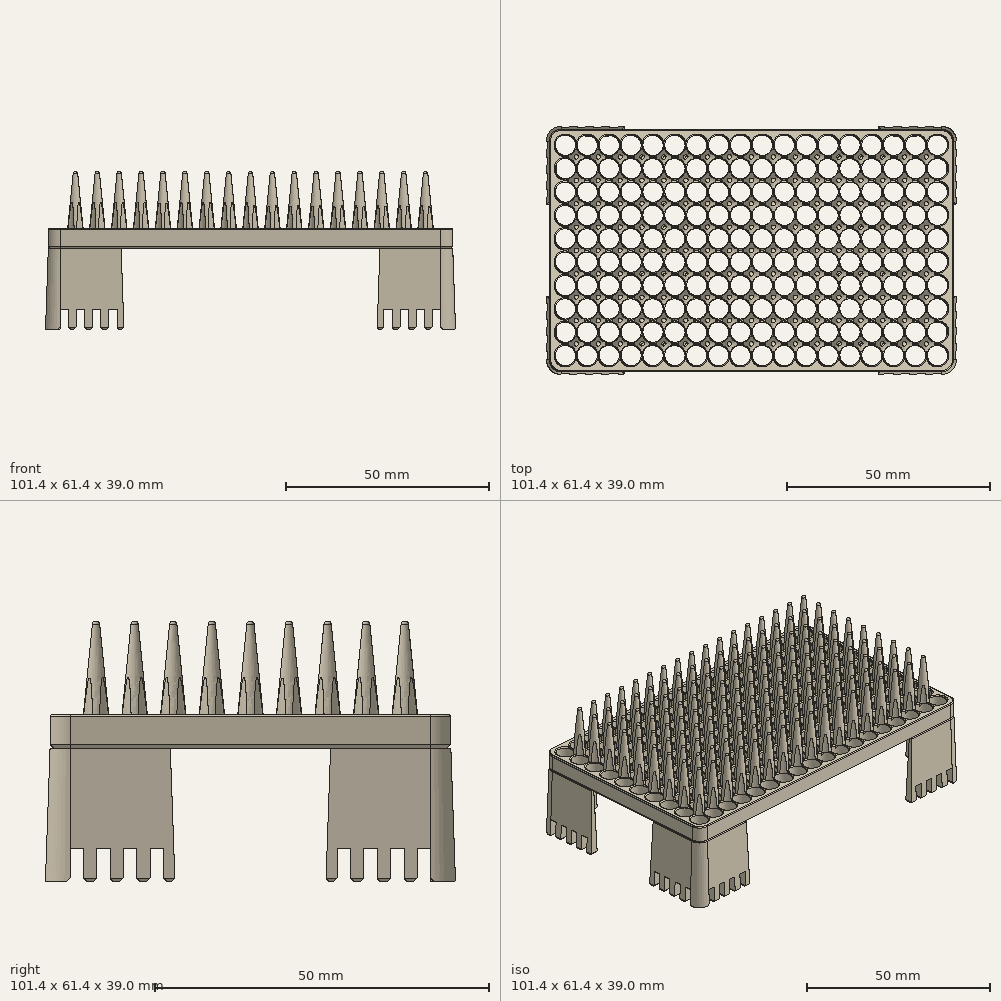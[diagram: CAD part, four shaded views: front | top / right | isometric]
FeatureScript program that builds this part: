
annotation { "Feature Type Name" : "Feature", "Feature Type Description" : "" }
export const myFeature = defineFeature(function(context is Context, id is Id, definition is map)
    precondition{}
    {
        {
            var Q0;
            Q0=qCreatedBy(makeId("Top.planeOp"),FACE);
            var sketch = newSketch(context, id + "F0", { "sketchPlane" : qUnion([Q0])});
            skLineSegment(sketch, "E0.bottom", {"start": v(-47, 30) * mm, "end": v(47, 30) * mm});
            skLineSegment(sketch, "E0.top", {"start": v(-47, -30) * mm, "end": v(47, -30) * mm});
            skLineSegment(sketch, "E0.left", {"start": v(-50, 27) * mm, "end": v(-50, -27) * mm});
            skLineSegment(sketch, "E0.right", {"start": v(50, 27) * mm, "end": v(50, -27) * mm});
            skPoint(sketch, "E1", {"position": v(-46, 26) * mm});
            skPoint(sketch, "E2.0.1.0", {"position": v(-46, 20.22) * mm});
            skPoint(sketch, "E2.0.2.0", {"position": v(-46, 14.45) * mm});
            skPoint(sketch, "E2.0.3.0", {"position": v(-46, 8.67) * mm});
            skPoint(sketch, "E2.0.4.0", {"position": v(-46, 2.9) * mm});
            skPoint(sketch, "E2.0.5.0", {"position": v(-46, -2.89) * mm});
            skPoint(sketch, "E2.0.6.0", {"position": v(-46, -8.66) * mm});
            skPoint(sketch, "E2.0.7.0", {"position": v(-46, -14.44) * mm});
            skPoint(sketch, "E2.0.8.0", {"position": v(-46, -20.22) * mm});
            skPoint(sketch, "E2.0.9.0", {"position": v(-46, -26) * mm});
            skPoint(sketch, "E2.1.0.0", {"position": v(-40.59, 26) * mm});
            skPoint(sketch, "E2.1.1.0", {"position": v(-40.59, 20.22) * mm});
            skPoint(sketch, "E2.1.2.0", {"position": v(-40.59, 14.45) * mm});
            skPoint(sketch, "E2.1.3.0", {"position": v(-40.59, 8.67) * mm});
            skPoint(sketch, "E2.1.4.0", {"position": v(-40.59, 2.9) * mm});
            skPoint(sketch, "E2.1.5.0", {"position": v(-40.59, -2.89) * mm});
            skPoint(sketch, "E2.1.6.0", {"position": v(-40.59, -8.66) * mm});
            skPoint(sketch, "E2.1.7.0", {"position": v(-40.59, -14.44) * mm});
            skPoint(sketch, "E2.1.8.0", {"position": v(-40.59, -20.22) * mm});
            skPoint(sketch, "E2.1.9.0", {"position": v(-40.59, -26) * mm});
            skPoint(sketch, "E2.2.0.0", {"position": v(-35.18, 26) * mm});
            skPoint(sketch, "E2.2.1.0", {"position": v(-35.18, 20.22) * mm});
            skPoint(sketch, "E2.2.2.0", {"position": v(-35.18, 14.45) * mm});
            skPoint(sketch, "E2.2.3.0", {"position": v(-35.18, 8.67) * mm});
            skPoint(sketch, "E2.2.4.0", {"position": v(-35.18, 2.9) * mm});
            skPoint(sketch, "E2.2.5.0", {"position": v(-35.18, -2.89) * mm});
            skPoint(sketch, "E2.2.6.0", {"position": v(-35.18, -8.66) * mm});
            skPoint(sketch, "E2.2.7.0", {"position": v(-35.18, -14.44) * mm});
            skPoint(sketch, "E2.2.8.0", {"position": v(-35.18, -20.22) * mm});
            skPoint(sketch, "E2.2.9.0", {"position": v(-35.18, -26) * mm});
            skPoint(sketch, "E2.3.0.0", {"position": v(-29.76, 26) * mm});
            skPoint(sketch, "E2.3.1.0", {"position": v(-29.76, 20.22) * mm});
            skPoint(sketch, "E2.3.2.0", {"position": v(-29.76, 14.45) * mm});
            skPoint(sketch, "E2.3.3.0", {"position": v(-29.76, 8.67) * mm});
            skPoint(sketch, "E2.3.4.0", {"position": v(-29.76, 2.9) * mm});
            skPoint(sketch, "E2.3.5.0", {"position": v(-29.76, -2.89) * mm});
            skPoint(sketch, "E2.3.6.0", {"position": v(-29.76, -8.66) * mm});
            skPoint(sketch, "E2.3.7.0", {"position": v(-29.76, -14.44) * mm});
            skPoint(sketch, "E2.3.8.0", {"position": v(-29.76, -20.22) * mm});
            skPoint(sketch, "E2.3.9.0", {"position": v(-29.76, -26) * mm});
            skPoint(sketch, "E2.4.0.0", {"position": v(-24.35, 26) * mm});
            skPoint(sketch, "E2.4.1.0", {"position": v(-24.35, 20.22) * mm});
            skPoint(sketch, "E2.4.2.0", {"position": v(-24.35, 14.45) * mm});
            skPoint(sketch, "E2.4.3.0", {"position": v(-24.35, 8.67) * mm});
            skPoint(sketch, "E2.4.4.0", {"position": v(-24.35, 2.9) * mm});
            skPoint(sketch, "E2.4.5.0", {"position": v(-24.35, -2.89) * mm});
            skPoint(sketch, "E2.4.6.0", {"position": v(-24.35, -8.66) * mm});
            skPoint(sketch, "E2.4.7.0", {"position": v(-24.35, -14.44) * mm});
            skPoint(sketch, "E2.4.8.0", {"position": v(-24.35, -20.22) * mm});
            skPoint(sketch, "E2.4.9.0", {"position": v(-24.35, -26) * mm});
            skPoint(sketch, "E2.5.0.0", {"position": v(-18.94, 26) * mm});
            skPoint(sketch, "E2.5.1.0", {"position": v(-18.94, 20.22) * mm});
            skPoint(sketch, "E2.5.2.0", {"position": v(-18.94, 14.45) * mm});
            skPoint(sketch, "E2.5.3.0", {"position": v(-18.94, 8.67) * mm});
            skPoint(sketch, "E2.5.4.0", {"position": v(-18.94, 2.9) * mm});
            skPoint(sketch, "E2.5.5.0", {"position": v(-18.94, -2.89) * mm});
            skPoint(sketch, "E2.5.6.0", {"position": v(-18.94, -8.66) * mm});
            skPoint(sketch, "E2.5.7.0", {"position": v(-18.94, -14.44) * mm});
            skPoint(sketch, "E2.5.8.0", {"position": v(-18.94, -20.22) * mm});
            skPoint(sketch, "E2.5.9.0", {"position": v(-18.94, -26) * mm});
            skPoint(sketch, "E2.6.0.0", {"position": v(-13.53, 26) * mm});
            skPoint(sketch, "E2.6.1.0", {"position": v(-13.53, 20.22) * mm});
            skPoint(sketch, "E2.6.2.0", {"position": v(-13.53, 14.45) * mm});
            skPoint(sketch, "E2.6.3.0", {"position": v(-13.53, 8.67) * mm});
            skPoint(sketch, "E2.6.4.0", {"position": v(-13.53, 2.9) * mm});
            skPoint(sketch, "E2.6.5.0", {"position": v(-13.53, -2.89) * mm});
            skPoint(sketch, "E2.6.6.0", {"position": v(-13.53, -8.66) * mm});
            skPoint(sketch, "E2.6.7.0", {"position": v(-13.53, -14.44) * mm});
            skPoint(sketch, "E2.6.8.0", {"position": v(-13.53, -20.22) * mm});
            skPoint(sketch, "E2.6.9.0", {"position": v(-13.53, -26) * mm});
            skPoint(sketch, "E2.7.0.0", {"position": v(-8.12, 26) * mm});
            skPoint(sketch, "E2.7.1.0", {"position": v(-8.12, 20.22) * mm});
            skPoint(sketch, "E2.7.2.0", {"position": v(-8.12, 14.45) * mm});
            skPoint(sketch, "E2.7.3.0", {"position": v(-8.12, 8.67) * mm});
            skPoint(sketch, "E2.7.4.0", {"position": v(-8.12, 2.9) * mm});
            skPoint(sketch, "E2.7.5.0", {"position": v(-8.12, -2.89) * mm});
            skPoint(sketch, "E2.7.6.0", {"position": v(-8.12, -8.66) * mm});
            skPoint(sketch, "E2.7.7.0", {"position": v(-8.12, -14.44) * mm});
            skPoint(sketch, "E2.7.8.0", {"position": v(-8.12, -20.22) * mm});
            skPoint(sketch, "E2.7.9.0", {"position": v(-8.12, -26) * mm});
            skPoint(sketch, "E2.8.0.0", {"position": v(-2.7, 26) * mm});
            skPoint(sketch, "E2.8.1.0", {"position": v(-2.7, 20.22) * mm});
            skPoint(sketch, "E2.8.2.0", {"position": v(-2.7, 14.45) * mm});
            skPoint(sketch, "E2.8.3.0", {"position": v(-2.7, 8.67) * mm});
            skPoint(sketch, "E2.8.4.0", {"position": v(-2.7, 2.9) * mm});
            skPoint(sketch, "E2.8.5.0", {"position": v(-2.7, -2.89) * mm});
            skPoint(sketch, "E2.8.6.0", {"position": v(-2.7, -8.66) * mm});
            skPoint(sketch, "E2.8.7.0", {"position": v(-2.7, -14.44) * mm});
            skPoint(sketch, "E2.8.8.0", {"position": v(-2.7, -20.22) * mm});
            skPoint(sketch, "E2.8.9.0", {"position": v(-2.7, -26) * mm});
            skPoint(sketch, "E2.9.0.0", {"position": v(2.7, 26) * mm});
            skPoint(sketch, "E2.9.1.0", {"position": v(2.7, 20.22) * mm});
            skPoint(sketch, "E2.9.2.0", {"position": v(2.7, 14.45) * mm});
            skPoint(sketch, "E2.9.3.0", {"position": v(2.7, 8.67) * mm});
            skPoint(sketch, "E2.9.4.0", {"position": v(2.7, 2.9) * mm});
            skPoint(sketch, "E2.9.5.0", {"position": v(2.7, -2.89) * mm});
            skPoint(sketch, "E2.9.6.0", {"position": v(2.7, -8.66) * mm});
            skPoint(sketch, "E2.9.7.0", {"position": v(2.7, -14.44) * mm});
            skPoint(sketch, "E2.9.8.0", {"position": v(2.7, -20.22) * mm});
            skPoint(sketch, "E2.9.9.0", {"position": v(2.7, -26) * mm});
            skPoint(sketch, "E2.10.0.0", {"position": v(8.12, 26) * mm});
            skPoint(sketch, "E2.10.1.0", {"position": v(8.12, 20.22) * mm});
            skPoint(sketch, "E2.10.2.0", {"position": v(8.12, 14.45) * mm});
            skPoint(sketch, "E2.10.3.0", {"position": v(8.12, 8.67) * mm});
            skPoint(sketch, "E2.10.4.0", {"position": v(8.12, 2.9) * mm});
            skPoint(sketch, "E2.10.5.0", {"position": v(8.12, -2.89) * mm});
            skPoint(sketch, "E2.10.6.0", {"position": v(8.12, -8.66) * mm});
            skPoint(sketch, "E2.10.7.0", {"position": v(8.12, -14.44) * mm});
            skPoint(sketch, "E2.10.8.0", {"position": v(8.12, -20.22) * mm});
            skPoint(sketch, "E2.10.9.0", {"position": v(8.12, -26) * mm});
            skPoint(sketch, "E2.11.0.0", {"position": v(13.53, 26) * mm});
            skPoint(sketch, "E2.11.1.0", {"position": v(13.53, 20.22) * mm});
            skPoint(sketch, "E2.11.2.0", {"position": v(13.53, 14.45) * mm});
            skPoint(sketch, "E2.11.3.0", {"position": v(13.53, 8.67) * mm});
            skPoint(sketch, "E2.11.4.0", {"position": v(13.53, 2.9) * mm});
            skPoint(sketch, "E2.11.5.0", {"position": v(13.53, -2.89) * mm});
            skPoint(sketch, "E2.11.6.0", {"position": v(13.53, -8.66) * mm});
            skPoint(sketch, "E2.11.7.0", {"position": v(13.53, -14.44) * mm});
            skPoint(sketch, "E2.11.8.0", {"position": v(13.53, -20.22) * mm});
            skPoint(sketch, "E2.11.9.0", {"position": v(13.53, -26) * mm});
            skPoint(sketch, "E2.12.0.0", {"position": v(18.94, 26) * mm});
            skPoint(sketch, "E2.12.1.0", {"position": v(18.94, 20.22) * mm});
            skPoint(sketch, "E2.12.2.0", {"position": v(18.94, 14.45) * mm});
            skPoint(sketch, "E2.12.3.0", {"position": v(18.94, 8.67) * mm});
            skPoint(sketch, "E2.12.4.0", {"position": v(18.94, 2.9) * mm});
            skPoint(sketch, "E2.12.5.0", {"position": v(18.94, -2.89) * mm});
            skPoint(sketch, "E2.12.6.0", {"position": v(18.94, -8.66) * mm});
            skPoint(sketch, "E2.12.7.0", {"position": v(18.94, -14.44) * mm});
            skPoint(sketch, "E2.12.8.0", {"position": v(18.94, -20.22) * mm});
            skPoint(sketch, "E2.12.9.0", {"position": v(18.94, -26) * mm});
            skPoint(sketch, "E2.13.0.0", {"position": v(24.36, 26) * mm});
            skPoint(sketch, "E2.13.1.0", {"position": v(24.36, 20.22) * mm});
            skPoint(sketch, "E2.13.2.0", {"position": v(24.36, 14.45) * mm});
            skPoint(sketch, "E2.13.3.0", {"position": v(24.36, 8.67) * mm});
            skPoint(sketch, "E2.13.4.0", {"position": v(24.36, 2.9) * mm});
            skPoint(sketch, "E2.13.5.0", {"position": v(24.36, -2.89) * mm});
            skPoint(sketch, "E2.13.6.0", {"position": v(24.36, -8.66) * mm});
            skPoint(sketch, "E2.13.7.0", {"position": v(24.36, -14.44) * mm});
            skPoint(sketch, "E2.13.8.0", {"position": v(24.36, -20.22) * mm});
            skPoint(sketch, "E2.13.9.0", {"position": v(24.36, -26) * mm});
            skPoint(sketch, "E2.14.0.0", {"position": v(29.77, 26) * mm});
            skPoint(sketch, "E2.14.1.0", {"position": v(29.77, 20.22) * mm});
            skPoint(sketch, "E2.14.2.0", {"position": v(29.77, 14.45) * mm});
            skPoint(sketch, "E2.14.3.0", {"position": v(29.77, 8.67) * mm});
            skPoint(sketch, "E2.14.4.0", {"position": v(29.77, 2.9) * mm});
            skPoint(sketch, "E2.14.5.0", {"position": v(29.77, -2.89) * mm});
            skPoint(sketch, "E2.14.6.0", {"position": v(29.77, -8.66) * mm});
            skPoint(sketch, "E2.14.7.0", {"position": v(29.77, -14.44) * mm});
            skPoint(sketch, "E2.14.8.0", {"position": v(29.77, -20.22) * mm});
            skPoint(sketch, "E2.14.9.0", {"position": v(29.77, -26) * mm});
            skPoint(sketch, "E2.15.0.0", {"position": v(35.18, 26) * mm});
            skPoint(sketch, "E2.15.1.0", {"position": v(35.18, 20.22) * mm});
            skPoint(sketch, "E2.15.2.0", {"position": v(35.18, 14.45) * mm});
            skPoint(sketch, "E2.15.3.0", {"position": v(35.18, 8.67) * mm});
            skPoint(sketch, "E2.15.4.0", {"position": v(35.18, 2.9) * mm});
            skPoint(sketch, "E2.15.5.0", {"position": v(35.18, -2.89) * mm});
            skPoint(sketch, "E2.15.6.0", {"position": v(35.18, -8.66) * mm});
            skPoint(sketch, "E2.15.7.0", {"position": v(35.18, -14.44) * mm});
            skPoint(sketch, "E2.15.8.0", {"position": v(35.18, -20.22) * mm});
            skPoint(sketch, "E2.15.9.0", {"position": v(35.18, -26) * mm});
            skPoint(sketch, "E2.16.0.0", {"position": v(40.6, 26) * mm});
            skPoint(sketch, "E2.16.1.0", {"position": v(40.6, 20.22) * mm});
            skPoint(sketch, "E2.16.2.0", {"position": v(40.6, 14.45) * mm});
            skPoint(sketch, "E2.16.3.0", {"position": v(40.6, 8.67) * mm});
            skPoint(sketch, "E2.16.4.0", {"position": v(40.6, 2.9) * mm});
            skPoint(sketch, "E2.16.5.0", {"position": v(40.6, -2.89) * mm});
            skPoint(sketch, "E2.16.6.0", {"position": v(40.6, -8.66) * mm});
            skPoint(sketch, "E2.16.7.0", {"position": v(40.6, -14.44) * mm});
            skPoint(sketch, "E2.16.8.0", {"position": v(40.6, -20.22) * mm});
            skPoint(sketch, "E2.16.9.0", {"position": v(40.6, -26) * mm});
            skPoint(sketch, "E2.17.0.0", {"position": v(46, 26) * mm});
            skPoint(sketch, "E2.17.1.0", {"position": v(46, 20.22) * mm});
            skPoint(sketch, "E2.17.2.0", {"position": v(46, 14.45) * mm});
            skPoint(sketch, "E2.17.3.0", {"position": v(46, 8.67) * mm});
            skPoint(sketch, "E2.17.4.0", {"position": v(46, 2.9) * mm});
            skPoint(sketch, "E2.17.5.0", {"position": v(46, -2.89) * mm});
            skPoint(sketch, "E2.17.6.0", {"position": v(46, -8.66) * mm});
            skPoint(sketch, "E2.17.7.0", {"position": v(46, -14.44) * mm});
            skPoint(sketch, "E2.17.8.0", {"position": v(46, -20.22) * mm});
            skPoint(sketch, "E2.17.9.0", {"position": v(46, -26) * mm});
            skLineSegment(sketch, "E2.direction1", {"start": v(-46, 26) * mm, "end": v(-40.59, 26) * mm, "construction": true});
            skLineSegment(sketch, "E2.direction2", {"start": v(-46, 26) * mm, "end": v(-46, 20.22) * mm, "construction": true});
            skPoint(sketch, "E3.visualSharp", {"position": v(-50, 30) * mm});
            skArc(sketch, "E3.filletArc", {"start": v(-47, 30) * mm, "mid": v(-49.12, 29.12) * mm, "end": v(-50, 27) * mm});
            skPoint(sketch, "E4.visualSharp", {"position": v(-50, -30) * mm});
            skArc(sketch, "E4.filletArc", {"start": v(-50, -27) * mm, "mid": v(-49.12, -29.12) * mm, "end": v(-47, -30) * mm});
            skPoint(sketch, "E5.visualSharp", {"position": v(50, 30) * mm});
            skArc(sketch, "E5.filletArc", {"start": v(50, 27) * mm, "mid": v(49.12, 29.12) * mm, "end": v(47, 30) * mm});
            skPoint(sketch, "E6.visualSharp", {"position": v(50, -30) * mm});
            skArc(sketch, "E6.filletArc", {"start": v(47, -30) * mm, "mid": v(49.12, -29.12) * mm, "end": v(50, -27) * mm});
            skCircle(sketch, "E7", {"center": v(-46, 26) * mm, "radius": 2.5 * mm});
            skCircle(sketch, "E8", {"center": v(-40.59, 26) * mm, "radius": 2.5 * mm});
            skCircle(sketch, "E9", {"center": v(-35.18, 26) * mm, "radius": 2.5 * mm});
            skCircle(sketch, "E10", {"center": v(-29.76, 26) * mm, "radius": 2.5 * mm});
            skCircle(sketch, "E11", {"center": v(-24.35, 26) * mm, "radius": 2.5 * mm});
            skCircle(sketch, "E12", {"center": v(-18.94, 26) * mm, "radius": 2.5 * mm});
            skCircle(sketch, "E13", {"center": v(-18.94, 20.22) * mm, "radius": 2.5 * mm});
            skCircle(sketch, "E14", {"center": v(-24.35, 20.22) * mm, "radius": 2.5 * mm});
            skCircle(sketch, "E15", {"center": v(-29.76, 20.22) * mm, "radius": 2.5 * mm});
            skCircle(sketch, "E16", {"center": v(-35.18, 20.22) * mm, "radius": 2.5 * mm});
            skCircle(sketch, "E17", {"center": v(-40.59, 20.22) * mm, "radius": 2.5 * mm});
            skCircle(sketch, "E18", {"center": v(-40.59, 14.45) * mm, "radius": 2.5 * mm});
            skCircle(sketch, "E19", {"center": v(-35.18, 14.45) * mm, "radius": 2.5 * mm});
            skCircle(sketch, "E20", {"center": v(-29.76, 14.45) * mm, "radius": 2.5 * mm});
            skCircle(sketch, "E21", {"center": v(-24.35, 14.45) * mm, "radius": 2.5 * mm});
            skCircle(sketch, "E22", {"center": v(-18.94, 14.45) * mm, "radius": 2.5 * mm});
            skCircle(sketch, "E23", {"center": v(-13.53, 26) * mm, "radius": 2.5 * mm});
            skCircle(sketch, "E24", {"center": v(-13.53, 20.22) * mm, "radius": 2.5 * mm});
            skCircle(sketch, "E25", {"center": v(-13.53, 14.45) * mm, "radius": 2.5 * mm});
            skCircle(sketch, "E26", {"center": v(-46, 20.22) * mm, "radius": 2.5 * mm});
            skCircle(sketch, "E27", {"center": v(-46, 14.45) * mm, "radius": 2.5 * mm});
            skCircle(sketch, "E28", {"center": v(-46, 8.67) * mm, "radius": 2.5 * mm});
            skCircle(sketch, "E29", {"center": v(-40.59, 8.67) * mm, "radius": 2.5 * mm});
            skCircle(sketch, "E30", {"center": v(-35.18, 8.67) * mm, "radius": 2.5 * mm});
            skCircle(sketch, "E31", {"center": v(-29.76, 8.67) * mm, "radius": 2.5 * mm});
            skCircle(sketch, "E32", {"center": v(-24.35, 8.67) * mm, "radius": 2.5 * mm});
            skCircle(sketch, "E33", {"center": v(-18.94, 8.67) * mm, "radius": 2.5 * mm});
            skCircle(sketch, "E34", {"center": v(-13.53, 8.67) * mm, "radius": 2.5 * mm});
            skCircle(sketch, "E35", {"center": v(-13.53, 2.9) * mm, "radius": 2.5 * mm});
            skCircle(sketch, "E36", {"center": v(-18.94, 2.9) * mm, "radius": 2.5 * mm});
            skCircle(sketch, "E37", {"center": v(-24.35, 2.9) * mm, "radius": 2.5 * mm});
            skCircle(sketch, "E38", {"center": v(-29.76, 2.9) * mm, "radius": 2.5 * mm});
            skCircle(sketch, "E39", {"center": v(-35.18, 2.9) * mm, "radius": 2.5 * mm});
            skCircle(sketch, "E40", {"center": v(-40.59, 2.9) * mm, "radius": 2.5 * mm});
            skCircle(sketch, "E41", {"center": v(-46, 2.9) * mm, "radius": 2.5 * mm});
            skCircle(sketch, "E42", {"center": v(-8.12, 26) * mm, "radius": 2.5 * mm});
            skCircle(sketch, "E43", {"center": v(-2.7, 26) * mm, "radius": 2.5 * mm});
            skCircle(sketch, "E44", {"center": v(-8.12, 20.22) * mm, "radius": 2.5 * mm});
            skCircle(sketch, "E45", {"center": v(-8.12, 14.45) * mm, "radius": 2.5 * mm});
            skCircle(sketch, "E46", {"center": v(-2.7, 20.22) * mm, "radius": 2.5 * mm});
            skCircle(sketch, "E47", {"center": v(-2.7, 14.45) * mm, "radius": 2.5 * mm});
            skCircle(sketch, "E48", {"center": v(2.7, 26) * mm, "radius": 2.5 * mm});
            skCircle(sketch, "E49", {"center": v(2.7, 20.22) * mm, "radius": 2.5 * mm});
            skCircle(sketch, "E50", {"center": v(8.12, 26) * mm, "radius": 2.5 * mm});
            skCircle(sketch, "E51", {"center": v(13.53, 26) * mm, "radius": 2.5 * mm});
            skCircle(sketch, "E52", {"center": v(18.94, 26) * mm, "radius": 2.5 * mm});
            skCircle(sketch, "E53", {"center": v(24.36, 26) * mm, "radius": 2.5 * mm});
            skCircle(sketch, "E54", {"center": v(29.77, 26) * mm, "radius": 2.5 * mm});
            skCircle(sketch, "E55", {"center": v(35.18, 26) * mm, "radius": 2.5 * mm});
            skCircle(sketch, "E56", {"center": v(40.6, 26) * mm, "radius": 2.5 * mm});
            skCircle(sketch, "E57", {"center": v(46, 26) * mm, "radius": 2.5 * mm});
            skCircle(sketch, "E58", {"center": v(46, 20.22) * mm, "radius": 2.5 * mm});
            skCircle(sketch, "E59", {"center": v(40.6, 20.22) * mm, "radius": 2.5 * mm});
            skCircle(sketch, "E60", {"center": v(35.18, 20.22) * mm, "radius": 2.5 * mm});
            skCircle(sketch, "E61", {"center": v(29.77, 20.22) * mm, "radius": 2.5 * mm});
            skCircle(sketch, "E62", {"center": v(24.36, 20.22) * mm, "radius": 2.5 * mm});
            skCircle(sketch, "E63", {"center": v(18.94, 20.22) * mm, "radius": 2.5 * mm});
            skCircle(sketch, "E64", {"center": v(13.53, 20.22) * mm, "radius": 2.5 * mm});
            skCircle(sketch, "E65", {"center": v(8.12, 20.22) * mm, "radius": 2.5 * mm});
            skCircle(sketch, "E66", {"center": v(2.7, 14.45) * mm, "radius": 2.5 * mm});
            skCircle(sketch, "E67", {"center": v(8.12, 14.45) * mm, "radius": 2.5 * mm});
            skCircle(sketch, "E68", {"center": v(13.53, 14.45) * mm, "radius": 2.5 * mm});
            skCircle(sketch, "E69", {"center": v(18.94, 14.45) * mm, "radius": 2.5 * mm});
            skCircle(sketch, "E70", {"center": v(24.36, 14.45) * mm, "radius": 2.5 * mm});
            skCircle(sketch, "E71", {"center": v(29.77, 14.45) * mm, "radius": 2.5 * mm});
            skCircle(sketch, "E72", {"center": v(35.18, 14.45) * mm, "radius": 2.5 * mm});
            skCircle(sketch, "E73", {"center": v(40.6, 14.45) * mm, "radius": 2.5 * mm});
            skCircle(sketch, "E74", {"center": v(46, 14.45) * mm, "radius": 2.5 * mm});
            skCircle(sketch, "E75", {"center": v(46, 8.67) * mm, "radius": 2.5 * mm});
            skCircle(sketch, "E76", {"center": v(40.6, 8.67) * mm, "radius": 2.5 * mm});
            skCircle(sketch, "E77", {"center": v(35.18, 8.67) * mm, "radius": 2.5 * mm});
            skCircle(sketch, "E78", {"center": v(29.77, 8.67) * mm, "radius": 2.5 * mm});
            skCircle(sketch, "E79", {"center": v(24.36, 8.67) * mm, "radius": 2.5 * mm});
            skCircle(sketch, "E80", {"center": v(18.94, 8.67) * mm, "radius": 2.5 * mm});
            skCircle(sketch, "E81", {"center": v(13.53, 8.67) * mm, "radius": 2.5 * mm});
            skCircle(sketch, "E82", {"center": v(8.12, 8.67) * mm, "radius": 2.5 * mm});
            skCircle(sketch, "E83", {"center": v(2.7, 8.67) * mm, "radius": 2.5 * mm});
            skCircle(sketch, "E84", {"center": v(-2.7, 8.67) * mm, "radius": 2.5 * mm});
            skCircle(sketch, "E85", {"center": v(-8.12, 8.67) * mm, "radius": 2.5 * mm});
            skCircle(sketch, "E86", {"center": v(-8.12, 2.9) * mm, "radius": 2.5 * mm});
            skCircle(sketch, "E87", {"center": v(-2.7, 2.9) * mm, "radius": 2.5 * mm});
            skCircle(sketch, "E88", {"center": v(2.7, 2.9) * mm, "radius": 2.5 * mm});
            skCircle(sketch, "E89", {"center": v(8.12, 2.9) * mm, "radius": 2.5 * mm});
            skCircle(sketch, "E90", {"center": v(13.53, 2.9) * mm, "radius": 2.5 * mm});
            skCircle(sketch, "E91", {"center": v(18.94, 2.9) * mm, "radius": 2.5 * mm});
            skCircle(sketch, "E92", {"center": v(24.36, 2.9) * mm, "radius": 2.5 * mm});
            skCircle(sketch, "E93", {"center": v(29.77, 2.9) * mm, "radius": 2.5 * mm});
            skCircle(sketch, "E94", {"center": v(35.18, 2.9) * mm, "radius": 2.5 * mm});
            skCircle(sketch, "E95", {"center": v(40.6, 2.9) * mm, "radius": 2.5 * mm});
            skCircle(sketch, "E96", {"center": v(46, 2.9) * mm, "radius": 2.5 * mm});
            skCircle(sketch, "E97", {"center": v(-46, -2.89) * mm, "radius": 2.5 * mm});
            skCircle(sketch, "E98", {"center": v(-40.59, -2.89) * mm, "radius": 2.5 * mm});
            skCircle(sketch, "E99", {"center": v(-35.18, -2.89) * mm, "radius": 2.5 * mm});
            skCircle(sketch, "E100", {"center": v(-29.76, -2.89) * mm, "radius": 2.5 * mm});
            skCircle(sketch, "E101", {"center": v(-24.35, -2.89) * mm, "radius": 2.5 * mm});
            skCircle(sketch, "E102", {"center": v(-18.94, -2.89) * mm, "radius": 2.5 * mm});
            skCircle(sketch, "E103", {"center": v(-13.53, -2.89) * mm, "radius": 2.5 * mm});
            skCircle(sketch, "E104", {"center": v(-8.12, -2.89) * mm, "radius": 2.5 * mm});
            skCircle(sketch, "E105", {"center": v(-2.7, -2.89) * mm, "radius": 2.5 * mm});
            skCircle(sketch, "E106", {"center": v(-2.7, -8.66) * mm, "radius": 2.5 * mm});
            skCircle(sketch, "E107", {"center": v(-24.35, -8.66) * mm, "radius": 2.5 * mm});
            skCircle(sketch, "E108", {"center": v(-18.94, -8.66) * mm, "radius": 2.5 * mm});
            skCircle(sketch, "E109", {"center": v(-13.53, -8.66) * mm, "radius": 2.5 * mm});
            skCircle(sketch, "E110", {"center": v(-8.12, -8.66) * mm, "radius": 2.5 * mm});
            skCircle(sketch, "E111", {"center": v(-35.18, -8.66) * mm, "radius": 2.5 * mm});
            skCircle(sketch, "E112", {"center": v(-29.76, -8.66) * mm, "radius": 2.5 * mm});
            skCircle(sketch, "E113", {"center": v(-35.18, -14.44) * mm, "radius": 2.5 * mm});
            skCircle(sketch, "E114", {"center": v(-29.76, -14.44) * mm, "radius": 2.5 * mm});
            skCircle(sketch, "E115", {"center": v(-24.35, -14.44) * mm, "radius": 2.5 * mm});
            skCircle(sketch, "E116", {"center": v(-18.94, -14.44) * mm, "radius": 2.5 * mm});
            skCircle(sketch, "E117", {"center": v(-13.53, -14.44) * mm, "radius": 2.5 * mm});
            skCircle(sketch, "E118", {"center": v(-8.12, -14.44) * mm, "radius": 2.5 * mm});
            skCircle(sketch, "E119", {"center": v(-2.7, -14.44) * mm, "radius": 2.5 * mm});
            skCircle(sketch, "E120", {"center": v(-46, -8.66) * mm, "radius": 2.5 * mm});
            skCircle(sketch, "E121", {"center": v(-40.59, -8.66) * mm, "radius": 2.5 * mm});
            skCircle(sketch, "E122", {"center": v(-46, -14.44) * mm, "radius": 2.5 * mm});
            skCircle(sketch, "E123", {"center": v(-40.59, -14.44) * mm, "radius": 2.5 * mm});
            skCircle(sketch, "E124", {"center": v(-46, -20.22) * mm, "radius": 2.5 * mm});
            skCircle(sketch, "E125", {"center": v(-40.59, -20.22) * mm, "radius": 2.5 * mm});
            skCircle(sketch, "E126", {"center": v(-46, -26) * mm, "radius": 2.5 * mm});
            skCircle(sketch, "E127", {"center": v(-40.59, -26) * mm, "radius": 2.5 * mm});
            skCircle(sketch, "E128", {"center": v(-35.18, -26) * mm, "radius": 2.5 * mm});
            skCircle(sketch, "E129", {"center": v(-35.18, -20.22) * mm, "radius": 2.5 * mm});
            skCircle(sketch, "E130", {"center": v(-29.76, -20.22) * mm, "radius": 2.5 * mm});
            skCircle(sketch, "E131", {"center": v(-29.76, -26) * mm, "radius": 2.5 * mm});
            skCircle(sketch, "E132", {"center": v(-24.35, -26) * mm, "radius": 2.5 * mm});
            skCircle(sketch, "E133", {"center": v(-24.35, -20.22) * mm, "radius": 2.5 * mm});
            skCircle(sketch, "E134", {"center": v(-18.94, -20.22) * mm, "radius": 2.5 * mm});
            skCircle(sketch, "E135", {"center": v(-18.94, -26) * mm, "radius": 2.5 * mm});
            skCircle(sketch, "E136", {"center": v(-13.53, -20.22) * mm, "radius": 2.5 * mm});
            skCircle(sketch, "E137", {"center": v(-8.12, -20.22) * mm, "radius": 2.5 * mm});
            skCircle(sketch, "E138", {"center": v(-2.7, -20.22) * mm, "radius": 2.5 * mm});
            skCircle(sketch, "E139", {"center": v(-2.7, -26) * mm, "radius": 2.5 * mm});
            skCircle(sketch, "E140", {"center": v(-8.12, -26) * mm, "radius": 2.5 * mm});
            skCircle(sketch, "E141", {"center": v(-13.53, -26) * mm, "radius": 2.5 * mm});
            skCircle(sketch, "E142", {"center": v(2.7, -2.89) * mm, "radius": 2.5 * mm});
            skCircle(sketch, "E143", {"center": v(8.12, -2.89) * mm, "radius": 2.5 * mm});
            skCircle(sketch, "E144", {"center": v(13.53, -2.89) * mm, "radius": 2.5 * mm});
            skCircle(sketch, "E145", {"center": v(18.94, -2.89) * mm, "radius": 2.5 * mm});
            skCircle(sketch, "E146", {"center": v(24.36, -2.89) * mm, "radius": 2.5 * mm});
            skCircle(sketch, "E147", {"center": v(29.77, -2.89) * mm, "radius": 2.5 * mm});
            skCircle(sketch, "E148", {"center": v(35.18, -2.89) * mm, "radius": 2.5 * mm});
            skCircle(sketch, "E149", {"center": v(40.6, -2.89) * mm, "radius": 2.5 * mm});
            skCircle(sketch, "E150", {"center": v(46, -2.89) * mm, "radius": 2.5 * mm});
            skCircle(sketch, "E151", {"center": v(46, -8.66) * mm, "radius": 2.5 * mm});
            skCircle(sketch, "E152", {"center": v(40.6, -8.66) * mm, "radius": 2.5 * mm});
            skCircle(sketch, "E153", {"center": v(35.18, -8.66) * mm, "radius": 2.5 * mm});
            skCircle(sketch, "E154", {"center": v(29.77, -8.66) * mm, "radius": 2.5 * mm});
            skCircle(sketch, "E155", {"center": v(24.36, -8.66) * mm, "radius": 2.5 * mm});
            skCircle(sketch, "E156", {"center": v(18.94, -8.66) * mm, "radius": 2.5 * mm});
            skCircle(sketch, "E157", {"center": v(13.53, -8.66) * mm, "radius": 2.5 * mm});
            skCircle(sketch, "E158", {"center": v(8.12, -8.66) * mm, "radius": 2.5 * mm});
            skCircle(sketch, "E159", {"center": v(2.7, -8.66) * mm, "radius": 2.5 * mm});
            skCircle(sketch, "E160", {"center": v(2.7, -14.44) * mm, "radius": 2.5 * mm});
            skCircle(sketch, "E161", {"center": v(8.12, -14.44) * mm, "radius": 2.5 * mm});
            skCircle(sketch, "E162", {"center": v(13.53, -14.44) * mm, "radius": 2.5 * mm});
            skCircle(sketch, "E163", {"center": v(18.94, -14.44) * mm, "radius": 2.5 * mm});
            skCircle(sketch, "E164", {"center": v(24.36, -14.44) * mm, "radius": 2.5 * mm});
            skCircle(sketch, "E165", {"center": v(29.77, -14.44) * mm, "radius": 2.5 * mm});
            skCircle(sketch, "E166", {"center": v(35.18, -14.44) * mm, "radius": 2.5 * mm});
            skCircle(sketch, "E167", {"center": v(40.6, -14.44) * mm, "radius": 2.5 * mm});
            skCircle(sketch, "E168", {"center": v(46, -14.44) * mm, "radius": 2.5 * mm});
            skCircle(sketch, "E169", {"center": v(2.7, -20.22) * mm, "radius": 2.5 * mm});
            skCircle(sketch, "E170", {"center": v(8.12, -20.22) * mm, "radius": 2.5 * mm});
            skCircle(sketch, "E171", {"center": v(13.53, -20.22) * mm, "radius": 2.5 * mm});
            skCircle(sketch, "E172", {"center": v(18.94, -20.22) * mm, "radius": 2.5 * mm});
            skCircle(sketch, "E173", {"center": v(24.36, -20.22) * mm, "radius": 2.5 * mm});
            skCircle(sketch, "E174", {"center": v(29.77, -20.22) * mm, "radius": 2.5 * mm});
            skCircle(sketch, "E175", {"center": v(35.18, -20.22) * mm, "radius": 2.5 * mm});
            skCircle(sketch, "E176", {"center": v(40.6, -20.22) * mm, "radius": 2.5 * mm});
            skCircle(sketch, "E177", {"center": v(46, -20.22) * mm, "radius": 2.5 * mm});
            skCircle(sketch, "E178", {"center": v(2.7, -26) * mm, "radius": 2.5 * mm});
            skCircle(sketch, "E179", {"center": v(8.12, -26) * mm, "radius": 2.5 * mm});
            skCircle(sketch, "E180", {"center": v(13.53, -26) * mm, "radius": 2.5 * mm});
            skCircle(sketch, "E181", {"center": v(18.94, -26) * mm, "radius": 2.5 * mm});
            skCircle(sketch, "E182", {"center": v(24.36, -26) * mm, "radius": 2.5 * mm});
            skCircle(sketch, "E183", {"center": v(29.77, -26) * mm, "radius": 2.5 * mm});
            skCircle(sketch, "E184", {"center": v(35.18, -26) * mm, "radius": 2.5 * mm});
            skCircle(sketch, "E185", {"center": v(40.6, -26) * mm, "radius": 2.5 * mm});
            skCircle(sketch, "E186", {"center": v(46, -26) * mm, "radius": 2.5 * mm});
            skSolve(sketch);
        }
        {
            var Q0;
            Q0=makeQuery(id+"F0.imprint","IMPRINT",FACE,{"disambiguationData":[TD([[makeQuery(id+"F0.imprint","IMPRINT",EDGE,{"derivedFrom":sQuery(id+"F0.wireOp",EDGE,"E0.bottom")}),-1.0]])]});
            var sketch = newSketch(context, id + "F1", { "sketchPlane" : qUnion([Q0])});
            skLineSegment(sketch, "E187", {"start": v(-46, 20.22) * mm, "end": v(-40.59, 26) * mm, "construction": true});
            skLineSegment(sketch, "E188", {"start": v(-46, 26) * mm, "end": v(-40.59, 20.22) * mm, "construction": true});
            skPoint(sketch, "E189", {"position": v(-43.3, 23.11) * mm});
            skLineSegment(sketch, "E190", {"start": v(-46, -20.22) * mm, "end": v(-40.59, -26) * mm, "construction": true});
            skLineSegment(sketch, "E191", {"start": v(-40.59, -20.22) * mm, "end": v(-46, -26) * mm, "construction": true});
            skPoint(sketch, "E192", {"position": v(-43.3, -23.1) * mm});
            skLineSegment(sketch, "E193", {"start": v(40.6, 26) * mm, "end": v(46, 20.22) * mm, "construction": true});
            skLineSegment(sketch, "E194", {"start": v(46, 26) * mm, "end": v(40.6, 20.22) * mm, "construction": true});
            skLineSegment(sketch, "E195", {"start": v(40.6, -20.22) * mm, "end": v(46, -26) * mm, "construction": true});
            skLineSegment(sketch, "E196", {"start": v(46, -20.22) * mm, "end": v(40.6, -26) * mm, "construction": true});
            skPoint(sketch, "E197", {"position": v(43.3, 23.11) * mm});
            skPoint(sketch, "E198", {"position": v(43.3, -23.1) * mm});
            skCircle(sketch, "E199", {"center": v(-43.3, 23.11) * mm, "radius": 2 * mm});
            skLineSegment(sketch, "E200", {"start": v(-40.59, 26) * mm, "end": v(-35.18, 20.22) * mm, "construction": true});
            skLineSegment(sketch, "E201", {"start": v(-35.18, 26) * mm, "end": v(-40.59, 20.22) * mm, "construction": true});
            skPoint(sketch, "E202", {"position": v(-37.88, 23.11) * mm});
            skLineSegment(sketch, "E203", {"start": v(-46, 20.22) * mm, "end": v(-40.59, 14.45) * mm, "construction": true});
            skLineSegment(sketch, "E204", {"start": v(-40.59, 20.22) * mm, "end": v(-46, 14.45) * mm, "construction": true});
            skPoint(sketch, "E205", {"position": v(-43.3, 17.33) * mm});
            skCircle(sketch, "E206.0.1.0", {"center": v(-43.3, 17.33) * mm, "radius": 2 * mm});
            skCircle(sketch, "E206.0.2.0", {"center": v(-43.3, 11.56) * mm, "radius": 2 * mm});
            skCircle(sketch, "E206.0.3.0", {"center": v(-43.3, 5.78) * mm, "radius": 2 * mm});
            skCircle(sketch, "E206.0.4.0", {"center": v(-43.3, 0) * mm, "radius": 2 * mm});
            skCircle(sketch, "E206.0.5.0", {"center": v(-43.3, -5.77) * mm, "radius": 2 * mm});
            skCircle(sketch, "E206.0.6.0", {"center": v(-43.3, -11.55) * mm, "radius": 2 * mm});
            skCircle(sketch, "E206.0.7.0", {"center": v(-43.3, -17.33) * mm, "radius": 2 * mm});
            skCircle(sketch, "E206.0.8.0", {"center": v(-43.3, -23.1) * mm, "radius": 2 * mm});
            skCircle(sketch, "E206.1.0.0", {"center": v(-37.88, 23.11) * mm, "radius": 2 * mm});
            skCircle(sketch, "E206.1.1.0", {"center": v(-37.88, 17.33) * mm, "radius": 2 * mm});
            skCircle(sketch, "E206.1.2.0", {"center": v(-37.88, 11.56) * mm, "radius": 2 * mm});
            skCircle(sketch, "E206.1.3.0", {"center": v(-37.88, 5.78) * mm, "radius": 2 * mm});
            skCircle(sketch, "E206.1.4.0", {"center": v(-37.88, 0) * mm, "radius": 2 * mm});
            skCircle(sketch, "E206.1.5.0", {"center": v(-37.88, -5.77) * mm, "radius": 2 * mm});
            skCircle(sketch, "E206.1.6.0", {"center": v(-37.88, -11.55) * mm, "radius": 2 * mm});
            skCircle(sketch, "E206.1.7.0", {"center": v(-37.88, -17.33) * mm, "radius": 2 * mm});
            skCircle(sketch, "E206.1.8.0", {"center": v(-37.88, -23.1) * mm, "radius": 2 * mm});
            skCircle(sketch, "E206.2.0.0", {"center": v(-32.47, 23.11) * mm, "radius": 2 * mm});
            skCircle(sketch, "E206.2.1.0", {"center": v(-32.47, 17.33) * mm, "radius": 2 * mm});
            skCircle(sketch, "E206.2.2.0", {"center": v(-32.47, 11.56) * mm, "radius": 2 * mm});
            skCircle(sketch, "E206.2.3.0", {"center": v(-32.47, 5.78) * mm, "radius": 2 * mm});
            skCircle(sketch, "E206.2.4.0", {"center": v(-32.47, 0) * mm, "radius": 2 * mm});
            skCircle(sketch, "E206.2.5.0", {"center": v(-32.47, -5.77) * mm, "radius": 2 * mm});
            skCircle(sketch, "E206.2.6.0", {"center": v(-32.47, -11.55) * mm, "radius": 2 * mm});
            skCircle(sketch, "E206.2.7.0", {"center": v(-32.47, -17.33) * mm, "radius": 2 * mm});
            skCircle(sketch, "E206.2.8.0", {"center": v(-32.47, -23.1) * mm, "radius": 2 * mm});
            skCircle(sketch, "E206.3.0.0", {"center": v(-27.06, 23.11) * mm, "radius": 2 * mm});
            skCircle(sketch, "E206.3.1.0", {"center": v(-27.06, 17.33) * mm, "radius": 2 * mm});
            skCircle(sketch, "E206.3.2.0", {"center": v(-27.06, 11.56) * mm, "radius": 2 * mm});
            skCircle(sketch, "E206.3.3.0", {"center": v(-27.06, 5.78) * mm, "radius": 2 * mm});
            skCircle(sketch, "E206.3.4.0", {"center": v(-27.06, 0) * mm, "radius": 2 * mm});
            skCircle(sketch, "E206.3.5.0", {"center": v(-27.06, -5.77) * mm, "radius": 2 * mm});
            skCircle(sketch, "E206.3.6.0", {"center": v(-27.06, -11.55) * mm, "radius": 2 * mm});
            skCircle(sketch, "E206.3.7.0", {"center": v(-27.06, -17.33) * mm, "radius": 2 * mm});
            skCircle(sketch, "E206.3.8.0", {"center": v(-27.06, -23.1) * mm, "radius": 2 * mm});
            skCircle(sketch, "E206.4.0.0", {"center": v(-21.65, 23.11) * mm, "radius": 2 * mm});
            skCircle(sketch, "E206.4.1.0", {"center": v(-21.65, 17.33) * mm, "radius": 2 * mm});
            skCircle(sketch, "E206.4.2.0", {"center": v(-21.65, 11.56) * mm, "radius": 2 * mm});
            skCircle(sketch, "E206.4.3.0", {"center": v(-21.65, 5.78) * mm, "radius": 2 * mm});
            skCircle(sketch, "E206.4.4.0", {"center": v(-21.65, 0) * mm, "radius": 2 * mm});
            skCircle(sketch, "E206.4.5.0", {"center": v(-21.65, -5.77) * mm, "radius": 2 * mm});
            skCircle(sketch, "E206.4.6.0", {"center": v(-21.65, -11.55) * mm, "radius": 2 * mm});
            skCircle(sketch, "E206.4.7.0", {"center": v(-21.65, -17.33) * mm, "radius": 2 * mm});
            skCircle(sketch, "E206.4.8.0", {"center": v(-21.65, -23.1) * mm, "radius": 2 * mm});
            skCircle(sketch, "E206.5.0.0", {"center": v(-16.23, 23.11) * mm, "radius": 2 * mm});
            skCircle(sketch, "E206.5.1.0", {"center": v(-16.23, 17.33) * mm, "radius": 2 * mm});
            skCircle(sketch, "E206.5.2.0", {"center": v(-16.23, 11.56) * mm, "radius": 2 * mm});
            skCircle(sketch, "E206.5.3.0", {"center": v(-16.23, 5.78) * mm, "radius": 2 * mm});
            skCircle(sketch, "E206.5.4.0", {"center": v(-16.23, 0) * mm, "radius": 2 * mm});
            skCircle(sketch, "E206.5.5.0", {"center": v(-16.23, -5.77) * mm, "radius": 2 * mm});
            skCircle(sketch, "E206.5.6.0", {"center": v(-16.23, -11.55) * mm, "radius": 2 * mm});
            skCircle(sketch, "E206.5.7.0", {"center": v(-16.23, -17.33) * mm, "radius": 2 * mm});
            skCircle(sketch, "E206.5.8.0", {"center": v(-16.23, -23.1) * mm, "radius": 2 * mm});
            skCircle(sketch, "E206.6.0.0", {"center": v(-10.82, 23.11) * mm, "radius": 2 * mm});
            skCircle(sketch, "E206.6.1.0", {"center": v(-10.82, 17.33) * mm, "radius": 2 * mm});
            skCircle(sketch, "E206.6.2.0", {"center": v(-10.82, 11.56) * mm, "radius": 2 * mm});
            skCircle(sketch, "E206.6.3.0", {"center": v(-10.82, 5.78) * mm, "radius": 2 * mm});
            skCircle(sketch, "E206.6.4.0", {"center": v(-10.82, 0) * mm, "radius": 2 * mm});
            skCircle(sketch, "E206.6.5.0", {"center": v(-10.82, -5.77) * mm, "radius": 2 * mm});
            skCircle(sketch, "E206.6.6.0", {"center": v(-10.82, -11.55) * mm, "radius": 2 * mm});
            skCircle(sketch, "E206.6.7.0", {"center": v(-10.82, -17.33) * mm, "radius": 2 * mm});
            skCircle(sketch, "E206.6.8.0", {"center": v(-10.82, -23.1) * mm, "radius": 2 * mm});
            skCircle(sketch, "E206.7.0.0", {"center": v(-5.41, 23.11) * mm, "radius": 2 * mm});
            skCircle(sketch, "E206.7.1.0", {"center": v(-5.41, 17.33) * mm, "radius": 2 * mm});
            skCircle(sketch, "E206.7.2.0", {"center": v(-5.41, 11.56) * mm, "radius": 2 * mm});
            skCircle(sketch, "E206.7.3.0", {"center": v(-5.41, 5.78) * mm, "radius": 2 * mm});
            skCircle(sketch, "E206.7.4.0", {"center": v(-5.41, 0) * mm, "radius": 2 * mm});
            skCircle(sketch, "E206.7.5.0", {"center": v(-5.41, -5.77) * mm, "radius": 2 * mm});
            skCircle(sketch, "E206.7.6.0", {"center": v(-5.41, -11.55) * mm, "radius": 2 * mm});
            skCircle(sketch, "E206.7.7.0", {"center": v(-5.41, -17.33) * mm, "radius": 2 * mm});
            skCircle(sketch, "E206.7.8.0", {"center": v(-5.41, -23.1) * mm, "radius": 2 * mm});
            skCircle(sketch, "E206.8.0.0", {"center": v(0, 23.11) * mm, "radius": 2 * mm});
            skCircle(sketch, "E206.8.1.0", {"center": v(0, 17.33) * mm, "radius": 2 * mm});
            skCircle(sketch, "E206.8.2.0", {"center": v(0, 11.56) * mm, "radius": 2 * mm});
            skCircle(sketch, "E206.8.3.0", {"center": v(0, 5.78) * mm, "radius": 2 * mm});
            skCircle(sketch, "E206.8.4.0", {"center": v(0, 0) * mm, "radius": 2 * mm});
            skCircle(sketch, "E206.8.5.0", {"center": v(0, -5.77) * mm, "radius": 2 * mm});
            skCircle(sketch, "E206.8.6.0", {"center": v(0, -11.55) * mm, "radius": 2 * mm});
            skCircle(sketch, "E206.8.7.0", {"center": v(0, -17.33) * mm, "radius": 2 * mm});
            skCircle(sketch, "E206.8.8.0", {"center": v(0, -23.1) * mm, "radius": 2 * mm});
            skCircle(sketch, "E206.9.0.0", {"center": v(5.41, 23.11) * mm, "radius": 2 * mm});
            skCircle(sketch, "E206.9.1.0", {"center": v(5.41, 17.33) * mm, "radius": 2 * mm});
            skCircle(sketch, "E206.9.2.0", {"center": v(5.41, 11.56) * mm, "radius": 2 * mm});
            skCircle(sketch, "E206.9.3.0", {"center": v(5.41, 5.78) * mm, "radius": 2 * mm});
            skCircle(sketch, "E206.9.4.0", {"center": v(5.41, 0) * mm, "radius": 2 * mm});
            skCircle(sketch, "E206.9.5.0", {"center": v(5.41, -5.77) * mm, "radius": 2 * mm});
            skCircle(sketch, "E206.9.6.0", {"center": v(5.41, -11.55) * mm, "radius": 2 * mm});
            skCircle(sketch, "E206.9.7.0", {"center": v(5.41, -17.33) * mm, "radius": 2 * mm});
            skCircle(sketch, "E206.9.8.0", {"center": v(5.41, -23.1) * mm, "radius": 2 * mm});
            skCircle(sketch, "E206.10.0.0", {"center": v(10.83, 23.11) * mm, "radius": 2 * mm});
            skCircle(sketch, "E206.10.1.0", {"center": v(10.83, 17.33) * mm, "radius": 2 * mm});
            skCircle(sketch, "E206.10.2.0", {"center": v(10.83, 11.56) * mm, "radius": 2 * mm});
            skCircle(sketch, "E206.10.3.0", {"center": v(10.83, 5.78) * mm, "radius": 2 * mm});
            skCircle(sketch, "E206.10.4.0", {"center": v(10.83, 0) * mm, "radius": 2 * mm});
            skCircle(sketch, "E206.10.5.0", {"center": v(10.83, -5.77) * mm, "radius": 2 * mm});
            skCircle(sketch, "E206.10.6.0", {"center": v(10.83, -11.55) * mm, "radius": 2 * mm});
            skCircle(sketch, "E206.10.7.0", {"center": v(10.83, -17.33) * mm, "radius": 2 * mm});
            skCircle(sketch, "E206.10.8.0", {"center": v(10.83, -23.1) * mm, "radius": 2 * mm});
            skCircle(sketch, "E206.11.0.0", {"center": v(16.24, 23.11) * mm, "radius": 2 * mm});
            skCircle(sketch, "E206.11.1.0", {"center": v(16.24, 17.33) * mm, "radius": 2 * mm});
            skCircle(sketch, "E206.11.2.0", {"center": v(16.24, 11.56) * mm, "radius": 2 * mm});
            skCircle(sketch, "E206.11.3.0", {"center": v(16.24, 5.78) * mm, "radius": 2 * mm});
            skCircle(sketch, "E206.11.4.0", {"center": v(16.24, 0) * mm, "radius": 2 * mm});
            skCircle(sketch, "E206.11.5.0", {"center": v(16.24, -5.77) * mm, "radius": 2 * mm});
            skCircle(sketch, "E206.11.6.0", {"center": v(16.24, -11.55) * mm, "radius": 2 * mm});
            skCircle(sketch, "E206.11.7.0", {"center": v(16.24, -17.33) * mm, "radius": 2 * mm});
            skCircle(sketch, "E206.11.8.0", {"center": v(16.24, -23.1) * mm, "radius": 2 * mm});
            skCircle(sketch, "E206.12.0.0", {"center": v(21.65, 23.11) * mm, "radius": 2 * mm});
            skCircle(sketch, "E206.12.1.0", {"center": v(21.65, 17.33) * mm, "radius": 2 * mm});
            skCircle(sketch, "E206.12.2.0", {"center": v(21.65, 11.56) * mm, "radius": 2 * mm});
            skCircle(sketch, "E206.12.3.0", {"center": v(21.65, 5.78) * mm, "radius": 2 * mm});
            skCircle(sketch, "E206.12.4.0", {"center": v(21.65, 0) * mm, "radius": 2 * mm});
            skCircle(sketch, "E206.12.5.0", {"center": v(21.65, -5.77) * mm, "radius": 2 * mm});
            skCircle(sketch, "E206.12.6.0", {"center": v(21.65, -11.55) * mm, "radius": 2 * mm});
            skCircle(sketch, "E206.12.7.0", {"center": v(21.65, -17.33) * mm, "radius": 2 * mm});
            skCircle(sketch, "E206.12.8.0", {"center": v(21.65, -23.1) * mm, "radius": 2 * mm});
            skCircle(sketch, "E206.13.0.0", {"center": v(27.06, 23.11) * mm, "radius": 2 * mm});
            skCircle(sketch, "E206.13.1.0", {"center": v(27.06, 17.33) * mm, "radius": 2 * mm});
            skCircle(sketch, "E206.13.2.0", {"center": v(27.06, 11.56) * mm, "radius": 2 * mm});
            skCircle(sketch, "E206.13.3.0", {"center": v(27.06, 5.78) * mm, "radius": 2 * mm});
            skCircle(sketch, "E206.13.4.0", {"center": v(27.06, 0) * mm, "radius": 2 * mm});
            skCircle(sketch, "E206.13.5.0", {"center": v(27.06, -5.77) * mm, "radius": 2 * mm});
            skCircle(sketch, "E206.13.6.0", {"center": v(27.06, -11.55) * mm, "radius": 2 * mm});
            skCircle(sketch, "E206.13.7.0", {"center": v(27.06, -17.33) * mm, "radius": 2 * mm});
            skCircle(sketch, "E206.13.8.0", {"center": v(27.06, -23.1) * mm, "radius": 2 * mm});
            skCircle(sketch, "E206.14.0.0", {"center": v(32.47, 23.11) * mm, "radius": 2 * mm});
            skCircle(sketch, "E206.14.1.0", {"center": v(32.47, 17.33) * mm, "radius": 2 * mm});
            skCircle(sketch, "E206.14.2.0", {"center": v(32.47, 11.56) * mm, "radius": 2 * mm});
            skCircle(sketch, "E206.14.3.0", {"center": v(32.47, 5.78) * mm, "radius": 2 * mm});
            skCircle(sketch, "E206.14.4.0", {"center": v(32.47, 0) * mm, "radius": 2 * mm});
            skCircle(sketch, "E206.14.5.0", {"center": v(32.47, -5.77) * mm, "radius": 2 * mm});
            skCircle(sketch, "E206.14.6.0", {"center": v(32.47, -11.55) * mm, "radius": 2 * mm});
            skCircle(sketch, "E206.14.7.0", {"center": v(32.47, -17.33) * mm, "radius": 2 * mm});
            skCircle(sketch, "E206.14.8.0", {"center": v(32.47, -23.1) * mm, "radius": 2 * mm});
            skCircle(sketch, "E206.15.0.0", {"center": v(37.89, 23.11) * mm, "radius": 2 * mm});
            skCircle(sketch, "E206.15.1.0", {"center": v(37.89, 17.33) * mm, "radius": 2 * mm});
            skCircle(sketch, "E206.15.2.0", {"center": v(37.89, 11.56) * mm, "radius": 2 * mm});
            skCircle(sketch, "E206.15.3.0", {"center": v(37.89, 5.78) * mm, "radius": 2 * mm});
            skCircle(sketch, "E206.15.4.0", {"center": v(37.89, 0) * mm, "radius": 2 * mm});
            skCircle(sketch, "E206.15.5.0", {"center": v(37.89, -5.77) * mm, "radius": 2 * mm});
            skCircle(sketch, "E206.15.6.0", {"center": v(37.89, -11.55) * mm, "radius": 2 * mm});
            skCircle(sketch, "E206.15.7.0", {"center": v(37.89, -17.33) * mm, "radius": 2 * mm});
            skCircle(sketch, "E206.15.8.0", {"center": v(37.89, -23.1) * mm, "radius": 2 * mm});
            skCircle(sketch, "E206.16.0.0", {"center": v(43.3, 23.11) * mm, "radius": 2 * mm});
            skCircle(sketch, "E206.16.1.0", {"center": v(43.3, 17.33) * mm, "radius": 2 * mm});
            skCircle(sketch, "E206.16.2.0", {"center": v(43.3, 11.56) * mm, "radius": 2 * mm});
            skCircle(sketch, "E206.16.3.0", {"center": v(43.3, 5.78) * mm, "radius": 2 * mm});
            skCircle(sketch, "E206.16.4.0", {"center": v(43.3, 0) * mm, "radius": 2 * mm});
            skCircle(sketch, "E206.16.5.0", {"center": v(43.3, -5.77) * mm, "radius": 2 * mm});
            skCircle(sketch, "E206.16.6.0", {"center": v(43.3, -11.55) * mm, "radius": 2 * mm});
            skCircle(sketch, "E206.16.7.0", {"center": v(43.3, -17.33) * mm, "radius": 2 * mm});
            skCircle(sketch, "E206.16.8.0", {"center": v(43.3, -23.1) * mm, "radius": 2 * mm});
            skLineSegment(sketch, "E206.direction1", {"start": v(-43.3, 23.11) * mm, "end": v(-37.88, 23.11) * mm, "construction": true});
            skLineSegment(sketch, "E206.direction2", {"start": v(-43.3, 23.11) * mm, "end": v(-43.3, 17.33) * mm, "construction": true});
            skSolve(sketch);
        }
        {
            var Q0;
            Q0=makeQuery(id+"F0.imprint","IMPRINT",FACE,{"disambiguationData":[TD([[makeQuery(id+"F0.imprint","IMPRINT",EDGE,{"derivedFrom":sQuery(id+"F0.wireOp",EDGE,"E0.bottom")}),-1.0]])]});
            extrude(context, id + "F2", {"entities" : qUnion([Q0]), "depth" : -4 * mm, "offsetDistance" : 25 * mm, "hasSecondDirection" : true, "secondDirectionOppositeDirection" : true, "secondDirectionDepth" : -1 * mm});
        }
        {
            var Q0;
            Q0 = qSketchRegion(id + "F1", true);
            extrude(context, id + "F3", {"entities" : qUnion([Q0]), "depth" : 15 * mm, "offsetDistance" : 25 * mm});
        }
        {
            var Q0;
            Q0=makeQuery(id+"F3.opExtrude","CAP_EDGE",EDGE,{"disambiguationData":[OSD([sQuery(id+"F1.wireOp",EDGE,"E199")])],"isStart":false});
            var Q1;
            Q1=makeQuery(id+"F3.opExtrude","CAP_FACE",FACE,{"disambiguationData":[OSD([sQuery(id+"F1.wireOp",EDGE,"E206.0.1.0")])],"isStart":false});
            var Q2;
            Q2=makeQuery(id+"F3.opExtrude","CAP_FACE",FACE,{"disambiguationData":[OSD([sQuery(id+"F1.wireOp",EDGE,"E206.0.2.0")])],"isStart":false});
            var Q3;
            Q3=makeQuery(id+"F3.opExtrude","CAP_FACE",FACE,{"disambiguationData":[OSD([sQuery(id+"F1.wireOp",EDGE,"E206.1.2.0")])],"isStart":false});
            var Q4;
            Q4=makeQuery(id+"F3.opExtrude","CAP_FACE",FACE,{"disambiguationData":[OSD([sQuery(id+"F1.wireOp",EDGE,"E206.1.1.0")])],"isStart":false});
            var Q5;
            Q5=makeQuery(id+"F3.opExtrude","CAP_FACE",FACE,{"disambiguationData":[OSD([sQuery(id+"F1.wireOp",EDGE,"E206.1.0.0")])],"isStart":false});
            var Q6;
            Q6=makeQuery(id+"F3.opExtrude","CAP_FACE",FACE,{"disambiguationData":[OSD([sQuery(id+"F1.wireOp",EDGE,"E206.2.0.0")])],"isStart":false});
            var Q7;
            Q7=makeQuery(id+"F3.opExtrude","CAP_FACE",FACE,{"disambiguationData":[OSD([sQuery(id+"F1.wireOp",EDGE,"E206.3.0.0")])],"isStart":false});
            var Q8;
            Q8=makeQuery(id+"F3.opExtrude","CAP_FACE",FACE,{"disambiguationData":[OSD([sQuery(id+"F1.wireOp",EDGE,"E206.4.0.0")])],"isStart":false});
            var Q9;
            Q9=makeQuery(id+"F3.opExtrude","CAP_FACE",FACE,{"disambiguationData":[OSD([sQuery(id+"F1.wireOp",EDGE,"E206.5.0.0")])],"isStart":false});
            var Q10;
            Q10=makeQuery(id+"F3.opExtrude","CAP_FACE",FACE,{"disambiguationData":[OSD([sQuery(id+"F1.wireOp",EDGE,"E206.6.0.0")])],"isStart":false});
            var Q11;
            Q11=makeQuery(id+"F3.opExtrude","CAP_FACE",FACE,{"disambiguationData":[OSD([sQuery(id+"F1.wireOp",EDGE,"E206.6.1.0")])],"isStart":false});
            var Q12;
            Q12=makeQuery(id+"F3.opExtrude","CAP_FACE",FACE,{"disambiguationData":[OSD([sQuery(id+"F1.wireOp",EDGE,"E206.5.1.0")])],"isStart":false});
            var Q13;
            Q13=makeQuery(id+"F3.opExtrude","CAP_FACE",FACE,{"disambiguationData":[OSD([sQuery(id+"F1.wireOp",EDGE,"E206.4.1.0")])],"isStart":false});
            var Q14;
            Q14=makeQuery(id+"F3.opExtrude","CAP_FACE",FACE,{"disambiguationData":[OSD([sQuery(id+"F1.wireOp",EDGE,"E206.3.1.0")])],"isStart":false});
            var Q15;
            Q15=makeQuery(id+"F3.opExtrude","CAP_FACE",FACE,{"disambiguationData":[OSD([sQuery(id+"F1.wireOp",EDGE,"E206.2.1.0")])],"isStart":false});
            var Q16;
            Q16=makeQuery(id+"F3.opExtrude","CAP_FACE",FACE,{"disambiguationData":[OSD([sQuery(id+"F1.wireOp",EDGE,"E206.2.2.0")])],"isStart":false});
            var Q17;
            Q17=makeQuery(id+"F3.opExtrude","CAP_FACE",FACE,{"disambiguationData":[OSD([sQuery(id+"F1.wireOp",EDGE,"E206.3.2.0")])],"isStart":false});
            var Q18;
            Q18=makeQuery(id+"F3.opExtrude","CAP_FACE",FACE,{"disambiguationData":[OSD([sQuery(id+"F1.wireOp",EDGE,"E206.4.2.0")])],"isStart":false});
            var Q19;
            Q19=makeQuery(id+"F3.opExtrude","CAP_FACE",FACE,{"disambiguationData":[OSD([sQuery(id+"F1.wireOp",EDGE,"E206.5.2.0")])],"isStart":false});
            var Q20;
            Q20=makeQuery(id+"F3.opExtrude","CAP_FACE",FACE,{"disambiguationData":[OSD([sQuery(id+"F1.wireOp",EDGE,"E206.7.0.0")])],"isStart":false});
            var Q21;
            Q21=makeQuery(id+"F3.opExtrude","CAP_FACE",FACE,{"disambiguationData":[OSD([sQuery(id+"F1.wireOp",EDGE,"E206.7.1.0")])],"isStart":false});
            var Q22;
            Q22=makeQuery(id+"F3.opExtrude","CAP_FACE",FACE,{"disambiguationData":[OSD([sQuery(id+"F1.wireOp",EDGE,"E206.6.2.0")])],"isStart":false});
            var Q23;
            Q23=makeQuery(id+"F3.opExtrude","CAP_FACE",FACE,{"disambiguationData":[OSD([sQuery(id+"F1.wireOp",EDGE,"E206.7.2.0")])],"isStart":false});
            var Q24;
            Q24=makeQuery(id+"F3.opExtrude","CAP_FACE",FACE,{"disambiguationData":[OSD([sQuery(id+"F1.wireOp",EDGE,"E206.8.2.0")])],"isStart":false});
            var Q25;
            Q25=makeQuery(id+"F3.opExtrude","CAP_FACE",FACE,{"disambiguationData":[OSD([sQuery(id+"F1.wireOp",EDGE,"E206.8.1.0")])],"isStart":false});
            var Q26;
            Q26=makeQuery(id+"F3.opExtrude","CAP_FACE",FACE,{"disambiguationData":[OSD([sQuery(id+"F1.wireOp",EDGE,"E206.8.0.0")])],"isStart":false});
            var Q27;
            Q27=makeQuery(id+"F3.opExtrude","CAP_FACE",FACE,{"disambiguationData":[OSD([sQuery(id+"F1.wireOp",EDGE,"E206.9.0.0")])],"isStart":false});
            var Q28;
            Q28=makeQuery(id+"F3.opExtrude","CAP_FACE",FACE,{"disambiguationData":[OSD([sQuery(id+"F1.wireOp",EDGE,"E206.10.0.0")])],"isStart":false});
            var Q29;
            Q29=makeQuery(id+"F3.opExtrude","CAP_FACE",FACE,{"disambiguationData":[OSD([sQuery(id+"F1.wireOp",EDGE,"E206.11.0.0")])],"isStart":false});
            var Q30;
            Q30=makeQuery(id+"F3.opExtrude","CAP_FACE",FACE,{"disambiguationData":[OSD([sQuery(id+"F1.wireOp",EDGE,"E206.12.0.0")])],"isStart":false});
            var Q31;
            Q31=makeQuery(id+"F3.opExtrude","CAP_FACE",FACE,{"disambiguationData":[OSD([sQuery(id+"F1.wireOp",EDGE,"E206.13.0.0")])],"isStart":false});
            var Q32;
            Q32=makeQuery(id+"F3.opExtrude","CAP_FACE",FACE,{"disambiguationData":[OSD([sQuery(id+"F1.wireOp",EDGE,"E206.14.0.0")])],"isStart":false});
            var Q33;
            Q33=makeQuery(id+"F3.opExtrude","CAP_FACE",FACE,{"disambiguationData":[OSD([sQuery(id+"F1.wireOp",EDGE,"E206.15.1.0")])],"isStart":false});
            var Q34;
            Q34=makeQuery(id+"F3.opExtrude","CAP_FACE",FACE,{"disambiguationData":[OSD([sQuery(id+"F1.wireOp",EDGE,"E206.14.1.0")])],"isStart":false});
            var Q35;
            Q35=makeQuery(id+"F3.opExtrude","CAP_FACE",FACE,{"disambiguationData":[OSD([sQuery(id+"F1.wireOp",EDGE,"E206.13.1.0")])],"isStart":false});
            var Q36;
            Q36=makeQuery(id+"F3.opExtrude","CAP_FACE",FACE,{"disambiguationData":[OSD([sQuery(id+"F1.wireOp",EDGE,"E206.12.1.0")])],"isStart":false});
            var Q37;
            Q37=makeQuery(id+"F3.opExtrude","CAP_FACE",FACE,{"disambiguationData":[OSD([sQuery(id+"F1.wireOp",EDGE,"E206.11.1.0")])],"isStart":false});
            var Q38;
            Q38=makeQuery(id+"F3.opExtrude","CAP_FACE",FACE,{"disambiguationData":[OSD([sQuery(id+"F1.wireOp",EDGE,"E206.10.1.0")])],"isStart":false});
            var Q39;
            Q39=makeQuery(id+"F3.opExtrude","CAP_FACE",FACE,{"disambiguationData":[OSD([sQuery(id+"F1.wireOp",EDGE,"E206.9.1.0")])],"isStart":false});
            var Q40;
            Q40=makeQuery(id+"F3.opExtrude","CAP_FACE",FACE,{"disambiguationData":[OSD([sQuery(id+"F1.wireOp",EDGE,"E206.9.2.0")])],"isStart":false});
            var Q41;
            Q41=makeQuery(id+"F3.opExtrude","CAP_FACE",FACE,{"disambiguationData":[OSD([sQuery(id+"F1.wireOp",EDGE,"E206.10.2.0")])],"isStart":false});
            var Q42;
            Q42=makeQuery(id+"F3.opExtrude","CAP_FACE",FACE,{"disambiguationData":[OSD([sQuery(id+"F1.wireOp",EDGE,"E206.11.2.0")])],"isStart":false});
            var Q43;
            Q43=makeQuery(id+"F3.opExtrude","CAP_FACE",FACE,{"disambiguationData":[OSD([sQuery(id+"F1.wireOp",EDGE,"E206.12.2.0")])],"isStart":false});
            var Q44;
            Q44=makeQuery(id+"F3.opExtrude","CAP_FACE",FACE,{"disambiguationData":[OSD([sQuery(id+"F1.wireOp",EDGE,"E206.13.2.0")])],"isStart":false});
            var Q45;
            Q45=makeQuery(id+"F3.opExtrude","CAP_FACE",FACE,{"disambiguationData":[OSD([sQuery(id+"F1.wireOp",EDGE,"E206.14.2.0")])],"isStart":false});
            var Q46;
            Q46=makeQuery(id+"F3.opExtrude","CAP_FACE",FACE,{"disambiguationData":[OSD([sQuery(id+"F1.wireOp",EDGE,"E206.15.2.0")])],"isStart":false});
            var Q47;
            Q47=makeQuery(id+"F3.opExtrude","CAP_FACE",FACE,{"disambiguationData":[OSD([sQuery(id+"F1.wireOp",EDGE,"E206.16.0.0")])],"isStart":false});
            var Q48;
            Q48=makeQuery(id+"F3.opExtrude","CAP_FACE",FACE,{"disambiguationData":[OSD([sQuery(id+"F1.wireOp",EDGE,"E206.16.1.0")])],"isStart":false});
            var Q49;
            Q49=makeQuery(id+"F3.opExtrude","CAP_FACE",FACE,{"disambiguationData":[OSD([sQuery(id+"F1.wireOp",EDGE,"E206.16.2.0")])],"isStart":false});
            var Q50;
            Q50=makeQuery(id+"F3.opExtrude","CAP_FACE",FACE,{"disambiguationData":[OSD([sQuery(id+"F1.wireOp",EDGE,"E206.16.3.0")])],"isStart":false});
            var Q51;
            Q51=makeQuery(id+"F3.opExtrude","CAP_FACE",FACE,{"disambiguationData":[OSD([sQuery(id+"F1.wireOp",EDGE,"E206.16.4.0")])],"isStart":false});
            var Q52;
            Q52=makeQuery(id+"F3.opExtrude","CAP_FACE",FACE,{"disambiguationData":[OSD([sQuery(id+"F1.wireOp",EDGE,"E206.15.4.0")])],"isStart":false});
            var Q53;
            Q53=makeQuery(id+"F3.opExtrude","CAP_FACE",FACE,{"disambiguationData":[OSD([sQuery(id+"F1.wireOp",EDGE,"E206.15.3.0")])],"isStart":false});
            var Q54;
            Q54=makeQuery(id+"F3.opExtrude","CAP_FACE",FACE,{"disambiguationData":[OSD([sQuery(id+"F1.wireOp",EDGE,"E206.14.4.0")])],"isStart":false});
            var Q55;
            Q55=makeQuery(id+"F3.opExtrude","CAP_FACE",FACE,{"disambiguationData":[OSD([sQuery(id+"F1.wireOp",EDGE,"E206.13.4.0")])],"isStart":false});
            var Q56;
            Q56=makeQuery(id+"F3.opExtrude","CAP_FACE",FACE,{"disambiguationData":[OSD([sQuery(id+"F1.wireOp",EDGE,"E206.13.3.0")])],"isStart":false});
            var Q57;
            Q57=makeQuery(id+"F3.opExtrude","CAP_FACE",FACE,{"disambiguationData":[OSD([sQuery(id+"F1.wireOp",EDGE,"E206.12.3.0")])],"isStart":false});
            var Q58;
            Q58=makeQuery(id+"F3.opExtrude","CAP_FACE",FACE,{"disambiguationData":[OSD([sQuery(id+"F1.wireOp",EDGE,"E206.12.4.0")])],"isStart":false});
            var Q59;
            Q59=makeQuery(id+"F3.opExtrude","CAP_FACE",FACE,{"disambiguationData":[OSD([sQuery(id+"F1.wireOp",EDGE,"E206.11.4.0")])],"isStart":false});
            var Q60;
            Q60=makeQuery(id+"F3.opExtrude","CAP_FACE",FACE,{"disambiguationData":[OSD([sQuery(id+"F1.wireOp",EDGE,"E206.11.3.0")])],"isStart":false});
            var Q61;
            Q61=makeQuery(id+"F3.opExtrude","CAP_FACE",FACE,{"disambiguationData":[OSD([sQuery(id+"F1.wireOp",EDGE,"E206.10.3.0")])],"isStart":false});
            var Q62;
            Q62=makeQuery(id+"F3.opExtrude","CAP_FACE",FACE,{"disambiguationData":[OSD([sQuery(id+"F1.wireOp",EDGE,"E206.10.4.0")])],"isStart":false});
            var Q63;
            Q63=makeQuery(id+"F3.opExtrude","CAP_FACE",FACE,{"disambiguationData":[OSD([sQuery(id+"F1.wireOp",EDGE,"E206.9.4.0")])],"isStart":false});
            var Q64;
            Q64=makeQuery(id+"F3.opExtrude","CAP_FACE",FACE,{"disambiguationData":[OSD([sQuery(id+"F1.wireOp",EDGE,"E206.9.3.0")])],"isStart":false});
            var Q65;
            Q65=makeQuery(id+"F3.opExtrude","CAP_FACE",FACE,{"disambiguationData":[OSD([sQuery(id+"F1.wireOp",EDGE,"E206.8.3.0")])],"isStart":false});
            var Q66;
            Q66=makeQuery(id+"F3.opExtrude","CAP_FACE",FACE,{"disambiguationData":[OSD([sQuery(id+"F1.wireOp",EDGE,"E206.8.4.0")])],"isStart":false});
            var Q67;
            Q67=makeQuery(id+"F3.opExtrude","CAP_FACE",FACE,{"disambiguationData":[OSD([sQuery(id+"F1.wireOp",EDGE,"E206.7.4.0")])],"isStart":false});
            var Q68;
            Q68=makeQuery(id+"F3.opExtrude","CAP_FACE",FACE,{"disambiguationData":[OSD([sQuery(id+"F1.wireOp",EDGE,"E206.7.3.0")])],"isStart":false});
            var Q69;
            Q69=makeQuery(id+"F3.opExtrude","CAP_FACE",FACE,{"disambiguationData":[OSD([sQuery(id+"F1.wireOp",EDGE,"E206.15.0.0")])],"isStart":false});
            var Q70;
            Q70=makeQuery(id+"F3.opExtrude","CAP_EDGE",EDGE,{"disambiguationData":[OSD([sQuery(id+"F1.wireOp",EDGE,"E206.14.3.0")])],"isStart":false});
            var Q71;
            Q71=makeQuery(id+"F3.opExtrude","CAP_FACE",FACE,{"disambiguationData":[OSD([sQuery(id+"F1.wireOp",EDGE,"E206.6.3.0")])],"isStart":false});
            var Q72;
            Q72=makeQuery(id+"F3.opExtrude","CAP_FACE",FACE,{"disambiguationData":[OSD([sQuery(id+"F1.wireOp",EDGE,"E206.5.3.0")])],"isStart":false});
            var Q73;
            Q73=makeQuery(id+"F3.opExtrude","CAP_FACE",FACE,{"disambiguationData":[OSD([sQuery(id+"F1.wireOp",EDGE,"E206.4.3.0")])],"isStart":false});
            var Q74;
            Q74=makeQuery(id+"F3.opExtrude","CAP_FACE",FACE,{"disambiguationData":[OSD([sQuery(id+"F1.wireOp",EDGE,"E206.3.3.0")])],"isStart":false});
            var Q75;
            Q75=makeQuery(id+"F3.opExtrude","CAP_FACE",FACE,{"disambiguationData":[OSD([sQuery(id+"F1.wireOp",EDGE,"E206.2.3.0")])],"isStart":false});
            var Q76;
            Q76=makeQuery(id+"F3.opExtrude","CAP_FACE",FACE,{"disambiguationData":[OSD([sQuery(id+"F1.wireOp",EDGE,"E206.1.3.0")])],"isStart":false});
            var Q77;
            Q77=makeQuery(id+"F3.opExtrude","CAP_FACE",FACE,{"disambiguationData":[OSD([sQuery(id+"F1.wireOp",EDGE,"E206.0.3.0")])],"isStart":false});
            var Q78;
            Q78=makeQuery(id+"F3.opExtrude","CAP_FACE",FACE,{"disambiguationData":[OSD([sQuery(id+"F1.wireOp",EDGE,"E206.0.4.0")])],"isStart":false});
            var Q79;
            Q79=makeQuery(id+"F3.opExtrude","CAP_FACE",FACE,{"disambiguationData":[OSD([sQuery(id+"F1.wireOp",EDGE,"E206.1.4.0")])],"isStart":false});
            var Q80;
            Q80=makeQuery(id+"F3.opExtrude","CAP_FACE",FACE,{"disambiguationData":[OSD([sQuery(id+"F1.wireOp",EDGE,"E206.2.4.0")])],"isStart":false});
            var Q81;
            Q81=makeQuery(id+"F3.opExtrude","CAP_FACE",FACE,{"disambiguationData":[OSD([sQuery(id+"F1.wireOp",EDGE,"E206.3.4.0")])],"isStart":false});
            var Q82;
            Q82=makeQuery(id+"F3.opExtrude","CAP_FACE",FACE,{"disambiguationData":[OSD([sQuery(id+"F1.wireOp",EDGE,"E206.4.4.0")])],"isStart":false});
            var Q83;
            Q83=makeQuery(id+"F3.opExtrude","CAP_FACE",FACE,{"disambiguationData":[OSD([sQuery(id+"F1.wireOp",EDGE,"E206.5.4.0")])],"isStart":false});
            var Q84;
            Q84=makeQuery(id+"F3.opExtrude","CAP_FACE",FACE,{"disambiguationData":[OSD([sQuery(id+"F1.wireOp",EDGE,"E206.6.4.0")])],"isStart":false});
            var Q85;
            Q85=makeQuery(id+"F3.opExtrude","CAP_FACE",FACE,{"disambiguationData":[OSD([sQuery(id+"F1.wireOp",EDGE,"E206.0.5.0")])],"isStart":false});
            var Q86;
            Q86=makeQuery(id+"F3.opExtrude","CAP_FACE",FACE,{"disambiguationData":[OSD([sQuery(id+"F1.wireOp",EDGE,"E206.1.5.0")])],"isStart":false});
            var Q87;
            Q87=makeQuery(id+"F3.opExtrude","CAP_FACE",FACE,{"disambiguationData":[OSD([sQuery(id+"F1.wireOp",EDGE,"E206.2.5.0")])],"isStart":false});
            var Q88;
            Q88=makeQuery(id+"F3.opExtrude","CAP_FACE",FACE,{"disambiguationData":[OSD([sQuery(id+"F1.wireOp",EDGE,"E206.3.5.0")])],"isStart":false});
            var Q89;
            Q89=makeQuery(id+"F3.opExtrude","CAP_FACE",FACE,{"disambiguationData":[OSD([sQuery(id+"F1.wireOp",EDGE,"E206.4.5.0")])],"isStart":false});
            var Q90;
            Q90=makeQuery(id+"F3.opExtrude","CAP_FACE",FACE,{"disambiguationData":[OSD([sQuery(id+"F1.wireOp",EDGE,"E206.5.5.0")])],"isStart":false});
            var Q91;
            Q91=makeQuery(id+"F3.opExtrude","CAP_FACE",FACE,{"disambiguationData":[OSD([sQuery(id+"F1.wireOp",EDGE,"E206.6.5.0")])],"isStart":false});
            var Q92;
            Q92=makeQuery(id+"F3.opExtrude","CAP_FACE",FACE,{"disambiguationData":[OSD([sQuery(id+"F1.wireOp",EDGE,"E206.7.5.0")])],"isStart":false});
            var Q93;
            Q93=makeQuery(id+"F3.opExtrude","CAP_FACE",FACE,{"disambiguationData":[OSD([sQuery(id+"F1.wireOp",EDGE,"E206.8.5.0")])],"isStart":false});
            var Q94;
            Q94=makeQuery(id+"F3.opExtrude","CAP_FACE",FACE,{"disambiguationData":[OSD([sQuery(id+"F1.wireOp",EDGE,"E206.9.5.0")])],"isStart":false});
            var Q95;
            Q95=makeQuery(id+"F3.opExtrude","CAP_FACE",FACE,{"disambiguationData":[OSD([sQuery(id+"F1.wireOp",EDGE,"E206.8.6.0")])],"isStart":false});
            var Q96;
            Q96=makeQuery(id+"F3.opExtrude","CAP_FACE",FACE,{"disambiguationData":[OSD([sQuery(id+"F1.wireOp",EDGE,"E206.7.6.0")])],"isStart":false});
            var Q97;
            Q97=makeQuery(id+"F3.opExtrude","CAP_FACE",FACE,{"disambiguationData":[OSD([sQuery(id+"F1.wireOp",EDGE,"E206.6.6.0")])],"isStart":false});
            var Q98;
            Q98=makeQuery(id+"F3.opExtrude","CAP_FACE",FACE,{"disambiguationData":[OSD([sQuery(id+"F1.wireOp",EDGE,"E206.5.6.0")])],"isStart":false});
            var Q99;
            Q99=makeQuery(id+"F3.opExtrude","CAP_FACE",FACE,{"disambiguationData":[OSD([sQuery(id+"F1.wireOp",EDGE,"E206.4.6.0")])],"isStart":false});
            var Q100;
            Q100=makeQuery(id+"F3.opExtrude","CAP_FACE",FACE,{"disambiguationData":[OSD([sQuery(id+"F1.wireOp",EDGE,"E206.3.6.0")])],"isStart":false});
            var Q101;
            Q101=makeQuery(id+"F3.opExtrude","CAP_FACE",FACE,{"disambiguationData":[OSD([sQuery(id+"F1.wireOp",EDGE,"E206.2.6.0")])],"isStart":false});
            var Q102;
            Q102=makeQuery(id+"F3.opExtrude","CAP_FACE",FACE,{"disambiguationData":[OSD([sQuery(id+"F1.wireOp",EDGE,"E206.1.6.0")])],"isStart":false});
            var Q103;
            Q103=makeQuery(id+"F3.opExtrude","CAP_FACE",FACE,{"disambiguationData":[OSD([sQuery(id+"F1.wireOp",EDGE,"E206.0.6.0")])],"isStart":false});
            var Q104;
            Q104=makeQuery(id+"F3.opExtrude","CAP_FACE",FACE,{"disambiguationData":[OSD([sQuery(id+"F1.wireOp",EDGE,"E206.9.6.0")])],"isStart":false});
            var Q105;
            Q105=makeQuery(id+"F3.opExtrude","CAP_FACE",FACE,{"disambiguationData":[OSD([sQuery(id+"F1.wireOp",EDGE,"E206.10.6.0")])],"isStart":false});
            var Q106;
            Q106=makeQuery(id+"F3.opExtrude","CAP_FACE",FACE,{"disambiguationData":[OSD([sQuery(id+"F1.wireOp",EDGE,"E206.11.6.0")])],"isStart":false});
            var Q107;
            Q107=makeQuery(id+"F3.opExtrude","CAP_FACE",FACE,{"disambiguationData":[OSD([sQuery(id+"F1.wireOp",EDGE,"E206.12.6.0")])],"isStart":false});
            var Q108;
            Q108=makeQuery(id+"F3.opExtrude","CAP_FACE",FACE,{"disambiguationData":[OSD([sQuery(id+"F1.wireOp",EDGE,"E206.13.6.0")])],"isStart":false});
            var Q109;
            Q109=makeQuery(id+"F3.opExtrude","CAP_FACE",FACE,{"disambiguationData":[OSD([sQuery(id+"F1.wireOp",EDGE,"E206.14.6.0")])],"isStart":false});
            var Q110;
            Q110=makeQuery(id+"F3.opExtrude","CAP_FACE",FACE,{"disambiguationData":[OSD([sQuery(id+"F1.wireOp",EDGE,"E206.15.6.0")])],"isStart":false});
            var Q111;
            Q111=makeQuery(id+"F3.opExtrude","CAP_FACE",FACE,{"disambiguationData":[OSD([sQuery(id+"F1.wireOp",EDGE,"E206.10.5.0")])],"isStart":false});
            var Q112;
            Q112=makeQuery(id+"F3.opExtrude","CAP_FACE",FACE,{"disambiguationData":[OSD([sQuery(id+"F1.wireOp",EDGE,"E206.11.5.0")])],"isStart":false});
            var Q113;
            Q113=makeQuery(id+"F3.opExtrude","CAP_FACE",FACE,{"disambiguationData":[OSD([sQuery(id+"F1.wireOp",EDGE,"E206.12.5.0")])],"isStart":false});
            var Q114;
            Q114=makeQuery(id+"F3.opExtrude","CAP_FACE",FACE,{"disambiguationData":[OSD([sQuery(id+"F1.wireOp",EDGE,"E206.13.5.0")])],"isStart":false});
            var Q115;
            Q115=makeQuery(id+"F3.opExtrude","CAP_FACE",FACE,{"disambiguationData":[OSD([sQuery(id+"F1.wireOp",EDGE,"E206.14.5.0")])],"isStart":false});
            var Q116;
            Q116=makeQuery(id+"F3.opExtrude","CAP_FACE",FACE,{"disambiguationData":[OSD([sQuery(id+"F1.wireOp",EDGE,"E206.15.5.0")])],"isStart":false});
            var Q117;
            Q117=makeQuery(id+"F3.opExtrude","CAP_FACE",FACE,{"disambiguationData":[OSD([sQuery(id+"F1.wireOp",EDGE,"E206.16.5.0")])],"isStart":false});
            var Q118;
            Q118=makeQuery(id+"F3.opExtrude","CAP_FACE",FACE,{"disambiguationData":[OSD([sQuery(id+"F1.wireOp",EDGE,"E206.16.6.0")])],"isStart":false});
            var Q119;
            Q119=makeQuery(id+"F3.opExtrude","CAP_FACE",FACE,{"disambiguationData":[OSD([sQuery(id+"F1.wireOp",EDGE,"E206.16.7.0")])],"isStart":false});
            var Q120;
            Q120=makeQuery(id+"F3.opExtrude","CAP_FACE",FACE,{"disambiguationData":[OSD([sQuery(id+"F1.wireOp",EDGE,"E206.15.7.0")])],"isStart":false});
            var Q121;
            Q121=makeQuery(id+"F3.opExtrude","CAP_FACE",FACE,{"disambiguationData":[OSD([sQuery(id+"F1.wireOp",EDGE,"E206.14.7.0")])],"isStart":false});
            var Q122;
            Q122=makeQuery(id+"F3.opExtrude","CAP_FACE",FACE,{"disambiguationData":[OSD([sQuery(id+"F1.wireOp",EDGE,"E206.13.7.0")])],"isStart":false});
            var Q123;
            Q123=makeQuery(id+"F3.opExtrude","CAP_FACE",FACE,{"disambiguationData":[OSD([sQuery(id+"F1.wireOp",EDGE,"E206.12.7.0")])],"isStart":false});
            var Q124;
            Q124=makeQuery(id+"F3.opExtrude","CAP_FACE",FACE,{"disambiguationData":[OSD([sQuery(id+"F1.wireOp",EDGE,"E206.11.7.0")])],"isStart":false});
            var Q125;
            Q125=makeQuery(id+"F3.opExtrude","CAP_FACE",FACE,{"disambiguationData":[OSD([sQuery(id+"F1.wireOp",EDGE,"E206.10.7.0")])],"isStart":false});
            var Q126;
            Q126=makeQuery(id+"F3.opExtrude","CAP_FACE",FACE,{"disambiguationData":[OSD([sQuery(id+"F1.wireOp",EDGE,"E206.9.7.0")])],"isStart":false});
            var Q127;
            Q127=makeQuery(id+"F3.opExtrude","CAP_FACE",FACE,{"disambiguationData":[OSD([sQuery(id+"F1.wireOp",EDGE,"E206.8.7.0")])],"isStart":false});
            var Q128;
            Q128=makeQuery(id+"F3.opExtrude","CAP_FACE",FACE,{"disambiguationData":[OSD([sQuery(id+"F1.wireOp",EDGE,"E206.7.7.0")])],"isStart":false});
            var Q129;
            Q129=makeQuery(id+"F3.opExtrude","CAP_FACE",FACE,{"disambiguationData":[OSD([sQuery(id+"F1.wireOp",EDGE,"E206.6.7.0")])],"isStart":false});
            var Q130;
            Q130=makeQuery(id+"F3.opExtrude","CAP_FACE",FACE,{"disambiguationData":[OSD([sQuery(id+"F1.wireOp",EDGE,"E206.5.7.0")])],"isStart":false});
            var Q131;
            Q131=makeQuery(id+"F3.opExtrude","CAP_FACE",FACE,{"disambiguationData":[OSD([sQuery(id+"F1.wireOp",EDGE,"E206.4.7.0")])],"isStart":false});
            var Q132;
            Q132=makeQuery(id+"F3.opExtrude","CAP_FACE",FACE,{"disambiguationData":[OSD([sQuery(id+"F1.wireOp",EDGE,"E206.3.7.0")])],"isStart":false});
            var Q133;
            Q133=makeQuery(id+"F3.opExtrude","CAP_FACE",FACE,{"disambiguationData":[OSD([sQuery(id+"F1.wireOp",EDGE,"E206.0.7.0")])],"isStart":false});
            var Q134;
            Q134=makeQuery(id+"F3.opExtrude","CAP_FACE",FACE,{"disambiguationData":[OSD([sQuery(id+"F1.wireOp",EDGE,"E206.1.7.0")])],"isStart":false});
            var Q135;
            Q135=makeQuery(id+"F3.opExtrude","CAP_FACE",FACE,{"disambiguationData":[OSD([sQuery(id+"F1.wireOp",EDGE,"E206.2.7.0")])],"isStart":false});
            var Q136;
            Q136=makeQuery(id+"F3.opExtrude","CAP_FACE",FACE,{"disambiguationData":[OSD([sQuery(id+"F1.wireOp",EDGE,"E206.0.8.0")])],"isStart":false});
            var Q137;
            Q137=makeQuery(id+"F3.opExtrude","CAP_FACE",FACE,{"disambiguationData":[OSD([sQuery(id+"F1.wireOp",EDGE,"E206.1.8.0")])],"isStart":false});
            var Q138;
            Q138=makeQuery(id+"F3.opExtrude","CAP_FACE",FACE,{"disambiguationData":[OSD([sQuery(id+"F1.wireOp",EDGE,"E206.2.8.0")])],"isStart":false});
            var Q139;
            Q139=makeQuery(id+"F3.opExtrude","CAP_FACE",FACE,{"disambiguationData":[OSD([sQuery(id+"F1.wireOp",EDGE,"E206.3.8.0")])],"isStart":false});
            var Q140;
            Q140=makeQuery(id+"F3.opExtrude","CAP_FACE",FACE,{"disambiguationData":[OSD([sQuery(id+"F1.wireOp",EDGE,"E206.4.8.0")])],"isStart":false});
            var Q141;
            Q141=makeQuery(id+"F3.opExtrude","CAP_FACE",FACE,{"disambiguationData":[OSD([sQuery(id+"F1.wireOp",EDGE,"E206.5.8.0")])],"isStart":false});
            var Q142;
            Q142=makeQuery(id+"F3.opExtrude","CAP_FACE",FACE,{"disambiguationData":[OSD([sQuery(id+"F1.wireOp",EDGE,"E206.6.8.0")])],"isStart":false});
            var Q143;
            Q143=makeQuery(id+"F3.opExtrude","CAP_FACE",FACE,{"disambiguationData":[OSD([sQuery(id+"F1.wireOp",EDGE,"E206.7.8.0")])],"isStart":false});
            var Q144;
            Q144=makeQuery(id+"F3.opExtrude","CAP_FACE",FACE,{"disambiguationData":[OSD([sQuery(id+"F1.wireOp",EDGE,"E206.8.8.0")])],"isStart":false});
            var Q145;
            Q145=makeQuery(id+"F3.opExtrude","CAP_FACE",FACE,{"disambiguationData":[OSD([sQuery(id+"F1.wireOp",EDGE,"E206.9.8.0")])],"isStart":false});
            var Q146;
            Q146=makeQuery(id+"F3.opExtrude","CAP_FACE",FACE,{"disambiguationData":[OSD([sQuery(id+"F1.wireOp",EDGE,"E206.11.8.0")])],"isStart":false});
            var Q147;
            Q147=makeQuery(id+"F3.opExtrude","CAP_FACE",FACE,{"disambiguationData":[OSD([sQuery(id+"F1.wireOp",EDGE,"E206.12.8.0")])],"isStart":false});
            var Q148;
            Q148=makeQuery(id+"F3.opExtrude","CAP_FACE",FACE,{"disambiguationData":[OSD([sQuery(id+"F1.wireOp",EDGE,"E206.13.8.0")])],"isStart":false});
            var Q149;
            Q149=makeQuery(id+"F3.opExtrude","CAP_FACE",FACE,{"disambiguationData":[OSD([sQuery(id+"F1.wireOp",EDGE,"E206.14.8.0")])],"isStart":false});
            var Q150;
            Q150=makeQuery(id+"F3.opExtrude","CAP_FACE",FACE,{"disambiguationData":[OSD([sQuery(id+"F1.wireOp",EDGE,"E206.15.8.0")])],"isStart":false});
            var Q151;
            Q151=makeQuery(id+"F3.opExtrude","CAP_FACE",FACE,{"disambiguationData":[OSD([sQuery(id+"F1.wireOp",EDGE,"E206.16.8.0")])],"isStart":false});
            var Q152;
            Q152=makeQuery(id+"F3.opExtrude","CAP_FACE",FACE,{"disambiguationData":[OSD([sQuery(id+"F1.wireOp",EDGE,"E206.10.8.0")])],"isStart":false});
            chamfer(context, id + "F4", {"entities" : qUnion([Q0, Q1, Q2, Q3, Q4, Q5, Q6, Q7, Q8, Q9, Q10, Q11, Q12, Q13, Q14, Q15, Q16, Q17, Q18, Q19, Q20, Q21, Q22, Q23, Q24, Q25, Q26, Q27, Q28, Q29, Q30, Q31, Q32, Q33, Q34, Q35, Q36, Q37, Q38, Q39, Q40, Q41, Q42, Q43, Q44, Q45, Q46, Q47, Q48, Q49, Q50, Q51, Q52, Q53, Q54, Q55, Q56, Q57, Q58, Q59, Q60, Q61, Q62, Q63, Q64, Q65, Q66, Q67, Q68, Q69, Q70, Q71, Q72, Q73, Q74, Q75, Q76, Q77, Q78, Q79, Q80, Q81, Q82, Q83, Q84, Q85, Q86, Q87, Q88, Q89, Q90, Q91, Q92, Q93, Q94, Q95, Q96, Q97, Q98, Q99, Q100, Q101, Q102, Q103, Q104, Q105, Q106, Q107, Q108, Q109, Q110, Q111, Q112, Q113, Q114, Q115, Q116, Q117, Q118, Q119, Q120, Q121, Q122, Q123, Q124, Q125, Q126, Q127, Q128, Q129, Q130, Q131, Q132, Q133, Q134, Q135, Q136, Q137, Q138, Q139, Q140, Q141, Q142, Q143, Q144, Q145, Q146, Q147, Q148, Q149, Q150, Q151, Q152]), "chamferType" : ChamferType.TWO_OFFSETS, "width1" : 1.5 * mm, "oppositeDirection" : false, "width2" : 15 * mm, "tangentPropagation" : true});
        }
        {
            var Q0;
            {var subQ0=sQuery(id+"F1.wireOp",EDGE,"E206.16.4.0");Q0=makeQuery(id+"F4.opChamfer","BLEND_EDGE",EDGE,{"blendedFrom":[makeQuery(id+"F3.opExtrude","CAP_EDGE",EDGE,{"disambiguationData":[OSD([subQ0])],"isStart":false}),makeQuery(id+"F3.opExtrude","CAP_FACE",FACE,{"disambiguationData":[OSD([subQ0])],"isStart":false})],"blendedInto":[makeQuery(id+"F3.opExtrude","CAP_FACE",FACE,{"disambiguationData":[OSD([subQ0])],"isStart":false})]});}
            var Q1;
            {var subQ0=sQuery(id+"F1.wireOp",EDGE,"E206.14.4.0");Q1=makeQuery(id+"F4.opChamfer","BLEND_EDGE",EDGE,{"blendedFrom":[makeQuery(id+"F3.opExtrude","CAP_EDGE",EDGE,{"disambiguationData":[OSD([subQ0])],"isStart":false}),makeQuery(id+"F3.opExtrude","CAP_FACE",FACE,{"disambiguationData":[OSD([subQ0])],"isStart":false})],"blendedInto":[makeQuery(id+"F3.opExtrude","CAP_FACE",FACE,{"disambiguationData":[OSD([subQ0])],"isStart":false})]});}
            var Q2;
            {var subQ0=sQuery(id+"F1.wireOp",EDGE,"E206.15.4.0");Q2=makeQuery(id+"F4.opChamfer","BLEND_EDGE",EDGE,{"blendedFrom":[makeQuery(id+"F3.opExtrude","CAP_EDGE",EDGE,{"disambiguationData":[OSD([subQ0])],"isStart":false}),makeQuery(id+"F3.opExtrude","CAP_FACE",FACE,{"disambiguationData":[OSD([subQ0])],"isStart":false})],"blendedInto":[makeQuery(id+"F3.opExtrude","CAP_FACE",FACE,{"disambiguationData":[OSD([subQ0])],"isStart":false})]});}
            var Q3;
            {var subQ0=sQuery(id+"F1.wireOp",EDGE,"E206.13.4.0");Q3=makeQuery(id+"F4.opChamfer","BLEND_EDGE",EDGE,{"blendedFrom":[makeQuery(id+"F3.opExtrude","CAP_EDGE",EDGE,{"disambiguationData":[OSD([subQ0])],"isStart":false}),makeQuery(id+"F3.opExtrude","CAP_FACE",FACE,{"disambiguationData":[OSD([subQ0])],"isStart":false})],"blendedInto":[makeQuery(id+"F3.opExtrude","CAP_FACE",FACE,{"disambiguationData":[OSD([subQ0])],"isStart":false})]});}
            var Q4;
            {var subQ0=sQuery(id+"F1.wireOp",EDGE,"E206.14.3.0");Q4=makeQuery(id+"F4.opChamfer","BLEND_EDGE",EDGE,{"blendedFrom":[makeQuery(id+"F3.opExtrude","CAP_EDGE",EDGE,{"disambiguationData":[OSD([subQ0])],"isStart":false}),makeQuery(id+"F3.opExtrude","CAP_FACE",FACE,{"disambiguationData":[OSD([subQ0])],"isStart":false})],"blendedInto":[makeQuery(id+"F3.opExtrude","CAP_FACE",FACE,{"disambiguationData":[OSD([subQ0])],"isStart":false})]});}
            var Q5;
            {var subQ0=sQuery(id+"F1.wireOp",EDGE,"E206.15.3.0");Q5=makeQuery(id+"F4.opChamfer","BLEND_EDGE",EDGE,{"blendedFrom":[makeQuery(id+"F3.opExtrude","CAP_EDGE",EDGE,{"disambiguationData":[OSD([subQ0])],"isStart":false}),makeQuery(id+"F3.opExtrude","CAP_FACE",FACE,{"disambiguationData":[OSD([subQ0])],"isStart":false})],"blendedInto":[makeQuery(id+"F3.opExtrude","CAP_FACE",FACE,{"disambiguationData":[OSD([subQ0])],"isStart":false})]});}
            var Q6;
            {var subQ0=sQuery(id+"F1.wireOp",EDGE,"E206.16.3.0");Q6=makeQuery(id+"F4.opChamfer","BLEND_EDGE",EDGE,{"blendedFrom":[makeQuery(id+"F3.opExtrude","CAP_EDGE",EDGE,{"disambiguationData":[OSD([subQ0])],"isStart":false}),makeQuery(id+"F3.opExtrude","CAP_FACE",FACE,{"disambiguationData":[OSD([subQ0])],"isStart":false})],"blendedInto":[makeQuery(id+"F3.opExtrude","CAP_FACE",FACE,{"disambiguationData":[OSD([subQ0])],"isStart":false})]});}
            var Q7;
            {var subQ0=sQuery(id+"F1.wireOp",EDGE,"E206.16.5.0");Q7=makeQuery(id+"F4.opChamfer","BLEND_EDGE",EDGE,{"blendedFrom":[makeQuery(id+"F3.opExtrude","CAP_EDGE",EDGE,{"disambiguationData":[OSD([subQ0])],"isStart":false}),makeQuery(id+"F3.opExtrude","CAP_FACE",FACE,{"disambiguationData":[OSD([subQ0])],"isStart":false})],"blendedInto":[makeQuery(id+"F3.opExtrude","CAP_FACE",FACE,{"disambiguationData":[OSD([subQ0])],"isStart":false})]});}
            var Q8;
            {var subQ0=sQuery(id+"F1.wireOp",EDGE,"E206.15.5.0");Q8=makeQuery(id+"F4.opChamfer","BLEND_EDGE",EDGE,{"blendedFrom":[makeQuery(id+"F3.opExtrude","CAP_EDGE",EDGE,{"disambiguationData":[OSD([subQ0])],"isStart":false}),makeQuery(id+"F3.opExtrude","CAP_FACE",FACE,{"disambiguationData":[OSD([subQ0])],"isStart":false})],"blendedInto":[makeQuery(id+"F3.opExtrude","CAP_FACE",FACE,{"disambiguationData":[OSD([subQ0])],"isStart":false})]});}
            var Q9;
            {var subQ0=sQuery(id+"F1.wireOp",EDGE,"E206.14.5.0");Q9=makeQuery(id+"F4.opChamfer","BLEND_EDGE",EDGE,{"blendedFrom":[makeQuery(id+"F3.opExtrude","CAP_EDGE",EDGE,{"disambiguationData":[OSD([subQ0])],"isStart":false}),makeQuery(id+"F3.opExtrude","CAP_FACE",FACE,{"disambiguationData":[OSD([subQ0])],"isStart":false})],"blendedInto":[makeQuery(id+"F3.opExtrude","CAP_FACE",FACE,{"disambiguationData":[OSD([subQ0])],"isStart":false})]});}
            var Q10;
            {var subQ0=sQuery(id+"F1.wireOp",EDGE,"E206.13.5.0");Q10=makeQuery(id+"F4.opChamfer","BLEND_EDGE",EDGE,{"blendedFrom":[makeQuery(id+"F3.opExtrude","CAP_EDGE",EDGE,{"disambiguationData":[OSD([subQ0])],"isStart":false}),makeQuery(id+"F3.opExtrude","CAP_FACE",FACE,{"disambiguationData":[OSD([subQ0])],"isStart":false})],"blendedInto":[makeQuery(id+"F3.opExtrude","CAP_FACE",FACE,{"disambiguationData":[OSD([subQ0])],"isStart":false})]});}
            var Q11;
            {var subQ0=sQuery(id+"F1.wireOp",EDGE,"E206.12.6.0");Q11=makeQuery(id+"F4.opChamfer","BLEND_EDGE",EDGE,{"blendedFrom":[makeQuery(id+"F3.opExtrude","CAP_EDGE",EDGE,{"disambiguationData":[OSD([subQ0])],"isStart":false}),makeQuery(id+"F3.opExtrude","CAP_FACE",FACE,{"disambiguationData":[OSD([subQ0])],"isStart":false})],"blendedInto":[makeQuery(id+"F3.opExtrude","CAP_FACE",FACE,{"disambiguationData":[OSD([subQ0])],"isStart":false})]});}
            var Q12;
            {var subQ0=sQuery(id+"F1.wireOp",EDGE,"E206.12.7.0");Q12=makeQuery(id+"F4.opChamfer","BLEND_EDGE",EDGE,{"blendedFrom":[makeQuery(id+"F3.opExtrude","CAP_EDGE",EDGE,{"disambiguationData":[OSD([subQ0])],"isStart":false}),makeQuery(id+"F3.opExtrude","CAP_FACE",FACE,{"disambiguationData":[OSD([subQ0])],"isStart":false})],"blendedInto":[makeQuery(id+"F3.opExtrude","CAP_FACE",FACE,{"disambiguationData":[OSD([subQ0])],"isStart":false})]});}
            var Q13;
            {var subQ0=sQuery(id+"F1.wireOp",EDGE,"E206.13.7.0");Q13=makeQuery(id+"F4.opChamfer","BLEND_EDGE",EDGE,{"blendedFrom":[makeQuery(id+"F3.opExtrude","CAP_EDGE",EDGE,{"disambiguationData":[OSD([subQ0])],"isStart":false}),makeQuery(id+"F3.opExtrude","CAP_FACE",FACE,{"disambiguationData":[OSD([subQ0])],"isStart":false})],"blendedInto":[makeQuery(id+"F3.opExtrude","CAP_FACE",FACE,{"disambiguationData":[OSD([subQ0])],"isStart":false})]});}
            var Q14;
            {var subQ0=sQuery(id+"F1.wireOp",EDGE,"E206.14.7.0");Q14=makeQuery(id+"F4.opChamfer","BLEND_EDGE",EDGE,{"blendedFrom":[makeQuery(id+"F3.opExtrude","CAP_EDGE",EDGE,{"disambiguationData":[OSD([subQ0])],"isStart":false}),makeQuery(id+"F3.opExtrude","CAP_FACE",FACE,{"disambiguationData":[OSD([subQ0])],"isStart":false})],"blendedInto":[makeQuery(id+"F3.opExtrude","CAP_FACE",FACE,{"disambiguationData":[OSD([subQ0])],"isStart":false})]});}
            var Q15;
            {var subQ0=sQuery(id+"F1.wireOp",EDGE,"E206.15.7.0");Q15=makeQuery(id+"F4.opChamfer","BLEND_EDGE",EDGE,{"blendedFrom":[makeQuery(id+"F3.opExtrude","CAP_EDGE",EDGE,{"disambiguationData":[OSD([subQ0])],"isStart":false}),makeQuery(id+"F3.opExtrude","CAP_FACE",FACE,{"disambiguationData":[OSD([subQ0])],"isStart":false})],"blendedInto":[makeQuery(id+"F3.opExtrude","CAP_FACE",FACE,{"disambiguationData":[OSD([subQ0])],"isStart":false})]});}
            var Q16;
            {var subQ0=sQuery(id+"F1.wireOp",EDGE,"E206.16.7.0");Q16=makeQuery(id+"F4.opChamfer","BLEND_EDGE",EDGE,{"blendedFrom":[makeQuery(id+"F3.opExtrude","CAP_EDGE",EDGE,{"disambiguationData":[OSD([subQ0])],"isStart":false}),makeQuery(id+"F3.opExtrude","CAP_FACE",FACE,{"disambiguationData":[OSD([subQ0])],"isStart":false})],"blendedInto":[makeQuery(id+"F3.opExtrude","CAP_FACE",FACE,{"disambiguationData":[OSD([subQ0])],"isStart":false})]});}
            var Q17;
            {var subQ0=sQuery(id+"F1.wireOp",EDGE,"E206.13.6.0");Q17=makeQuery(id+"F4.opChamfer","BLEND_EDGE",EDGE,{"blendedFrom":[makeQuery(id+"F3.opExtrude","CAP_EDGE",EDGE,{"disambiguationData":[OSD([subQ0])],"isStart":false}),makeQuery(id+"F3.opExtrude","CAP_FACE",FACE,{"disambiguationData":[OSD([subQ0])],"isStart":false})],"blendedInto":[makeQuery(id+"F3.opExtrude","CAP_FACE",FACE,{"disambiguationData":[OSD([subQ0])],"isStart":false})]});}
            var Q18;
            {var subQ0=sQuery(id+"F1.wireOp",EDGE,"E206.14.6.0");Q18=makeQuery(id+"F4.opChamfer","BLEND_EDGE",EDGE,{"blendedFrom":[makeQuery(id+"F3.opExtrude","CAP_EDGE",EDGE,{"disambiguationData":[OSD([subQ0])],"isStart":false}),makeQuery(id+"F3.opExtrude","CAP_FACE",FACE,{"disambiguationData":[OSD([subQ0])],"isStart":false})],"blendedInto":[makeQuery(id+"F3.opExtrude","CAP_FACE",FACE,{"disambiguationData":[OSD([subQ0])],"isStart":false})]});}
            var Q19;
            {var subQ0=sQuery(id+"F1.wireOp",EDGE,"E206.15.6.0");Q19=makeQuery(id+"F4.opChamfer","BLEND_EDGE",EDGE,{"blendedFrom":[makeQuery(id+"F3.opExtrude","CAP_EDGE",EDGE,{"disambiguationData":[OSD([subQ0])],"isStart":false}),makeQuery(id+"F3.opExtrude","CAP_FACE",FACE,{"disambiguationData":[OSD([subQ0])],"isStart":false})],"blendedInto":[makeQuery(id+"F3.opExtrude","CAP_FACE",FACE,{"disambiguationData":[OSD([subQ0])],"isStart":false})]});}
            var Q20;
            {var subQ0=sQuery(id+"F1.wireOp",EDGE,"E206.16.6.0");Q20=makeQuery(id+"F4.opChamfer","BLEND_EDGE",EDGE,{"blendedFrom":[makeQuery(id+"F3.opExtrude","CAP_EDGE",EDGE,{"disambiguationData":[OSD([subQ0])],"isStart":false}),makeQuery(id+"F3.opExtrude","CAP_FACE",FACE,{"disambiguationData":[OSD([subQ0])],"isStart":false})],"blendedInto":[makeQuery(id+"F3.opExtrude","CAP_FACE",FACE,{"disambiguationData":[OSD([subQ0])],"isStart":false})]});}
            var Q21;
            {var subQ0=sQuery(id+"F1.wireOp",EDGE,"E206.16.8.0");Q21=makeQuery(id+"F4.opChamfer","BLEND_EDGE",EDGE,{"blendedFrom":[makeQuery(id+"F3.opExtrude","CAP_EDGE",EDGE,{"disambiguationData":[OSD([subQ0])],"isStart":false}),makeQuery(id+"F3.opExtrude","CAP_FACE",FACE,{"disambiguationData":[OSD([subQ0])],"isStart":false})],"blendedInto":[makeQuery(id+"F3.opExtrude","CAP_FACE",FACE,{"disambiguationData":[OSD([subQ0])],"isStart":false})]});}
            var Q22;
            {var subQ0=sQuery(id+"F1.wireOp",EDGE,"E206.15.8.0");Q22=makeQuery(id+"F4.opChamfer","BLEND_EDGE",EDGE,{"blendedFrom":[makeQuery(id+"F3.opExtrude","CAP_EDGE",EDGE,{"disambiguationData":[OSD([subQ0])],"isStart":false}),makeQuery(id+"F3.opExtrude","CAP_FACE",FACE,{"disambiguationData":[OSD([subQ0])],"isStart":false})],"blendedInto":[makeQuery(id+"F3.opExtrude","CAP_FACE",FACE,{"disambiguationData":[OSD([subQ0])],"isStart":false})]});}
            var Q23;
            {var subQ0=sQuery(id+"F1.wireOp",EDGE,"E206.14.8.0");Q23=makeQuery(id+"F4.opChamfer","BLEND_EDGE",EDGE,{"blendedFrom":[makeQuery(id+"F3.opExtrude","CAP_EDGE",EDGE,{"disambiguationData":[OSD([subQ0])],"isStart":false}),makeQuery(id+"F3.opExtrude","CAP_FACE",FACE,{"disambiguationData":[OSD([subQ0])],"isStart":false})],"blendedInto":[makeQuery(id+"F3.opExtrude","CAP_FACE",FACE,{"disambiguationData":[OSD([subQ0])],"isStart":false})]});}
            var Q24;
            {var subQ0=sQuery(id+"F1.wireOp",EDGE,"E206.13.8.0");Q24=makeQuery(id+"F4.opChamfer","BLEND_EDGE",EDGE,{"blendedFrom":[makeQuery(id+"F3.opExtrude","CAP_EDGE",EDGE,{"disambiguationData":[OSD([subQ0])],"isStart":false}),makeQuery(id+"F3.opExtrude","CAP_FACE",FACE,{"disambiguationData":[OSD([subQ0])],"isStart":false})],"blendedInto":[makeQuery(id+"F3.opExtrude","CAP_FACE",FACE,{"disambiguationData":[OSD([subQ0])],"isStart":false})]});}
            var Q25;
            {var subQ0=sQuery(id+"F1.wireOp",EDGE,"E206.12.8.0");Q25=makeQuery(id+"F4.opChamfer","BLEND_EDGE",EDGE,{"blendedFrom":[makeQuery(id+"F3.opExtrude","CAP_EDGE",EDGE,{"disambiguationData":[OSD([subQ0])],"isStart":false}),makeQuery(id+"F3.opExtrude","CAP_FACE",FACE,{"disambiguationData":[OSD([subQ0])],"isStart":false})],"blendedInto":[makeQuery(id+"F3.opExtrude","CAP_FACE",FACE,{"disambiguationData":[OSD([subQ0])],"isStart":false})]});}
            var Q26;
            {var subQ0=sQuery(id+"F1.wireOp",EDGE,"E206.12.5.0");Q26=makeQuery(id+"F4.opChamfer","BLEND_EDGE",EDGE,{"blendedFrom":[makeQuery(id+"F3.opExtrude","CAP_EDGE",EDGE,{"disambiguationData":[OSD([subQ0])],"isStart":false}),makeQuery(id+"F3.opExtrude","CAP_FACE",FACE,{"disambiguationData":[OSD([subQ0])],"isStart":false})],"blendedInto":[makeQuery(id+"F3.opExtrude","CAP_FACE",FACE,{"disambiguationData":[OSD([subQ0])],"isStart":false})]});}
            var Q27;
            {var subQ0=sQuery(id+"F1.wireOp",EDGE,"E206.12.4.0");Q27=makeQuery(id+"F4.opChamfer","BLEND_EDGE",EDGE,{"blendedFrom":[makeQuery(id+"F3.opExtrude","CAP_EDGE",EDGE,{"disambiguationData":[OSD([subQ0])],"isStart":false}),makeQuery(id+"F3.opExtrude","CAP_FACE",FACE,{"disambiguationData":[OSD([subQ0])],"isStart":false})],"blendedInto":[makeQuery(id+"F3.opExtrude","CAP_FACE",FACE,{"disambiguationData":[OSD([subQ0])],"isStart":false})]});}
            var Q28;
            {var subQ0=sQuery(id+"F1.wireOp",EDGE,"E206.12.3.0");Q28=makeQuery(id+"F4.opChamfer","BLEND_EDGE",EDGE,{"blendedFrom":[makeQuery(id+"F3.opExtrude","CAP_EDGE",EDGE,{"disambiguationData":[OSD([subQ0])],"isStart":false}),makeQuery(id+"F3.opExtrude","CAP_FACE",FACE,{"disambiguationData":[OSD([subQ0])],"isStart":false})],"blendedInto":[makeQuery(id+"F3.opExtrude","CAP_FACE",FACE,{"disambiguationData":[OSD([subQ0])],"isStart":false})]});}
            var Q29;
            {var subQ0=sQuery(id+"F1.wireOp",EDGE,"E206.13.3.0");Q29=makeQuery(id+"F4.opChamfer","BLEND_EDGE",EDGE,{"blendedFrom":[makeQuery(id+"F3.opExtrude","CAP_EDGE",EDGE,{"disambiguationData":[OSD([subQ0])],"isStart":false}),makeQuery(id+"F3.opExtrude","CAP_FACE",FACE,{"disambiguationData":[OSD([subQ0])],"isStart":false})],"blendedInto":[makeQuery(id+"F3.opExtrude","CAP_FACE",FACE,{"disambiguationData":[OSD([subQ0])],"isStart":false})]});}
            var Q30;
            {var subQ0=sQuery(id+"F1.wireOp",EDGE,"E206.12.2.0");Q30=makeQuery(id+"F4.opChamfer","BLEND_EDGE",EDGE,{"blendedFrom":[makeQuery(id+"F3.opExtrude","CAP_EDGE",EDGE,{"disambiguationData":[OSD([subQ0])],"isStart":false}),makeQuery(id+"F3.opExtrude","CAP_FACE",FACE,{"disambiguationData":[OSD([subQ0])],"isStart":false})],"blendedInto":[makeQuery(id+"F3.opExtrude","CAP_FACE",FACE,{"disambiguationData":[OSD([subQ0])],"isStart":false})]});}
            var Q31;
            {var subQ0=sQuery(id+"F1.wireOp",EDGE,"E206.13.2.0");Q31=makeQuery(id+"F4.opChamfer","BLEND_EDGE",EDGE,{"blendedFrom":[makeQuery(id+"F3.opExtrude","CAP_EDGE",EDGE,{"disambiguationData":[OSD([subQ0])],"isStart":false}),makeQuery(id+"F3.opExtrude","CAP_FACE",FACE,{"disambiguationData":[OSD([subQ0])],"isStart":false})],"blendedInto":[makeQuery(id+"F3.opExtrude","CAP_FACE",FACE,{"disambiguationData":[OSD([subQ0])],"isStart":false})]});}
            var Q32;
            {var subQ0=sQuery(id+"F1.wireOp",EDGE,"E206.14.2.0");Q32=makeQuery(id+"F4.opChamfer","BLEND_EDGE",EDGE,{"blendedFrom":[makeQuery(id+"F3.opExtrude","CAP_EDGE",EDGE,{"disambiguationData":[OSD([subQ0])],"isStart":false}),makeQuery(id+"F3.opExtrude","CAP_FACE",FACE,{"disambiguationData":[OSD([subQ0])],"isStart":false})],"blendedInto":[makeQuery(id+"F3.opExtrude","CAP_FACE",FACE,{"disambiguationData":[OSD([subQ0])],"isStart":false})]});}
            var Q33;
            {var subQ0=sQuery(id+"F1.wireOp",EDGE,"E206.15.2.0");Q33=makeQuery(id+"F4.opChamfer","BLEND_EDGE",EDGE,{"blendedFrom":[makeQuery(id+"F3.opExtrude","CAP_EDGE",EDGE,{"disambiguationData":[OSD([subQ0])],"isStart":false}),makeQuery(id+"F3.opExtrude","CAP_FACE",FACE,{"disambiguationData":[OSD([subQ0])],"isStart":false})],"blendedInto":[makeQuery(id+"F3.opExtrude","CAP_FACE",FACE,{"disambiguationData":[OSD([subQ0])],"isStart":false})]});}
            var Q34;
            {var subQ0=sQuery(id+"F1.wireOp",EDGE,"E206.16.2.0");Q34=makeQuery(id+"F4.opChamfer","BLEND_EDGE",EDGE,{"blendedFrom":[makeQuery(id+"F3.opExtrude","CAP_EDGE",EDGE,{"disambiguationData":[OSD([subQ0])],"isStart":false}),makeQuery(id+"F3.opExtrude","CAP_FACE",FACE,{"disambiguationData":[OSD([subQ0])],"isStart":false})],"blendedInto":[makeQuery(id+"F3.opExtrude","CAP_FACE",FACE,{"disambiguationData":[OSD([subQ0])],"isStart":false})]});}
            var Q35;
            {var subQ0=sQuery(id+"F1.wireOp",EDGE,"E206.16.1.0");Q35=makeQuery(id+"F4.opChamfer","BLEND_EDGE",EDGE,{"blendedFrom":[makeQuery(id+"F3.opExtrude","CAP_EDGE",EDGE,{"disambiguationData":[OSD([subQ0])],"isStart":false}),makeQuery(id+"F3.opExtrude","CAP_FACE",FACE,{"disambiguationData":[OSD([subQ0])],"isStart":false})],"blendedInto":[makeQuery(id+"F3.opExtrude","CAP_FACE",FACE,{"disambiguationData":[OSD([subQ0])],"isStart":false})]});}
            var Q36;
            {var subQ0=sQuery(id+"F1.wireOp",EDGE,"E206.16.0.0");Q36=makeQuery(id+"F4.opChamfer","BLEND_EDGE",EDGE,{"blendedFrom":[makeQuery(id+"F3.opExtrude","CAP_EDGE",EDGE,{"disambiguationData":[OSD([subQ0])],"isStart":false}),makeQuery(id+"F3.opExtrude","CAP_FACE",FACE,{"disambiguationData":[OSD([subQ0])],"isStart":false})],"blendedInto":[makeQuery(id+"F3.opExtrude","CAP_FACE",FACE,{"disambiguationData":[OSD([subQ0])],"isStart":false})]});}
            var Q37;
            {var subQ0=sQuery(id+"F1.wireOp",EDGE,"E206.15.0.0");Q37=makeQuery(id+"F4.opChamfer","BLEND_EDGE",EDGE,{"blendedFrom":[makeQuery(id+"F3.opExtrude","CAP_EDGE",EDGE,{"disambiguationData":[OSD([subQ0])],"isStart":false}),makeQuery(id+"F3.opExtrude","CAP_FACE",FACE,{"disambiguationData":[OSD([subQ0])],"isStart":false})],"blendedInto":[makeQuery(id+"F3.opExtrude","CAP_FACE",FACE,{"disambiguationData":[OSD([subQ0])],"isStart":false})]});}
            var Q38;
            {var subQ0=sQuery(id+"F1.wireOp",EDGE,"E206.15.1.0");Q38=makeQuery(id+"F4.opChamfer","BLEND_EDGE",EDGE,{"blendedFrom":[makeQuery(id+"F3.opExtrude","CAP_EDGE",EDGE,{"disambiguationData":[OSD([subQ0])],"isStart":false}),makeQuery(id+"F3.opExtrude","CAP_FACE",FACE,{"disambiguationData":[OSD([subQ0])],"isStart":false})],"blendedInto":[makeQuery(id+"F3.opExtrude","CAP_FACE",FACE,{"disambiguationData":[OSD([subQ0])],"isStart":false})]});}
            var Q39;
            {var subQ0=sQuery(id+"F1.wireOp",EDGE,"E206.14.1.0");Q39=makeQuery(id+"F4.opChamfer","BLEND_EDGE",EDGE,{"blendedFrom":[makeQuery(id+"F3.opExtrude","CAP_EDGE",EDGE,{"disambiguationData":[OSD([subQ0])],"isStart":false}),makeQuery(id+"F3.opExtrude","CAP_FACE",FACE,{"disambiguationData":[OSD([subQ0])],"isStart":false})],"blendedInto":[makeQuery(id+"F3.opExtrude","CAP_FACE",FACE,{"disambiguationData":[OSD([subQ0])],"isStart":false})]});}
            var Q40;
            {var subQ0=sQuery(id+"F1.wireOp",EDGE,"E206.14.0.0");Q40=makeQuery(id+"F4.opChamfer","BLEND_EDGE",EDGE,{"blendedFrom":[makeQuery(id+"F3.opExtrude","CAP_EDGE",EDGE,{"disambiguationData":[OSD([subQ0])],"isStart":false}),makeQuery(id+"F3.opExtrude","CAP_FACE",FACE,{"disambiguationData":[OSD([subQ0])],"isStart":false})],"blendedInto":[makeQuery(id+"F3.opExtrude","CAP_FACE",FACE,{"disambiguationData":[OSD([subQ0])],"isStart":false})]});}
            var Q41;
            {var subQ0=sQuery(id+"F1.wireOp",EDGE,"E206.13.0.0");Q41=makeQuery(id+"F4.opChamfer","BLEND_EDGE",EDGE,{"blendedFrom":[makeQuery(id+"F3.opExtrude","CAP_EDGE",EDGE,{"disambiguationData":[OSD([subQ0])],"isStart":false}),makeQuery(id+"F3.opExtrude","CAP_FACE",FACE,{"disambiguationData":[OSD([subQ0])],"isStart":false})],"blendedInto":[makeQuery(id+"F3.opExtrude","CAP_FACE",FACE,{"disambiguationData":[OSD([subQ0])],"isStart":false})]});}
            var Q42;
            {var subQ0=sQuery(id+"F1.wireOp",EDGE,"E206.13.1.0");Q42=makeQuery(id+"F4.opChamfer","BLEND_EDGE",EDGE,{"blendedFrom":[makeQuery(id+"F3.opExtrude","CAP_EDGE",EDGE,{"disambiguationData":[OSD([subQ0])],"isStart":false}),makeQuery(id+"F3.opExtrude","CAP_FACE",FACE,{"disambiguationData":[OSD([subQ0])],"isStart":false})],"blendedInto":[makeQuery(id+"F3.opExtrude","CAP_FACE",FACE,{"disambiguationData":[OSD([subQ0])],"isStart":false})]});}
            var Q43;
            {var subQ0=sQuery(id+"F1.wireOp",EDGE,"E206.12.1.0");Q43=makeQuery(id+"F4.opChamfer","BLEND_EDGE",EDGE,{"blendedFrom":[makeQuery(id+"F3.opExtrude","CAP_EDGE",EDGE,{"disambiguationData":[OSD([subQ0])],"isStart":false}),makeQuery(id+"F3.opExtrude","CAP_FACE",FACE,{"disambiguationData":[OSD([subQ0])],"isStart":false})],"blendedInto":[makeQuery(id+"F3.opExtrude","CAP_FACE",FACE,{"disambiguationData":[OSD([subQ0])],"isStart":false})]});}
            var Q44;
            {var subQ0=sQuery(id+"F1.wireOp",EDGE,"E206.12.0.0");Q44=makeQuery(id+"F4.opChamfer","BLEND_EDGE",EDGE,{"blendedFrom":[makeQuery(id+"F3.opExtrude","CAP_EDGE",EDGE,{"disambiguationData":[OSD([subQ0])],"isStart":false}),makeQuery(id+"F3.opExtrude","CAP_FACE",FACE,{"disambiguationData":[OSD([subQ0])],"isStart":false})],"blendedInto":[makeQuery(id+"F3.opExtrude","CAP_FACE",FACE,{"disambiguationData":[OSD([subQ0])],"isStart":false})]});}
            var Q45;
            {var subQ0=sQuery(id+"F1.wireOp",EDGE,"E206.11.8.0");Q45=makeQuery(id+"F4.opChamfer","BLEND_EDGE",EDGE,{"blendedFrom":[makeQuery(id+"F3.opExtrude","CAP_EDGE",EDGE,{"disambiguationData":[OSD([subQ0])],"isStart":false}),makeQuery(id+"F3.opExtrude","CAP_FACE",FACE,{"disambiguationData":[OSD([subQ0])],"isStart":false})],"blendedInto":[makeQuery(id+"F3.opExtrude","CAP_FACE",FACE,{"disambiguationData":[OSD([subQ0])],"isStart":false})]});}
            var Q46;
            {var subQ0=sQuery(id+"F1.wireOp",EDGE,"E206.10.8.0");Q46=makeQuery(id+"F4.opChamfer","BLEND_EDGE",EDGE,{"blendedFrom":[makeQuery(id+"F3.opExtrude","CAP_EDGE",EDGE,{"disambiguationData":[OSD([subQ0])],"isStart":false}),makeQuery(id+"F3.opExtrude","CAP_FACE",FACE,{"disambiguationData":[OSD([subQ0])],"isStart":false})],"blendedInto":[makeQuery(id+"F3.opExtrude","CAP_FACE",FACE,{"disambiguationData":[OSD([subQ0])],"isStart":false})]});}
            var Q47;
            {var subQ0=sQuery(id+"F1.wireOp",EDGE,"E206.10.7.0");Q47=makeQuery(id+"F4.opChamfer","BLEND_EDGE",EDGE,{"blendedFrom":[makeQuery(id+"F3.opExtrude","CAP_EDGE",EDGE,{"disambiguationData":[OSD([subQ0])],"isStart":false}),makeQuery(id+"F3.opExtrude","CAP_FACE",FACE,{"disambiguationData":[OSD([subQ0])],"isStart":false})],"blendedInto":[makeQuery(id+"F3.opExtrude","CAP_FACE",FACE,{"disambiguationData":[OSD([subQ0])],"isStart":false})]});}
            var Q48;
            {var subQ0=sQuery(id+"F1.wireOp",EDGE,"E206.11.7.0");Q48=makeQuery(id+"F4.opChamfer","BLEND_EDGE",EDGE,{"blendedFrom":[makeQuery(id+"F3.opExtrude","CAP_EDGE",EDGE,{"disambiguationData":[OSD([subQ0])],"isStart":false}),makeQuery(id+"F3.opExtrude","CAP_FACE",FACE,{"disambiguationData":[OSD([subQ0])],"isStart":false})],"blendedInto":[makeQuery(id+"F3.opExtrude","CAP_FACE",FACE,{"disambiguationData":[OSD([subQ0])],"isStart":false})]});}
            var Q49;
            {var subQ0=sQuery(id+"F1.wireOp",EDGE,"E206.10.6.0");Q49=makeQuery(id+"F4.opChamfer","BLEND_EDGE",EDGE,{"blendedFrom":[makeQuery(id+"F3.opExtrude","CAP_EDGE",EDGE,{"disambiguationData":[OSD([subQ0])],"isStart":false}),makeQuery(id+"F3.opExtrude","CAP_FACE",FACE,{"disambiguationData":[OSD([subQ0])],"isStart":false})],"blendedInto":[makeQuery(id+"F3.opExtrude","CAP_FACE",FACE,{"disambiguationData":[OSD([subQ0])],"isStart":false})]});}
            var Q50;
            {var subQ0=sQuery(id+"F1.wireOp",EDGE,"E206.11.6.0");Q50=makeQuery(id+"F4.opChamfer","BLEND_EDGE",EDGE,{"blendedFrom":[makeQuery(id+"F3.opExtrude","CAP_EDGE",EDGE,{"disambiguationData":[OSD([subQ0])],"isStart":false}),makeQuery(id+"F3.opExtrude","CAP_FACE",FACE,{"disambiguationData":[OSD([subQ0])],"isStart":false})],"blendedInto":[makeQuery(id+"F3.opExtrude","CAP_FACE",FACE,{"disambiguationData":[OSD([subQ0])],"isStart":false})]});}
            var Q51;
            {var subQ0=sQuery(id+"F1.wireOp",EDGE,"E206.10.5.0");Q51=makeQuery(id+"F4.opChamfer","BLEND_EDGE",EDGE,{"blendedFrom":[makeQuery(id+"F3.opExtrude","CAP_EDGE",EDGE,{"disambiguationData":[OSD([subQ0])],"isStart":false}),makeQuery(id+"F3.opExtrude","CAP_FACE",FACE,{"disambiguationData":[OSD([subQ0])],"isStart":false})],"blendedInto":[makeQuery(id+"F3.opExtrude","CAP_FACE",FACE,{"disambiguationData":[OSD([subQ0])],"isStart":false})]});}
            var Q52;
            {var subQ0=sQuery(id+"F1.wireOp",EDGE,"E206.11.5.0");Q52=makeQuery(id+"F4.opChamfer","BLEND_EDGE",EDGE,{"blendedFrom":[makeQuery(id+"F3.opExtrude","CAP_EDGE",EDGE,{"disambiguationData":[OSD([subQ0])],"isStart":false}),makeQuery(id+"F3.opExtrude","CAP_FACE",FACE,{"disambiguationData":[OSD([subQ0])],"isStart":false})],"blendedInto":[makeQuery(id+"F3.opExtrude","CAP_FACE",FACE,{"disambiguationData":[OSD([subQ0])],"isStart":false})]});}
            var Q53;
            {var subQ0=sQuery(id+"F1.wireOp",EDGE,"E206.10.4.0");Q53=makeQuery(id+"F4.opChamfer","BLEND_EDGE",EDGE,{"blendedFrom":[makeQuery(id+"F3.opExtrude","CAP_EDGE",EDGE,{"disambiguationData":[OSD([subQ0])],"isStart":false}),makeQuery(id+"F3.opExtrude","CAP_FACE",FACE,{"disambiguationData":[OSD([subQ0])],"isStart":false})],"blendedInto":[makeQuery(id+"F3.opExtrude","CAP_FACE",FACE,{"disambiguationData":[OSD([subQ0])],"isStart":false})]});}
            var Q54;
            {var subQ0=sQuery(id+"F1.wireOp",EDGE,"E206.11.4.0");Q54=makeQuery(id+"F4.opChamfer","BLEND_EDGE",EDGE,{"blendedFrom":[makeQuery(id+"F3.opExtrude","CAP_EDGE",EDGE,{"disambiguationData":[OSD([subQ0])],"isStart":false}),makeQuery(id+"F3.opExtrude","CAP_FACE",FACE,{"disambiguationData":[OSD([subQ0])],"isStart":false})],"blendedInto":[makeQuery(id+"F3.opExtrude","CAP_FACE",FACE,{"disambiguationData":[OSD([subQ0])],"isStart":false})]});}
            var Q55;
            {var subQ0=sQuery(id+"F1.wireOp",EDGE,"E206.4.8.0");Q55=makeQuery(id+"F4.opChamfer","BLEND_EDGE",EDGE,{"blendedFrom":[makeQuery(id+"F3.opExtrude","CAP_EDGE",EDGE,{"disambiguationData":[OSD([subQ0])],"isStart":false}),makeQuery(id+"F3.opExtrude","CAP_FACE",FACE,{"disambiguationData":[OSD([subQ0])],"isStart":false})],"blendedInto":[makeQuery(id+"F3.opExtrude","CAP_FACE",FACE,{"disambiguationData":[OSD([subQ0])],"isStart":false})]});}
            var Q56;
            {var subQ0=sQuery(id+"F1.wireOp",EDGE,"E206.5.8.0");Q56=makeQuery(id+"F4.opChamfer","BLEND_EDGE",EDGE,{"blendedFrom":[makeQuery(id+"F3.opExtrude","CAP_EDGE",EDGE,{"disambiguationData":[OSD([subQ0])],"isStart":false}),makeQuery(id+"F3.opExtrude","CAP_FACE",FACE,{"disambiguationData":[OSD([subQ0])],"isStart":false})],"blendedInto":[makeQuery(id+"F3.opExtrude","CAP_FACE",FACE,{"disambiguationData":[OSD([subQ0])],"isStart":false})]});}
            var Q57;
            {var subQ0=sQuery(id+"F1.wireOp",EDGE,"E206.6.8.0");Q57=makeQuery(id+"F4.opChamfer","BLEND_EDGE",EDGE,{"blendedFrom":[makeQuery(id+"F3.opExtrude","CAP_EDGE",EDGE,{"disambiguationData":[OSD([subQ0])],"isStart":false}),makeQuery(id+"F3.opExtrude","CAP_FACE",FACE,{"disambiguationData":[OSD([subQ0])],"isStart":false})],"blendedInto":[makeQuery(id+"F3.opExtrude","CAP_FACE",FACE,{"disambiguationData":[OSD([subQ0])],"isStart":false})]});}
            var Q58;
            {var subQ0=sQuery(id+"F1.wireOp",EDGE,"E206.7.8.0");Q58=makeQuery(id+"F4.opChamfer","BLEND_EDGE",EDGE,{"blendedFrom":[makeQuery(id+"F3.opExtrude","CAP_EDGE",EDGE,{"disambiguationData":[OSD([subQ0])],"isStart":false}),makeQuery(id+"F3.opExtrude","CAP_FACE",FACE,{"disambiguationData":[OSD([subQ0])],"isStart":false})],"blendedInto":[makeQuery(id+"F3.opExtrude","CAP_FACE",FACE,{"disambiguationData":[OSD([subQ0])],"isStart":false})]});}
            var Q59;
            {var subQ0=sQuery(id+"F1.wireOp",EDGE,"E206.8.8.0");Q59=makeQuery(id+"F4.opChamfer","BLEND_EDGE",EDGE,{"blendedFrom":[makeQuery(id+"F3.opExtrude","CAP_EDGE",EDGE,{"disambiguationData":[OSD([subQ0])],"isStart":false}),makeQuery(id+"F3.opExtrude","CAP_FACE",FACE,{"disambiguationData":[OSD([subQ0])],"isStart":false})],"blendedInto":[makeQuery(id+"F3.opExtrude","CAP_FACE",FACE,{"disambiguationData":[OSD([subQ0])],"isStart":false})]});}
            var Q60;
            {var subQ0=sQuery(id+"F1.wireOp",EDGE,"E206.9.8.0");Q60=makeQuery(id+"F4.opChamfer","BLEND_EDGE",EDGE,{"blendedFrom":[makeQuery(id+"F3.opExtrude","CAP_EDGE",EDGE,{"disambiguationData":[OSD([subQ0])],"isStart":false}),makeQuery(id+"F3.opExtrude","CAP_FACE",FACE,{"disambiguationData":[OSD([subQ0])],"isStart":false})],"blendedInto":[makeQuery(id+"F3.opExtrude","CAP_FACE",FACE,{"disambiguationData":[OSD([subQ0])],"isStart":false})]});}
            var Q61;
            {var subQ0=sQuery(id+"F1.wireOp",EDGE,"E206.4.7.0");Q61=makeQuery(id+"F4.opChamfer","BLEND_EDGE",EDGE,{"blendedFrom":[makeQuery(id+"F3.opExtrude","CAP_EDGE",EDGE,{"disambiguationData":[OSD([subQ0])],"isStart":false}),makeQuery(id+"F3.opExtrude","CAP_FACE",FACE,{"disambiguationData":[OSD([subQ0])],"isStart":false})],"blendedInto":[makeQuery(id+"F3.opExtrude","CAP_FACE",FACE,{"disambiguationData":[OSD([subQ0])],"isStart":false})]});}
            var Q62;
            {var subQ0=sQuery(id+"F1.wireOp",EDGE,"E206.5.7.0");Q62=makeQuery(id+"F4.opChamfer","BLEND_EDGE",EDGE,{"blendedFrom":[makeQuery(id+"F3.opExtrude","CAP_EDGE",EDGE,{"disambiguationData":[OSD([subQ0])],"isStart":false}),makeQuery(id+"F3.opExtrude","CAP_FACE",FACE,{"disambiguationData":[OSD([subQ0])],"isStart":false})],"blendedInto":[makeQuery(id+"F3.opExtrude","CAP_FACE",FACE,{"disambiguationData":[OSD([subQ0])],"isStart":false})]});}
            var Q63;
            {var subQ0=sQuery(id+"F1.wireOp",EDGE,"E206.6.7.0");Q63=makeQuery(id+"F4.opChamfer","BLEND_EDGE",EDGE,{"blendedFrom":[makeQuery(id+"F3.opExtrude","CAP_EDGE",EDGE,{"disambiguationData":[OSD([subQ0])],"isStart":false}),makeQuery(id+"F3.opExtrude","CAP_FACE",FACE,{"disambiguationData":[OSD([subQ0])],"isStart":false})],"blendedInto":[makeQuery(id+"F3.opExtrude","CAP_FACE",FACE,{"disambiguationData":[OSD([subQ0])],"isStart":false})]});}
            var Q64;
            {var subQ0=sQuery(id+"F1.wireOp",EDGE,"E206.7.7.0");Q64=makeQuery(id+"F4.opChamfer","BLEND_EDGE",EDGE,{"blendedFrom":[makeQuery(id+"F3.opExtrude","CAP_EDGE",EDGE,{"disambiguationData":[OSD([subQ0])],"isStart":false}),makeQuery(id+"F3.opExtrude","CAP_FACE",FACE,{"disambiguationData":[OSD([subQ0])],"isStart":false})],"blendedInto":[makeQuery(id+"F3.opExtrude","CAP_FACE",FACE,{"disambiguationData":[OSD([subQ0])],"isStart":false})]});}
            var Q65;
            {var subQ0=sQuery(id+"F1.wireOp",EDGE,"E206.8.7.0");Q65=makeQuery(id+"F4.opChamfer","BLEND_EDGE",EDGE,{"blendedFrom":[makeQuery(id+"F3.opExtrude","CAP_EDGE",EDGE,{"disambiguationData":[OSD([subQ0])],"isStart":false}),makeQuery(id+"F3.opExtrude","CAP_FACE",FACE,{"disambiguationData":[OSD([subQ0])],"isStart":false})],"blendedInto":[makeQuery(id+"F3.opExtrude","CAP_FACE",FACE,{"disambiguationData":[OSD([subQ0])],"isStart":false})]});}
            var Q66;
            {var subQ0=sQuery(id+"F1.wireOp",EDGE,"E206.9.7.0");Q66=makeQuery(id+"F4.opChamfer","BLEND_EDGE",EDGE,{"blendedFrom":[makeQuery(id+"F3.opExtrude","CAP_EDGE",EDGE,{"disambiguationData":[OSD([subQ0])],"isStart":false}),makeQuery(id+"F3.opExtrude","CAP_FACE",FACE,{"disambiguationData":[OSD([subQ0])],"isStart":false})],"blendedInto":[makeQuery(id+"F3.opExtrude","CAP_FACE",FACE,{"disambiguationData":[OSD([subQ0])],"isStart":false})]});}
            var Q67;
            {var subQ0=sQuery(id+"F1.wireOp",EDGE,"E206.9.6.0");Q67=makeQuery(id+"F4.opChamfer","BLEND_EDGE",EDGE,{"blendedFrom":[makeQuery(id+"F3.opExtrude","CAP_EDGE",EDGE,{"disambiguationData":[OSD([subQ0])],"isStart":false}),makeQuery(id+"F3.opExtrude","CAP_FACE",FACE,{"disambiguationData":[OSD([subQ0])],"isStart":false})],"blendedInto":[makeQuery(id+"F3.opExtrude","CAP_FACE",FACE,{"disambiguationData":[OSD([subQ0])],"isStart":false})]});}
            var Q68;
            {var subQ0=sQuery(id+"F1.wireOp",EDGE,"E206.8.6.0");Q68=makeQuery(id+"F4.opChamfer","BLEND_EDGE",EDGE,{"blendedFrom":[makeQuery(id+"F3.opExtrude","CAP_EDGE",EDGE,{"disambiguationData":[OSD([subQ0])],"isStart":false}),makeQuery(id+"F3.opExtrude","CAP_FACE",FACE,{"disambiguationData":[OSD([subQ0])],"isStart":false})],"blendedInto":[makeQuery(id+"F3.opExtrude","CAP_FACE",FACE,{"disambiguationData":[OSD([subQ0])],"isStart":false})]});}
            var Q69;
            {var subQ0=sQuery(id+"F1.wireOp",EDGE,"E206.9.0.0");Q69=makeQuery(id+"F4.opChamfer","BLEND_EDGE",EDGE,{"blendedFrom":[makeQuery(id+"F3.opExtrude","CAP_EDGE",EDGE,{"disambiguationData":[OSD([subQ0])],"isStart":false}),makeQuery(id+"F3.opExtrude","CAP_FACE",FACE,{"disambiguationData":[OSD([subQ0])],"isStart":false})],"blendedInto":[makeQuery(id+"F3.opExtrude","CAP_FACE",FACE,{"disambiguationData":[OSD([subQ0])],"isStart":false})]});}
            var Q70;
            {var subQ0=sQuery(id+"F1.wireOp",EDGE,"E206.10.0.0");Q70=makeQuery(id+"F4.opChamfer","BLEND_EDGE",EDGE,{"blendedFrom":[makeQuery(id+"F3.opExtrude","CAP_EDGE",EDGE,{"disambiguationData":[OSD([subQ0])],"isStart":false}),makeQuery(id+"F3.opExtrude","CAP_FACE",FACE,{"disambiguationData":[OSD([subQ0])],"isStart":false})],"blendedInto":[makeQuery(id+"F3.opExtrude","CAP_FACE",FACE,{"disambiguationData":[OSD([subQ0])],"isStart":false})]});}
            var Q71;
            {var subQ0=sQuery(id+"F1.wireOp",EDGE,"E206.11.0.0");Q71=makeQuery(id+"F4.opChamfer","BLEND_EDGE",EDGE,{"blendedFrom":[makeQuery(id+"F3.opExtrude","CAP_EDGE",EDGE,{"disambiguationData":[OSD([subQ0])],"isStart":false}),makeQuery(id+"F3.opExtrude","CAP_FACE",FACE,{"disambiguationData":[OSD([subQ0])],"isStart":false})],"blendedInto":[makeQuery(id+"F3.opExtrude","CAP_FACE",FACE,{"disambiguationData":[OSD([subQ0])],"isStart":false})]});}
            var Q72;
            {var subQ0=sQuery(id+"F1.wireOp",EDGE,"E206.9.1.0");Q72=makeQuery(id+"F4.opChamfer","BLEND_EDGE",EDGE,{"blendedFrom":[makeQuery(id+"F3.opExtrude","CAP_EDGE",EDGE,{"disambiguationData":[OSD([subQ0])],"isStart":false}),makeQuery(id+"F3.opExtrude","CAP_FACE",FACE,{"disambiguationData":[OSD([subQ0])],"isStart":false})],"blendedInto":[makeQuery(id+"F3.opExtrude","CAP_FACE",FACE,{"disambiguationData":[OSD([subQ0])],"isStart":false})]});}
            var Q73;
            {var subQ0=sQuery(id+"F1.wireOp",EDGE,"E206.10.1.0");Q73=makeQuery(id+"F4.opChamfer","BLEND_EDGE",EDGE,{"blendedFrom":[makeQuery(id+"F3.opExtrude","CAP_EDGE",EDGE,{"disambiguationData":[OSD([subQ0])],"isStart":false}),makeQuery(id+"F3.opExtrude","CAP_FACE",FACE,{"disambiguationData":[OSD([subQ0])],"isStart":false})],"blendedInto":[makeQuery(id+"F3.opExtrude","CAP_FACE",FACE,{"disambiguationData":[OSD([subQ0])],"isStart":false})]});}
            var Q74;
            {var subQ0=sQuery(id+"F1.wireOp",EDGE,"E206.11.1.0");Q74=makeQuery(id+"F4.opChamfer","BLEND_EDGE",EDGE,{"blendedFrom":[makeQuery(id+"F3.opExtrude","CAP_EDGE",EDGE,{"disambiguationData":[OSD([subQ0])],"isStart":false}),makeQuery(id+"F3.opExtrude","CAP_FACE",FACE,{"disambiguationData":[OSD([subQ0])],"isStart":false})],"blendedInto":[makeQuery(id+"F3.opExtrude","CAP_FACE",FACE,{"disambiguationData":[OSD([subQ0])],"isStart":false})]});}
            var Q75;
            {var subQ0=sQuery(id+"F1.wireOp",EDGE,"E206.11.2.0");Q75=makeQuery(id+"F4.opChamfer","BLEND_EDGE",EDGE,{"blendedFrom":[makeQuery(id+"F3.opExtrude","CAP_EDGE",EDGE,{"disambiguationData":[OSD([subQ0])],"isStart":false}),makeQuery(id+"F3.opExtrude","CAP_FACE",FACE,{"disambiguationData":[OSD([subQ0])],"isStart":false})],"blendedInto":[makeQuery(id+"F3.opExtrude","CAP_FACE",FACE,{"disambiguationData":[OSD([subQ0])],"isStart":false})]});}
            var Q76;
            {var subQ0=sQuery(id+"F1.wireOp",EDGE,"E206.10.2.0");Q76=makeQuery(id+"F4.opChamfer","BLEND_EDGE",EDGE,{"blendedFrom":[makeQuery(id+"F3.opExtrude","CAP_EDGE",EDGE,{"disambiguationData":[OSD([subQ0])],"isStart":false}),makeQuery(id+"F3.opExtrude","CAP_FACE",FACE,{"disambiguationData":[OSD([subQ0])],"isStart":false})],"blendedInto":[makeQuery(id+"F3.opExtrude","CAP_FACE",FACE,{"disambiguationData":[OSD([subQ0])],"isStart":false})]});}
            var Q77;
            {var subQ0=sQuery(id+"F1.wireOp",EDGE,"E206.9.2.0");Q77=makeQuery(id+"F4.opChamfer","BLEND_EDGE",EDGE,{"blendedFrom":[makeQuery(id+"F3.opExtrude","CAP_EDGE",EDGE,{"disambiguationData":[OSD([subQ0])],"isStart":false}),makeQuery(id+"F3.opExtrude","CAP_FACE",FACE,{"disambiguationData":[OSD([subQ0])],"isStart":false})],"blendedInto":[makeQuery(id+"F3.opExtrude","CAP_FACE",FACE,{"disambiguationData":[OSD([subQ0])],"isStart":false})]});}
            var Q78;
            {var subQ0=sQuery(id+"F1.wireOp",EDGE,"E206.8.2.0");Q78=makeQuery(id+"F4.opChamfer","BLEND_EDGE",EDGE,{"blendedFrom":[makeQuery(id+"F3.opExtrude","CAP_EDGE",EDGE,{"disambiguationData":[OSD([subQ0])],"isStart":false}),makeQuery(id+"F3.opExtrude","CAP_FACE",FACE,{"disambiguationData":[OSD([subQ0])],"isStart":false})],"blendedInto":[makeQuery(id+"F3.opExtrude","CAP_FACE",FACE,{"disambiguationData":[OSD([subQ0])],"isStart":false})]});}
            var Q79;
            {var subQ0=sQuery(id+"F1.wireOp",EDGE,"E206.8.1.0");Q79=makeQuery(id+"F4.opChamfer","BLEND_EDGE",EDGE,{"blendedFrom":[makeQuery(id+"F3.opExtrude","CAP_EDGE",EDGE,{"disambiguationData":[OSD([subQ0])],"isStart":false}),makeQuery(id+"F3.opExtrude","CAP_FACE",FACE,{"disambiguationData":[OSD([subQ0])],"isStart":false})],"blendedInto":[makeQuery(id+"F3.opExtrude","CAP_FACE",FACE,{"disambiguationData":[OSD([subQ0])],"isStart":false})]});}
            var Q80;
            {var subQ0=sQuery(id+"F1.wireOp",EDGE,"E206.8.0.0");Q80=makeQuery(id+"F4.opChamfer","BLEND_EDGE",EDGE,{"blendedFrom":[makeQuery(id+"F3.opExtrude","CAP_EDGE",EDGE,{"disambiguationData":[OSD([subQ0])],"isStart":false}),makeQuery(id+"F3.opExtrude","CAP_FACE",FACE,{"disambiguationData":[OSD([subQ0])],"isStart":false})],"blendedInto":[makeQuery(id+"F3.opExtrude","CAP_FACE",FACE,{"disambiguationData":[OSD([subQ0])],"isStart":false})]});}
            var Q81;
            {var subQ0=sQuery(id+"F1.wireOp",EDGE,"E206.11.3.0");Q81=makeQuery(id+"F4.opChamfer","BLEND_EDGE",EDGE,{"blendedFrom":[makeQuery(id+"F3.opExtrude","CAP_EDGE",EDGE,{"disambiguationData":[OSD([subQ0])],"isStart":false}),makeQuery(id+"F3.opExtrude","CAP_FACE",FACE,{"disambiguationData":[OSD([subQ0])],"isStart":false})],"blendedInto":[makeQuery(id+"F3.opExtrude","CAP_FACE",FACE,{"disambiguationData":[OSD([subQ0])],"isStart":false})]});}
            var Q82;
            {var subQ0=sQuery(id+"F1.wireOp",EDGE,"E206.10.3.0");Q82=makeQuery(id+"F4.opChamfer","BLEND_EDGE",EDGE,{"blendedFrom":[makeQuery(id+"F3.opExtrude","CAP_EDGE",EDGE,{"disambiguationData":[OSD([subQ0])],"isStart":false}),makeQuery(id+"F3.opExtrude","CAP_FACE",FACE,{"disambiguationData":[OSD([subQ0])],"isStart":false})],"blendedInto":[makeQuery(id+"F3.opExtrude","CAP_FACE",FACE,{"disambiguationData":[OSD([subQ0])],"isStart":false})]});}
            var Q83;
            {var subQ0=sQuery(id+"F1.wireOp",EDGE,"E206.9.3.0");Q83=makeQuery(id+"F4.opChamfer","BLEND_EDGE",EDGE,{"blendedFrom":[makeQuery(id+"F3.opExtrude","CAP_EDGE",EDGE,{"disambiguationData":[OSD([subQ0])],"isStart":false}),makeQuery(id+"F3.opExtrude","CAP_FACE",FACE,{"disambiguationData":[OSD([subQ0])],"isStart":false})],"blendedInto":[makeQuery(id+"F3.opExtrude","CAP_FACE",FACE,{"disambiguationData":[OSD([subQ0])],"isStart":false})]});}
            var Q84;
            {var subQ0=sQuery(id+"F1.wireOp",EDGE,"E206.9.4.0");Q84=makeQuery(id+"F4.opChamfer","BLEND_EDGE",EDGE,{"blendedFrom":[makeQuery(id+"F3.opExtrude","CAP_EDGE",EDGE,{"disambiguationData":[OSD([subQ0])],"isStart":false}),makeQuery(id+"F3.opExtrude","CAP_FACE",FACE,{"disambiguationData":[OSD([subQ0])],"isStart":false})],"blendedInto":[makeQuery(id+"F3.opExtrude","CAP_FACE",FACE,{"disambiguationData":[OSD([subQ0])],"isStart":false})]});}
            var Q85;
            {var subQ0=sQuery(id+"F1.wireOp",EDGE,"E206.9.5.0");Q85=makeQuery(id+"F4.opChamfer","BLEND_EDGE",EDGE,{"blendedFrom":[makeQuery(id+"F3.opExtrude","CAP_EDGE",EDGE,{"disambiguationData":[OSD([subQ0])],"isStart":false}),makeQuery(id+"F3.opExtrude","CAP_FACE",FACE,{"disambiguationData":[OSD([subQ0])],"isStart":false})],"blendedInto":[makeQuery(id+"F3.opExtrude","CAP_FACE",FACE,{"disambiguationData":[OSD([subQ0])],"isStart":false})]});}
            var Q86;
            {var subQ0=sQuery(id+"F1.wireOp",EDGE,"E206.8.5.0");Q86=makeQuery(id+"F4.opChamfer","BLEND_EDGE",EDGE,{"blendedFrom":[makeQuery(id+"F3.opExtrude","CAP_EDGE",EDGE,{"disambiguationData":[OSD([subQ0])],"isStart":false}),makeQuery(id+"F3.opExtrude","CAP_FACE",FACE,{"disambiguationData":[OSD([subQ0])],"isStart":false})],"blendedInto":[makeQuery(id+"F3.opExtrude","CAP_FACE",FACE,{"disambiguationData":[OSD([subQ0])],"isStart":false})]});}
            var Q87;
            {var subQ0=sQuery(id+"F1.wireOp",EDGE,"E206.8.4.0");Q87=makeQuery(id+"F4.opChamfer","BLEND_EDGE",EDGE,{"blendedFrom":[makeQuery(id+"F3.opExtrude","CAP_EDGE",EDGE,{"disambiguationData":[OSD([subQ0])],"isStart":false}),makeQuery(id+"F3.opExtrude","CAP_FACE",FACE,{"disambiguationData":[OSD([subQ0])],"isStart":false})],"blendedInto":[makeQuery(id+"F3.opExtrude","CAP_FACE",FACE,{"disambiguationData":[OSD([subQ0])],"isStart":false})]});}
            var Q88;
            {var subQ0=sQuery(id+"F1.wireOp",EDGE,"E206.8.3.0");Q88=makeQuery(id+"F4.opChamfer","BLEND_EDGE",EDGE,{"blendedFrom":[makeQuery(id+"F3.opExtrude","CAP_EDGE",EDGE,{"disambiguationData":[OSD([subQ0])],"isStart":false}),makeQuery(id+"F3.opExtrude","CAP_FACE",FACE,{"disambiguationData":[OSD([subQ0])],"isStart":false})],"blendedInto":[makeQuery(id+"F3.opExtrude","CAP_FACE",FACE,{"disambiguationData":[OSD([subQ0])],"isStart":false})]});}
            var Q89;
            {var subQ0=sQuery(id+"F1.wireOp",EDGE,"E206.7.0.0");Q89=makeQuery(id+"F4.opChamfer","BLEND_EDGE",EDGE,{"blendedFrom":[makeQuery(id+"F3.opExtrude","CAP_EDGE",EDGE,{"disambiguationData":[OSD([subQ0])],"isStart":false}),makeQuery(id+"F3.opExtrude","CAP_FACE",FACE,{"disambiguationData":[OSD([subQ0])],"isStart":false})],"blendedInto":[makeQuery(id+"F3.opExtrude","CAP_FACE",FACE,{"disambiguationData":[OSD([subQ0])],"isStart":false})]});}
            var Q90;
            {var subQ0=sQuery(id+"F1.wireOp",EDGE,"E206.7.1.0");Q90=makeQuery(id+"F4.opChamfer","BLEND_EDGE",EDGE,{"blendedFrom":[makeQuery(id+"F3.opExtrude","CAP_EDGE",EDGE,{"disambiguationData":[OSD([subQ0])],"isStart":false}),makeQuery(id+"F3.opExtrude","CAP_FACE",FACE,{"disambiguationData":[OSD([subQ0])],"isStart":false})],"blendedInto":[makeQuery(id+"F3.opExtrude","CAP_FACE",FACE,{"disambiguationData":[OSD([subQ0])],"isStart":false})]});}
            var Q91;
            {var subQ0=sQuery(id+"F1.wireOp",EDGE,"E206.7.2.0");Q91=makeQuery(id+"F4.opChamfer","BLEND_EDGE",EDGE,{"blendedFrom":[makeQuery(id+"F3.opExtrude","CAP_EDGE",EDGE,{"disambiguationData":[OSD([subQ0])],"isStart":false}),makeQuery(id+"F3.opExtrude","CAP_FACE",FACE,{"disambiguationData":[OSD([subQ0])],"isStart":false})],"blendedInto":[makeQuery(id+"F3.opExtrude","CAP_FACE",FACE,{"disambiguationData":[OSD([subQ0])],"isStart":false})]});}
            var Q92;
            {var subQ0=sQuery(id+"F1.wireOp",EDGE,"E206.7.3.0");Q92=makeQuery(id+"F4.opChamfer","BLEND_EDGE",EDGE,{"blendedFrom":[makeQuery(id+"F3.opExtrude","CAP_EDGE",EDGE,{"disambiguationData":[OSD([subQ0])],"isStart":false}),makeQuery(id+"F3.opExtrude","CAP_FACE",FACE,{"disambiguationData":[OSD([subQ0])],"isStart":false})],"blendedInto":[makeQuery(id+"F3.opExtrude","CAP_FACE",FACE,{"disambiguationData":[OSD([subQ0])],"isStart":false})]});}
            var Q93;
            {var subQ0=sQuery(id+"F1.wireOp",EDGE,"E206.7.4.0");Q93=makeQuery(id+"F4.opChamfer","BLEND_EDGE",EDGE,{"blendedFrom":[makeQuery(id+"F3.opExtrude","CAP_EDGE",EDGE,{"disambiguationData":[OSD([subQ0])],"isStart":false}),makeQuery(id+"F3.opExtrude","CAP_FACE",FACE,{"disambiguationData":[OSD([subQ0])],"isStart":false})],"blendedInto":[makeQuery(id+"F3.opExtrude","CAP_FACE",FACE,{"disambiguationData":[OSD([subQ0])],"isStart":false})]});}
            var Q94;
            {var subQ0=sQuery(id+"F1.wireOp",EDGE,"E206.7.5.0");Q94=makeQuery(id+"F4.opChamfer","BLEND_EDGE",EDGE,{"blendedFrom":[makeQuery(id+"F3.opExtrude","CAP_EDGE",EDGE,{"disambiguationData":[OSD([subQ0])],"isStart":false}),makeQuery(id+"F3.opExtrude","CAP_FACE",FACE,{"disambiguationData":[OSD([subQ0])],"isStart":false})],"blendedInto":[makeQuery(id+"F3.opExtrude","CAP_FACE",FACE,{"disambiguationData":[OSD([subQ0])],"isStart":false})]});}
            var Q95;
            {var subQ0=sQuery(id+"F1.wireOp",EDGE,"E206.7.6.0");Q95=makeQuery(id+"F4.opChamfer","BLEND_EDGE",EDGE,{"blendedFrom":[makeQuery(id+"F3.opExtrude","CAP_EDGE",EDGE,{"disambiguationData":[OSD([subQ0])],"isStart":false}),makeQuery(id+"F3.opExtrude","CAP_FACE",FACE,{"disambiguationData":[OSD([subQ0])],"isStart":false})],"blendedInto":[makeQuery(id+"F3.opExtrude","CAP_FACE",FACE,{"disambiguationData":[OSD([subQ0])],"isStart":false})]});}
            var Q96;
            {var subQ0=sQuery(id+"F1.wireOp",EDGE,"E206.6.6.0");Q96=makeQuery(id+"F4.opChamfer","BLEND_EDGE",EDGE,{"blendedFrom":[makeQuery(id+"F3.opExtrude","CAP_EDGE",EDGE,{"disambiguationData":[OSD([subQ0])],"isStart":false}),makeQuery(id+"F3.opExtrude","CAP_FACE",FACE,{"disambiguationData":[OSD([subQ0])],"isStart":false})],"blendedInto":[makeQuery(id+"F3.opExtrude","CAP_FACE",FACE,{"disambiguationData":[OSD([subQ0])],"isStart":false})]});}
            var Q97;
            {var subQ0=sQuery(id+"F1.wireOp",EDGE,"E206.5.6.0");Q97=makeQuery(id+"F4.opChamfer","BLEND_EDGE",EDGE,{"blendedFrom":[makeQuery(id+"F3.opExtrude","CAP_EDGE",EDGE,{"disambiguationData":[OSD([subQ0])],"isStart":false}),makeQuery(id+"F3.opExtrude","CAP_FACE",FACE,{"disambiguationData":[OSD([subQ0])],"isStart":false})],"blendedInto":[makeQuery(id+"F3.opExtrude","CAP_FACE",FACE,{"disambiguationData":[OSD([subQ0])],"isStart":false})]});}
            var Q98;
            {var subQ0=sQuery(id+"F1.wireOp",EDGE,"E206.4.6.0");Q98=makeQuery(id+"F4.opChamfer","BLEND_EDGE",EDGE,{"blendedFrom":[makeQuery(id+"F3.opExtrude","CAP_EDGE",EDGE,{"disambiguationData":[OSD([subQ0])],"isStart":false}),makeQuery(id+"F3.opExtrude","CAP_FACE",FACE,{"disambiguationData":[OSD([subQ0])],"isStart":false})],"blendedInto":[makeQuery(id+"F3.opExtrude","CAP_FACE",FACE,{"disambiguationData":[OSD([subQ0])],"isStart":false})]});}
            var Q99;
            {var subQ0=sQuery(id+"F1.wireOp",EDGE,"E206.3.7.0");Q99=makeQuery(id+"F4.opChamfer","BLEND_EDGE",EDGE,{"blendedFrom":[makeQuery(id+"F3.opExtrude","CAP_EDGE",EDGE,{"disambiguationData":[OSD([subQ0])],"isStart":false}),makeQuery(id+"F3.opExtrude","CAP_FACE",FACE,{"disambiguationData":[OSD([subQ0])],"isStart":false})],"blendedInto":[makeQuery(id+"F3.opExtrude","CAP_FACE",FACE,{"disambiguationData":[OSD([subQ0])],"isStart":false})]});}
            var Q100;
            {var subQ0=sQuery(id+"F1.wireOp",EDGE,"E206.3.8.0");Q100=makeQuery(id+"F4.opChamfer","BLEND_EDGE",EDGE,{"blendedFrom":[makeQuery(id+"F3.opExtrude","CAP_EDGE",EDGE,{"disambiguationData":[OSD([subQ0])],"isStart":false}),makeQuery(id+"F3.opExtrude","CAP_FACE",FACE,{"disambiguationData":[OSD([subQ0])],"isStart":false})],"blendedInto":[makeQuery(id+"F3.opExtrude","CAP_FACE",FACE,{"disambiguationData":[OSD([subQ0])],"isStart":false})]});}
            var Q101;
            {var subQ0=sQuery(id+"F1.wireOp",EDGE,"E206.2.8.0");Q101=makeQuery(id+"F4.opChamfer","BLEND_EDGE",EDGE,{"blendedFrom":[makeQuery(id+"F3.opExtrude","CAP_EDGE",EDGE,{"disambiguationData":[OSD([subQ0])],"isStart":false}),makeQuery(id+"F3.opExtrude","CAP_FACE",FACE,{"disambiguationData":[OSD([subQ0])],"isStart":false})],"blendedInto":[makeQuery(id+"F3.opExtrude","CAP_FACE",FACE,{"disambiguationData":[OSD([subQ0])],"isStart":false})]});}
            var Q102;
            {var subQ0=sQuery(id+"F1.wireOp",EDGE,"E206.1.8.0");Q102=makeQuery(id+"F4.opChamfer","BLEND_EDGE",EDGE,{"blendedFrom":[makeQuery(id+"F3.opExtrude","CAP_EDGE",EDGE,{"disambiguationData":[OSD([subQ0])],"isStart":false}),makeQuery(id+"F3.opExtrude","CAP_FACE",FACE,{"disambiguationData":[OSD([subQ0])],"isStart":false})],"blendedInto":[makeQuery(id+"F3.opExtrude","CAP_FACE",FACE,{"disambiguationData":[OSD([subQ0])],"isStart":false})]});}
            var Q103;
            {var subQ0=sQuery(id+"F1.wireOp",EDGE,"E206.0.8.0");Q103=makeQuery(id+"F4.opChamfer","BLEND_EDGE",EDGE,{"blendedFrom":[makeQuery(id+"F3.opExtrude","CAP_EDGE",EDGE,{"disambiguationData":[OSD([subQ0])],"isStart":false}),makeQuery(id+"F3.opExtrude","CAP_FACE",FACE,{"disambiguationData":[OSD([subQ0])],"isStart":false})],"blendedInto":[makeQuery(id+"F3.opExtrude","CAP_FACE",FACE,{"disambiguationData":[OSD([subQ0])],"isStart":false})]});}
            var Q104;
            {var subQ0=sQuery(id+"F1.wireOp",EDGE,"E206.0.7.0");Q104=makeQuery(id+"F4.opChamfer","BLEND_EDGE",EDGE,{"blendedFrom":[makeQuery(id+"F3.opExtrude","CAP_EDGE",EDGE,{"disambiguationData":[OSD([subQ0])],"isStart":false}),makeQuery(id+"F3.opExtrude","CAP_FACE",FACE,{"disambiguationData":[OSD([subQ0])],"isStart":false})],"blendedInto":[makeQuery(id+"F3.opExtrude","CAP_FACE",FACE,{"disambiguationData":[OSD([subQ0])],"isStart":false})]});}
            var Q105;
            {var subQ0=sQuery(id+"F1.wireOp",EDGE,"E206.1.7.0");Q105=makeQuery(id+"F4.opChamfer","BLEND_EDGE",EDGE,{"blendedFrom":[makeQuery(id+"F3.opExtrude","CAP_EDGE",EDGE,{"disambiguationData":[OSD([subQ0])],"isStart":false}),makeQuery(id+"F3.opExtrude","CAP_FACE",FACE,{"disambiguationData":[OSD([subQ0])],"isStart":false})],"blendedInto":[makeQuery(id+"F3.opExtrude","CAP_FACE",FACE,{"disambiguationData":[OSD([subQ0])],"isStart":false})]});}
            var Q106;
            {var subQ0=sQuery(id+"F1.wireOp",EDGE,"E206.2.7.0");Q106=makeQuery(id+"F4.opChamfer","BLEND_EDGE",EDGE,{"blendedFrom":[makeQuery(id+"F3.opExtrude","CAP_EDGE",EDGE,{"disambiguationData":[OSD([subQ0])],"isStart":false}),makeQuery(id+"F3.opExtrude","CAP_FACE",FACE,{"disambiguationData":[OSD([subQ0])],"isStart":false})],"blendedInto":[makeQuery(id+"F3.opExtrude","CAP_FACE",FACE,{"disambiguationData":[OSD([subQ0])],"isStart":false})]});}
            var Q107;
            {var subQ0=sQuery(id+"F1.wireOp",EDGE,"E206.3.6.0");Q107=makeQuery(id+"F4.opChamfer","BLEND_EDGE",EDGE,{"blendedFrom":[makeQuery(id+"F3.opExtrude","CAP_EDGE",EDGE,{"disambiguationData":[OSD([subQ0])],"isStart":false}),makeQuery(id+"F3.opExtrude","CAP_FACE",FACE,{"disambiguationData":[OSD([subQ0])],"isStart":false})],"blendedInto":[makeQuery(id+"F3.opExtrude","CAP_FACE",FACE,{"disambiguationData":[OSD([subQ0])],"isStart":false})]});}
            var Q108;
            {var subQ0=sQuery(id+"F1.wireOp",EDGE,"E206.2.6.0");Q108=makeQuery(id+"F4.opChamfer","BLEND_EDGE",EDGE,{"blendedFrom":[makeQuery(id+"F3.opExtrude","CAP_EDGE",EDGE,{"disambiguationData":[OSD([subQ0])],"isStart":false}),makeQuery(id+"F3.opExtrude","CAP_FACE",FACE,{"disambiguationData":[OSD([subQ0])],"isStart":false})],"blendedInto":[makeQuery(id+"F3.opExtrude","CAP_FACE",FACE,{"disambiguationData":[OSD([subQ0])],"isStart":false})]});}
            var Q109;
            {var subQ0=sQuery(id+"F1.wireOp",EDGE,"E206.1.6.0");Q109=makeQuery(id+"F4.opChamfer","BLEND_EDGE",EDGE,{"blendedFrom":[makeQuery(id+"F3.opExtrude","CAP_EDGE",EDGE,{"disambiguationData":[OSD([subQ0])],"isStart":false}),makeQuery(id+"F3.opExtrude","CAP_FACE",FACE,{"disambiguationData":[OSD([subQ0])],"isStart":false})],"blendedInto":[makeQuery(id+"F3.opExtrude","CAP_FACE",FACE,{"disambiguationData":[OSD([subQ0])],"isStart":false})]});}
            var Q110;
            {var subQ0=sQuery(id+"F1.wireOp",EDGE,"E206.0.6.0");Q110=makeQuery(id+"F4.opChamfer","BLEND_EDGE",EDGE,{"blendedFrom":[makeQuery(id+"F3.opExtrude","CAP_EDGE",EDGE,{"disambiguationData":[OSD([subQ0])],"isStart":false}),makeQuery(id+"F3.opExtrude","CAP_FACE",FACE,{"disambiguationData":[OSD([subQ0])],"isStart":false})],"blendedInto":[makeQuery(id+"F3.opExtrude","CAP_FACE",FACE,{"disambiguationData":[OSD([subQ0])],"isStart":false})]});}
            var Q111;
            {var subQ0=sQuery(id+"F1.wireOp",EDGE,"E206.0.5.0");Q111=makeQuery(id+"F4.opChamfer","BLEND_EDGE",EDGE,{"blendedFrom":[makeQuery(id+"F3.opExtrude","CAP_EDGE",EDGE,{"disambiguationData":[OSD([subQ0])],"isStart":false}),makeQuery(id+"F3.opExtrude","CAP_FACE",FACE,{"disambiguationData":[OSD([subQ0])],"isStart":false})],"blendedInto":[makeQuery(id+"F3.opExtrude","CAP_FACE",FACE,{"disambiguationData":[OSD([subQ0])],"isStart":false})]});}
            var Q112;
            {var subQ0=sQuery(id+"F1.wireOp",EDGE,"E206.1.5.0");Q112=makeQuery(id+"F4.opChamfer","BLEND_EDGE",EDGE,{"blendedFrom":[makeQuery(id+"F3.opExtrude","CAP_EDGE",EDGE,{"disambiguationData":[OSD([subQ0])],"isStart":false}),makeQuery(id+"F3.opExtrude","CAP_FACE",FACE,{"disambiguationData":[OSD([subQ0])],"isStart":false})],"blendedInto":[makeQuery(id+"F3.opExtrude","CAP_FACE",FACE,{"disambiguationData":[OSD([subQ0])],"isStart":false})]});}
            var Q113;
            {var subQ0=sQuery(id+"F1.wireOp",EDGE,"E206.2.5.0");Q113=makeQuery(id+"F4.opChamfer","BLEND_EDGE",EDGE,{"blendedFrom":[makeQuery(id+"F3.opExtrude","CAP_EDGE",EDGE,{"disambiguationData":[OSD([subQ0])],"isStart":false}),makeQuery(id+"F3.opExtrude","CAP_FACE",FACE,{"disambiguationData":[OSD([subQ0])],"isStart":false})],"blendedInto":[makeQuery(id+"F3.opExtrude","CAP_FACE",FACE,{"disambiguationData":[OSD([subQ0])],"isStart":false})]});}
            var Q114;
            {var subQ0=sQuery(id+"F1.wireOp",EDGE,"E206.3.5.0");Q114=makeQuery(id+"F4.opChamfer","BLEND_EDGE",EDGE,{"blendedFrom":[makeQuery(id+"F3.opExtrude","CAP_EDGE",EDGE,{"disambiguationData":[OSD([subQ0])],"isStart":false}),makeQuery(id+"F3.opExtrude","CAP_FACE",FACE,{"disambiguationData":[OSD([subQ0])],"isStart":false})],"blendedInto":[makeQuery(id+"F3.opExtrude","CAP_FACE",FACE,{"disambiguationData":[OSD([subQ0])],"isStart":false})]});}
            var Q115;
            {var subQ0=sQuery(id+"F1.wireOp",EDGE,"E206.4.5.0");Q115=makeQuery(id+"F4.opChamfer","BLEND_EDGE",EDGE,{"blendedFrom":[makeQuery(id+"F3.opExtrude","CAP_EDGE",EDGE,{"disambiguationData":[OSD([subQ0])],"isStart":false}),makeQuery(id+"F3.opExtrude","CAP_FACE",FACE,{"disambiguationData":[OSD([subQ0])],"isStart":false})],"blendedInto":[makeQuery(id+"F3.opExtrude","CAP_FACE",FACE,{"disambiguationData":[OSD([subQ0])],"isStart":false})]});}
            var Q116;
            {var subQ0=sQuery(id+"F1.wireOp",EDGE,"E206.5.5.0");Q116=makeQuery(id+"F4.opChamfer","BLEND_EDGE",EDGE,{"blendedFrom":[makeQuery(id+"F3.opExtrude","CAP_EDGE",EDGE,{"disambiguationData":[OSD([subQ0])],"isStart":false}),makeQuery(id+"F3.opExtrude","CAP_FACE",FACE,{"disambiguationData":[OSD([subQ0])],"isStart":false})],"blendedInto":[makeQuery(id+"F3.opExtrude","CAP_FACE",FACE,{"disambiguationData":[OSD([subQ0])],"isStart":false})]});}
            var Q117;
            {var subQ0=sQuery(id+"F1.wireOp",EDGE,"E206.6.5.0");Q117=makeQuery(id+"F4.opChamfer","BLEND_EDGE",EDGE,{"blendedFrom":[makeQuery(id+"F3.opExtrude","CAP_EDGE",EDGE,{"disambiguationData":[OSD([subQ0])],"isStart":false}),makeQuery(id+"F3.opExtrude","CAP_FACE",FACE,{"disambiguationData":[OSD([subQ0])],"isStart":false})],"blendedInto":[makeQuery(id+"F3.opExtrude","CAP_FACE",FACE,{"disambiguationData":[OSD([subQ0])],"isStart":false})]});}
            var Q118;
            {var subQ0=sQuery(id+"F1.wireOp",EDGE,"E206.6.0.0");Q118=makeQuery(id+"F4.opChamfer","BLEND_EDGE",EDGE,{"blendedFrom":[makeQuery(id+"F3.opExtrude","CAP_EDGE",EDGE,{"disambiguationData":[OSD([subQ0])],"isStart":false}),makeQuery(id+"F3.opExtrude","CAP_FACE",FACE,{"disambiguationData":[OSD([subQ0])],"isStart":false})],"blendedInto":[makeQuery(id+"F3.opExtrude","CAP_FACE",FACE,{"disambiguationData":[OSD([subQ0])],"isStart":false})]});}
            var Q119;
            {var subQ0=sQuery(id+"F1.wireOp",EDGE,"E206.6.1.0");Q119=makeQuery(id+"F4.opChamfer","BLEND_EDGE",EDGE,{"blendedFrom":[makeQuery(id+"F3.opExtrude","CAP_EDGE",EDGE,{"disambiguationData":[OSD([subQ0])],"isStart":false}),makeQuery(id+"F3.opExtrude","CAP_FACE",FACE,{"disambiguationData":[OSD([subQ0])],"isStart":false})],"blendedInto":[makeQuery(id+"F3.opExtrude","CAP_FACE",FACE,{"disambiguationData":[OSD([subQ0])],"isStart":false})]});}
            var Q120;
            {var subQ0=sQuery(id+"F1.wireOp",EDGE,"E206.6.2.0");Q120=makeQuery(id+"F4.opChamfer","BLEND_EDGE",EDGE,{"blendedFrom":[makeQuery(id+"F3.opExtrude","CAP_EDGE",EDGE,{"disambiguationData":[OSD([subQ0])],"isStart":false}),makeQuery(id+"F3.opExtrude","CAP_FACE",FACE,{"disambiguationData":[OSD([subQ0])],"isStart":false})],"blendedInto":[makeQuery(id+"F3.opExtrude","CAP_FACE",FACE,{"disambiguationData":[OSD([subQ0])],"isStart":false})]});}
            var Q121;
            {var subQ0=sQuery(id+"F1.wireOp",EDGE,"E206.6.3.0");Q121=makeQuery(id+"F4.opChamfer","BLEND_EDGE",EDGE,{"blendedFrom":[makeQuery(id+"F3.opExtrude","CAP_EDGE",EDGE,{"disambiguationData":[OSD([subQ0])],"isStart":false}),makeQuery(id+"F3.opExtrude","CAP_FACE",FACE,{"disambiguationData":[OSD([subQ0])],"isStart":false})],"blendedInto":[makeQuery(id+"F3.opExtrude","CAP_FACE",FACE,{"disambiguationData":[OSD([subQ0])],"isStart":false})]});}
            var Q122;
            {var subQ0=sQuery(id+"F1.wireOp",EDGE,"E206.6.4.0");Q122=makeQuery(id+"F4.opChamfer","BLEND_EDGE",EDGE,{"blendedFrom":[makeQuery(id+"F3.opExtrude","CAP_EDGE",EDGE,{"disambiguationData":[OSD([subQ0])],"isStart":false}),makeQuery(id+"F3.opExtrude","CAP_FACE",FACE,{"disambiguationData":[OSD([subQ0])],"isStart":false})],"blendedInto":[makeQuery(id+"F3.opExtrude","CAP_FACE",FACE,{"disambiguationData":[OSD([subQ0])],"isStart":false})]});}
            var Q123;
            {var subQ0=sQuery(id+"F1.wireOp",EDGE,"E206.5.4.0");Q123=makeQuery(id+"F4.opChamfer","BLEND_EDGE",EDGE,{"blendedFrom":[makeQuery(id+"F3.opExtrude","CAP_EDGE",EDGE,{"disambiguationData":[OSD([subQ0])],"isStart":false}),makeQuery(id+"F3.opExtrude","CAP_FACE",FACE,{"disambiguationData":[OSD([subQ0])],"isStart":false})],"blendedInto":[makeQuery(id+"F3.opExtrude","CAP_FACE",FACE,{"disambiguationData":[OSD([subQ0])],"isStart":false})]});}
            var Q124;
            {var subQ0=sQuery(id+"F1.wireOp",EDGE,"E206.4.4.0");Q124=makeQuery(id+"F4.opChamfer","BLEND_EDGE",EDGE,{"blendedFrom":[makeQuery(id+"F3.opExtrude","CAP_EDGE",EDGE,{"disambiguationData":[OSD([subQ0])],"isStart":false}),makeQuery(id+"F3.opExtrude","CAP_FACE",FACE,{"disambiguationData":[OSD([subQ0])],"isStart":false})],"blendedInto":[makeQuery(id+"F3.opExtrude","CAP_FACE",FACE,{"disambiguationData":[OSD([subQ0])],"isStart":false})]});}
            var Q125;
            {var subQ0=sQuery(id+"F1.wireOp",EDGE,"E206.3.4.0");Q125=makeQuery(id+"F4.opChamfer","BLEND_EDGE",EDGE,{"blendedFrom":[makeQuery(id+"F3.opExtrude","CAP_EDGE",EDGE,{"disambiguationData":[OSD([subQ0])],"isStart":false}),makeQuery(id+"F3.opExtrude","CAP_FACE",FACE,{"disambiguationData":[OSD([subQ0])],"isStart":false})],"blendedInto":[makeQuery(id+"F3.opExtrude","CAP_FACE",FACE,{"disambiguationData":[OSD([subQ0])],"isStart":false})]});}
            var Q126;
            {var subQ0=sQuery(id+"F1.wireOp",EDGE,"E206.2.4.0");Q126=makeQuery(id+"F4.opChamfer","BLEND_EDGE",EDGE,{"blendedFrom":[makeQuery(id+"F3.opExtrude","CAP_EDGE",EDGE,{"disambiguationData":[OSD([subQ0])],"isStart":false}),makeQuery(id+"F3.opExtrude","CAP_FACE",FACE,{"disambiguationData":[OSD([subQ0])],"isStart":false})],"blendedInto":[makeQuery(id+"F3.opExtrude","CAP_FACE",FACE,{"disambiguationData":[OSD([subQ0])],"isStart":false})]});}
            var Q127;
            {var subQ0=sQuery(id+"F1.wireOp",EDGE,"E206.0.4.0");Q127=makeQuery(id+"F4.opChamfer","BLEND_EDGE",EDGE,{"blendedFrom":[makeQuery(id+"F3.opExtrude","CAP_EDGE",EDGE,{"disambiguationData":[OSD([subQ0])],"isStart":false}),makeQuery(id+"F3.opExtrude","CAP_FACE",FACE,{"disambiguationData":[OSD([subQ0])],"isStart":false})],"blendedInto":[makeQuery(id+"F3.opExtrude","CAP_FACE",FACE,{"disambiguationData":[OSD([subQ0])],"isStart":false})]});}
            var Q128;
            {var subQ0=sQuery(id+"F1.wireOp",EDGE,"E206.1.4.0");Q128=makeQuery(id+"F4.opChamfer","BLEND_EDGE",EDGE,{"blendedFrom":[makeQuery(id+"F3.opExtrude","CAP_EDGE",EDGE,{"disambiguationData":[OSD([subQ0])],"isStart":false}),makeQuery(id+"F3.opExtrude","CAP_FACE",FACE,{"disambiguationData":[OSD([subQ0])],"isStart":false})],"blendedInto":[makeQuery(id+"F3.opExtrude","CAP_FACE",FACE,{"disambiguationData":[OSD([subQ0])],"isStart":false})]});}
            var Q129;
            {var subQ0=sQuery(id+"F1.wireOp",EDGE,"E206.0.3.0");Q129=makeQuery(id+"F4.opChamfer","BLEND_EDGE",EDGE,{"blendedFrom":[makeQuery(id+"F3.opExtrude","CAP_EDGE",EDGE,{"disambiguationData":[OSD([subQ0])],"isStart":false}),makeQuery(id+"F3.opExtrude","CAP_FACE",FACE,{"disambiguationData":[OSD([subQ0])],"isStart":false})],"blendedInto":[makeQuery(id+"F3.opExtrude","CAP_FACE",FACE,{"disambiguationData":[OSD([subQ0])],"isStart":false})]});}
            var Q130;
            {var subQ0=sQuery(id+"F1.wireOp",EDGE,"E206.0.2.0");Q130=makeQuery(id+"F4.opChamfer","BLEND_EDGE",EDGE,{"blendedFrom":[makeQuery(id+"F3.opExtrude","CAP_EDGE",EDGE,{"disambiguationData":[OSD([subQ0])],"isStart":false}),makeQuery(id+"F3.opExtrude","CAP_FACE",FACE,{"disambiguationData":[OSD([subQ0])],"isStart":false})],"blendedInto":[makeQuery(id+"F3.opExtrude","CAP_FACE",FACE,{"disambiguationData":[OSD([subQ0])],"isStart":false})]});}
            var Q131;
            {var subQ0=sQuery(id+"F1.wireOp",EDGE,"E206.1.2.0");Q131=makeQuery(id+"F4.opChamfer","BLEND_EDGE",EDGE,{"blendedFrom":[makeQuery(id+"F3.opExtrude","CAP_EDGE",EDGE,{"disambiguationData":[OSD([subQ0])],"isStart":false}),makeQuery(id+"F3.opExtrude","CAP_FACE",FACE,{"disambiguationData":[OSD([subQ0])],"isStart":false})],"blendedInto":[makeQuery(id+"F3.opExtrude","CAP_FACE",FACE,{"disambiguationData":[OSD([subQ0])],"isStart":false})]});}
            var Q132;
            {var subQ0=sQuery(id+"F1.wireOp",EDGE,"E206.1.3.0");Q132=makeQuery(id+"F4.opChamfer","BLEND_EDGE",EDGE,{"blendedFrom":[makeQuery(id+"F3.opExtrude","CAP_EDGE",EDGE,{"disambiguationData":[OSD([subQ0])],"isStart":false}),makeQuery(id+"F3.opExtrude","CAP_FACE",FACE,{"disambiguationData":[OSD([subQ0])],"isStart":false})],"blendedInto":[makeQuery(id+"F3.opExtrude","CAP_FACE",FACE,{"disambiguationData":[OSD([subQ0])],"isStart":false})]});}
            var Q133;
            {var subQ0=sQuery(id+"F1.wireOp",EDGE,"E206.2.3.0");Q133=makeQuery(id+"F4.opChamfer","BLEND_EDGE",EDGE,{"blendedFrom":[makeQuery(id+"F3.opExtrude","CAP_EDGE",EDGE,{"disambiguationData":[OSD([subQ0])],"isStart":false}),makeQuery(id+"F3.opExtrude","CAP_FACE",FACE,{"disambiguationData":[OSD([subQ0])],"isStart":false})],"blendedInto":[makeQuery(id+"F3.opExtrude","CAP_FACE",FACE,{"disambiguationData":[OSD([subQ0])],"isStart":false})]});}
            var Q134;
            {var subQ0=sQuery(id+"F1.wireOp",EDGE,"E206.3.3.0");Q134=makeQuery(id+"F4.opChamfer","BLEND_EDGE",EDGE,{"blendedFrom":[makeQuery(id+"F3.opExtrude","CAP_EDGE",EDGE,{"disambiguationData":[OSD([subQ0])],"isStart":false}),makeQuery(id+"F3.opExtrude","CAP_FACE",FACE,{"disambiguationData":[OSD([subQ0])],"isStart":false})],"blendedInto":[makeQuery(id+"F3.opExtrude","CAP_FACE",FACE,{"disambiguationData":[OSD([subQ0])],"isStart":false})]});}
            var Q135;
            {var subQ0=sQuery(id+"F1.wireOp",EDGE,"E206.4.3.0");Q135=makeQuery(id+"F4.opChamfer","BLEND_EDGE",EDGE,{"blendedFrom":[makeQuery(id+"F3.opExtrude","CAP_EDGE",EDGE,{"disambiguationData":[OSD([subQ0])],"isStart":false}),makeQuery(id+"F3.opExtrude","CAP_FACE",FACE,{"disambiguationData":[OSD([subQ0])],"isStart":false})],"blendedInto":[makeQuery(id+"F3.opExtrude","CAP_FACE",FACE,{"disambiguationData":[OSD([subQ0])],"isStart":false})]});}
            var Q136;
            {var subQ0=sQuery(id+"F1.wireOp",EDGE,"E206.5.3.0");Q136=makeQuery(id+"F4.opChamfer","BLEND_EDGE",EDGE,{"blendedFrom":[makeQuery(id+"F3.opExtrude","CAP_EDGE",EDGE,{"disambiguationData":[OSD([subQ0])],"isStart":false}),makeQuery(id+"F3.opExtrude","CAP_FACE",FACE,{"disambiguationData":[OSD([subQ0])],"isStart":false})],"blendedInto":[makeQuery(id+"F3.opExtrude","CAP_FACE",FACE,{"disambiguationData":[OSD([subQ0])],"isStart":false})]});}
            var Q137;
            {var subQ0=sQuery(id+"F1.wireOp",EDGE,"E206.5.2.0");Q137=makeQuery(id+"F4.opChamfer","BLEND_EDGE",EDGE,{"blendedFrom":[makeQuery(id+"F3.opExtrude","CAP_EDGE",EDGE,{"disambiguationData":[OSD([subQ0])],"isStart":false}),makeQuery(id+"F3.opExtrude","CAP_FACE",FACE,{"disambiguationData":[OSD([subQ0])],"isStart":false})],"blendedInto":[makeQuery(id+"F3.opExtrude","CAP_FACE",FACE,{"disambiguationData":[OSD([subQ0])],"isStart":false})]});}
            var Q138;
            {var subQ0=sQuery(id+"F1.wireOp",EDGE,"E206.5.1.0");Q138=makeQuery(id+"F4.opChamfer","BLEND_EDGE",EDGE,{"blendedFrom":[makeQuery(id+"F3.opExtrude","CAP_EDGE",EDGE,{"disambiguationData":[OSD([subQ0])],"isStart":false}),makeQuery(id+"F3.opExtrude","CAP_FACE",FACE,{"disambiguationData":[OSD([subQ0])],"isStart":false})],"blendedInto":[makeQuery(id+"F3.opExtrude","CAP_FACE",FACE,{"disambiguationData":[OSD([subQ0])],"isStart":false})]});}
            var Q139;
            {var subQ0=sQuery(id+"F1.wireOp",EDGE,"E206.5.0.0");Q139=makeQuery(id+"F4.opChamfer","BLEND_EDGE",EDGE,{"blendedFrom":[makeQuery(id+"F3.opExtrude","CAP_EDGE",EDGE,{"disambiguationData":[OSD([subQ0])],"isStart":false}),makeQuery(id+"F3.opExtrude","CAP_FACE",FACE,{"disambiguationData":[OSD([subQ0])],"isStart":false})],"blendedInto":[makeQuery(id+"F3.opExtrude","CAP_FACE",FACE,{"disambiguationData":[OSD([subQ0])],"isStart":false})]});}
            var Q140;
            {var subQ0=sQuery(id+"F1.wireOp",EDGE,"E206.4.0.0");Q140=makeQuery(id+"F4.opChamfer","BLEND_EDGE",EDGE,{"blendedFrom":[makeQuery(id+"F3.opExtrude","CAP_EDGE",EDGE,{"disambiguationData":[OSD([subQ0])],"isStart":false}),makeQuery(id+"F3.opExtrude","CAP_FACE",FACE,{"disambiguationData":[OSD([subQ0])],"isStart":false})],"blendedInto":[makeQuery(id+"F3.opExtrude","CAP_FACE",FACE,{"disambiguationData":[OSD([subQ0])],"isStart":false})]});}
            var Q141;
            {var subQ0=sQuery(id+"F1.wireOp",EDGE,"E206.4.1.0");Q141=makeQuery(id+"F4.opChamfer","BLEND_EDGE",EDGE,{"blendedFrom":[makeQuery(id+"F3.opExtrude","CAP_EDGE",EDGE,{"disambiguationData":[OSD([subQ0])],"isStart":false}),makeQuery(id+"F3.opExtrude","CAP_FACE",FACE,{"disambiguationData":[OSD([subQ0])],"isStart":false})],"blendedInto":[makeQuery(id+"F3.opExtrude","CAP_FACE",FACE,{"disambiguationData":[OSD([subQ0])],"isStart":false})]});}
            var Q142;
            {var subQ0=sQuery(id+"F1.wireOp",EDGE,"E206.4.2.0");Q142=makeQuery(id+"F4.opChamfer","BLEND_EDGE",EDGE,{"blendedFrom":[makeQuery(id+"F3.opExtrude","CAP_EDGE",EDGE,{"disambiguationData":[OSD([subQ0])],"isStart":false}),makeQuery(id+"F3.opExtrude","CAP_FACE",FACE,{"disambiguationData":[OSD([subQ0])],"isStart":false})],"blendedInto":[makeQuery(id+"F3.opExtrude","CAP_FACE",FACE,{"disambiguationData":[OSD([subQ0])],"isStart":false})]});}
            var Q143;
            {var subQ0=sQuery(id+"F1.wireOp",EDGE,"E206.2.2.0");Q143=makeQuery(id+"F4.opChamfer","BLEND_EDGE",EDGE,{"blendedFrom":[makeQuery(id+"F3.opExtrude","CAP_EDGE",EDGE,{"disambiguationData":[OSD([subQ0])],"isStart":false}),makeQuery(id+"F3.opExtrude","CAP_FACE",FACE,{"disambiguationData":[OSD([subQ0])],"isStart":false})],"blendedInto":[makeQuery(id+"F3.opExtrude","CAP_FACE",FACE,{"disambiguationData":[OSD([subQ0])],"isStart":false})]});}
            var Q144;
            {var subQ0=sQuery(id+"F1.wireOp",EDGE,"E206.3.2.0");Q144=makeQuery(id+"F4.opChamfer","BLEND_EDGE",EDGE,{"blendedFrom":[makeQuery(id+"F3.opExtrude","CAP_EDGE",EDGE,{"disambiguationData":[OSD([subQ0])],"isStart":false}),makeQuery(id+"F3.opExtrude","CAP_FACE",FACE,{"disambiguationData":[OSD([subQ0])],"isStart":false})],"blendedInto":[makeQuery(id+"F3.opExtrude","CAP_FACE",FACE,{"disambiguationData":[OSD([subQ0])],"isStart":false})]});}
            var Q145;
            {var subQ0=sQuery(id+"F1.wireOp",EDGE,"E206.2.1.0");Q145=makeQuery(id+"F4.opChamfer","BLEND_EDGE",EDGE,{"blendedFrom":[makeQuery(id+"F3.opExtrude","CAP_EDGE",EDGE,{"disambiguationData":[OSD([subQ0])],"isStart":false}),makeQuery(id+"F3.opExtrude","CAP_FACE",FACE,{"disambiguationData":[OSD([subQ0])],"isStart":false})],"blendedInto":[makeQuery(id+"F3.opExtrude","CAP_FACE",FACE,{"disambiguationData":[OSD([subQ0])],"isStart":false})]});}
            var Q146;
            {var subQ0=sQuery(id+"F1.wireOp",EDGE,"E206.3.1.0");Q146=makeQuery(id+"F4.opChamfer","BLEND_EDGE",EDGE,{"blendedFrom":[makeQuery(id+"F3.opExtrude","CAP_EDGE",EDGE,{"disambiguationData":[OSD([subQ0])],"isStart":false}),makeQuery(id+"F3.opExtrude","CAP_FACE",FACE,{"disambiguationData":[OSD([subQ0])],"isStart":false})],"blendedInto":[makeQuery(id+"F3.opExtrude","CAP_FACE",FACE,{"disambiguationData":[OSD([subQ0])],"isStart":false})]});}
            var Q147;
            {var subQ0=sQuery(id+"F1.wireOp",EDGE,"E206.2.0.0");Q147=makeQuery(id+"F4.opChamfer","BLEND_EDGE",EDGE,{"blendedFrom":[makeQuery(id+"F3.opExtrude","CAP_EDGE",EDGE,{"disambiguationData":[OSD([subQ0])],"isStart":false}),makeQuery(id+"F3.opExtrude","CAP_FACE",FACE,{"disambiguationData":[OSD([subQ0])],"isStart":false})],"blendedInto":[makeQuery(id+"F3.opExtrude","CAP_FACE",FACE,{"disambiguationData":[OSD([subQ0])],"isStart":false})]});}
            var Q148;
            {var subQ0=sQuery(id+"F1.wireOp",EDGE,"E206.3.0.0");Q148=makeQuery(id+"F4.opChamfer","BLEND_EDGE",EDGE,{"blendedFrom":[makeQuery(id+"F3.opExtrude","CAP_EDGE",EDGE,{"disambiguationData":[OSD([subQ0])],"isStart":false}),makeQuery(id+"F3.opExtrude","CAP_FACE",FACE,{"disambiguationData":[OSD([subQ0])],"isStart":false})],"blendedInto":[makeQuery(id+"F3.opExtrude","CAP_FACE",FACE,{"disambiguationData":[OSD([subQ0])],"isStart":false})]});}
            var Q149;
            {var subQ0=sQuery(id+"F1.wireOp",EDGE,"E206.1.1.0");Q149=makeQuery(id+"F4.opChamfer","BLEND_EDGE",EDGE,{"blendedFrom":[makeQuery(id+"F3.opExtrude","CAP_EDGE",EDGE,{"disambiguationData":[OSD([subQ0])],"isStart":false}),makeQuery(id+"F3.opExtrude","CAP_FACE",FACE,{"disambiguationData":[OSD([subQ0])],"isStart":false})],"blendedInto":[makeQuery(id+"F3.opExtrude","CAP_FACE",FACE,{"disambiguationData":[OSD([subQ0])],"isStart":false})]});}
            var Q150;
            {var subQ0=sQuery(id+"F1.wireOp",EDGE,"E206.1.0.0");Q150=makeQuery(id+"F4.opChamfer","BLEND_EDGE",EDGE,{"blendedFrom":[makeQuery(id+"F3.opExtrude","CAP_EDGE",EDGE,{"disambiguationData":[OSD([subQ0])],"isStart":false}),makeQuery(id+"F3.opExtrude","CAP_FACE",FACE,{"disambiguationData":[OSD([subQ0])],"isStart":false})],"blendedInto":[makeQuery(id+"F3.opExtrude","CAP_FACE",FACE,{"disambiguationData":[OSD([subQ0])],"isStart":false})]});}
            var Q151;
            {var subQ0=sQuery(id+"F1.wireOp",EDGE,"E206.0.1.0");Q151=makeQuery(id+"F4.opChamfer","BLEND_EDGE",EDGE,{"blendedFrom":[makeQuery(id+"F3.opExtrude","CAP_EDGE",EDGE,{"disambiguationData":[OSD([subQ0])],"isStart":false}),makeQuery(id+"F3.opExtrude","CAP_FACE",FACE,{"disambiguationData":[OSD([subQ0])],"isStart":false})],"blendedInto":[makeQuery(id+"F3.opExtrude","CAP_FACE",FACE,{"disambiguationData":[OSD([subQ0])],"isStart":false})]});}
            var Q152;
            {var subQ0=sQuery(id+"F1.wireOp",EDGE,"E199");Q152=makeQuery(id+"F4.opChamfer","BLEND_EDGE",EDGE,{"blendedFrom":[makeQuery(id+"F3.opExtrude","CAP_EDGE",EDGE,{"disambiguationData":[OSD([subQ0])],"isStart":false}),makeQuery(id+"F3.opExtrude","CAP_FACE",FACE,{"disambiguationData":[OSD([subQ0])],"isStart":false})],"blendedInto":[makeQuery(id+"F3.opExtrude","CAP_FACE",FACE,{"disambiguationData":[OSD([subQ0])],"isStart":false})]});}
            fillet(context, id + "F5", {"entities" : qUnion([Q0, Q1, Q2, Q3, Q4, Q5, Q6, Q7, Q8, Q9, Q10, Q11, Q12, Q13, Q14, Q15, Q16, Q17, Q18, Q19, Q20, Q21, Q22, Q23, Q24, Q25, Q26, Q27, Q28, Q29, Q30, Q31, Q32, Q33, Q34, Q35, Q36, Q37, Q38, Q39, Q40, Q41, Q42, Q43, Q44, Q45, Q46, Q47, Q48, Q49, Q50, Q51, Q52, Q53, Q54, Q55, Q56, Q57, Q58, Q59, Q60, Q61, Q62, Q63, Q64, Q65, Q66, Q67, Q68, Q69, Q70, Q71, Q72, Q73, Q74, Q75, Q76, Q77, Q78, Q79, Q80, Q81, Q82, Q83, Q84, Q85, Q86, Q87, Q88, Q89, Q90, Q91, Q92, Q93, Q94, Q95, Q96, Q97, Q98, Q99, Q100, Q101, Q102, Q103, Q104, Q105, Q106, Q107, Q108, Q109, Q110, Q111, Q112, Q113, Q114, Q115, Q116, Q117, Q118, Q119, Q120, Q121, Q122, Q123, Q124, Q125, Q126, Q127, Q128, Q129, Q130, Q131, Q132, Q133, Q134, Q135, Q136, Q137, Q138, Q139, Q140, Q141, Q142, Q143, Q144, Q145, Q146, Q147, Q148, Q149, Q150, Q151, Q152]), "radius" : 0.5 * mm, "tangentPropagation" : true, "allowEdgeOverflow" : false});
        }
        {
            var Q0;
            Q0=makeQuery(id+"F2.opExtrude","CAP_FACE",FACE,{"disambiguationData":[OSD([sQuery(id+"F0.wireOp",EDGE,"E0.bottom"),sQuery(id+"F0.wireOp",EDGE,"E0.top"),sQuery(id+"F0.wireOp",EDGE,"E0.left"),sQuery(id+"F0.wireOp",EDGE,"E0.right"),sQuery(id+"F0.wireOp",EDGE,"E3.filletArc"),sQuery(id+"F0.wireOp",EDGE,"E4.filletArc"),sQuery(id+"F0.wireOp",EDGE,"E5.filletArc"),sQuery(id+"F0.wireOp",EDGE,"E6.filletArc"),sQuery(id+"F0.wireOp",EDGE,"E7"),sQuery(id+"F0.wireOp",EDGE,"E8"),sQuery(id+"F0.wireOp",EDGE,"E9"),sQuery(id+"F0.wireOp",EDGE,"E10"),sQuery(id+"F0.wireOp",EDGE,"E11"),sQuery(id+"F0.wireOp",EDGE,"E12"),sQuery(id+"F0.wireOp",EDGE,"E13"),sQuery(id+"F0.wireOp",EDGE,"E14"),sQuery(id+"F0.wireOp",EDGE,"E15"),sQuery(id+"F0.wireOp",EDGE,"E16"),sQuery(id+"F0.wireOp",EDGE,"E17"),sQuery(id+"F0.wireOp",EDGE,"E18"),sQuery(id+"F0.wireOp",EDGE,"E19"),sQuery(id+"F0.wireOp",EDGE,"E20"),sQuery(id+"F0.wireOp",EDGE,"E21"),sQuery(id+"F0.wireOp",EDGE,"E22"),sQuery(id+"F0.wireOp",EDGE,"E23"),sQuery(id+"F0.wireOp",EDGE,"E24"),sQuery(id+"F0.wireOp",EDGE,"E25"),sQuery(id+"F0.wireOp",EDGE,"E26"),sQuery(id+"F0.wireOp",EDGE,"E27"),sQuery(id+"F0.wireOp",EDGE,"E28"),sQuery(id+"F0.wireOp",EDGE,"E29"),sQuery(id+"F0.wireOp",EDGE,"E30"),sQuery(id+"F0.wireOp",EDGE,"E31"),sQuery(id+"F0.wireOp",EDGE,"E32"),sQuery(id+"F0.wireOp",EDGE,"E33"),sQuery(id+"F0.wireOp",EDGE,"E34"),sQuery(id+"F0.wireOp",EDGE,"E35"),sQuery(id+"F0.wireOp",EDGE,"E36"),sQuery(id+"F0.wireOp",EDGE,"E37"),sQuery(id+"F0.wireOp",EDGE,"E38"),sQuery(id+"F0.wireOp",EDGE,"E39"),sQuery(id+"F0.wireOp",EDGE,"E40"),sQuery(id+"F0.wireOp",EDGE,"E41"),sQuery(id+"F0.wireOp",EDGE,"E42"),sQuery(id+"F0.wireOp",EDGE,"E43"),sQuery(id+"F0.wireOp",EDGE,"E44"),sQuery(id+"F0.wireOp",EDGE,"E45"),sQuery(id+"F0.wireOp",EDGE,"E46"),sQuery(id+"F0.wireOp",EDGE,"E47"),sQuery(id+"F0.wireOp",EDGE,"E48"),sQuery(id+"F0.wireOp",EDGE,"E49"),sQuery(id+"F0.wireOp",EDGE,"E50"),sQuery(id+"F0.wireOp",EDGE,"E51"),sQuery(id+"F0.wireOp",EDGE,"E52"),sQuery(id+"F0.wireOp",EDGE,"E53"),sQuery(id+"F0.wireOp",EDGE,"E54"),sQuery(id+"F0.wireOp",EDGE,"E55"),sQuery(id+"F0.wireOp",EDGE,"E56"),sQuery(id+"F0.wireOp",EDGE,"E57"),sQuery(id+"F0.wireOp",EDGE,"E58"),sQuery(id+"F0.wireOp",EDGE,"E59"),sQuery(id+"F0.wireOp",EDGE,"E60"),sQuery(id+"F0.wireOp",EDGE,"E61"),sQuery(id+"F0.wireOp",EDGE,"E62"),sQuery(id+"F0.wireOp",EDGE,"E63"),sQuery(id+"F0.wireOp",EDGE,"E64"),sQuery(id+"F0.wireOp",EDGE,"E65"),sQuery(id+"F0.wireOp",EDGE,"E66"),sQuery(id+"F0.wireOp",EDGE,"E67"),sQuery(id+"F0.wireOp",EDGE,"E68"),sQuery(id+"F0.wireOp",EDGE,"E69"),sQuery(id+"F0.wireOp",EDGE,"E70"),sQuery(id+"F0.wireOp",EDGE,"E71"),sQuery(id+"F0.wireOp",EDGE,"E72"),sQuery(id+"F0.wireOp",EDGE,"E73"),sQuery(id+"F0.wireOp",EDGE,"E74"),sQuery(id+"F0.wireOp",EDGE,"E75"),sQuery(id+"F0.wireOp",EDGE,"E76"),sQuery(id+"F0.wireOp",EDGE,"E77"),sQuery(id+"F0.wireOp",EDGE,"E78"),sQuery(id+"F0.wireOp",EDGE,"E79"),sQuery(id+"F0.wireOp",EDGE,"E80"),sQuery(id+"F0.wireOp",EDGE,"E81"),sQuery(id+"F0.wireOp",EDGE,"E82"),sQuery(id+"F0.wireOp",EDGE,"E83"),sQuery(id+"F0.wireOp",EDGE,"E84"),sQuery(id+"F0.wireOp",EDGE,"E85"),sQuery(id+"F0.wireOp",EDGE,"E86"),sQuery(id+"F0.wireOp",EDGE,"E87"),sQuery(id+"F0.wireOp",EDGE,"E88"),sQuery(id+"F0.wireOp",EDGE,"E89"),sQuery(id+"F0.wireOp",EDGE,"E90"),sQuery(id+"F0.wireOp",EDGE,"E91"),sQuery(id+"F0.wireOp",EDGE,"E92"),sQuery(id+"F0.wireOp",EDGE,"E93"),sQuery(id+"F0.wireOp",EDGE,"E94"),sQuery(id+"F0.wireOp",EDGE,"E95"),sQuery(id+"F0.wireOp",EDGE,"E96"),sQuery(id+"F0.wireOp",EDGE,"E97"),sQuery(id+"F0.wireOp",EDGE,"E98"),sQuery(id+"F0.wireOp",EDGE,"E99"),sQuery(id+"F0.wireOp",EDGE,"E100"),sQuery(id+"F0.wireOp",EDGE,"E101"),sQuery(id+"F0.wireOp",EDGE,"E102"),sQuery(id+"F0.wireOp",EDGE,"E103"),sQuery(id+"F0.wireOp",EDGE,"E104"),sQuery(id+"F0.wireOp",EDGE,"E105"),sQuery(id+"F0.wireOp",EDGE,"E106"),sQuery(id+"F0.wireOp",EDGE,"E107"),sQuery(id+"F0.wireOp",EDGE,"E108"),sQuery(id+"F0.wireOp",EDGE,"E109"),sQuery(id+"F0.wireOp",EDGE,"E110"),sQuery(id+"F0.wireOp",EDGE,"E111"),sQuery(id+"F0.wireOp",EDGE,"E112"),sQuery(id+"F0.wireOp",EDGE,"E113"),sQuery(id+"F0.wireOp",EDGE,"E114"),sQuery(id+"F0.wireOp",EDGE,"E115"),sQuery(id+"F0.wireOp",EDGE,"E116"),sQuery(id+"F0.wireOp",EDGE,"E117"),sQuery(id+"F0.wireOp",EDGE,"E118"),sQuery(id+"F0.wireOp",EDGE,"E119"),sQuery(id+"F0.wireOp",EDGE,"E120"),sQuery(id+"F0.wireOp",EDGE,"E121"),sQuery(id+"F0.wireOp",EDGE,"E122"),sQuery(id+"F0.wireOp",EDGE,"E123"),sQuery(id+"F0.wireOp",EDGE,"E124"),sQuery(id+"F0.wireOp",EDGE,"E125"),sQuery(id+"F0.wireOp",EDGE,"E126"),sQuery(id+"F0.wireOp",EDGE,"E127"),sQuery(id+"F0.wireOp",EDGE,"E128"),sQuery(id+"F0.wireOp",EDGE,"E129"),sQuery(id+"F0.wireOp",EDGE,"E130"),sQuery(id+"F0.wireOp",EDGE,"E131"),sQuery(id+"F0.wireOp",EDGE,"E132"),sQuery(id+"F0.wireOp",EDGE,"E133"),sQuery(id+"F0.wireOp",EDGE,"E134"),sQuery(id+"F0.wireOp",EDGE,"E135"),sQuery(id+"F0.wireOp",EDGE,"E136"),sQuery(id+"F0.wireOp",EDGE,"E137"),sQuery(id+"F0.wireOp",EDGE,"E138"),sQuery(id+"F0.wireOp",EDGE,"E139"),sQuery(id+"F0.wireOp",EDGE,"E140"),sQuery(id+"F0.wireOp",EDGE,"E141"),sQuery(id+"F0.wireOp",EDGE,"E142"),sQuery(id+"F0.wireOp",EDGE,"E143"),sQuery(id+"F0.wireOp",EDGE,"E144"),sQuery(id+"F0.wireOp",EDGE,"E145"),sQuery(id+"F0.wireOp",EDGE,"E146"),sQuery(id+"F0.wireOp",EDGE,"E147"),sQuery(id+"F0.wireOp",EDGE,"E148"),sQuery(id+"F0.wireOp",EDGE,"E149"),sQuery(id+"F0.wireOp",EDGE,"E150"),sQuery(id+"F0.wireOp",EDGE,"E151"),sQuery(id+"F0.wireOp",EDGE,"E152"),sQuery(id+"F0.wireOp",EDGE,"E153"),sQuery(id+"F0.wireOp",EDGE,"E154"),sQuery(id+"F0.wireOp",EDGE,"E155"),sQuery(id+"F0.wireOp",EDGE,"E156"),sQuery(id+"F0.wireOp",EDGE,"E157"),sQuery(id+"F0.wireOp",EDGE,"E158"),sQuery(id+"F0.wireOp",EDGE,"E159"),sQuery(id+"F0.wireOp",EDGE,"E160"),sQuery(id+"F0.wireOp",EDGE,"E161"),sQuery(id+"F0.wireOp",EDGE,"E162"),sQuery(id+"F0.wireOp",EDGE,"E163"),sQuery(id+"F0.wireOp",EDGE,"E164"),sQuery(id+"F0.wireOp",EDGE,"E165"),sQuery(id+"F0.wireOp",EDGE,"E166"),sQuery(id+"F0.wireOp",EDGE,"E167"),sQuery(id+"F0.wireOp",EDGE,"E168"),sQuery(id+"F0.wireOp",EDGE,"E169"),sQuery(id+"F0.wireOp",EDGE,"E170"),sQuery(id+"F0.wireOp",EDGE,"E171"),sQuery(id+"F0.wireOp",EDGE,"E172"),sQuery(id+"F0.wireOp",EDGE,"E173"),sQuery(id+"F0.wireOp",EDGE,"E174"),sQuery(id+"F0.wireOp",EDGE,"E175"),sQuery(id+"F0.wireOp",EDGE,"E176"),sQuery(id+"F0.wireOp",EDGE,"E177"),sQuery(id+"F0.wireOp",EDGE,"E178"),sQuery(id+"F0.wireOp",EDGE,"E179"),sQuery(id+"F0.wireOp",EDGE,"E180"),sQuery(id+"F0.wireOp",EDGE,"E181"),sQuery(id+"F0.wireOp",EDGE,"E182"),sQuery(id+"F0.wireOp",EDGE,"E183"),sQuery(id+"F0.wireOp",EDGE,"E184"),sQuery(id+"F0.wireOp",EDGE,"E185"),sQuery(id+"F0.wireOp",EDGE,"E186")])],"isStart":false});
            var sketch = newSketch(context, id + "F6", { "sketchPlane" : qUnion([Q0])});
            skSolve(sketch);
        }
        {
            var Q0;
            Q0=makeQuery(id+"F6.imprint","IMPRINT",FACE,{"disambiguationData":[TD([[makeQuery(id+"F6.imprint","IMPRINT",EDGE,{"derivedFrom":makeQuery(id+"F2.opExtrude","CAP_EDGE",EDGE,{"disambiguationData":[OSD([sQuery(id+"F0.wireOp",EDGE,"E126")])],"isStart":false})}),-1.0]])]});
            var Q1;
            Q1=makeQuery(id+"F6.imprint","IMPRINT",FACE,{"disambiguationData":[TD([[makeQuery(id+"F6.imprint","IMPRINT",EDGE,{"derivedFrom":makeQuery(id+"F2.opExtrude","CAP_EDGE",EDGE,{"disambiguationData":[OSD([sQuery(id+"F0.wireOp",EDGE,"E127")])],"isStart":false})}),-1.0]])]});
            var Q2;
            Q2=makeQuery(id+"F6.imprint","IMPRINT",FACE,{"disambiguationData":[TD([[makeQuery(id+"F6.imprint","IMPRINT",EDGE,{"derivedFrom":makeQuery(id+"F2.opExtrude","CAP_EDGE",EDGE,{"disambiguationData":[OSD([sQuery(id+"F0.wireOp",EDGE,"E128")])],"isStart":false})}),-1.0]])]});
            var Q3;
            Q3=makeQuery(id+"F6.imprint","IMPRINT",FACE,{"disambiguationData":[TD([[makeQuery(id+"F6.imprint","IMPRINT",EDGE,{"derivedFrom":makeQuery(id+"F2.opExtrude","CAP_EDGE",EDGE,{"disambiguationData":[OSD([sQuery(id+"F0.wireOp",EDGE,"E124")])],"isStart":false})}),-1.0]])]});
            var Q4;
            Q4=makeQuery(id+"F6.imprint","IMPRINT",FACE,{"disambiguationData":[TD([[makeQuery(id+"F6.imprint","IMPRINT",EDGE,{"derivedFrom":makeQuery(id+"F2.opExtrude","CAP_EDGE",EDGE,{"disambiguationData":[OSD([sQuery(id+"F0.wireOp",EDGE,"E125")])],"isStart":false})}),-1.0]])]});
            var Q5;
            Q5=makeQuery(id+"F6.imprint","IMPRINT",FACE,{"disambiguationData":[TD([[makeQuery(id+"F6.imprint","IMPRINT",EDGE,{"derivedFrom":makeQuery(id+"F2.opExtrude","CAP_EDGE",EDGE,{"disambiguationData":[OSD([sQuery(id+"F0.wireOp",EDGE,"E129")])],"isStart":false})}),-1.0]])]});
            var Q6;
            Q6=makeQuery(id+"F6.imprint","IMPRINT",FACE,{"disambiguationData":[TD([[makeQuery(id+"F6.imprint","IMPRINT",EDGE,{"derivedFrom":makeQuery(id+"F2.opExtrude","CAP_EDGE",EDGE,{"disambiguationData":[OSD([sQuery(id+"F0.wireOp",EDGE,"E130")])],"isStart":false})}),-1.0]])]});
            var Q7;
            Q7=makeQuery(id+"F6.imprint","IMPRINT",FACE,{"disambiguationData":[TD([[makeQuery(id+"F6.imprint","IMPRINT",EDGE,{"derivedFrom":makeQuery(id+"F2.opExtrude","CAP_EDGE",EDGE,{"disambiguationData":[OSD([sQuery(id+"F0.wireOp",EDGE,"E133")])],"isStart":false})}),-1.0]])]});
            var Q8;
            Q8=makeQuery(id+"F6.imprint","IMPRINT",FACE,{"disambiguationData":[TD([[makeQuery(id+"F6.imprint","IMPRINT",EDGE,{"derivedFrom":makeQuery(id+"F2.opExtrude","CAP_EDGE",EDGE,{"disambiguationData":[OSD([sQuery(id+"F0.wireOp",EDGE,"E134")])],"isStart":false})}),-1.0]])]});
            var Q9;
            Q9=makeQuery(id+"F6.imprint","IMPRINT",FACE,{"disambiguationData":[TD([[makeQuery(id+"F6.imprint","IMPRINT",EDGE,{"derivedFrom":makeQuery(id+"F2.opExtrude","CAP_EDGE",EDGE,{"disambiguationData":[OSD([sQuery(id+"F0.wireOp",EDGE,"E135")])],"isStart":false})}),-1.0]])]});
            var Q10;
            Q10=makeQuery(id+"F6.imprint","IMPRINT",FACE,{"disambiguationData":[TD([[makeQuery(id+"F6.imprint","IMPRINT",EDGE,{"derivedFrom":makeQuery(id+"F2.opExtrude","CAP_EDGE",EDGE,{"disambiguationData":[OSD([sQuery(id+"F0.wireOp",EDGE,"E132")])],"isStart":false})}),-1.0]])]});
            var Q11;
            Q11=makeQuery(id+"F6.imprint","IMPRINT",FACE,{"disambiguationData":[TD([[makeQuery(id+"F6.imprint","IMPRINT",EDGE,{"derivedFrom":makeQuery(id+"F2.opExtrude","CAP_EDGE",EDGE,{"disambiguationData":[OSD([sQuery(id+"F0.wireOp",EDGE,"E131")])],"isStart":false})}),-1.0]])]});
            var Q12;
            Q12=makeQuery(id+"F6.imprint","IMPRINT",FACE,{"disambiguationData":[TD([[makeQuery(id+"F6.imprint","IMPRINT",EDGE,{"derivedFrom":makeQuery(id+"F2.opExtrude","CAP_EDGE",EDGE,{"disambiguationData":[OSD([sQuery(id+"F0.wireOp",EDGE,"E141")])],"isStart":false})}),-1.0]])]});
            var Q13;
            Q13=makeQuery(id+"F6.imprint","IMPRINT",FACE,{"disambiguationData":[TD([[makeQuery(id+"F6.imprint","IMPRINT",EDGE,{"derivedFrom":makeQuery(id+"F2.opExtrude","CAP_EDGE",EDGE,{"disambiguationData":[OSD([sQuery(id+"F0.wireOp",EDGE,"E140")])],"isStart":false})}),-1.0]])]});
            var Q14;
            Q14=makeQuery(id+"F6.imprint","IMPRINT",FACE,{"disambiguationData":[TD([[makeQuery(id+"F6.imprint","IMPRINT",EDGE,{"derivedFrom":makeQuery(id+"F2.opExtrude","CAP_EDGE",EDGE,{"disambiguationData":[OSD([sQuery(id+"F0.wireOp",EDGE,"E139")])],"isStart":false})}),-1.0]])]});
            var Q15;
            Q15=makeQuery(id+"F6.imprint","IMPRINT",FACE,{"disambiguationData":[TD([[makeQuery(id+"F6.imprint","IMPRINT",EDGE,{"derivedFrom":makeQuery(id+"F2.opExtrude","CAP_EDGE",EDGE,{"disambiguationData":[OSD([sQuery(id+"F0.wireOp",EDGE,"E138")])],"isStart":false})}),-1.0]])]});
            var Q16;
            Q16=makeQuery(id+"F6.imprint","IMPRINT",FACE,{"disambiguationData":[TD([[makeQuery(id+"F6.imprint","IMPRINT",EDGE,{"derivedFrom":makeQuery(id+"F2.opExtrude","CAP_EDGE",EDGE,{"disambiguationData":[OSD([sQuery(id+"F0.wireOp",EDGE,"E137")])],"isStart":false})}),-1.0]])]});
            var Q17;
            Q17=makeQuery(id+"F6.imprint","IMPRINT",FACE,{"disambiguationData":[TD([[makeQuery(id+"F6.imprint","IMPRINT",EDGE,{"derivedFrom":makeQuery(id+"F2.opExtrude","CAP_EDGE",EDGE,{"disambiguationData":[OSD([sQuery(id+"F0.wireOp",EDGE,"E136")])],"isStart":false})}),-1.0]])]});
            var Q18;
            Q18=makeQuery(id+"F6.imprint","IMPRINT",FACE,{"disambiguationData":[TD([[makeQuery(id+"F6.imprint","IMPRINT",EDGE,{"derivedFrom":makeQuery(id+"F2.opExtrude","CAP_EDGE",EDGE,{"disambiguationData":[OSD([sQuery(id+"F0.wireOp",EDGE,"E117")])],"isStart":false})}),-1.0]])]});
            var Q19;
            Q19=makeQuery(id+"F6.imprint","IMPRINT",FACE,{"disambiguationData":[TD([[makeQuery(id+"F6.imprint","IMPRINT",EDGE,{"derivedFrom":makeQuery(id+"F2.opExtrude","CAP_EDGE",EDGE,{"disambiguationData":[OSD([sQuery(id+"F0.wireOp",EDGE,"E118")])],"isStart":false})}),-1.0]])]});
            var Q20;
            Q20=makeQuery(id+"F6.imprint","IMPRINT",FACE,{"disambiguationData":[TD([[makeQuery(id+"F6.imprint","IMPRINT",EDGE,{"derivedFrom":makeQuery(id+"F2.opExtrude","CAP_EDGE",EDGE,{"disambiguationData":[OSD([sQuery(id+"F0.wireOp",EDGE,"E119")])],"isStart":false})}),-1.0]])]});
            var Q21;
            Q21=makeQuery(id+"F6.imprint","IMPRINT",FACE,{"disambiguationData":[TD([[makeQuery(id+"F6.imprint","IMPRINT",EDGE,{"derivedFrom":makeQuery(id+"F2.opExtrude","CAP_EDGE",EDGE,{"disambiguationData":[OSD([sQuery(id+"F0.wireOp",EDGE,"E106")])],"isStart":false})}),-1.0]])]});
            var Q22;
            Q22=makeQuery(id+"F6.imprint","IMPRINT",FACE,{"disambiguationData":[TD([[makeQuery(id+"F6.imprint","IMPRINT",EDGE,{"derivedFrom":makeQuery(id+"F2.opExtrude","CAP_EDGE",EDGE,{"disambiguationData":[OSD([sQuery(id+"F0.wireOp",EDGE,"E110")])],"isStart":false})}),-1.0]])]});
            var Q23;
            Q23=makeQuery(id+"F6.imprint","IMPRINT",FACE,{"disambiguationData":[TD([[makeQuery(id+"F6.imprint","IMPRINT",EDGE,{"derivedFrom":makeQuery(id+"F2.opExtrude","CAP_EDGE",EDGE,{"disambiguationData":[OSD([sQuery(id+"F0.wireOp",EDGE,"E109")])],"isStart":false})}),-1.0]])]});
            var Q24;
            Q24=makeQuery(id+"F6.imprint","IMPRINT",FACE,{"disambiguationData":[TD([[makeQuery(id+"F6.imprint","IMPRINT",EDGE,{"derivedFrom":makeQuery(id+"F2.opExtrude","CAP_EDGE",EDGE,{"disambiguationData":[OSD([sQuery(id+"F0.wireOp",EDGE,"E108")])],"isStart":false})}),-1.0]])]});
            var Q25;
            Q25=makeQuery(id+"F6.imprint","IMPRINT",FACE,{"disambiguationData":[TD([[makeQuery(id+"F6.imprint","IMPRINT",EDGE,{"derivedFrom":makeQuery(id+"F2.opExtrude","CAP_EDGE",EDGE,{"disambiguationData":[OSD([sQuery(id+"F0.wireOp",EDGE,"E116")])],"isStart":false})}),-1.0]])]});
            var Q26;
            Q26=makeQuery(id+"F6.imprint","IMPRINT",FACE,{"disambiguationData":[TD([[makeQuery(id+"F6.imprint","IMPRINT",EDGE,{"derivedFrom":makeQuery(id+"F2.opExtrude","CAP_EDGE",EDGE,{"disambiguationData":[OSD([sQuery(id+"F0.wireOp",EDGE,"E115")])],"isStart":false})}),-1.0]])]});
            var Q27;
            Q27=makeQuery(id+"F6.imprint","IMPRINT",FACE,{"disambiguationData":[TD([[makeQuery(id+"F6.imprint","IMPRINT",EDGE,{"derivedFrom":makeQuery(id+"F2.opExtrude","CAP_EDGE",EDGE,{"disambiguationData":[OSD([sQuery(id+"F0.wireOp",EDGE,"E114")])],"isStart":false})}),-1.0]])]});
            var Q28;
            Q28=makeQuery(id+"F6.imprint","IMPRINT",FACE,{"disambiguationData":[TD([[makeQuery(id+"F6.imprint","IMPRINT",EDGE,{"derivedFrom":makeQuery(id+"F2.opExtrude","CAP_EDGE",EDGE,{"disambiguationData":[OSD([sQuery(id+"F0.wireOp",EDGE,"E113")])],"isStart":false})}),-1.0]])]});
            var Q29;
            Q29=makeQuery(id+"F6.imprint","IMPRINT",FACE,{"disambiguationData":[TD([[makeQuery(id+"F6.imprint","IMPRINT",EDGE,{"derivedFrom":makeQuery(id+"F2.opExtrude","CAP_EDGE",EDGE,{"disambiguationData":[OSD([sQuery(id+"F0.wireOp",EDGE,"E123")])],"isStart":false})}),-1.0]])]});
            var Q30;
            Q30=makeQuery(id+"F6.imprint","IMPRINT",FACE,{"disambiguationData":[TD([[makeQuery(id+"F6.imprint","IMPRINT",EDGE,{"derivedFrom":makeQuery(id+"F2.opExtrude","CAP_EDGE",EDGE,{"disambiguationData":[OSD([sQuery(id+"F0.wireOp",EDGE,"E122")])],"isStart":false})}),-1.0]])]});
            var Q31;
            Q31=makeQuery(id+"F6.imprint","IMPRINT",FACE,{"disambiguationData":[TD([[makeQuery(id+"F6.imprint","IMPRINT",EDGE,{"derivedFrom":makeQuery(id+"F2.opExtrude","CAP_EDGE",EDGE,{"disambiguationData":[OSD([sQuery(id+"F0.wireOp",EDGE,"E120")])],"isStart":false})}),-1.0]])]});
            var Q32;
            Q32=makeQuery(id+"F6.imprint","IMPRINT",FACE,{"disambiguationData":[TD([[makeQuery(id+"F6.imprint","IMPRINT",EDGE,{"derivedFrom":makeQuery(id+"F2.opExtrude","CAP_EDGE",EDGE,{"disambiguationData":[OSD([sQuery(id+"F0.wireOp",EDGE,"E121")])],"isStart":false})}),-1.0]])]});
            var Q33;
            Q33=makeQuery(id+"F6.imprint","IMPRINT",FACE,{"disambiguationData":[TD([[makeQuery(id+"F6.imprint","IMPRINT",EDGE,{"derivedFrom":makeQuery(id+"F2.opExtrude","CAP_EDGE",EDGE,{"disambiguationData":[OSD([sQuery(id+"F0.wireOp",EDGE,"E111")])],"isStart":false})}),-1.0]])]});
            var Q34;
            Q34=makeQuery(id+"F6.imprint","IMPRINT",FACE,{"disambiguationData":[TD([[makeQuery(id+"F6.imprint","IMPRINT",EDGE,{"derivedFrom":makeQuery(id+"F2.opExtrude","CAP_EDGE",EDGE,{"disambiguationData":[OSD([sQuery(id+"F0.wireOp",EDGE,"E112")])],"isStart":false})}),-1.0]])]});
            var Q35;
            Q35=makeQuery(id+"F6.imprint","IMPRINT",FACE,{"disambiguationData":[TD([[makeQuery(id+"F6.imprint","IMPRINT",EDGE,{"derivedFrom":makeQuery(id+"F2.opExtrude","CAP_EDGE",EDGE,{"disambiguationData":[OSD([sQuery(id+"F0.wireOp",EDGE,"E107")])],"isStart":false})}),-1.0]])]});
            var Q36;
            Q36=makeQuery(id+"F6.imprint","IMPRINT",FACE,{"disambiguationData":[TD([[makeQuery(id+"F6.imprint","IMPRINT",EDGE,{"derivedFrom":makeQuery(id+"F2.opExtrude","CAP_EDGE",EDGE,{"disambiguationData":[OSD([sQuery(id+"F0.wireOp",EDGE,"E105")])],"isStart":false})}),-1.0]])]});
            var Q37;
            Q37=makeQuery(id+"F6.imprint","IMPRINT",FACE,{"disambiguationData":[TD([[makeQuery(id+"F6.imprint","IMPRINT",EDGE,{"derivedFrom":makeQuery(id+"F2.opExtrude","CAP_EDGE",EDGE,{"disambiguationData":[OSD([sQuery(id+"F0.wireOp",EDGE,"E104")])],"isStart":false})}),-1.0]])]});
            var Q38;
            Q38=makeQuery(id+"F6.imprint","IMPRINT",FACE,{"disambiguationData":[TD([[makeQuery(id+"F6.imprint","IMPRINT",EDGE,{"derivedFrom":makeQuery(id+"F2.opExtrude","CAP_EDGE",EDGE,{"disambiguationData":[OSD([sQuery(id+"F0.wireOp",EDGE,"E103")])],"isStart":false})}),-1.0]])]});
            var Q39;
            Q39=makeQuery(id+"F6.imprint","IMPRINT",FACE,{"disambiguationData":[TD([[makeQuery(id+"F6.imprint","IMPRINT",EDGE,{"derivedFrom":makeQuery(id+"F2.opExtrude","CAP_EDGE",EDGE,{"disambiguationData":[OSD([sQuery(id+"F0.wireOp",EDGE,"E102")])],"isStart":false})}),-1.0]])]});
            var Q40;
            Q40=makeQuery(id+"F6.imprint","IMPRINT",FACE,{"disambiguationData":[TD([[makeQuery(id+"F6.imprint","IMPRINT",EDGE,{"derivedFrom":makeQuery(id+"F2.opExtrude","CAP_EDGE",EDGE,{"disambiguationData":[OSD([sQuery(id+"F0.wireOp",EDGE,"E101")])],"isStart":false})}),-1.0]])]});
            var Q41;
            Q41=makeQuery(id+"F6.imprint","IMPRINT",FACE,{"disambiguationData":[TD([[makeQuery(id+"F6.imprint","IMPRINT",EDGE,{"derivedFrom":makeQuery(id+"F2.opExtrude","CAP_EDGE",EDGE,{"disambiguationData":[OSD([sQuery(id+"F0.wireOp",EDGE,"E100")])],"isStart":false})}),-1.0]])]});
            var Q42;
            Q42=makeQuery(id+"F6.imprint","IMPRINT",FACE,{"disambiguationData":[TD([[makeQuery(id+"F6.imprint","IMPRINT",EDGE,{"derivedFrom":makeQuery(id+"F2.opExtrude","CAP_EDGE",EDGE,{"disambiguationData":[OSD([sQuery(id+"F0.wireOp",EDGE,"E99")])],"isStart":false})}),-1.0]])]});
            var Q43;
            Q43=makeQuery(id+"F6.imprint","IMPRINT",FACE,{"disambiguationData":[TD([[makeQuery(id+"F6.imprint","IMPRINT",EDGE,{"derivedFrom":makeQuery(id+"F2.opExtrude","CAP_EDGE",EDGE,{"disambiguationData":[OSD([sQuery(id+"F0.wireOp",EDGE,"E98")])],"isStart":false})}),-1.0]])]});
            var Q44;
            Q44=makeQuery(id+"F6.imprint","IMPRINT",FACE,{"disambiguationData":[TD([[makeQuery(id+"F6.imprint","IMPRINT",EDGE,{"derivedFrom":makeQuery(id+"F2.opExtrude","CAP_EDGE",EDGE,{"disambiguationData":[OSD([sQuery(id+"F0.wireOp",EDGE,"E97")])],"isStart":false})}),-1.0]])]});
            var Q45;
            Q45=makeQuery(id+"F6.imprint","IMPRINT",FACE,{"disambiguationData":[TD([[makeQuery(id+"F6.imprint","IMPRINT",EDGE,{"derivedFrom":makeQuery(id+"F2.opExtrude","CAP_EDGE",EDGE,{"disambiguationData":[OSD([sQuery(id+"F0.wireOp",EDGE,"E40")])],"isStart":false})}),-1.0]])]});
            var Q46;
            Q46=makeQuery(id+"F6.imprint","IMPRINT",FACE,{"disambiguationData":[TD([[makeQuery(id+"F6.imprint","IMPRINT",EDGE,{"derivedFrom":makeQuery(id+"F2.opExtrude","CAP_EDGE",EDGE,{"disambiguationData":[OSD([sQuery(id+"F0.wireOp",EDGE,"E39")])],"isStart":false})}),-1.0]])]});
            var Q47;
            Q47=makeQuery(id+"F6.imprint","IMPRINT",FACE,{"disambiguationData":[TD([[makeQuery(id+"F6.imprint","IMPRINT",EDGE,{"derivedFrom":makeQuery(id+"F2.opExtrude","CAP_EDGE",EDGE,{"disambiguationData":[OSD([sQuery(id+"F0.wireOp",EDGE,"E38")])],"isStart":false})}),-1.0]])]});
            var Q48;
            Q48=makeQuery(id+"F6.imprint","IMPRINT",FACE,{"disambiguationData":[TD([[makeQuery(id+"F6.imprint","IMPRINT",EDGE,{"derivedFrom":makeQuery(id+"F2.opExtrude","CAP_EDGE",EDGE,{"disambiguationData":[OSD([sQuery(id+"F0.wireOp",EDGE,"E37")])],"isStart":false})}),-1.0]])]});
            var Q49;
            Q49=makeQuery(id+"F6.imprint","IMPRINT",FACE,{"disambiguationData":[TD([[makeQuery(id+"F6.imprint","IMPRINT",EDGE,{"derivedFrom":makeQuery(id+"F2.opExtrude","CAP_EDGE",EDGE,{"disambiguationData":[OSD([sQuery(id+"F0.wireOp",EDGE,"E36")])],"isStart":false})}),-1.0]])]});
            var Q50;
            Q50=makeQuery(id+"F6.imprint","IMPRINT",FACE,{"disambiguationData":[TD([[makeQuery(id+"F6.imprint","IMPRINT",EDGE,{"derivedFrom":makeQuery(id+"F2.opExtrude","CAP_EDGE",EDGE,{"disambiguationData":[OSD([sQuery(id+"F0.wireOp",EDGE,"E35")])],"isStart":false})}),-1.0]])]});
            var Q51;
            Q51=makeQuery(id+"F6.imprint","IMPRINT",FACE,{"disambiguationData":[TD([[makeQuery(id+"F6.imprint","IMPRINT",EDGE,{"derivedFrom":makeQuery(id+"F2.opExtrude","CAP_EDGE",EDGE,{"disambiguationData":[OSD([sQuery(id+"F0.wireOp",EDGE,"E86")])],"isStart":false})}),-1.0]])]});
            var Q52;
            Q52=makeQuery(id+"F6.imprint","IMPRINT",FACE,{"disambiguationData":[TD([[makeQuery(id+"F6.imprint","IMPRINT",EDGE,{"derivedFrom":makeQuery(id+"F2.opExtrude","CAP_EDGE",EDGE,{"disambiguationData":[OSD([sQuery(id+"F0.wireOp",EDGE,"E87")])],"isStart":false})}),-1.0]])]});
            var Q53;
            Q53=makeQuery(id+"F6.imprint","IMPRINT",FACE,{"disambiguationData":[TD([[makeQuery(id+"F6.imprint","IMPRINT",EDGE,{"derivedFrom":makeQuery(id+"F2.opExtrude","CAP_EDGE",EDGE,{"disambiguationData":[OSD([sQuery(id+"F0.wireOp",EDGE,"E84")])],"isStart":false})}),-1.0]])]});
            var Q54;
            Q54=makeQuery(id+"F6.imprint","IMPRINT",FACE,{"disambiguationData":[TD([[makeQuery(id+"F6.imprint","IMPRINT",EDGE,{"derivedFrom":makeQuery(id+"F2.opExtrude","CAP_EDGE",EDGE,{"disambiguationData":[OSD([sQuery(id+"F0.wireOp",EDGE,"E85")])],"isStart":false})}),-1.0]])]});
            var Q55;
            Q55=makeQuery(id+"F6.imprint","IMPRINT",FACE,{"disambiguationData":[TD([[makeQuery(id+"F6.imprint","IMPRINT",EDGE,{"derivedFrom":makeQuery(id+"F2.opExtrude","CAP_EDGE",EDGE,{"disambiguationData":[OSD([sQuery(id+"F0.wireOp",EDGE,"E34")])],"isStart":false})}),-1.0]])]});
            var Q56;
            Q56=makeQuery(id+"F6.imprint","IMPRINT",FACE,{"disambiguationData":[TD([[makeQuery(id+"F6.imprint","IMPRINT",EDGE,{"derivedFrom":makeQuery(id+"F2.opExtrude","CAP_EDGE",EDGE,{"disambiguationData":[OSD([sQuery(id+"F0.wireOp",EDGE,"E33")])],"isStart":false})}),-1.0]])]});
            var Q57;
            Q57=makeQuery(id+"F6.imprint","IMPRINT",FACE,{"disambiguationData":[TD([[makeQuery(id+"F6.imprint","IMPRINT",EDGE,{"derivedFrom":makeQuery(id+"F2.opExtrude","CAP_EDGE",EDGE,{"disambiguationData":[OSD([sQuery(id+"F0.wireOp",EDGE,"E32")])],"isStart":false})}),-1.0]])]});
            var Q58;
            Q58=makeQuery(id+"F6.imprint","IMPRINT",FACE,{"disambiguationData":[TD([[makeQuery(id+"F6.imprint","IMPRINT",EDGE,{"derivedFrom":makeQuery(id+"F2.opExtrude","CAP_EDGE",EDGE,{"disambiguationData":[OSD([sQuery(id+"F0.wireOp",EDGE,"E31")])],"isStart":false})}),-1.0]])]});
            var Q59;
            Q59=makeQuery(id+"F6.imprint","IMPRINT",FACE,{"disambiguationData":[TD([[makeQuery(id+"F6.imprint","IMPRINT",EDGE,{"derivedFrom":makeQuery(id+"F2.opExtrude","CAP_EDGE",EDGE,{"disambiguationData":[OSD([sQuery(id+"F0.wireOp",EDGE,"E30")])],"isStart":false})}),-1.0]])]});
            var Q60;
            Q60=makeQuery(id+"F6.imprint","IMPRINT",FACE,{"disambiguationData":[TD([[makeQuery(id+"F6.imprint","IMPRINT",EDGE,{"derivedFrom":makeQuery(id+"F2.opExtrude","CAP_EDGE",EDGE,{"disambiguationData":[OSD([sQuery(id+"F0.wireOp",EDGE,"E29")])],"isStart":false})}),-1.0]])]});
            var Q61;
            Q61=makeQuery(id+"F6.imprint","IMPRINT",FACE,{"disambiguationData":[TD([[makeQuery(id+"F6.imprint","IMPRINT",EDGE,{"derivedFrom":makeQuery(id+"F2.opExtrude","CAP_EDGE",EDGE,{"disambiguationData":[OSD([sQuery(id+"F0.wireOp",EDGE,"E28")])],"isStart":false})}),-1.0]])]});
            var Q62;
            Q62=makeQuery(id+"F6.imprint","IMPRINT",FACE,{"disambiguationData":[TD([[makeQuery(id+"F6.imprint","IMPRINT",EDGE,{"derivedFrom":makeQuery(id+"F2.opExtrude","CAP_EDGE",EDGE,{"disambiguationData":[OSD([sQuery(id+"F0.wireOp",EDGE,"E27")])],"isStart":false})}),-1.0]])]});
            var Q63;
            Q63=makeQuery(id+"F6.imprint","IMPRINT",FACE,{"disambiguationData":[TD([[makeQuery(id+"F6.imprint","IMPRINT",EDGE,{"derivedFrom":makeQuery(id+"F2.opExtrude","CAP_EDGE",EDGE,{"disambiguationData":[OSD([sQuery(id+"F0.wireOp",EDGE,"E18")])],"isStart":false})}),-1.0]])]});
            var Q64;
            Q64=makeQuery(id+"F6.imprint","IMPRINT",FACE,{"disambiguationData":[TD([[makeQuery(id+"F6.imprint","IMPRINT",EDGE,{"derivedFrom":makeQuery(id+"F2.opExtrude","CAP_EDGE",EDGE,{"disambiguationData":[OSD([sQuery(id+"F0.wireOp",EDGE,"E19")])],"isStart":false})}),-1.0]])]});
            var Q65;
            Q65=makeQuery(id+"F6.imprint","IMPRINT",FACE,{"disambiguationData":[TD([[makeQuery(id+"F6.imprint","IMPRINT",EDGE,{"derivedFrom":makeQuery(id+"F2.opExtrude","CAP_EDGE",EDGE,{"disambiguationData":[OSD([sQuery(id+"F0.wireOp",EDGE,"E20")])],"isStart":false})}),-1.0]])]});
            var Q66;
            Q66=makeQuery(id+"F6.imprint","IMPRINT",FACE,{"disambiguationData":[TD([[makeQuery(id+"F6.imprint","IMPRINT",EDGE,{"derivedFrom":makeQuery(id+"F2.opExtrude","CAP_EDGE",EDGE,{"disambiguationData":[OSD([sQuery(id+"F0.wireOp",EDGE,"E21")])],"isStart":false})}),-1.0]])]});
            var Q67;
            Q67=makeQuery(id+"F6.imprint","IMPRINT",FACE,{"disambiguationData":[TD([[makeQuery(id+"F6.imprint","IMPRINT",EDGE,{"derivedFrom":makeQuery(id+"F2.opExtrude","CAP_EDGE",EDGE,{"disambiguationData":[OSD([sQuery(id+"F0.wireOp",EDGE,"E22")])],"isStart":false})}),-1.0]])]});
            var Q68;
            Q68=makeQuery(id+"F6.imprint","IMPRINT",FACE,{"disambiguationData":[TD([[makeQuery(id+"F6.imprint","IMPRINT",EDGE,{"derivedFrom":makeQuery(id+"F2.opExtrude","CAP_EDGE",EDGE,{"disambiguationData":[OSD([sQuery(id+"F0.wireOp",EDGE,"E25")])],"isStart":false})}),-1.0]])]});
            var Q69;
            Q69=makeQuery(id+"F6.imprint","IMPRINT",FACE,{"disambiguationData":[TD([[makeQuery(id+"F6.imprint","IMPRINT",EDGE,{"derivedFrom":makeQuery(id+"F2.opExtrude","CAP_EDGE",EDGE,{"disambiguationData":[OSD([sQuery(id+"F0.wireOp",EDGE,"E45")])],"isStart":false})}),-1.0]])]});
            var Q70;
            Q70=makeQuery(id+"F6.imprint","IMPRINT",FACE,{"disambiguationData":[TD([[makeQuery(id+"F6.imprint","IMPRINT",EDGE,{"derivedFrom":makeQuery(id+"F2.opExtrude","CAP_EDGE",EDGE,{"disambiguationData":[OSD([sQuery(id+"F0.wireOp",EDGE,"E47")])],"isStart":false})}),-1.0]])]});
            var Q71;
            Q71=makeQuery(id+"F6.imprint","IMPRINT",FACE,{"disambiguationData":[TD([[makeQuery(id+"F6.imprint","IMPRINT",EDGE,{"derivedFrom":makeQuery(id+"F2.opExtrude","CAP_EDGE",EDGE,{"disambiguationData":[OSD([sQuery(id+"F0.wireOp",EDGE,"E46")])],"isStart":false})}),-1.0]])]});
            var Q72;
            Q72=makeQuery(id+"F6.imprint","IMPRINT",FACE,{"disambiguationData":[TD([[makeQuery(id+"F6.imprint","IMPRINT",EDGE,{"derivedFrom":makeQuery(id+"F2.opExtrude","CAP_EDGE",EDGE,{"disambiguationData":[OSD([sQuery(id+"F0.wireOp",EDGE,"E44")])],"isStart":false})}),-1.0]])]});
            var Q73;
            Q73=makeQuery(id+"F6.imprint","IMPRINT",FACE,{"disambiguationData":[TD([[makeQuery(id+"F6.imprint","IMPRINT",EDGE,{"derivedFrom":makeQuery(id+"F2.opExtrude","CAP_EDGE",EDGE,{"disambiguationData":[OSD([sQuery(id+"F0.wireOp",EDGE,"E24")])],"isStart":false})}),-1.0]])]});
            var Q74;
            Q74=makeQuery(id+"F6.imprint","IMPRINT",FACE,{"disambiguationData":[TD([[makeQuery(id+"F6.imprint","IMPRINT",EDGE,{"derivedFrom":makeQuery(id+"F2.opExtrude","CAP_EDGE",EDGE,{"disambiguationData":[OSD([sQuery(id+"F0.wireOp",EDGE,"E13")])],"isStart":false})}),-1.0]])]});
            var Q75;
            Q75=makeQuery(id+"F6.imprint","IMPRINT",FACE,{"disambiguationData":[TD([[makeQuery(id+"F6.imprint","IMPRINT",EDGE,{"derivedFrom":makeQuery(id+"F2.opExtrude","CAP_EDGE",EDGE,{"disambiguationData":[OSD([sQuery(id+"F0.wireOp",EDGE,"E14")])],"isStart":false})}),-1.0]])]});
            var Q76;
            Q76=makeQuery(id+"F6.imprint","IMPRINT",FACE,{"disambiguationData":[TD([[makeQuery(id+"F6.imprint","IMPRINT",EDGE,{"derivedFrom":makeQuery(id+"F2.opExtrude","CAP_EDGE",EDGE,{"disambiguationData":[OSD([sQuery(id+"F0.wireOp",EDGE,"E15")])],"isStart":false})}),-1.0]])]});
            var Q77;
            Q77=makeQuery(id+"F6.imprint","IMPRINT",FACE,{"disambiguationData":[TD([[makeQuery(id+"F6.imprint","IMPRINT",EDGE,{"derivedFrom":makeQuery(id+"F2.opExtrude","CAP_EDGE",EDGE,{"disambiguationData":[OSD([sQuery(id+"F0.wireOp",EDGE,"E16")])],"isStart":false})}),-1.0]])]});
            var Q78;
            Q78=makeQuery(id+"F6.imprint","IMPRINT",FACE,{"disambiguationData":[TD([[makeQuery(id+"F6.imprint","IMPRINT",EDGE,{"derivedFrom":makeQuery(id+"F2.opExtrude","CAP_EDGE",EDGE,{"disambiguationData":[OSD([sQuery(id+"F0.wireOp",EDGE,"E17")])],"isStart":false})}),-1.0]])]});
            var Q79;
            Q79=makeQuery(id+"F6.imprint","IMPRINT",FACE,{"disambiguationData":[TD([[makeQuery(id+"F6.imprint","IMPRINT",EDGE,{"derivedFrom":makeQuery(id+"F2.opExtrude","CAP_EDGE",EDGE,{"disambiguationData":[OSD([sQuery(id+"F0.wireOp",EDGE,"E26")])],"isStart":false})}),-1.0]])]});
            var Q80;
            Q80=makeQuery(id+"F6.imprint","IMPRINT",FACE,{"disambiguationData":[TD([[makeQuery(id+"F6.imprint","IMPRINT",EDGE,{"derivedFrom":makeQuery(id+"F2.opExtrude","CAP_EDGE",EDGE,{"disambiguationData":[OSD([sQuery(id+"F0.wireOp",EDGE,"E7")])],"isStart":false})}),-1.0]])]});
            var Q81;
            Q81=makeQuery(id+"F6.imprint","IMPRINT",FACE,{"disambiguationData":[TD([[makeQuery(id+"F6.imprint","IMPRINT",EDGE,{"derivedFrom":makeQuery(id+"F2.opExtrude","CAP_EDGE",EDGE,{"disambiguationData":[OSD([sQuery(id+"F0.wireOp",EDGE,"E8")])],"isStart":false})}),-1.0]])]});
            var Q82;
            Q82=makeQuery(id+"F6.imprint","IMPRINT",FACE,{"disambiguationData":[TD([[makeQuery(id+"F6.imprint","IMPRINT",EDGE,{"derivedFrom":makeQuery(id+"F2.opExtrude","CAP_EDGE",EDGE,{"disambiguationData":[OSD([sQuery(id+"F0.wireOp",EDGE,"E9")])],"isStart":false})}),-1.0]])]});
            var Q83;
            Q83=makeQuery(id+"F6.imprint","IMPRINT",FACE,{"disambiguationData":[TD([[makeQuery(id+"F6.imprint","IMPRINT",EDGE,{"derivedFrom":makeQuery(id+"F2.opExtrude","CAP_EDGE",EDGE,{"disambiguationData":[OSD([sQuery(id+"F0.wireOp",EDGE,"E10")])],"isStart":false})}),-1.0]])]});
            var Q84;
            Q84=makeQuery(id+"F6.imprint","IMPRINT",FACE,{"disambiguationData":[TD([[makeQuery(id+"F6.imprint","IMPRINT",EDGE,{"derivedFrom":makeQuery(id+"F2.opExtrude","CAP_EDGE",EDGE,{"disambiguationData":[OSD([sQuery(id+"F0.wireOp",EDGE,"E11")])],"isStart":false})}),-1.0]])]});
            var Q85;
            Q85=makeQuery(id+"F6.imprint","IMPRINT",FACE,{"disambiguationData":[TD([[makeQuery(id+"F6.imprint","IMPRINT",EDGE,{"derivedFrom":makeQuery(id+"F2.opExtrude","CAP_EDGE",EDGE,{"disambiguationData":[OSD([sQuery(id+"F0.wireOp",EDGE,"E12")])],"isStart":false})}),-1.0]])]});
            var Q86;
            Q86=makeQuery(id+"F6.imprint","IMPRINT",FACE,{"disambiguationData":[TD([[makeQuery(id+"F6.imprint","IMPRINT",EDGE,{"derivedFrom":makeQuery(id+"F2.opExtrude","CAP_EDGE",EDGE,{"disambiguationData":[OSD([sQuery(id+"F0.wireOp",EDGE,"E23")])],"isStart":false})}),-1.0]])]});
            var Q87;
            Q87=makeQuery(id+"F6.imprint","IMPRINT",FACE,{"disambiguationData":[TD([[makeQuery(id+"F6.imprint","IMPRINT",EDGE,{"derivedFrom":makeQuery(id+"F2.opExtrude","CAP_EDGE",EDGE,{"disambiguationData":[OSD([sQuery(id+"F0.wireOp",EDGE,"E42")])],"isStart":false})}),-1.0]])]});
            var Q88;
            Q88=makeQuery(id+"F6.imprint","IMPRINT",FACE,{"disambiguationData":[TD([[makeQuery(id+"F6.imprint","IMPRINT",EDGE,{"derivedFrom":makeQuery(id+"F2.opExtrude","CAP_EDGE",EDGE,{"disambiguationData":[OSD([sQuery(id+"F0.wireOp",EDGE,"E43")])],"isStart":false})}),-1.0]])]});
            var Q89;
            Q89=makeQuery(id+"F6.imprint","IMPRINT",FACE,{"disambiguationData":[TD([[makeQuery(id+"F6.imprint","IMPRINT",EDGE,{"derivedFrom":makeQuery(id+"F2.opExtrude","CAP_EDGE",EDGE,{"disambiguationData":[OSD([sQuery(id+"F0.wireOp",EDGE,"E41")])],"isStart":false})}),-1.0]])]});
            extrude(context, id + "F7", {"entities" : qUnion([Q0, Q1, Q2, Q3, Q4, Q5, Q6, Q7, Q8, Q9, Q10, Q11, Q12, Q13, Q14, Q15, Q16, Q17, Q18, Q19, Q20, Q21, Q22, Q23, Q24, Q25, Q26, Q27, Q28, Q29, Q30, Q31, Q32, Q33, Q34, Q35, Q36, Q37, Q38, Q39, Q40, Q41, Q42, Q43, Q44, Q45, Q46, Q47, Q48, Q49, Q50, Q51, Q52, Q53, Q54, Q55, Q56, Q57, Q58, Q59, Q60, Q61, Q62, Q63, Q64, Q65, Q66, Q67, Q68, Q69, Q70, Q71, Q72, Q73, Q74, Q75, Q76, Q77, Q78, Q79, Q80, Q81, Q82, Q83, Q84, Q85, Q86, Q87, Q88, Q89]), "endBound" : BoundingType.SYMMETRIC, "depth" : 25 * mm, "offsetDistance" : 25 * mm, "hasDraft" : true, "draftAngle" : 1 * degree});
        }
        {
            var Q0;
            Q0=makeQuery(id+"F7.*.split.splitOp","SPLIT",BODY,{"derivedFrom":makeQuery(id+"F7.opExtrude","SWEPT_BODY",BODY,{"disambiguationData":[OSD([sQuery(id+"F0.wireOp",EDGE,"E7")])]})});
            var Q1;
            Q1=makeQuery(id+"F7.*.split.splitOp","SPLIT",BODY,{"derivedFrom":makeQuery(id+"F7.opExtrude","SWEPT_BODY",BODY,{"disambiguationData":[OSD([sQuery(id+"F0.wireOp",EDGE,"E8")])]})});
            var Q2;
            Q2=makeQuery(id+"F7.*.split.splitOp","SPLIT",BODY,{"derivedFrom":makeQuery(id+"F7.opExtrude","SWEPT_BODY",BODY,{"disambiguationData":[OSD([sQuery(id+"F0.wireOp",EDGE,"E17")])]})});
            var Q3;
            Q3=makeQuery(id+"F7.*.split.splitOp","SPLIT",BODY,{"derivedFrom":makeQuery(id+"F7.opExtrude","SWEPT_BODY",BODY,{"disambiguationData":[OSD([sQuery(id+"F0.wireOp",EDGE,"E26")])]})});
            var Q4;
            Q4=makeQuery(id+"F7.*.split.splitOp","SPLIT",BODY,{"derivedFrom":makeQuery(id+"F7.opExtrude","SWEPT_BODY",BODY,{"disambiguationData":[OSD([sQuery(id+"F0.wireOp",EDGE,"E27")])]})});
            var Q5;
            Q5=makeQuery(id+"F7.*.split.splitOp","SPLIT",BODY,{"derivedFrom":makeQuery(id+"F7.opExtrude","SWEPT_BODY",BODY,{"disambiguationData":[OSD([sQuery(id+"F0.wireOp",EDGE,"E18")])]})});
            var Q6;
            Q6=makeQuery(id+"F7.*.split.splitOp","SPLIT",BODY,{"derivedFrom":makeQuery(id+"F7.opExtrude","SWEPT_BODY",BODY,{"disambiguationData":[OSD([sQuery(id+"F0.wireOp",EDGE,"E29")])]})});
            var Q7;
            Q7=makeQuery(id+"F7.*.split.splitOp","SPLIT",BODY,{"derivedFrom":makeQuery(id+"F7.opExtrude","SWEPT_BODY",BODY,{"disambiguationData":[OSD([sQuery(id+"F0.wireOp",EDGE,"E28")])]})});
            var Q8;
            Q8=makeQuery(id+"F7.*.split.splitOp","SPLIT",BODY,{"derivedFrom":makeQuery(id+"F7.opExtrude","SWEPT_BODY",BODY,{"disambiguationData":[OSD([sQuery(id+"F0.wireOp",EDGE,"E41")])]})});
            var Q9;
            Q9=makeQuery(id+"F7.*.split.splitOp","SPLIT",BODY,{"derivedFrom":makeQuery(id+"F7.opExtrude","SWEPT_BODY",BODY,{"disambiguationData":[OSD([sQuery(id+"F0.wireOp",EDGE,"E40")])]})});
            var Q10;
            Q10=makeQuery(id+"F7.*.split.splitOp","SPLIT",BODY,{"derivedFrom":makeQuery(id+"F7.opExtrude","SWEPT_BODY",BODY,{"disambiguationData":[OSD([sQuery(id+"F0.wireOp",EDGE,"E98")])]})});
            var Q11;
            Q11=makeQuery(id+"F7.*.split.splitOp","SPLIT",BODY,{"derivedFrom":makeQuery(id+"F7.opExtrude","SWEPT_BODY",BODY,{"disambiguationData":[OSD([sQuery(id+"F0.wireOp",EDGE,"E97")])]})});
            var Q12;
            Q12=makeQuery(id+"F7.*.split.splitOp","SPLIT",BODY,{"derivedFrom":makeQuery(id+"F7.opExtrude","SWEPT_BODY",BODY,{"disambiguationData":[OSD([sQuery(id+"F0.wireOp",EDGE,"E120")])]})});
            var Q13;
            Q13=makeQuery(id+"F7.*.split.splitOp","SPLIT",BODY,{"derivedFrom":makeQuery(id+"F7.opExtrude","SWEPT_BODY",BODY,{"disambiguationData":[OSD([sQuery(id+"F0.wireOp",EDGE,"E121")])]})});
            var Q14;
            Q14=makeQuery(id+"F7.*.split.splitOp","SPLIT",BODY,{"derivedFrom":makeQuery(id+"F7.opExtrude","SWEPT_BODY",BODY,{"disambiguationData":[OSD([sQuery(id+"F0.wireOp",EDGE,"E123")])]})});
            var Q15;
            Q15=makeQuery(id+"F7.*.split.splitOp","SPLIT",BODY,{"derivedFrom":makeQuery(id+"F7.opExtrude","SWEPT_BODY",BODY,{"disambiguationData":[OSD([sQuery(id+"F0.wireOp",EDGE,"E122")])]})});
            var Q16;
            Q16=makeQuery(id+"F7.*.split.splitOp","SPLIT",BODY,{"derivedFrom":makeQuery(id+"F7.opExtrude","SWEPT_BODY",BODY,{"disambiguationData":[OSD([sQuery(id+"F0.wireOp",EDGE,"E124")])]})});
            var Q17;
            Q17=makeQuery(id+"F7.*.split.splitOp","SPLIT",BODY,{"derivedFrom":makeQuery(id+"F7.opExtrude","SWEPT_BODY",BODY,{"disambiguationData":[OSD([sQuery(id+"F0.wireOp",EDGE,"E125")])]})});
            var Q18;
            Q18=makeQuery(id+"F7.*.split.splitOp","SPLIT",BODY,{"derivedFrom":makeQuery(id+"F7.opExtrude","SWEPT_BODY",BODY,{"disambiguationData":[OSD([sQuery(id+"F0.wireOp",EDGE,"E127")])]})});
            var Q19;
            Q19=makeQuery(id+"F7.*.split.splitOp","SPLIT",BODY,{"derivedFrom":makeQuery(id+"F7.opExtrude","SWEPT_BODY",BODY,{"disambiguationData":[OSD([sQuery(id+"F0.wireOp",EDGE,"E126")])]})});
            var Q20;
            Q20=makeQuery(id+"F7.*.split.splitOp","SPLIT",BODY,{"derivedFrom":makeQuery(id+"F7.opExtrude","SWEPT_BODY",BODY,{"disambiguationData":[OSD([sQuery(id+"F0.wireOp",EDGE,"E9")])]})});
            var Q21;
            Q21=makeQuery(id+"F7.*.split.splitOp","SPLIT",BODY,{"derivedFrom":makeQuery(id+"F7.opExtrude","SWEPT_BODY",BODY,{"disambiguationData":[OSD([sQuery(id+"F0.wireOp",EDGE,"E16")])]})});
            var Q22;
            Q22=makeQuery(id+"F7.*.split.splitOp","SPLIT",BODY,{"derivedFrom":makeQuery(id+"F7.opExtrude","SWEPT_BODY",BODY,{"disambiguationData":[OSD([sQuery(id+"F0.wireOp",EDGE,"E19")])]})});
            var Q23;
            Q23=makeQuery(id+"F7.*.split.splitOp","SPLIT",BODY,{"derivedFrom":makeQuery(id+"F7.opExtrude","SWEPT_BODY",BODY,{"disambiguationData":[OSD([sQuery(id+"F0.wireOp",EDGE,"E30")])]})});
            var Q24;
            Q24=makeQuery(id+"F7.*.split.splitOp","SPLIT",BODY,{"derivedFrom":makeQuery(id+"F7.opExtrude","SWEPT_BODY",BODY,{"disambiguationData":[OSD([sQuery(id+"F0.wireOp",EDGE,"E39")])]})});
            var Q25;
            Q25=makeQuery(id+"F7.*.split.splitOp","SPLIT",BODY,{"derivedFrom":makeQuery(id+"F7.opExtrude","SWEPT_BODY",BODY,{"disambiguationData":[OSD([sQuery(id+"F0.wireOp",EDGE,"E99")])]})});
            var Q26;
            Q26=makeQuery(id+"F7.*.split.splitOp","SPLIT",BODY,{"derivedFrom":makeQuery(id+"F7.opExtrude","SWEPT_BODY",BODY,{"disambiguationData":[OSD([sQuery(id+"F0.wireOp",EDGE,"E111")])]})});
            var Q27;
            Q27=makeQuery(id+"F7.*.split.splitOp","SPLIT",BODY,{"derivedFrom":makeQuery(id+"F7.opExtrude","SWEPT_BODY",BODY,{"disambiguationData":[OSD([sQuery(id+"F0.wireOp",EDGE,"E113")])]})});
            var Q28;
            Q28=makeQuery(id+"F7.*.split.splitOp","SPLIT",BODY,{"derivedFrom":makeQuery(id+"F7.opExtrude","SWEPT_BODY",BODY,{"disambiguationData":[OSD([sQuery(id+"F0.wireOp",EDGE,"E129")])]})});
            var Q29;
            Q29=makeQuery(id+"F7.*.split.splitOp","SPLIT",BODY,{"derivedFrom":makeQuery(id+"F7.opExtrude","SWEPT_BODY",BODY,{"disambiguationData":[OSD([sQuery(id+"F0.wireOp",EDGE,"E128")])]})});
            var Q30;
            Q30=makeQuery(id+"F7.*.split.splitOp","SPLIT",BODY,{"derivedFrom":makeQuery(id+"F7.opExtrude","SWEPT_BODY",BODY,{"disambiguationData":[OSD([sQuery(id+"F0.wireOp",EDGE,"E10")])]})});
            var Q31;
            Q31=makeQuery(id+"F7.*.split.splitOp","SPLIT",BODY,{"derivedFrom":makeQuery(id+"F7.opExtrude","SWEPT_BODY",BODY,{"disambiguationData":[OSD([sQuery(id+"F0.wireOp",EDGE,"E15")])]})});
            var Q32;
            Q32=makeQuery(id+"F7.*.split.splitOp","SPLIT",BODY,{"derivedFrom":makeQuery(id+"F7.opExtrude","SWEPT_BODY",BODY,{"disambiguationData":[OSD([sQuery(id+"F0.wireOp",EDGE,"E20")])]})});
            var Q33;
            Q33=makeQuery(id+"F7.*.split.splitOp","SPLIT",BODY,{"derivedFrom":makeQuery(id+"F7.opExtrude","SWEPT_BODY",BODY,{"disambiguationData":[OSD([sQuery(id+"F0.wireOp",EDGE,"E31")])]})});
            var Q34;
            Q34=makeQuery(id+"F7.*.split.splitOp","SPLIT",BODY,{"derivedFrom":makeQuery(id+"F7.opExtrude","SWEPT_BODY",BODY,{"disambiguationData":[OSD([sQuery(id+"F0.wireOp",EDGE,"E38")])]})});
            var Q35;
            Q35=makeQuery(id+"F7.*.split.splitOp","SPLIT",BODY,{"derivedFrom":makeQuery(id+"F7.opExtrude","SWEPT_BODY",BODY,{"disambiguationData":[OSD([sQuery(id+"F0.wireOp",EDGE,"E100")])]})});
            var Q36;
            Q36=makeQuery(id+"F7.*.split.splitOp","SPLIT",BODY,{"derivedFrom":makeQuery(id+"F7.opExtrude","SWEPT_BODY",BODY,{"disambiguationData":[OSD([sQuery(id+"F0.wireOp",EDGE,"E112")])]})});
            var Q37;
            Q37=makeQuery(id+"F7.*.split.splitOp","SPLIT",BODY,{"derivedFrom":makeQuery(id+"F7.opExtrude","SWEPT_BODY",BODY,{"disambiguationData":[OSD([sQuery(id+"F0.wireOp",EDGE,"E114")])]})});
            var Q38;
            Q38=makeQuery(id+"F7.*.split.splitOp","SPLIT",BODY,{"derivedFrom":makeQuery(id+"F7.opExtrude","SWEPT_BODY",BODY,{"disambiguationData":[OSD([sQuery(id+"F0.wireOp",EDGE,"E130")])]})});
            var Q39;
            Q39=makeQuery(id+"F7.*.split.splitOp","SPLIT",BODY,{"derivedFrom":makeQuery(id+"F7.opExtrude","SWEPT_BODY",BODY,{"disambiguationData":[OSD([sQuery(id+"F0.wireOp",EDGE,"E131")])]})});
            var Q40;
            Q40=makeQuery(id+"F7.*.split.splitOp","SPLIT",BODY,{"derivedFrom":makeQuery(id+"F7.opExtrude","SWEPT_BODY",BODY,{"disambiguationData":[OSD([sQuery(id+"F0.wireOp",EDGE,"E132")])]})});
            var Q41;
            Q41=makeQuery(id+"F7.*.split.splitOp","SPLIT",BODY,{"derivedFrom":makeQuery(id+"F7.opExtrude","SWEPT_BODY",BODY,{"disambiguationData":[OSD([sQuery(id+"F0.wireOp",EDGE,"E133")])]})});
            var Q42;
            Q42=makeQuery(id+"F7.*.split.splitOp","SPLIT",BODY,{"derivedFrom":makeQuery(id+"F7.opExtrude","SWEPT_BODY",BODY,{"disambiguationData":[OSD([sQuery(id+"F0.wireOp",EDGE,"E115")])]})});
            var Q43;
            Q43=makeQuery(id+"F7.*.split.splitOp","SPLIT",BODY,{"derivedFrom":makeQuery(id+"F7.opExtrude","SWEPT_BODY",BODY,{"disambiguationData":[OSD([sQuery(id+"F0.wireOp",EDGE,"E107")])]})});
            var Q44;
            Q44=makeQuery(id+"F7.*.split.splitOp","SPLIT",BODY,{"derivedFrom":makeQuery(id+"F7.opExtrude","SWEPT_BODY",BODY,{"disambiguationData":[OSD([sQuery(id+"F0.wireOp",EDGE,"E101")])]})});
            var Q45;
            Q45=makeQuery(id+"F7.*.split.splitOp","SPLIT",BODY,{"derivedFrom":makeQuery(id+"F7.opExtrude","SWEPT_BODY",BODY,{"disambiguationData":[OSD([sQuery(id+"F0.wireOp",EDGE,"E37")])]})});
            var Q46;
            Q46=makeQuery(id+"F7.*.split.splitOp","SPLIT",BODY,{"derivedFrom":makeQuery(id+"F7.opExtrude","SWEPT_BODY",BODY,{"disambiguationData":[OSD([sQuery(id+"F0.wireOp",EDGE,"E32")])]})});
            var Q47;
            Q47=makeQuery(id+"F7.*.split.splitOp","SPLIT",BODY,{"derivedFrom":makeQuery(id+"F7.opExtrude","SWEPT_BODY",BODY,{"disambiguationData":[OSD([sQuery(id+"F0.wireOp",EDGE,"E21")])]})});
            var Q48;
            Q48=makeQuery(id+"F7.*.split.splitOp","SPLIT",BODY,{"derivedFrom":makeQuery(id+"F7.opExtrude","SWEPT_BODY",BODY,{"disambiguationData":[OSD([sQuery(id+"F0.wireOp",EDGE,"E14")])]})});
            var Q49;
            Q49=makeQuery(id+"F7.*.split.splitOp","SPLIT",BODY,{"derivedFrom":makeQuery(id+"F7.opExtrude","SWEPT_BODY",BODY,{"disambiguationData":[OSD([sQuery(id+"F0.wireOp",EDGE,"E11")])]})});
            var Q50;
            Q50=makeQuery(id+"F7.*.split.splitOp","SPLIT",BODY,{"derivedFrom":makeQuery(id+"F7.opExtrude","SWEPT_BODY",BODY,{"disambiguationData":[OSD([sQuery(id+"F0.wireOp",EDGE,"E12")])]})});
            var Q51;
            Q51=makeQuery(id+"F7.*.split.splitOp","SPLIT",BODY,{"derivedFrom":makeQuery(id+"F7.opExtrude","SWEPT_BODY",BODY,{"disambiguationData":[OSD([sQuery(id+"F0.wireOp",EDGE,"E13")])]})});
            var Q52;
            Q52=makeQuery(id+"F7.*.split.splitOp","SPLIT",BODY,{"derivedFrom":makeQuery(id+"F7.opExtrude","SWEPT_BODY",BODY,{"disambiguationData":[OSD([sQuery(id+"F0.wireOp",EDGE,"E22")])]})});
            var Q53;
            Q53=makeQuery(id+"F7.*.split.splitOp","SPLIT",BODY,{"derivedFrom":makeQuery(id+"F7.opExtrude","SWEPT_BODY",BODY,{"disambiguationData":[OSD([sQuery(id+"F0.wireOp",EDGE,"E33")])]})});
            var Q54;
            Q54=makeQuery(id+"F7.*.split.splitOp","SPLIT",BODY,{"derivedFrom":makeQuery(id+"F7.opExtrude","SWEPT_BODY",BODY,{"disambiguationData":[OSD([sQuery(id+"F0.wireOp",EDGE,"E36")])]})});
            var Q55;
            Q55=makeQuery(id+"F7.*.split.splitOp","SPLIT",BODY,{"derivedFrom":makeQuery(id+"F7.opExtrude","SWEPT_BODY",BODY,{"disambiguationData":[OSD([sQuery(id+"F0.wireOp",EDGE,"E102")])]})});
            var Q56;
            Q56=makeQuery(id+"F7.*.split.splitOp","SPLIT",BODY,{"derivedFrom":makeQuery(id+"F7.opExtrude","SWEPT_BODY",BODY,{"disambiguationData":[OSD([sQuery(id+"F0.wireOp",EDGE,"E108")])]})});
            var Q57;
            Q57=makeQuery(id+"F7.*.split.splitOp","SPLIT",BODY,{"derivedFrom":makeQuery(id+"F7.opExtrude","SWEPT_BODY",BODY,{"disambiguationData":[OSD([sQuery(id+"F0.wireOp",EDGE,"E116")])]})});
            var Q58;
            Q58=makeQuery(id+"F7.*.split.splitOp","SPLIT",BODY,{"derivedFrom":makeQuery(id+"F7.opExtrude","SWEPT_BODY",BODY,{"disambiguationData":[OSD([sQuery(id+"F0.wireOp",EDGE,"E134")])]})});
            var Q59;
            Q59=makeQuery(id+"F7.*.split.splitOp","SPLIT",BODY,{"derivedFrom":makeQuery(id+"F7.opExtrude","SWEPT_BODY",BODY,{"disambiguationData":[OSD([sQuery(id+"F0.wireOp",EDGE,"E135")])]})});
            var Q60;
            Q60=makeQuery(id+"F7.*.split.splitOp","SPLIT",BODY,{"derivedFrom":makeQuery(id+"F7.opExtrude","SWEPT_BODY",BODY,{"disambiguationData":[OSD([sQuery(id+"F0.wireOp",EDGE,"E23")])]})});
            var Q61;
            Q61=makeQuery(id+"F7.*.split.splitOp","SPLIT",BODY,{"derivedFrom":makeQuery(id+"F7.opExtrude","SWEPT_BODY",BODY,{"disambiguationData":[OSD([sQuery(id+"F0.wireOp",EDGE,"E24")])]})});
            var Q62;
            Q62=makeQuery(id+"F7.*.split.splitOp","SPLIT",BODY,{"derivedFrom":makeQuery(id+"F7.opExtrude","SWEPT_BODY",BODY,{"disambiguationData":[OSD([sQuery(id+"F0.wireOp",EDGE,"E25")])]})});
            var Q63;
            Q63=makeQuery(id+"F7.*.split.splitOp","SPLIT",BODY,{"derivedFrom":makeQuery(id+"F7.opExtrude","SWEPT_BODY",BODY,{"disambiguationData":[OSD([sQuery(id+"F0.wireOp",EDGE,"E34")])]})});
            var Q64;
            Q64=makeQuery(id+"F7.*.split.splitOp","SPLIT",BODY,{"derivedFrom":makeQuery(id+"F7.opExtrude","SWEPT_BODY",BODY,{"disambiguationData":[OSD([sQuery(id+"F0.wireOp",EDGE,"E35")])]})});
            var Q65;
            Q65=makeQuery(id+"F7.*.split.splitOp","SPLIT",BODY,{"derivedFrom":makeQuery(id+"F7.opExtrude","SWEPT_BODY",BODY,{"disambiguationData":[OSD([sQuery(id+"F0.wireOp",EDGE,"E103")])]})});
            var Q66;
            Q66=makeQuery(id+"F7.*.split.splitOp","SPLIT",BODY,{"derivedFrom":makeQuery(id+"F7.opExtrude","SWEPT_BODY",BODY,{"disambiguationData":[OSD([sQuery(id+"F0.wireOp",EDGE,"E109")])]})});
            var Q67;
            Q67=makeQuery(id+"F7.*.split.splitOp","SPLIT",BODY,{"derivedFrom":makeQuery(id+"F7.opExtrude","SWEPT_BODY",BODY,{"disambiguationData":[OSD([sQuery(id+"F0.wireOp",EDGE,"E117")])]})});
            var Q68;
            Q68=makeQuery(id+"F7.*.split.splitOp","SPLIT",BODY,{"derivedFrom":makeQuery(id+"F7.opExtrude","SWEPT_BODY",BODY,{"disambiguationData":[OSD([sQuery(id+"F0.wireOp",EDGE,"E136")])]})});
            var Q69;
            Q69=makeQuery(id+"F7.*.split.splitOp","SPLIT",BODY,{"derivedFrom":makeQuery(id+"F7.opExtrude","SWEPT_BODY",BODY,{"disambiguationData":[OSD([sQuery(id+"F0.wireOp",EDGE,"E141")])]})});
            var Q70;
            Q70=makeQuery(id+"F7.*.split.splitOp","SPLIT",BODY,{"derivedFrom":makeQuery(id+"F7.opExtrude","SWEPT_BODY",BODY,{"disambiguationData":[OSD([sQuery(id+"F0.wireOp",EDGE,"E140")])]})});
            var Q71;
            Q71=makeQuery(id+"F7.*.split.splitOp","SPLIT",BODY,{"derivedFrom":makeQuery(id+"F7.opExtrude","SWEPT_BODY",BODY,{"disambiguationData":[OSD([sQuery(id+"F0.wireOp",EDGE,"E137")])]})});
            var Q72;
            Q72=makeQuery(id+"F7.*.split.splitOp","SPLIT",BODY,{"derivedFrom":makeQuery(id+"F7.opExtrude","SWEPT_BODY",BODY,{"disambiguationData":[OSD([sQuery(id+"F0.wireOp",EDGE,"E118")])]})});
            var Q73;
            Q73=makeQuery(id+"F7.*.split.splitOp","SPLIT",BODY,{"derivedFrom":makeQuery(id+"F7.opExtrude","SWEPT_BODY",BODY,{"disambiguationData":[OSD([sQuery(id+"F0.wireOp",EDGE,"E110")])]})});
            var Q74;
            Q74=makeQuery(id+"F7.*.split.splitOp","SPLIT",BODY,{"derivedFrom":makeQuery(id+"F7.opExtrude","SWEPT_BODY",BODY,{"disambiguationData":[OSD([sQuery(id+"F0.wireOp",EDGE,"E104")])]})});
            var Q75;
            Q75=makeQuery(id+"F7.*.split.splitOp","SPLIT",BODY,{"derivedFrom":makeQuery(id+"F7.opExtrude","SWEPT_BODY",BODY,{"disambiguationData":[OSD([sQuery(id+"F0.wireOp",EDGE,"E86")])]})});
            var Q76;
            Q76=makeQuery(id+"F7.*.split.splitOp","SPLIT",BODY,{"derivedFrom":makeQuery(id+"F7.opExtrude","SWEPT_BODY",BODY,{"disambiguationData":[OSD([sQuery(id+"F0.wireOp",EDGE,"E85")])]})});
            var Q77;
            Q77=makeQuery(id+"F7.*.split.splitOp","SPLIT",BODY,{"derivedFrom":makeQuery(id+"F7.opExtrude","SWEPT_BODY",BODY,{"disambiguationData":[OSD([sQuery(id+"F0.wireOp",EDGE,"E45")])]})});
            var Q78;
            Q78=makeQuery(id+"F7.*.split.splitOp","SPLIT",BODY,{"derivedFrom":makeQuery(id+"F7.opExtrude","SWEPT_BODY",BODY,{"disambiguationData":[OSD([sQuery(id+"F0.wireOp",EDGE,"E44")])]})});
            var Q79;
            Q79=makeQuery(id+"F7.*.split.splitOp","SPLIT",BODY,{"derivedFrom":makeQuery(id+"F7.opExtrude","SWEPT_BODY",BODY,{"disambiguationData":[OSD([sQuery(id+"F0.wireOp",EDGE,"E42")])]})});
            var Q80;
            Q80=makeQuery(id+"F7.*.split.splitOp","SPLIT",BODY,{"derivedFrom":makeQuery(id+"F7.opExtrude","SWEPT_BODY",BODY,{"disambiguationData":[OSD([sQuery(id+"F0.wireOp",EDGE,"E43")])]})});
            var Q81;
            Q81=makeQuery(id+"F7.*.split.splitOp","SPLIT",BODY,{"derivedFrom":makeQuery(id+"F7.opExtrude","SWEPT_BODY",BODY,{"disambiguationData":[OSD([sQuery(id+"F0.wireOp",EDGE,"E46")])]})});
            var Q82;
            Q82=makeQuery(id+"F7.*.split.splitOp","SPLIT",BODY,{"derivedFrom":makeQuery(id+"F7.opExtrude","SWEPT_BODY",BODY,{"disambiguationData":[OSD([sQuery(id+"F0.wireOp",EDGE,"E47")])]})});
            var Q83;
            Q83=makeQuery(id+"F7.*.split.splitOp","SPLIT",BODY,{"derivedFrom":makeQuery(id+"F7.opExtrude","SWEPT_BODY",BODY,{"disambiguationData":[OSD([sQuery(id+"F0.wireOp",EDGE,"E84")])]})});
            var Q84;
            Q84=makeQuery(id+"F7.*.split.splitOp","SPLIT",BODY,{"derivedFrom":makeQuery(id+"F7.opExtrude","SWEPT_BODY",BODY,{"disambiguationData":[OSD([sQuery(id+"F0.wireOp",EDGE,"E87")])]})});
            var Q85;
            Q85=makeQuery(id+"F7.*.split.splitOp","SPLIT",BODY,{"derivedFrom":makeQuery(id+"F7.opExtrude","SWEPT_BODY",BODY,{"disambiguationData":[OSD([sQuery(id+"F0.wireOp",EDGE,"E105")])]})});
            var Q86;
            Q86=makeQuery(id+"F7.*.split.splitOp","SPLIT",BODY,{"derivedFrom":makeQuery(id+"F7.opExtrude","SWEPT_BODY",BODY,{"disambiguationData":[OSD([sQuery(id+"F0.wireOp",EDGE,"E106")])]})});
            var Q87;
            Q87=makeQuery(id+"F7.*.split.splitOp","SPLIT",BODY,{"derivedFrom":makeQuery(id+"F7.opExtrude","SWEPT_BODY",BODY,{"disambiguationData":[OSD([sQuery(id+"F0.wireOp",EDGE,"E119")])]})});
            var Q88;
            Q88=makeQuery(id+"F7.*.split.splitOp","SPLIT",BODY,{"derivedFrom":makeQuery(id+"F7.opExtrude","SWEPT_BODY",BODY,{"disambiguationData":[OSD([sQuery(id+"F0.wireOp",EDGE,"E138")])]})});
            var Q89;
            Q89=makeQuery(id+"F7.*.split.splitOp","SPLIT",BODY,{"derivedFrom":makeQuery(id+"F7.opExtrude","SWEPT_BODY",BODY,{"disambiguationData":[OSD([sQuery(id+"F0.wireOp",EDGE,"E139")])]})});
            var Q90;
            Q90=makeQuery(id+"F3.opExtrude","SWEPT_BODY",BODY,{"disambiguationData":[OSD([sQuery(id+"F1.wireOp",EDGE,"E199")])]});
            var Q91;
            Q91=makeQuery(id+"F3.opExtrude","SWEPT_BODY",BODY,{"disambiguationData":[OSD([sQuery(id+"F1.wireOp",EDGE,"E206.0.1.0")])]});
            var Q92;
            Q92=makeQuery(id+"F3.opExtrude","SWEPT_BODY",BODY,{"disambiguationData":[OSD([sQuery(id+"F1.wireOp",EDGE,"E206.0.2.0")])]});
            var Q93;
            Q93=makeQuery(id+"F3.opExtrude","SWEPT_BODY",BODY,{"disambiguationData":[OSD([sQuery(id+"F1.wireOp",EDGE,"E206.0.3.0")])]});
            var Q94;
            Q94=makeQuery(id+"F3.opExtrude","SWEPT_BODY",BODY,{"disambiguationData":[OSD([sQuery(id+"F1.wireOp",EDGE,"E206.0.4.0")])]});
            var Q95;
            Q95=makeQuery(id+"F3.opExtrude","SWEPT_BODY",BODY,{"disambiguationData":[OSD([sQuery(id+"F1.wireOp",EDGE,"E206.0.5.0")])]});
            var Q96;
            Q96=makeQuery(id+"F3.opExtrude","SWEPT_BODY",BODY,{"disambiguationData":[OSD([sQuery(id+"F1.wireOp",EDGE,"E206.0.6.0")])]});
            var Q97;
            Q97=makeQuery(id+"F3.opExtrude","SWEPT_BODY",BODY,{"disambiguationData":[OSD([sQuery(id+"F1.wireOp",EDGE,"E206.0.7.0")])]});
            var Q98;
            Q98=makeQuery(id+"F3.opExtrude","SWEPT_BODY",BODY,{"disambiguationData":[OSD([sQuery(id+"F1.wireOp",EDGE,"E206.0.8.0")])]});
            var Q99;
            Q99=makeQuery(id+"F3.opExtrude","SWEPT_BODY",BODY,{"disambiguationData":[OSD([sQuery(id+"F1.wireOp",EDGE,"E206.1.0.0")])]});
            var Q100;
            Q100=makeQuery(id+"F3.opExtrude","SWEPT_BODY",BODY,{"disambiguationData":[OSD([sQuery(id+"F1.wireOp",EDGE,"E206.1.1.0")])]});
            var Q101;
            Q101=makeQuery(id+"F3.opExtrude","SWEPT_BODY",BODY,{"disambiguationData":[OSD([sQuery(id+"F1.wireOp",EDGE,"E206.1.2.0")])]});
            var Q102;
            Q102=makeQuery(id+"F3.opExtrude","SWEPT_BODY",BODY,{"disambiguationData":[OSD([sQuery(id+"F1.wireOp",EDGE,"E206.1.3.0")])]});
            var Q103;
            Q103=makeQuery(id+"F3.opExtrude","SWEPT_BODY",BODY,{"disambiguationData":[OSD([sQuery(id+"F1.wireOp",EDGE,"E206.1.4.0")])]});
            var Q104;
            Q104=makeQuery(id+"F3.opExtrude","SWEPT_BODY",BODY,{"disambiguationData":[OSD([sQuery(id+"F1.wireOp",EDGE,"E206.1.5.0")])]});
            var Q105;
            Q105=makeQuery(id+"F3.opExtrude","SWEPT_BODY",BODY,{"disambiguationData":[OSD([sQuery(id+"F1.wireOp",EDGE,"E206.1.6.0")])]});
            var Q106;
            Q106=makeQuery(id+"F3.opExtrude","SWEPT_BODY",BODY,{"disambiguationData":[OSD([sQuery(id+"F1.wireOp",EDGE,"E206.1.7.0")])]});
            var Q107;
            Q107=makeQuery(id+"F3.opExtrude","SWEPT_BODY",BODY,{"disambiguationData":[OSD([sQuery(id+"F1.wireOp",EDGE,"E206.1.8.0")])]});
            var Q108;
            Q108=makeQuery(id+"F3.opExtrude","SWEPT_BODY",BODY,{"disambiguationData":[OSD([sQuery(id+"F1.wireOp",EDGE,"E206.2.0.0")])]});
            var Q109;
            Q109=makeQuery(id+"F3.opExtrude","SWEPT_BODY",BODY,{"disambiguationData":[OSD([sQuery(id+"F1.wireOp",EDGE,"E206.2.1.0")])]});
            var Q110;
            Q110=makeQuery(id+"F3.opExtrude","SWEPT_BODY",BODY,{"disambiguationData":[OSD([sQuery(id+"F1.wireOp",EDGE,"E206.2.2.0")])]});
            var Q111;
            Q111=makeQuery(id+"F3.opExtrude","SWEPT_BODY",BODY,{"disambiguationData":[OSD([sQuery(id+"F1.wireOp",EDGE,"E206.2.3.0")])]});
            var Q112;
            Q112=makeQuery(id+"F3.opExtrude","SWEPT_BODY",BODY,{"disambiguationData":[OSD([sQuery(id+"F1.wireOp",EDGE,"E206.2.4.0")])]});
            var Q113;
            Q113=makeQuery(id+"F3.opExtrude","SWEPT_BODY",BODY,{"disambiguationData":[OSD([sQuery(id+"F1.wireOp",EDGE,"E206.2.5.0")])]});
            var Q114;
            Q114=makeQuery(id+"F3.opExtrude","SWEPT_BODY",BODY,{"disambiguationData":[OSD([sQuery(id+"F1.wireOp",EDGE,"E206.2.6.0")])]});
            var Q115;
            Q115=makeQuery(id+"F3.opExtrude","SWEPT_BODY",BODY,{"disambiguationData":[OSD([sQuery(id+"F1.wireOp",EDGE,"E206.2.7.0")])]});
            var Q116;
            Q116=makeQuery(id+"F3.opExtrude","SWEPT_BODY",BODY,{"disambiguationData":[OSD([sQuery(id+"F1.wireOp",EDGE,"E206.2.8.0")])]});
            var Q117;
            Q117=makeQuery(id+"F3.opExtrude","SWEPT_BODY",BODY,{"disambiguationData":[OSD([sQuery(id+"F1.wireOp",EDGE,"E206.3.8.0")])]});
            var Q118;
            Q118=makeQuery(id+"F3.opExtrude","SWEPT_BODY",BODY,{"disambiguationData":[OSD([sQuery(id+"F1.wireOp",EDGE,"E206.3.7.0")])]});
            var Q119;
            Q119=makeQuery(id+"F3.opExtrude","SWEPT_BODY",BODY,{"disambiguationData":[OSD([sQuery(id+"F1.wireOp",EDGE,"E206.3.6.0")])]});
            var Q120;
            Q120=makeQuery(id+"F3.opExtrude","SWEPT_BODY",BODY,{"disambiguationData":[OSD([sQuery(id+"F1.wireOp",EDGE,"E206.3.5.0")])]});
            var Q121;
            Q121=makeQuery(id+"F3.opExtrude","SWEPT_BODY",BODY,{"disambiguationData":[OSD([sQuery(id+"F1.wireOp",EDGE,"E206.3.4.0")])]});
            var Q122;
            Q122=makeQuery(id+"F3.opExtrude","SWEPT_BODY",BODY,{"disambiguationData":[OSD([sQuery(id+"F1.wireOp",EDGE,"E206.3.3.0")])]});
            var Q123;
            Q123=makeQuery(id+"F3.opExtrude","SWEPT_BODY",BODY,{"disambiguationData":[OSD([sQuery(id+"F1.wireOp",EDGE,"E206.3.2.0")])]});
            var Q124;
            Q124=makeQuery(id+"F3.opExtrude","SWEPT_BODY",BODY,{"disambiguationData":[OSD([sQuery(id+"F1.wireOp",EDGE,"E206.3.1.0")])]});
            var Q125;
            Q125=makeQuery(id+"F3.opExtrude","SWEPT_BODY",BODY,{"disambiguationData":[OSD([sQuery(id+"F1.wireOp",EDGE,"E206.3.0.0")])]});
            var Q126;
            Q126=makeQuery(id+"F3.opExtrude","SWEPT_BODY",BODY,{"disambiguationData":[OSD([sQuery(id+"F1.wireOp",EDGE,"E206.4.0.0")])]});
            var Q127;
            Q127=makeQuery(id+"F3.opExtrude","SWEPT_BODY",BODY,{"disambiguationData":[OSD([sQuery(id+"F1.wireOp",EDGE,"E206.4.1.0")])]});
            var Q128;
            Q128=makeQuery(id+"F3.opExtrude","SWEPT_BODY",BODY,{"disambiguationData":[OSD([sQuery(id+"F1.wireOp",EDGE,"E206.4.2.0")])]});
            var Q129;
            Q129=makeQuery(id+"F3.opExtrude","SWEPT_BODY",BODY,{"disambiguationData":[OSD([sQuery(id+"F1.wireOp",EDGE,"E206.4.3.0")])]});
            var Q130;
            Q130=makeQuery(id+"F3.opExtrude","SWEPT_BODY",BODY,{"disambiguationData":[OSD([sQuery(id+"F1.wireOp",EDGE,"E206.4.4.0")])]});
            var Q131;
            Q131=makeQuery(id+"F3.opExtrude","SWEPT_BODY",BODY,{"disambiguationData":[OSD([sQuery(id+"F1.wireOp",EDGE,"E206.4.5.0")])]});
            var Q132;
            Q132=makeQuery(id+"F3.opExtrude","SWEPT_BODY",BODY,{"disambiguationData":[OSD([sQuery(id+"F1.wireOp",EDGE,"E206.4.6.0")])]});
            var Q133;
            Q133=makeQuery(id+"F3.opExtrude","SWEPT_BODY",BODY,{"disambiguationData":[OSD([sQuery(id+"F1.wireOp",EDGE,"E206.4.7.0")])]});
            var Q134;
            Q134=makeQuery(id+"F3.opExtrude","SWEPT_BODY",BODY,{"disambiguationData":[OSD([sQuery(id+"F1.wireOp",EDGE,"E206.4.8.0")])]});
            var Q135;
            Q135=makeQuery(id+"F3.opExtrude","SWEPT_BODY",BODY,{"disambiguationData":[OSD([sQuery(id+"F1.wireOp",EDGE,"E206.5.8.0")])]});
            var Q136;
            Q136=makeQuery(id+"F3.opExtrude","SWEPT_BODY",BODY,{"disambiguationData":[OSD([sQuery(id+"F1.wireOp",EDGE,"E206.5.7.0")])]});
            var Q137;
            Q137=makeQuery(id+"F3.opExtrude","SWEPT_BODY",BODY,{"disambiguationData":[OSD([sQuery(id+"F1.wireOp",EDGE,"E206.5.6.0")])]});
            var Q138;
            Q138=makeQuery(id+"F3.opExtrude","SWEPT_BODY",BODY,{"disambiguationData":[OSD([sQuery(id+"F1.wireOp",EDGE,"E206.5.5.0")])]});
            var Q139;
            Q139=makeQuery(id+"F3.opExtrude","SWEPT_BODY",BODY,{"disambiguationData":[OSD([sQuery(id+"F1.wireOp",EDGE,"E206.5.4.0")])]});
            var Q140;
            Q140=makeQuery(id+"F3.opExtrude","SWEPT_BODY",BODY,{"disambiguationData":[OSD([sQuery(id+"F1.wireOp",EDGE,"E206.5.3.0")])]});
            var Q141;
            Q141=makeQuery(id+"F3.opExtrude","SWEPT_BODY",BODY,{"disambiguationData":[OSD([sQuery(id+"F1.wireOp",EDGE,"E206.5.2.0")])]});
            var Q142;
            Q142=makeQuery(id+"F3.opExtrude","SWEPT_BODY",BODY,{"disambiguationData":[OSD([sQuery(id+"F1.wireOp",EDGE,"E206.5.1.0")])]});
            var Q143;
            Q143=makeQuery(id+"F3.opExtrude","SWEPT_BODY",BODY,{"disambiguationData":[OSD([sQuery(id+"F1.wireOp",EDGE,"E206.5.0.0")])]});
            var Q144;
            Q144=makeQuery(id+"F3.opExtrude","SWEPT_BODY",BODY,{"disambiguationData":[OSD([sQuery(id+"F1.wireOp",EDGE,"E206.6.0.0")])]});
            var Q145;
            Q145=makeQuery(id+"F3.opExtrude","SWEPT_BODY",BODY,{"disambiguationData":[OSD([sQuery(id+"F1.wireOp",EDGE,"E206.6.1.0")])]});
            var Q146;
            Q146=makeQuery(id+"F3.opExtrude","SWEPT_BODY",BODY,{"disambiguationData":[OSD([sQuery(id+"F1.wireOp",EDGE,"E206.6.2.0")])]});
            var Q147;
            Q147=makeQuery(id+"F3.opExtrude","SWEPT_BODY",BODY,{"disambiguationData":[OSD([sQuery(id+"F1.wireOp",EDGE,"E206.6.3.0")])]});
            var Q148;
            Q148=makeQuery(id+"F3.opExtrude","SWEPT_BODY",BODY,{"disambiguationData":[OSD([sQuery(id+"F1.wireOp",EDGE,"E206.6.4.0")])]});
            var Q149;
            Q149=makeQuery(id+"F3.opExtrude","SWEPT_BODY",BODY,{"disambiguationData":[OSD([sQuery(id+"F1.wireOp",EDGE,"E206.6.7.0")])]});
            var Q150;
            Q150=makeQuery(id+"F3.opExtrude","SWEPT_BODY",BODY,{"disambiguationData":[OSD([sQuery(id+"F1.wireOp",EDGE,"E206.6.8.0")])]});
            var Q151;
            Q151=makeQuery(id+"F3.opExtrude","SWEPT_BODY",BODY,{"disambiguationData":[OSD([sQuery(id+"F1.wireOp",EDGE,"E206.7.8.0")])]});
            var Q152;
            Q152=makeQuery(id+"F3.opExtrude","SWEPT_BODY",BODY,{"disambiguationData":[OSD([sQuery(id+"F1.wireOp",EDGE,"E206.7.7.0")])]});
            var Q153;
            Q153=makeQuery(id+"F3.opExtrude","SWEPT_BODY",BODY,{"disambiguationData":[OSD([sQuery(id+"F1.wireOp",EDGE,"E206.6.6.0")])]});
            var Q154;
            Q154=makeQuery(id+"F3.opExtrude","SWEPT_BODY",BODY,{"disambiguationData":[OSD([sQuery(id+"F1.wireOp",EDGE,"E206.6.5.0")])]});
            var Q155;
            Q155=makeQuery(id+"F3.opExtrude","SWEPT_BODY",BODY,{"disambiguationData":[OSD([sQuery(id+"F1.wireOp",EDGE,"E206.7.6.0")])]});
            var Q156;
            Q156=makeQuery(id+"F3.opExtrude","SWEPT_BODY",BODY,{"disambiguationData":[OSD([sQuery(id+"F1.wireOp",EDGE,"E206.7.5.0")])]});
            var Q157;
            Q157=makeQuery(id+"F3.opExtrude","SWEPT_BODY",BODY,{"disambiguationData":[OSD([sQuery(id+"F1.wireOp",EDGE,"E206.7.4.0")])]});
            var Q158;
            Q158=makeQuery(id+"F3.opExtrude","SWEPT_BODY",BODY,{"disambiguationData":[OSD([sQuery(id+"F1.wireOp",EDGE,"E206.7.3.0")])]});
            var Q159;
            Q159=makeQuery(id+"F3.opExtrude","SWEPT_BODY",BODY,{"disambiguationData":[OSD([sQuery(id+"F1.wireOp",EDGE,"E206.7.2.0")])]});
            var Q160;
            Q160=makeQuery(id+"F3.opExtrude","SWEPT_BODY",BODY,{"disambiguationData":[OSD([sQuery(id+"F1.wireOp",EDGE,"E206.7.1.0")])]});
            var Q161;
            Q161=makeQuery(id+"F3.opExtrude","SWEPT_BODY",BODY,{"disambiguationData":[OSD([sQuery(id+"F1.wireOp",EDGE,"E206.7.0.0")])]});
            var Q162;
            Q162=makeQuery(id+"F3.opExtrude","SWEPT_BODY",BODY,{"disambiguationData":[OSD([sQuery(id+"F1.wireOp",EDGE,"E206.8.8.0")])]});
            var Q163;
            Q163=makeQuery(id+"F3.opExtrude","SWEPT_BODY",BODY,{"disambiguationData":[OSD([sQuery(id+"F1.wireOp",EDGE,"E206.8.7.0")])]});
            var Q164;
            Q164=makeQuery(id+"F3.opExtrude","SWEPT_BODY",BODY,{"disambiguationData":[OSD([sQuery(id+"F1.wireOp",EDGE,"E206.8.6.0")])]});
            var Q165;
            Q165=makeQuery(id+"F3.opExtrude","SWEPT_BODY",BODY,{"disambiguationData":[OSD([sQuery(id+"F1.wireOp",EDGE,"E206.8.5.0")])]});
            var Q166;
            Q166=makeQuery(id+"F3.opExtrude","SWEPT_BODY",BODY,{"disambiguationData":[OSD([sQuery(id+"F1.wireOp",EDGE,"E206.8.4.0")])]});
            var Q167;
            Q167=makeQuery(id+"F3.opExtrude","SWEPT_BODY",BODY,{"disambiguationData":[OSD([sQuery(id+"F1.wireOp",EDGE,"E206.8.3.0")])]});
            var Q168;
            Q168=makeQuery(id+"F3.opExtrude","SWEPT_BODY",BODY,{"disambiguationData":[OSD([sQuery(id+"F1.wireOp",EDGE,"E206.8.2.0")])]});
            var Q169;
            Q169=makeQuery(id+"F3.opExtrude","SWEPT_BODY",BODY,{"disambiguationData":[OSD([sQuery(id+"F1.wireOp",EDGE,"E206.8.1.0")])]});
            var Q170;
            Q170=makeQuery(id+"F3.opExtrude","SWEPT_BODY",BODY,{"disambiguationData":[OSD([sQuery(id+"F1.wireOp",EDGE,"E206.8.0.0")])]});
            booleanBodies(context, id + "F8", {"operationType" : BooleanOperationType.SUBTRACTION, "tools" : qUnion([Q0, Q1, Q2, Q3, Q4, Q5, Q6, Q7, Q8, Q9, Q10, Q11, Q12, Q13, Q14, Q15, Q16, Q17, Q18, Q19, Q20, Q21, Q22, Q23, Q24, Q25, Q26, Q27, Q28, Q29, Q30, Q31, Q32, Q33, Q34, Q35, Q36, Q37, Q38, Q39, Q40, Q41, Q42, Q43, Q44, Q45, Q46, Q47, Q48, Q49, Q50, Q51, Q52, Q53, Q54, Q55, Q56, Q57, Q58, Q59, Q60, Q61, Q62, Q63, Q64, Q65, Q66, Q67, Q68, Q69, Q70, Q71, Q72, Q73, Q74, Q75, Q76, Q77, Q78, Q79, Q80, Q81, Q82, Q83, Q84, Q85, Q86, Q87, Q88, Q89]), "targets" : qUnion([Q90, Q91, Q92, Q93, Q94, Q95, Q96, Q97, Q98, Q99, Q100, Q101, Q102, Q103, Q104, Q105, Q106, Q107, Q108, Q109, Q110, Q111, Q112, Q113, Q114, Q115, Q116, Q117, Q118, Q119, Q120, Q121, Q122, Q123, Q124, Q125, Q126, Q127, Q128, Q129, Q130, Q131, Q132, Q133, Q134, Q135, Q136, Q137, Q138, Q139, Q140, Q141, Q142, Q143, Q144, Q145, Q146, Q147, Q148, Q149, Q150, Q151, Q152, Q153, Q154, Q155, Q156, Q157, Q158, Q159, Q160, Q161, Q162, Q163, Q164, Q165, Q166, Q167, Q168, Q169, Q170])});
        }
        {
            var Q0;
            Q0=makeQuery(id+"F0.imprint","IMPRINT",FACE,{"disambiguationData":[TD([[makeQuery(id+"F0.imprint","IMPRINT",EDGE,{"derivedFrom":sQuery(id+"F0.wireOp",EDGE,"E178")}),1.0]])]});
            var Q1;
            Q1=makeQuery(id+"F0.imprint","IMPRINT",FACE,{"disambiguationData":[TD([[makeQuery(id+"F0.imprint","IMPRINT",EDGE,{"derivedFrom":sQuery(id+"F0.wireOp",EDGE,"E179")}),1.0]])]});
            var Q2;
            Q2=makeQuery(id+"F0.imprint","IMPRINT",FACE,{"disambiguationData":[TD([[makeQuery(id+"F0.imprint","IMPRINT",EDGE,{"derivedFrom":sQuery(id+"F0.wireOp",EDGE,"E180")}),1.0]])]});
            var Q3;
            Q3=makeQuery(id+"F0.imprint","IMPRINT",FACE,{"disambiguationData":[TD([[makeQuery(id+"F0.imprint","IMPRINT",EDGE,{"derivedFrom":sQuery(id+"F0.wireOp",EDGE,"E181")}),1.0]])]});
            var Q4;
            Q4=makeQuery(id+"F0.imprint","IMPRINT",FACE,{"disambiguationData":[TD([[makeQuery(id+"F0.imprint","IMPRINT",EDGE,{"derivedFrom":sQuery(id+"F0.wireOp",EDGE,"E182")}),1.0]])]});
            var Q5;
            Q5=makeQuery(id+"F0.imprint","IMPRINT",FACE,{"disambiguationData":[TD([[makeQuery(id+"F0.imprint","IMPRINT",EDGE,{"derivedFrom":sQuery(id+"F0.wireOp",EDGE,"E183")}),1.0]])]});
            var Q6;
            Q6=makeQuery(id+"F0.imprint","IMPRINT",FACE,{"disambiguationData":[TD([[makeQuery(id+"F0.imprint","IMPRINT",EDGE,{"derivedFrom":sQuery(id+"F0.wireOp",EDGE,"E184")}),1.0]])]});
            var Q7;
            Q7=makeQuery(id+"F0.imprint","IMPRINT",FACE,{"disambiguationData":[TD([[makeQuery(id+"F0.imprint","IMPRINT",EDGE,{"derivedFrom":sQuery(id+"F0.wireOp",EDGE,"E185")}),1.0]])]});
            var Q8;
            Q8=makeQuery(id+"F0.imprint","IMPRINT",FACE,{"disambiguationData":[TD([[makeQuery(id+"F0.imprint","IMPRINT",EDGE,{"derivedFrom":sQuery(id+"F0.wireOp",EDGE,"E186")}),1.0]])]});
            var Q9;
            Q9=makeQuery(id+"F0.imprint","IMPRINT",FACE,{"disambiguationData":[TD([[makeQuery(id+"F0.imprint","IMPRINT",EDGE,{"derivedFrom":sQuery(id+"F0.wireOp",EDGE,"E169")}),1.0]])]});
            var Q10;
            Q10=makeQuery(id+"F0.imprint","IMPRINT",FACE,{"disambiguationData":[TD([[makeQuery(id+"F0.imprint","IMPRINT",EDGE,{"derivedFrom":sQuery(id+"F0.wireOp",EDGE,"E170")}),1.0]])]});
            var Q11;
            Q11=makeQuery(id+"F0.imprint","IMPRINT",FACE,{"disambiguationData":[TD([[makeQuery(id+"F0.imprint","IMPRINT",EDGE,{"derivedFrom":sQuery(id+"F0.wireOp",EDGE,"E171")}),1.0]])]});
            var Q12;
            Q12=makeQuery(id+"F0.imprint","IMPRINT",FACE,{"disambiguationData":[TD([[makeQuery(id+"F0.imprint","IMPRINT",EDGE,{"derivedFrom":sQuery(id+"F0.wireOp",EDGE,"E172")}),1.0]])]});
            var Q13;
            Q13=makeQuery(id+"F0.imprint","IMPRINT",FACE,{"disambiguationData":[TD([[makeQuery(id+"F0.imprint","IMPRINT",EDGE,{"derivedFrom":sQuery(id+"F0.wireOp",EDGE,"E173")}),1.0]])]});
            var Q14;
            Q14=makeQuery(id+"F0.imprint","IMPRINT",FACE,{"disambiguationData":[TD([[makeQuery(id+"F0.imprint","IMPRINT",EDGE,{"derivedFrom":sQuery(id+"F0.wireOp",EDGE,"E174")}),1.0]])]});
            var Q15;
            Q15=makeQuery(id+"F0.imprint","IMPRINT",FACE,{"disambiguationData":[TD([[makeQuery(id+"F0.imprint","IMPRINT",EDGE,{"derivedFrom":sQuery(id+"F0.wireOp",EDGE,"E175")}),1.0]])]});
            var Q16;
            Q16=makeQuery(id+"F0.imprint","IMPRINT",FACE,{"disambiguationData":[TD([[makeQuery(id+"F0.imprint","IMPRINT",EDGE,{"derivedFrom":sQuery(id+"F0.wireOp",EDGE,"E176")}),1.0]])]});
            var Q17;
            Q17=makeQuery(id+"F0.imprint","IMPRINT",FACE,{"disambiguationData":[TD([[makeQuery(id+"F0.imprint","IMPRINT",EDGE,{"derivedFrom":sQuery(id+"F0.wireOp",EDGE,"E177")}),1.0]])]});
            var Q18;
            Q18=makeQuery(id+"F0.imprint","IMPRINT",FACE,{"disambiguationData":[TD([[makeQuery(id+"F0.imprint","IMPRINT",EDGE,{"derivedFrom":sQuery(id+"F0.wireOp",EDGE,"E160")}),1.0]])]});
            var Q19;
            Q19=makeQuery(id+"F0.imprint","IMPRINT",FACE,{"disambiguationData":[TD([[makeQuery(id+"F0.imprint","IMPRINT",EDGE,{"derivedFrom":sQuery(id+"F0.wireOp",EDGE,"E161")}),1.0]])]});
            var Q20;
            Q20=makeQuery(id+"F0.imprint","IMPRINT",FACE,{"disambiguationData":[TD([[makeQuery(id+"F0.imprint","IMPRINT",EDGE,{"derivedFrom":sQuery(id+"F0.wireOp",EDGE,"E162")}),1.0]])]});
            var Q21;
            Q21=makeQuery(id+"F0.imprint","IMPRINT",FACE,{"disambiguationData":[TD([[makeQuery(id+"F0.imprint","IMPRINT",EDGE,{"derivedFrom":sQuery(id+"F0.wireOp",EDGE,"E163")}),1.0]])]});
            var Q22;
            Q22=makeQuery(id+"F0.imprint","IMPRINT",FACE,{"disambiguationData":[TD([[makeQuery(id+"F0.imprint","IMPRINT",EDGE,{"derivedFrom":sQuery(id+"F0.wireOp",EDGE,"E164")}),1.0]])]});
            var Q23;
            Q23=makeQuery(id+"F0.imprint","IMPRINT",FACE,{"disambiguationData":[TD([[makeQuery(id+"F0.imprint","IMPRINT",EDGE,{"derivedFrom":sQuery(id+"F0.wireOp",EDGE,"E165")}),1.0]])]});
            var Q24;
            Q24=makeQuery(id+"F0.imprint","IMPRINT",FACE,{"disambiguationData":[TD([[makeQuery(id+"F0.imprint","IMPRINT",EDGE,{"derivedFrom":sQuery(id+"F0.wireOp",EDGE,"E166")}),1.0]])]});
            var Q25;
            Q25=makeQuery(id+"F0.imprint","IMPRINT",FACE,{"disambiguationData":[TD([[makeQuery(id+"F0.imprint","IMPRINT",EDGE,{"derivedFrom":sQuery(id+"F0.wireOp",EDGE,"E167")}),1.0]])]});
            var Q26;
            Q26=makeQuery(id+"F0.imprint","IMPRINT",FACE,{"disambiguationData":[TD([[makeQuery(id+"F0.imprint","IMPRINT",EDGE,{"derivedFrom":sQuery(id+"F0.wireOp",EDGE,"E168")}),1.0]])]});
            var Q27;
            Q27=makeQuery(id+"F0.imprint","IMPRINT",FACE,{"disambiguationData":[TD([[makeQuery(id+"F0.imprint","IMPRINT",EDGE,{"derivedFrom":sQuery(id+"F0.wireOp",EDGE,"E159")}),1.0]])]});
            var Q28;
            Q28=makeQuery(id+"F0.imprint","IMPRINT",FACE,{"disambiguationData":[TD([[makeQuery(id+"F0.imprint","IMPRINT",EDGE,{"derivedFrom":sQuery(id+"F0.wireOp",EDGE,"E158")}),1.0]])]});
            var Q29;
            Q29=makeQuery(id+"F0.imprint","IMPRINT",FACE,{"disambiguationData":[TD([[makeQuery(id+"F0.imprint","IMPRINT",EDGE,{"derivedFrom":sQuery(id+"F0.wireOp",EDGE,"E157")}),1.0]])]});
            var Q30;
            Q30=makeQuery(id+"F0.imprint","IMPRINT",FACE,{"disambiguationData":[TD([[makeQuery(id+"F0.imprint","IMPRINT",EDGE,{"derivedFrom":sQuery(id+"F0.wireOp",EDGE,"E156")}),1.0]])]});
            var Q31;
            Q31=makeQuery(id+"F0.imprint","IMPRINT",FACE,{"disambiguationData":[TD([[makeQuery(id+"F0.imprint","IMPRINT",EDGE,{"derivedFrom":sQuery(id+"F0.wireOp",EDGE,"E155")}),1.0]])]});
            var Q32;
            Q32=makeQuery(id+"F0.imprint","IMPRINT",FACE,{"disambiguationData":[TD([[makeQuery(id+"F0.imprint","IMPRINT",EDGE,{"derivedFrom":sQuery(id+"F0.wireOp",EDGE,"E154")}),1.0]])]});
            var Q33;
            Q33=makeQuery(id+"F0.imprint","IMPRINT",FACE,{"disambiguationData":[TD([[makeQuery(id+"F0.imprint","IMPRINT",EDGE,{"derivedFrom":sQuery(id+"F0.wireOp",EDGE,"E153")}),1.0]])]});
            var Q34;
            Q34=makeQuery(id+"F0.imprint","IMPRINT",FACE,{"disambiguationData":[TD([[makeQuery(id+"F0.imprint","IMPRINT",EDGE,{"derivedFrom":sQuery(id+"F0.wireOp",EDGE,"E152")}),1.0]])]});
            var Q35;
            Q35=makeQuery(id+"F0.imprint","IMPRINT",FACE,{"disambiguationData":[TD([[makeQuery(id+"F0.imprint","IMPRINT",EDGE,{"derivedFrom":sQuery(id+"F0.wireOp",EDGE,"E151")}),1.0]])]});
            var Q36;
            Q36=makeQuery(id+"F0.imprint","IMPRINT",FACE,{"disambiguationData":[TD([[makeQuery(id+"F0.imprint","IMPRINT",EDGE,{"derivedFrom":sQuery(id+"F0.wireOp",EDGE,"E142")}),1.0]])]});
            var Q37;
            Q37=makeQuery(id+"F0.imprint","IMPRINT",FACE,{"disambiguationData":[TD([[makeQuery(id+"F0.imprint","IMPRINT",EDGE,{"derivedFrom":sQuery(id+"F0.wireOp",EDGE,"E143")}),1.0]])]});
            var Q38;
            Q38=makeQuery(id+"F0.imprint","IMPRINT",FACE,{"disambiguationData":[TD([[makeQuery(id+"F0.imprint","IMPRINT",EDGE,{"derivedFrom":sQuery(id+"F0.wireOp",EDGE,"E144")}),1.0]])]});
            var Q39;
            Q39=makeQuery(id+"F0.imprint","IMPRINT",FACE,{"disambiguationData":[TD([[makeQuery(id+"F0.imprint","IMPRINT",EDGE,{"derivedFrom":sQuery(id+"F0.wireOp",EDGE,"E145")}),1.0]])]});
            var Q40;
            Q40=makeQuery(id+"F0.imprint","IMPRINT",FACE,{"disambiguationData":[TD([[makeQuery(id+"F0.imprint","IMPRINT",EDGE,{"derivedFrom":sQuery(id+"F0.wireOp",EDGE,"E146")}),1.0]])]});
            var Q41;
            Q41=makeQuery(id+"F0.imprint","IMPRINT",FACE,{"disambiguationData":[TD([[makeQuery(id+"F0.imprint","IMPRINT",EDGE,{"derivedFrom":sQuery(id+"F0.wireOp",EDGE,"E147")}),1.0]])]});
            var Q42;
            Q42=makeQuery(id+"F0.imprint","IMPRINT",FACE,{"disambiguationData":[TD([[makeQuery(id+"F0.imprint","IMPRINT",EDGE,{"derivedFrom":sQuery(id+"F0.wireOp",EDGE,"E148")}),1.0]])]});
            var Q43;
            Q43=makeQuery(id+"F0.imprint","IMPRINT",FACE,{"disambiguationData":[TD([[makeQuery(id+"F0.imprint","IMPRINT",EDGE,{"derivedFrom":sQuery(id+"F0.wireOp",EDGE,"E149")}),1.0]])]});
            var Q44;
            Q44=makeQuery(id+"F0.imprint","IMPRINT",FACE,{"disambiguationData":[TD([[makeQuery(id+"F0.imprint","IMPRINT",EDGE,{"derivedFrom":sQuery(id+"F0.wireOp",EDGE,"E150")}),1.0]])]});
            var Q45;
            Q45=makeQuery(id+"F0.imprint","IMPRINT",FACE,{"disambiguationData":[TD([[makeQuery(id+"F0.imprint","IMPRINT",EDGE,{"derivedFrom":sQuery(id+"F0.wireOp",EDGE,"E88")}),1.0]])]});
            var Q46;
            Q46=makeQuery(id+"F0.imprint","IMPRINT",FACE,{"disambiguationData":[TD([[makeQuery(id+"F0.imprint","IMPRINT",EDGE,{"derivedFrom":sQuery(id+"F0.wireOp",EDGE,"E89")}),1.0]])]});
            var Q47;
            Q47=makeQuery(id+"F0.imprint","IMPRINT",FACE,{"disambiguationData":[TD([[makeQuery(id+"F0.imprint","IMPRINT",EDGE,{"derivedFrom":sQuery(id+"F0.wireOp",EDGE,"E90")}),1.0]])]});
            var Q48;
            Q48=makeQuery(id+"F0.imprint","IMPRINT",FACE,{"disambiguationData":[TD([[makeQuery(id+"F0.imprint","IMPRINT",EDGE,{"derivedFrom":sQuery(id+"F0.wireOp",EDGE,"E91")}),1.0]])]});
            var Q49;
            Q49=makeQuery(id+"F0.imprint","IMPRINT",FACE,{"disambiguationData":[TD([[makeQuery(id+"F0.imprint","IMPRINT",EDGE,{"derivedFrom":sQuery(id+"F0.wireOp",EDGE,"E92")}),1.0]])]});
            var Q50;
            Q50=makeQuery(id+"F0.imprint","IMPRINT",FACE,{"disambiguationData":[TD([[makeQuery(id+"F0.imprint","IMPRINT",EDGE,{"derivedFrom":sQuery(id+"F0.wireOp",EDGE,"E93")}),1.0]])]});
            var Q51;
            Q51=makeQuery(id+"F0.imprint","IMPRINT",FACE,{"disambiguationData":[TD([[makeQuery(id+"F0.imprint","IMPRINT",EDGE,{"derivedFrom":sQuery(id+"F0.wireOp",EDGE,"E94")}),1.0]])]});
            var Q52;
            Q52=makeQuery(id+"F0.imprint","IMPRINT",FACE,{"disambiguationData":[TD([[makeQuery(id+"F0.imprint","IMPRINT",EDGE,{"derivedFrom":sQuery(id+"F0.wireOp",EDGE,"E95")}),1.0]])]});
            var Q53;
            Q53=makeQuery(id+"F0.imprint","IMPRINT",FACE,{"disambiguationData":[TD([[makeQuery(id+"F0.imprint","IMPRINT",EDGE,{"derivedFrom":sQuery(id+"F0.wireOp",EDGE,"E96")}),1.0]])]});
            var Q54;
            Q54=makeQuery(id+"F0.imprint","IMPRINT",FACE,{"disambiguationData":[TD([[makeQuery(id+"F0.imprint","IMPRINT",EDGE,{"derivedFrom":sQuery(id+"F0.wireOp",EDGE,"E83")}),1.0]])]});
            var Q55;
            Q55=makeQuery(id+"F0.imprint","IMPRINT",FACE,{"disambiguationData":[TD([[makeQuery(id+"F0.imprint","IMPRINT",EDGE,{"derivedFrom":sQuery(id+"F0.wireOp",EDGE,"E82")}),1.0]])]});
            var Q56;
            Q56=makeQuery(id+"F0.imprint","IMPRINT",FACE,{"disambiguationData":[TD([[makeQuery(id+"F0.imprint","IMPRINT",EDGE,{"derivedFrom":sQuery(id+"F0.wireOp",EDGE,"E81")}),1.0]])]});
            var Q57;
            Q57=makeQuery(id+"F0.imprint","IMPRINT",FACE,{"disambiguationData":[TD([[makeQuery(id+"F0.imprint","IMPRINT",EDGE,{"derivedFrom":sQuery(id+"F0.wireOp",EDGE,"E80")}),1.0]])]});
            var Q58;
            Q58=makeQuery(id+"F0.imprint","IMPRINT",FACE,{"disambiguationData":[TD([[makeQuery(id+"F0.imprint","IMPRINT",EDGE,{"derivedFrom":sQuery(id+"F0.wireOp",EDGE,"E79")}),1.0]])]});
            var Q59;
            Q59=makeQuery(id+"F0.imprint","IMPRINT",FACE,{"disambiguationData":[TD([[makeQuery(id+"F0.imprint","IMPRINT",EDGE,{"derivedFrom":sQuery(id+"F0.wireOp",EDGE,"E78")}),1.0]])]});
            var Q60;
            Q60=makeQuery(id+"F0.imprint","IMPRINT",FACE,{"disambiguationData":[TD([[makeQuery(id+"F0.imprint","IMPRINT",EDGE,{"derivedFrom":sQuery(id+"F0.wireOp",EDGE,"E76")}),1.0]])]});
            var Q61;
            Q61=makeQuery(id+"F0.imprint","IMPRINT",FACE,{"disambiguationData":[TD([[makeQuery(id+"F0.imprint","IMPRINT",EDGE,{"derivedFrom":sQuery(id+"F0.wireOp",EDGE,"E75")}),1.0]])]});
            var Q62;
            Q62=makeQuery(id+"F0.imprint","IMPRINT",FACE,{"disambiguationData":[TD([[makeQuery(id+"F0.imprint","IMPRINT",EDGE,{"derivedFrom":sQuery(id+"F0.wireOp",EDGE,"E66")}),1.0]])]});
            var Q63;
            Q63=makeQuery(id+"F0.imprint","IMPRINT",FACE,{"disambiguationData":[TD([[makeQuery(id+"F0.imprint","IMPRINT",EDGE,{"derivedFrom":sQuery(id+"F0.wireOp",EDGE,"E67")}),1.0]])]});
            var Q64;
            Q64=makeQuery(id+"F0.imprint","IMPRINT",FACE,{"disambiguationData":[TD([[makeQuery(id+"F0.imprint","IMPRINT",EDGE,{"derivedFrom":sQuery(id+"F0.wireOp",EDGE,"E68")}),1.0]])]});
            var Q65;
            Q65=makeQuery(id+"F0.imprint","IMPRINT",FACE,{"disambiguationData":[TD([[makeQuery(id+"F0.imprint","IMPRINT",EDGE,{"derivedFrom":sQuery(id+"F0.wireOp",EDGE,"E69")}),1.0]])]});
            var Q66;
            Q66=makeQuery(id+"F0.imprint","IMPRINT",FACE,{"disambiguationData":[TD([[makeQuery(id+"F0.imprint","IMPRINT",EDGE,{"derivedFrom":sQuery(id+"F0.wireOp",EDGE,"E70")}),1.0]])]});
            var Q67;
            Q67=makeQuery(id+"F0.imprint","IMPRINT",FACE,{"disambiguationData":[TD([[makeQuery(id+"F0.imprint","IMPRINT",EDGE,{"derivedFrom":sQuery(id+"F0.wireOp",EDGE,"E71")}),1.0]])]});
            var Q68;
            Q68=makeQuery(id+"F0.imprint","IMPRINT",FACE,{"disambiguationData":[TD([[makeQuery(id+"F0.imprint","IMPRINT",EDGE,{"derivedFrom":sQuery(id+"F0.wireOp",EDGE,"E72")}),1.0]])]});
            var Q69;
            Q69=makeQuery(id+"F0.imprint","IMPRINT",FACE,{"disambiguationData":[TD([[makeQuery(id+"F0.imprint","IMPRINT",EDGE,{"derivedFrom":sQuery(id+"F0.wireOp",EDGE,"E73")}),1.0]])]});
            var Q70;
            Q70=makeQuery(id+"F0.imprint","IMPRINT",FACE,{"disambiguationData":[TD([[makeQuery(id+"F0.imprint","IMPRINT",EDGE,{"derivedFrom":sQuery(id+"F0.wireOp",EDGE,"E74")}),1.0]])]});
            var Q71;
            Q71=makeQuery(id+"F0.imprint","IMPRINT",FACE,{"disambiguationData":[TD([[makeQuery(id+"F0.imprint","IMPRINT",EDGE,{"derivedFrom":sQuery(id+"F0.wireOp",EDGE,"E77")}),1.0]])]});
            var Q72;
            Q72=makeQuery(id+"F0.imprint","IMPRINT",FACE,{"disambiguationData":[TD([[makeQuery(id+"F0.imprint","IMPRINT",EDGE,{"derivedFrom":sQuery(id+"F0.wireOp",EDGE,"E49")}),1.0]])]});
            var Q73;
            Q73=makeQuery(id+"F0.imprint","IMPRINT",FACE,{"disambiguationData":[TD([[makeQuery(id+"F0.imprint","IMPRINT",EDGE,{"derivedFrom":sQuery(id+"F0.wireOp",EDGE,"E65")}),1.0]])]});
            var Q74;
            Q74=makeQuery(id+"F0.imprint","IMPRINT",FACE,{"disambiguationData":[TD([[makeQuery(id+"F0.imprint","IMPRINT",EDGE,{"derivedFrom":sQuery(id+"F0.wireOp",EDGE,"E64")}),1.0]])]});
            var Q75;
            Q75=makeQuery(id+"F0.imprint","IMPRINT",FACE,{"disambiguationData":[TD([[makeQuery(id+"F0.imprint","IMPRINT",EDGE,{"derivedFrom":sQuery(id+"F0.wireOp",EDGE,"E63")}),1.0]])]});
            var Q76;
            Q76=makeQuery(id+"F0.imprint","IMPRINT",FACE,{"disambiguationData":[TD([[makeQuery(id+"F0.imprint","IMPRINT",EDGE,{"derivedFrom":sQuery(id+"F0.wireOp",EDGE,"E62")}),1.0]])]});
            var Q77;
            Q77=makeQuery(id+"F0.imprint","IMPRINT",FACE,{"disambiguationData":[TD([[makeQuery(id+"F0.imprint","IMPRINT",EDGE,{"derivedFrom":sQuery(id+"F0.wireOp",EDGE,"E61")}),1.0]])]});
            var Q78;
            Q78=makeQuery(id+"F0.imprint","IMPRINT",FACE,{"disambiguationData":[TD([[makeQuery(id+"F0.imprint","IMPRINT",EDGE,{"derivedFrom":sQuery(id+"F0.wireOp",EDGE,"E60")}),1.0]])]});
            var Q79;
            Q79=makeQuery(id+"F0.imprint","IMPRINT",FACE,{"disambiguationData":[TD([[makeQuery(id+"F0.imprint","IMPRINT",EDGE,{"derivedFrom":sQuery(id+"F0.wireOp",EDGE,"E59")}),1.0]])]});
            var Q80;
            Q80=makeQuery(id+"F0.imprint","IMPRINT",FACE,{"disambiguationData":[TD([[makeQuery(id+"F0.imprint","IMPRINT",EDGE,{"derivedFrom":sQuery(id+"F0.wireOp",EDGE,"E58")}),1.0]])]});
            var Q81;
            Q81=makeQuery(id+"F0.imprint","IMPRINT",FACE,{"disambiguationData":[TD([[makeQuery(id+"F0.imprint","IMPRINT",EDGE,{"derivedFrom":sQuery(id+"F0.wireOp",EDGE,"E48")}),1.0]])]});
            var Q82;
            Q82=makeQuery(id+"F0.imprint","IMPRINT",FACE,{"disambiguationData":[TD([[makeQuery(id+"F0.imprint","IMPRINT",EDGE,{"derivedFrom":sQuery(id+"F0.wireOp",EDGE,"E50")}),1.0]])]});
            var Q83;
            Q83=makeQuery(id+"F0.imprint","IMPRINT",FACE,{"disambiguationData":[TD([[makeQuery(id+"F0.imprint","IMPRINT",EDGE,{"derivedFrom":sQuery(id+"F0.wireOp",EDGE,"E51")}),1.0]])]});
            var Q84;
            Q84=makeQuery(id+"F0.imprint","IMPRINT",FACE,{"disambiguationData":[TD([[makeQuery(id+"F0.imprint","IMPRINT",EDGE,{"derivedFrom":sQuery(id+"F0.wireOp",EDGE,"E52")}),1.0]])]});
            var Q85;
            Q85=makeQuery(id+"F0.imprint","IMPRINT",FACE,{"disambiguationData":[TD([[makeQuery(id+"F0.imprint","IMPRINT",EDGE,{"derivedFrom":sQuery(id+"F0.wireOp",EDGE,"E53")}),1.0]])]});
            var Q86;
            Q86=makeQuery(id+"F0.imprint","IMPRINT",FACE,{"disambiguationData":[TD([[makeQuery(id+"F0.imprint","IMPRINT",EDGE,{"derivedFrom":sQuery(id+"F0.wireOp",EDGE,"E54")}),1.0]])]});
            var Q87;
            Q87=makeQuery(id+"F0.imprint","IMPRINT",FACE,{"disambiguationData":[TD([[makeQuery(id+"F0.imprint","IMPRINT",EDGE,{"derivedFrom":sQuery(id+"F0.wireOp",EDGE,"E55")}),1.0]])]});
            var Q88;
            Q88=makeQuery(id+"F0.imprint","IMPRINT",FACE,{"disambiguationData":[TD([[makeQuery(id+"F0.imprint","IMPRINT",EDGE,{"derivedFrom":sQuery(id+"F0.wireOp",EDGE,"E56")}),1.0]])]});
            var Q89;
            Q89=makeQuery(id+"F0.imprint","IMPRINT",FACE,{"disambiguationData":[TD([[makeQuery(id+"F0.imprint","IMPRINT",EDGE,{"derivedFrom":sQuery(id+"F0.wireOp",EDGE,"E57")}),1.0]])]});
            extrude(context, id + "F9", {"entities" : qUnion([Q0, Q1, Q2, Q3, Q4, Q5, Q6, Q7, Q8, Q9, Q10, Q11, Q12, Q13, Q14, Q15, Q16, Q17, Q18, Q19, Q20, Q21, Q22, Q23, Q24, Q25, Q26, Q27, Q28, Q29, Q30, Q31, Q32, Q33, Q34, Q35, Q36, Q37, Q38, Q39, Q40, Q41, Q42, Q43, Q44, Q45, Q46, Q47, Q48, Q49, Q50, Q51, Q52, Q53, Q54, Q55, Q56, Q57, Q58, Q59, Q60, Q61, Q62, Q63, Q64, Q65, Q66, Q67, Q68, Q69, Q70, Q71, Q72, Q73, Q74, Q75, Q76, Q77, Q78, Q79, Q80, Q81, Q82, Q83, Q84, Q85, Q86, Q87, Q88, Q89]), "endBound" : BoundingType.SYMMETRIC, "depth" : 25 * mm, "offsetDistance" : 25 * mm, "hasDraft" : true, "draftAngle" : 1 * degree});
        }
        {
            var Q0;
            Q0=makeQuery(id+"F9.*.split.splitOp","SPLIT",BODY,{"derivedFrom":makeQuery(id+"F9.opExtrude","SWEPT_BODY",BODY,{"disambiguationData":[OSD([sQuery(id+"F0.wireOp",EDGE,"E178")])]})});
            var Q1;
            Q1=makeQuery(id+"F9.*.split.splitOp","SPLIT",BODY,{"derivedFrom":makeQuery(id+"F9.opExtrude","SWEPT_BODY",BODY,{"disambiguationData":[OSD([sQuery(id+"F0.wireOp",EDGE,"E179")])]})});
            var Q2;
            Q2=makeQuery(id+"F9.*.split.splitOp","SPLIT",BODY,{"derivedFrom":makeQuery(id+"F9.opExtrude","SWEPT_BODY",BODY,{"disambiguationData":[OSD([sQuery(id+"F0.wireOp",EDGE,"E180")])]})});
            var Q3;
            Q3=makeQuery(id+"F9.*.split.splitOp","SPLIT",BODY,{"derivedFrom":makeQuery(id+"F9.opExtrude","SWEPT_BODY",BODY,{"disambiguationData":[OSD([sQuery(id+"F0.wireOp",EDGE,"E181")])]})});
            var Q4;
            Q4=makeQuery(id+"F9.*.split.splitOp","SPLIT",BODY,{"derivedFrom":makeQuery(id+"F9.opExtrude","SWEPT_BODY",BODY,{"disambiguationData":[OSD([sQuery(id+"F0.wireOp",EDGE,"E182")])]})});
            var Q5;
            Q5=makeQuery(id+"F9.*.split.splitOp","SPLIT",BODY,{"derivedFrom":makeQuery(id+"F9.opExtrude","SWEPT_BODY",BODY,{"disambiguationData":[OSD([sQuery(id+"F0.wireOp",EDGE,"E183")])]})});
            var Q6;
            Q6=makeQuery(id+"F9.*.split.splitOp","SPLIT",BODY,{"derivedFrom":makeQuery(id+"F9.opExtrude","SWEPT_BODY",BODY,{"disambiguationData":[OSD([sQuery(id+"F0.wireOp",EDGE,"E184")])]})});
            var Q7;
            Q7=makeQuery(id+"F9.*.split.splitOp","SPLIT",BODY,{"derivedFrom":makeQuery(id+"F9.opExtrude","SWEPT_BODY",BODY,{"disambiguationData":[OSD([sQuery(id+"F0.wireOp",EDGE,"E185")])]})});
            var Q8;
            Q8=makeQuery(id+"F9.*.split.splitOp","SPLIT",BODY,{"derivedFrom":makeQuery(id+"F9.opExtrude","SWEPT_BODY",BODY,{"disambiguationData":[OSD([sQuery(id+"F0.wireOp",EDGE,"E186")])]})});
            var Q9;
            Q9=makeQuery(id+"F9.*.split.splitOp","SPLIT",BODY,{"derivedFrom":makeQuery(id+"F9.opExtrude","SWEPT_BODY",BODY,{"disambiguationData":[OSD([sQuery(id+"F0.wireOp",EDGE,"E177")])]})});
            var Q10;
            Q10=makeQuery(id+"F9.*.split.splitOp","SPLIT",BODY,{"derivedFrom":makeQuery(id+"F9.opExtrude","SWEPT_BODY",BODY,{"disambiguationData":[OSD([sQuery(id+"F0.wireOp",EDGE,"E176")])]})});
            var Q11;
            Q11=makeQuery(id+"F9.*.split.splitOp","SPLIT",BODY,{"derivedFrom":makeQuery(id+"F9.opExtrude","SWEPT_BODY",BODY,{"disambiguationData":[OSD([sQuery(id+"F0.wireOp",EDGE,"E175")])]})});
            var Q12;
            Q12=makeQuery(id+"F9.*.split.splitOp","SPLIT",BODY,{"derivedFrom":makeQuery(id+"F9.opExtrude","SWEPT_BODY",BODY,{"disambiguationData":[OSD([sQuery(id+"F0.wireOp",EDGE,"E174")])]})});
            var Q13;
            Q13=makeQuery(id+"F9.*.split.splitOp","SPLIT",BODY,{"derivedFrom":makeQuery(id+"F9.opExtrude","SWEPT_BODY",BODY,{"disambiguationData":[OSD([sQuery(id+"F0.wireOp",EDGE,"E173")])]})});
            var Q14;
            Q14=makeQuery(id+"F9.*.split.splitOp","SPLIT",BODY,{"derivedFrom":makeQuery(id+"F9.opExtrude","SWEPT_BODY",BODY,{"disambiguationData":[OSD([sQuery(id+"F0.wireOp",EDGE,"E172")])]})});
            var Q15;
            Q15=makeQuery(id+"F9.*.split.splitOp","SPLIT",BODY,{"derivedFrom":makeQuery(id+"F9.opExtrude","SWEPT_BODY",BODY,{"disambiguationData":[OSD([sQuery(id+"F0.wireOp",EDGE,"E171")])]})});
            var Q16;
            Q16=makeQuery(id+"F9.*.split.splitOp","SPLIT",BODY,{"derivedFrom":makeQuery(id+"F9.opExtrude","SWEPT_BODY",BODY,{"disambiguationData":[OSD([sQuery(id+"F0.wireOp",EDGE,"E170")])]})});
            var Q17;
            Q17=makeQuery(id+"F9.*.split.splitOp","SPLIT",BODY,{"derivedFrom":makeQuery(id+"F9.opExtrude","SWEPT_BODY",BODY,{"disambiguationData":[OSD([sQuery(id+"F0.wireOp",EDGE,"E169")])]})});
            var Q18;
            Q18=makeQuery(id+"F9.*.split.splitOp","SPLIT",BODY,{"derivedFrom":makeQuery(id+"F9.opExtrude","SWEPT_BODY",BODY,{"disambiguationData":[OSD([sQuery(id+"F0.wireOp",EDGE,"E160")])]})});
            var Q19;
            Q19=makeQuery(id+"F9.*.split.splitOp","SPLIT",BODY,{"derivedFrom":makeQuery(id+"F9.opExtrude","SWEPT_BODY",BODY,{"disambiguationData":[OSD([sQuery(id+"F0.wireOp",EDGE,"E161")])]})});
            var Q20;
            Q20=makeQuery(id+"F9.*.split.splitOp","SPLIT",BODY,{"derivedFrom":makeQuery(id+"F9.opExtrude","SWEPT_BODY",BODY,{"disambiguationData":[OSD([sQuery(id+"F0.wireOp",EDGE,"E162")])]})});
            var Q21;
            Q21=makeQuery(id+"F9.*.split.splitOp","SPLIT",BODY,{"derivedFrom":makeQuery(id+"F9.opExtrude","SWEPT_BODY",BODY,{"disambiguationData":[OSD([sQuery(id+"F0.wireOp",EDGE,"E163")])]})});
            var Q22;
            Q22=makeQuery(id+"F9.*.split.splitOp","SPLIT",BODY,{"derivedFrom":makeQuery(id+"F9.opExtrude","SWEPT_BODY",BODY,{"disambiguationData":[OSD([sQuery(id+"F0.wireOp",EDGE,"E164")])]})});
            var Q23;
            Q23=makeQuery(id+"F9.*.split.splitOp","SPLIT",BODY,{"derivedFrom":makeQuery(id+"F9.opExtrude","SWEPT_BODY",BODY,{"disambiguationData":[OSD([sQuery(id+"F0.wireOp",EDGE,"E165")])]})});
            var Q24;
            Q24=makeQuery(id+"F9.*.split.splitOp","SPLIT",BODY,{"derivedFrom":makeQuery(id+"F9.opExtrude","SWEPT_BODY",BODY,{"disambiguationData":[OSD([sQuery(id+"F0.wireOp",EDGE,"E166")])]})});
            var Q25;
            Q25=makeQuery(id+"F9.*.split.splitOp","SPLIT",BODY,{"derivedFrom":makeQuery(id+"F9.opExtrude","SWEPT_BODY",BODY,{"disambiguationData":[OSD([sQuery(id+"F0.wireOp",EDGE,"E167")])]})});
            var Q26;
            Q26=makeQuery(id+"F9.*.split.splitOp","SPLIT",BODY,{"derivedFrom":makeQuery(id+"F9.opExtrude","SWEPT_BODY",BODY,{"disambiguationData":[OSD([sQuery(id+"F0.wireOp",EDGE,"E168")])]})});
            var Q27;
            Q27=makeQuery(id+"F9.*.split.splitOp","SPLIT",BODY,{"derivedFrom":makeQuery(id+"F9.opExtrude","SWEPT_BODY",BODY,{"disambiguationData":[OSD([sQuery(id+"F0.wireOp",EDGE,"E151")])]})});
            var Q28;
            Q28=makeQuery(id+"F9.*.split.splitOp","SPLIT",BODY,{"derivedFrom":makeQuery(id+"F9.opExtrude","SWEPT_BODY",BODY,{"disambiguationData":[OSD([sQuery(id+"F0.wireOp",EDGE,"E152")])]})});
            var Q29;
            Q29=makeQuery(id+"F9.*.split.splitOp","SPLIT",BODY,{"derivedFrom":makeQuery(id+"F9.opExtrude","SWEPT_BODY",BODY,{"disambiguationData":[OSD([sQuery(id+"F0.wireOp",EDGE,"E153")])]})});
            var Q30;
            Q30=makeQuery(id+"F9.*.split.splitOp","SPLIT",BODY,{"derivedFrom":makeQuery(id+"F9.opExtrude","SWEPT_BODY",BODY,{"disambiguationData":[OSD([sQuery(id+"F0.wireOp",EDGE,"E154")])]})});
            var Q31;
            Q31=makeQuery(id+"F9.*.split.splitOp","SPLIT",BODY,{"derivedFrom":makeQuery(id+"F9.opExtrude","SWEPT_BODY",BODY,{"disambiguationData":[OSD([sQuery(id+"F0.wireOp",EDGE,"E155")])]})});
            var Q32;
            Q32=makeQuery(id+"F9.*.split.splitOp","SPLIT",BODY,{"derivedFrom":makeQuery(id+"F9.opExtrude","SWEPT_BODY",BODY,{"disambiguationData":[OSD([sQuery(id+"F0.wireOp",EDGE,"E156")])]})});
            var Q33;
            Q33=makeQuery(id+"F9.*.split.splitOp","SPLIT",BODY,{"derivedFrom":makeQuery(id+"F9.opExtrude","SWEPT_BODY",BODY,{"disambiguationData":[OSD([sQuery(id+"F0.wireOp",EDGE,"E157")])]})});
            var Q34;
            Q34=makeQuery(id+"F9.*.split.splitOp","SPLIT",BODY,{"derivedFrom":makeQuery(id+"F9.opExtrude","SWEPT_BODY",BODY,{"disambiguationData":[OSD([sQuery(id+"F0.wireOp",EDGE,"E158")])]})});
            var Q35;
            Q35=makeQuery(id+"F9.*.split.splitOp","SPLIT",BODY,{"derivedFrom":makeQuery(id+"F9.opExtrude","SWEPT_BODY",BODY,{"disambiguationData":[OSD([sQuery(id+"F0.wireOp",EDGE,"E159")])]})});
            var Q36;
            Q36=makeQuery(id+"F9.*.split.splitOp","SPLIT",BODY,{"derivedFrom":makeQuery(id+"F9.opExtrude","SWEPT_BODY",BODY,{"disambiguationData":[OSD([sQuery(id+"F0.wireOp",EDGE,"E142")])]})});
            var Q37;
            Q37=makeQuery(id+"F9.*.split.splitOp","SPLIT",BODY,{"derivedFrom":makeQuery(id+"F9.opExtrude","SWEPT_BODY",BODY,{"disambiguationData":[OSD([sQuery(id+"F0.wireOp",EDGE,"E143")])]})});
            var Q38;
            Q38=makeQuery(id+"F9.*.split.splitOp","SPLIT",BODY,{"derivedFrom":makeQuery(id+"F9.opExtrude","SWEPT_BODY",BODY,{"disambiguationData":[OSD([sQuery(id+"F0.wireOp",EDGE,"E144")])]})});
            var Q39;
            Q39=makeQuery(id+"F9.*.split.splitOp","SPLIT",BODY,{"derivedFrom":makeQuery(id+"F9.opExtrude","SWEPT_BODY",BODY,{"disambiguationData":[OSD([sQuery(id+"F0.wireOp",EDGE,"E145")])]})});
            var Q40;
            Q40=makeQuery(id+"F9.*.split.splitOp","SPLIT",BODY,{"derivedFrom":makeQuery(id+"F9.opExtrude","SWEPT_BODY",BODY,{"disambiguationData":[OSD([sQuery(id+"F0.wireOp",EDGE,"E146")])]})});
            var Q41;
            Q41=makeQuery(id+"F9.*.split.splitOp","SPLIT",BODY,{"derivedFrom":makeQuery(id+"F9.opExtrude","SWEPT_BODY",BODY,{"disambiguationData":[OSD([sQuery(id+"F0.wireOp",EDGE,"E147")])]})});
            var Q42;
            Q42=makeQuery(id+"F9.*.split.splitOp","SPLIT",BODY,{"derivedFrom":makeQuery(id+"F9.opExtrude","SWEPT_BODY",BODY,{"disambiguationData":[OSD([sQuery(id+"F0.wireOp",EDGE,"E148")])]})});
            var Q43;
            Q43=makeQuery(id+"F9.*.split.splitOp","SPLIT",BODY,{"derivedFrom":makeQuery(id+"F9.opExtrude","SWEPT_BODY",BODY,{"disambiguationData":[OSD([sQuery(id+"F0.wireOp",EDGE,"E149")])]})});
            var Q44;
            Q44=makeQuery(id+"F9.*.split.splitOp","SPLIT",BODY,{"derivedFrom":makeQuery(id+"F9.opExtrude","SWEPT_BODY",BODY,{"disambiguationData":[OSD([sQuery(id+"F0.wireOp",EDGE,"E150")])]})});
            var Q45;
            Q45=makeQuery(id+"F9.*.split.splitOp","SPLIT",BODY,{"derivedFrom":makeQuery(id+"F9.opExtrude","SWEPT_BODY",BODY,{"disambiguationData":[OSD([sQuery(id+"F0.wireOp",EDGE,"E88")])]})});
            var Q46;
            Q46=makeQuery(id+"F9.*.split.splitOp","SPLIT",BODY,{"derivedFrom":makeQuery(id+"F9.opExtrude","SWEPT_BODY",BODY,{"disambiguationData":[OSD([sQuery(id+"F0.wireOp",EDGE,"E89")])]})});
            var Q47;
            Q47=makeQuery(id+"F9.*.split.splitOp","SPLIT",BODY,{"derivedFrom":makeQuery(id+"F9.opExtrude","SWEPT_BODY",BODY,{"disambiguationData":[OSD([sQuery(id+"F0.wireOp",EDGE,"E90")])]})});
            var Q48;
            Q48=makeQuery(id+"F9.*.split.splitOp","SPLIT",BODY,{"derivedFrom":makeQuery(id+"F9.opExtrude","SWEPT_BODY",BODY,{"disambiguationData":[OSD([sQuery(id+"F0.wireOp",EDGE,"E91")])]})});
            var Q49;
            Q49=makeQuery(id+"F9.*.split.splitOp","SPLIT",BODY,{"derivedFrom":makeQuery(id+"F9.opExtrude","SWEPT_BODY",BODY,{"disambiguationData":[OSD([sQuery(id+"F0.wireOp",EDGE,"E92")])]})});
            var Q50;
            Q50=makeQuery(id+"F9.*.split.splitOp","SPLIT",BODY,{"derivedFrom":makeQuery(id+"F9.opExtrude","SWEPT_BODY",BODY,{"disambiguationData":[OSD([sQuery(id+"F0.wireOp",EDGE,"E93")])]})});
            var Q51;
            Q51=makeQuery(id+"F9.*.split.splitOp","SPLIT",BODY,{"derivedFrom":makeQuery(id+"F9.opExtrude","SWEPT_BODY",BODY,{"disambiguationData":[OSD([sQuery(id+"F0.wireOp",EDGE,"E94")])]})});
            var Q52;
            Q52=makeQuery(id+"F9.*.split.splitOp","SPLIT",BODY,{"derivedFrom":makeQuery(id+"F9.opExtrude","SWEPT_BODY",BODY,{"disambiguationData":[OSD([sQuery(id+"F0.wireOp",EDGE,"E95")])]})});
            var Q53;
            Q53=makeQuery(id+"F9.*.split.splitOp","SPLIT",BODY,{"derivedFrom":makeQuery(id+"F9.opExtrude","SWEPT_BODY",BODY,{"disambiguationData":[OSD([sQuery(id+"F0.wireOp",EDGE,"E96")])]})});
            var Q54;
            Q54=makeQuery(id+"F9.*.split.splitOp","SPLIT",BODY,{"derivedFrom":makeQuery(id+"F9.opExtrude","SWEPT_BODY",BODY,{"disambiguationData":[OSD([sQuery(id+"F0.wireOp",EDGE,"E75")])]})});
            var Q55;
            Q55=makeQuery(id+"F9.*.split.splitOp","SPLIT",BODY,{"derivedFrom":makeQuery(id+"F9.opExtrude","SWEPT_BODY",BODY,{"disambiguationData":[OSD([sQuery(id+"F0.wireOp",EDGE,"E76")])]})});
            var Q56;
            Q56=makeQuery(id+"F9.*.split.splitOp","SPLIT",BODY,{"derivedFrom":makeQuery(id+"F9.opExtrude","SWEPT_BODY",BODY,{"disambiguationData":[OSD([sQuery(id+"F0.wireOp",EDGE,"E77")])]})});
            var Q57;
            Q57=makeQuery(id+"F9.*.split.splitOp","SPLIT",BODY,{"derivedFrom":makeQuery(id+"F9.opExtrude","SWEPT_BODY",BODY,{"disambiguationData":[OSD([sQuery(id+"F0.wireOp",EDGE,"E78")])]})});
            var Q58;
            Q58=makeQuery(id+"F9.*.split.splitOp","SPLIT",BODY,{"derivedFrom":makeQuery(id+"F9.opExtrude","SWEPT_BODY",BODY,{"disambiguationData":[OSD([sQuery(id+"F0.wireOp",EDGE,"E79")])]})});
            var Q59;
            Q59=makeQuery(id+"F9.*.split.splitOp","SPLIT",BODY,{"derivedFrom":makeQuery(id+"F9.opExtrude","SWEPT_BODY",BODY,{"disambiguationData":[OSD([sQuery(id+"F0.wireOp",EDGE,"E80")])]})});
            var Q60;
            Q60=makeQuery(id+"F9.*.split.splitOp","SPLIT",BODY,{"derivedFrom":makeQuery(id+"F9.opExtrude","SWEPT_BODY",BODY,{"disambiguationData":[OSD([sQuery(id+"F0.wireOp",EDGE,"E81")])]})});
            var Q61;
            Q61=makeQuery(id+"F9.*.split.splitOp","SPLIT",BODY,{"derivedFrom":makeQuery(id+"F9.opExtrude","SWEPT_BODY",BODY,{"disambiguationData":[OSD([sQuery(id+"F0.wireOp",EDGE,"E82")])]})});
            var Q62;
            Q62=makeQuery(id+"F9.*.split.splitOp","SPLIT",BODY,{"derivedFrom":makeQuery(id+"F9.opExtrude","SWEPT_BODY",BODY,{"disambiguationData":[OSD([sQuery(id+"F0.wireOp",EDGE,"E83")])]})});
            var Q63;
            Q63=makeQuery(id+"F9.*.split.splitOp","SPLIT",BODY,{"derivedFrom":makeQuery(id+"F9.opExtrude","SWEPT_BODY",BODY,{"disambiguationData":[OSD([sQuery(id+"F0.wireOp",EDGE,"E66")])]})});
            var Q64;
            Q64=makeQuery(id+"F9.*.split.splitOp","SPLIT",BODY,{"derivedFrom":makeQuery(id+"F9.opExtrude","SWEPT_BODY",BODY,{"disambiguationData":[OSD([sQuery(id+"F0.wireOp",EDGE,"E67")])]})});
            var Q65;
            Q65=makeQuery(id+"F9.*.split.splitOp","SPLIT",BODY,{"derivedFrom":makeQuery(id+"F9.opExtrude","SWEPT_BODY",BODY,{"disambiguationData":[OSD([sQuery(id+"F0.wireOp",EDGE,"E68")])]})});
            var Q66;
            Q66=makeQuery(id+"F9.*.split.splitOp","SPLIT",BODY,{"derivedFrom":makeQuery(id+"F9.opExtrude","SWEPT_BODY",BODY,{"disambiguationData":[OSD([sQuery(id+"F0.wireOp",EDGE,"E70")])]})});
            var Q67;
            Q67=makeQuery(id+"F9.*.split.splitOp","SPLIT",BODY,{"derivedFrom":makeQuery(id+"F9.opExtrude","SWEPT_BODY",BODY,{"disambiguationData":[OSD([sQuery(id+"F0.wireOp",EDGE,"E71")])]})});
            var Q68;
            Q68=makeQuery(id+"F9.*.split.splitOp","SPLIT",BODY,{"derivedFrom":makeQuery(id+"F9.opExtrude","SWEPT_BODY",BODY,{"disambiguationData":[OSD([sQuery(id+"F0.wireOp",EDGE,"E72")])]})});
            var Q69;
            Q69=makeQuery(id+"F9.*.split.splitOp","SPLIT",BODY,{"derivedFrom":makeQuery(id+"F9.opExtrude","SWEPT_BODY",BODY,{"disambiguationData":[OSD([sQuery(id+"F0.wireOp",EDGE,"E73")])]})});
            var Q70;
            Q70=makeQuery(id+"F9.*.split.splitOp","SPLIT",BODY,{"derivedFrom":makeQuery(id+"F9.opExtrude","SWEPT_BODY",BODY,{"disambiguationData":[OSD([sQuery(id+"F0.wireOp",EDGE,"E74")])]})});
            var Q71;
            Q71=makeQuery(id+"F9.*.split.splitOp","SPLIT",BODY,{"derivedFrom":makeQuery(id+"F9.opExtrude","SWEPT_BODY",BODY,{"disambiguationData":[OSD([sQuery(id+"F0.wireOp",EDGE,"E69")])]})});
            var Q72;
            Q72=makeQuery(id+"F9.*.split.splitOp","SPLIT",BODY,{"derivedFrom":makeQuery(id+"F9.opExtrude","SWEPT_BODY",BODY,{"disambiguationData":[OSD([sQuery(id+"F0.wireOp",EDGE,"E49")])]})});
            var Q73;
            Q73=makeQuery(id+"F9.*.split.splitOp","SPLIT",BODY,{"derivedFrom":makeQuery(id+"F9.opExtrude","SWEPT_BODY",BODY,{"disambiguationData":[OSD([sQuery(id+"F0.wireOp",EDGE,"E65")])]})});
            var Q74;
            Q74=makeQuery(id+"F9.*.split.splitOp","SPLIT",BODY,{"derivedFrom":makeQuery(id+"F9.opExtrude","SWEPT_BODY",BODY,{"disambiguationData":[OSD([sQuery(id+"F0.wireOp",EDGE,"E64")])]})});
            var Q75;
            Q75=makeQuery(id+"F9.*.split.splitOp","SPLIT",BODY,{"derivedFrom":makeQuery(id+"F9.opExtrude","SWEPT_BODY",BODY,{"disambiguationData":[OSD([sQuery(id+"F0.wireOp",EDGE,"E63")])]})});
            var Q76;
            Q76=makeQuery(id+"F9.*.split.splitOp","SPLIT",BODY,{"derivedFrom":makeQuery(id+"F9.opExtrude","SWEPT_BODY",BODY,{"disambiguationData":[OSD([sQuery(id+"F0.wireOp",EDGE,"E62")])]})});
            var Q77;
            Q77=makeQuery(id+"F9.*.split.splitOp","SPLIT",BODY,{"derivedFrom":makeQuery(id+"F9.opExtrude","SWEPT_BODY",BODY,{"disambiguationData":[OSD([sQuery(id+"F0.wireOp",EDGE,"E60")])]})});
            var Q78;
            Q78=makeQuery(id+"F9.*.split.splitOp","SPLIT",BODY,{"derivedFrom":makeQuery(id+"F9.opExtrude","SWEPT_BODY",BODY,{"disambiguationData":[OSD([sQuery(id+"F0.wireOp",EDGE,"E59")])]})});
            var Q79;
            Q79=makeQuery(id+"F9.*.split.splitOp","SPLIT",BODY,{"derivedFrom":makeQuery(id+"F9.opExtrude","SWEPT_BODY",BODY,{"disambiguationData":[OSD([sQuery(id+"F0.wireOp",EDGE,"E58")])]})});
            var Q80;
            Q80=makeQuery(id+"F9.*.split.splitOp","SPLIT",BODY,{"derivedFrom":makeQuery(id+"F9.opExtrude","SWEPT_BODY",BODY,{"disambiguationData":[OSD([sQuery(id+"F0.wireOp",EDGE,"E61")])]})});
            var Q81;
            Q81=makeQuery(id+"F9.*.split.splitOp","SPLIT",BODY,{"derivedFrom":makeQuery(id+"F9.opExtrude","SWEPT_BODY",BODY,{"disambiguationData":[OSD([sQuery(id+"F0.wireOp",EDGE,"E48")])]})});
            var Q82;
            Q82=makeQuery(id+"F9.*.split.splitOp","SPLIT",BODY,{"derivedFrom":makeQuery(id+"F9.opExtrude","SWEPT_BODY",BODY,{"disambiguationData":[OSD([sQuery(id+"F0.wireOp",EDGE,"E50")])]})});
            var Q83;
            Q83=makeQuery(id+"F9.*.split.splitOp","SPLIT",BODY,{"derivedFrom":makeQuery(id+"F9.opExtrude","SWEPT_BODY",BODY,{"disambiguationData":[OSD([sQuery(id+"F0.wireOp",EDGE,"E52")])]})});
            var Q84;
            Q84=makeQuery(id+"F9.*.split.splitOp","SPLIT",BODY,{"derivedFrom":makeQuery(id+"F9.opExtrude","SWEPT_BODY",BODY,{"disambiguationData":[OSD([sQuery(id+"F0.wireOp",EDGE,"E53")])]})});
            var Q85;
            Q85=makeQuery(id+"F9.*.split.splitOp","SPLIT",BODY,{"derivedFrom":makeQuery(id+"F9.opExtrude","SWEPT_BODY",BODY,{"disambiguationData":[OSD([sQuery(id+"F0.wireOp",EDGE,"E54")])]})});
            var Q86;
            Q86=makeQuery(id+"F9.*.split.splitOp","SPLIT",BODY,{"derivedFrom":makeQuery(id+"F9.opExtrude","SWEPT_BODY",BODY,{"disambiguationData":[OSD([sQuery(id+"F0.wireOp",EDGE,"E55")])]})});
            var Q87;
            Q87=makeQuery(id+"F9.*.split.splitOp","SPLIT",BODY,{"derivedFrom":makeQuery(id+"F9.opExtrude","SWEPT_BODY",BODY,{"disambiguationData":[OSD([sQuery(id+"F0.wireOp",EDGE,"E56")])]})});
            var Q88;
            Q88=makeQuery(id+"F9.*.split.splitOp","SPLIT",BODY,{"derivedFrom":makeQuery(id+"F9.opExtrude","SWEPT_BODY",BODY,{"disambiguationData":[OSD([sQuery(id+"F0.wireOp",EDGE,"E57")])]})});
            var Q89;
            Q89=makeQuery(id+"F9.*.split.splitOp","SPLIT",BODY,{"derivedFrom":makeQuery(id+"F9.opExtrude","SWEPT_BODY",BODY,{"disambiguationData":[OSD([sQuery(id+"F0.wireOp",EDGE,"E51")])]})});
            var Q90;
            Q90=makeQuery(id+"F3.opExtrude","SWEPT_BODY",BODY,{"disambiguationData":[OSD([sQuery(id+"F1.wireOp",EDGE,"E206.8.7.0")])]});
            var Q91;
            Q91=makeQuery(id+"F3.opExtrude","SWEPT_BODY",BODY,{"disambiguationData":[OSD([sQuery(id+"F1.wireOp",EDGE,"E206.8.6.0")])]});
            var Q92;
            Q92=makeQuery(id+"F3.opExtrude","SWEPT_BODY",BODY,{"disambiguationData":[OSD([sQuery(id+"F1.wireOp",EDGE,"E206.8.5.0")])]});
            var Q93;
            Q93=makeQuery(id+"F3.opExtrude","SWEPT_BODY",BODY,{"disambiguationData":[OSD([sQuery(id+"F1.wireOp",EDGE,"E206.9.5.0")])]});
            var Q94;
            Q94=makeQuery(id+"F3.opExtrude","SWEPT_BODY",BODY,{"disambiguationData":[OSD([sQuery(id+"F1.wireOp",EDGE,"E206.9.6.0")])]});
            var Q95;
            Q95=makeQuery(id+"F3.opExtrude","SWEPT_BODY",BODY,{"disambiguationData":[OSD([sQuery(id+"F1.wireOp",EDGE,"E206.9.7.0")])]});
            var Q96;
            Q96=makeQuery(id+"F3.opExtrude","SWEPT_BODY",BODY,{"disambiguationData":[OSD([sQuery(id+"F1.wireOp",EDGE,"E206.9.8.0")])]});
            var Q97;
            Q97=makeQuery(id+"F3.opExtrude","SWEPT_BODY",BODY,{"disambiguationData":[OSD([sQuery(id+"F1.wireOp",EDGE,"E206.10.8.0")])]});
            var Q98;
            Q98=makeQuery(id+"F3.opExtrude","SWEPT_BODY",BODY,{"disambiguationData":[OSD([sQuery(id+"F1.wireOp",EDGE,"E206.10.7.0")])]});
            var Q99;
            Q99=makeQuery(id+"F3.opExtrude","SWEPT_BODY",BODY,{"disambiguationData":[OSD([sQuery(id+"F1.wireOp",EDGE,"E206.10.6.0")])]});
            var Q100;
            Q100=makeQuery(id+"F3.opExtrude","SWEPT_BODY",BODY,{"disambiguationData":[OSD([sQuery(id+"F1.wireOp",EDGE,"E206.10.5.0")])]});
            var Q101;
            Q101=makeQuery(id+"F3.opExtrude","SWEPT_BODY",BODY,{"disambiguationData":[OSD([sQuery(id+"F1.wireOp",EDGE,"E206.11.5.0")])]});
            var Q102;
            Q102=makeQuery(id+"F3.opExtrude","SWEPT_BODY",BODY,{"disambiguationData":[OSD([sQuery(id+"F1.wireOp",EDGE,"E206.11.6.0")])]});
            var Q103;
            Q103=makeQuery(id+"F3.opExtrude","SWEPT_BODY",BODY,{"disambiguationData":[OSD([sQuery(id+"F1.wireOp",EDGE,"E206.11.7.0")])]});
            var Q104;
            Q104=makeQuery(id+"F3.opExtrude","SWEPT_BODY",BODY,{"disambiguationData":[OSD([sQuery(id+"F1.wireOp",EDGE,"E206.11.8.0")])]});
            var Q105;
            Q105=makeQuery(id+"F3.opExtrude","SWEPT_BODY",BODY,{"disambiguationData":[OSD([sQuery(id+"F1.wireOp",EDGE,"E206.12.8.0")])]});
            var Q106;
            Q106=makeQuery(id+"F3.opExtrude","SWEPT_BODY",BODY,{"disambiguationData":[OSD([sQuery(id+"F1.wireOp",EDGE,"E206.12.7.0")])]});
            var Q107;
            Q107=makeQuery(id+"F3.opExtrude","SWEPT_BODY",BODY,{"disambiguationData":[OSD([sQuery(id+"F1.wireOp",EDGE,"E206.12.6.0")])]});
            var Q108;
            Q108=makeQuery(id+"F3.opExtrude","SWEPT_BODY",BODY,{"disambiguationData":[OSD([sQuery(id+"F1.wireOp",EDGE,"E206.12.5.0")])]});
            var Q109;
            Q109=makeQuery(id+"F3.opExtrude","SWEPT_BODY",BODY,{"disambiguationData":[OSD([sQuery(id+"F1.wireOp",EDGE,"E206.13.5.0")])]});
            var Q110;
            Q110=makeQuery(id+"F3.opExtrude","SWEPT_BODY",BODY,{"disambiguationData":[OSD([sQuery(id+"F1.wireOp",EDGE,"E206.13.6.0")])]});
            var Q111;
            Q111=makeQuery(id+"F3.opExtrude","SWEPT_BODY",BODY,{"disambiguationData":[OSD([sQuery(id+"F1.wireOp",EDGE,"E206.13.7.0")])]});
            var Q112;
            Q112=makeQuery(id+"F3.opExtrude","SWEPT_BODY",BODY,{"disambiguationData":[OSD([sQuery(id+"F1.wireOp",EDGE,"E206.13.8.0")])]});
            var Q113;
            Q113=makeQuery(id+"F3.opExtrude","SWEPT_BODY",BODY,{"disambiguationData":[OSD([sQuery(id+"F1.wireOp",EDGE,"E206.14.8.0")])]});
            var Q114;
            Q114=makeQuery(id+"F3.opExtrude","SWEPT_BODY",BODY,{"disambiguationData":[OSD([sQuery(id+"F1.wireOp",EDGE,"E206.14.7.0")])]});
            var Q115;
            Q115=makeQuery(id+"F3.opExtrude","SWEPT_BODY",BODY,{"disambiguationData":[OSD([sQuery(id+"F1.wireOp",EDGE,"E206.14.6.0")])]});
            var Q116;
            Q116=makeQuery(id+"F3.opExtrude","SWEPT_BODY",BODY,{"disambiguationData":[OSD([sQuery(id+"F1.wireOp",EDGE,"E206.14.5.0")])]});
            var Q117;
            Q117=makeQuery(id+"F3.opExtrude","SWEPT_BODY",BODY,{"disambiguationData":[OSD([sQuery(id+"F1.wireOp",EDGE,"E206.15.5.0")])]});
            var Q118;
            Q118=makeQuery(id+"F3.opExtrude","SWEPT_BODY",BODY,{"disambiguationData":[OSD([sQuery(id+"F1.wireOp",EDGE,"E206.15.6.0")])]});
            var Q119;
            Q119=makeQuery(id+"F3.opExtrude","SWEPT_BODY",BODY,{"disambiguationData":[OSD([sQuery(id+"F1.wireOp",EDGE,"E206.15.7.0")])]});
            var Q120;
            Q120=makeQuery(id+"F3.opExtrude","SWEPT_BODY",BODY,{"disambiguationData":[OSD([sQuery(id+"F1.wireOp",EDGE,"E206.15.8.0")])]});
            var Q121;
            Q121=makeQuery(id+"F3.opExtrude","SWEPT_BODY",BODY,{"disambiguationData":[OSD([sQuery(id+"F1.wireOp",EDGE,"E206.16.8.0")])]});
            var Q122;
            Q122=makeQuery(id+"F3.opExtrude","SWEPT_BODY",BODY,{"disambiguationData":[OSD([sQuery(id+"F1.wireOp",EDGE,"E206.16.7.0")])]});
            var Q123;
            Q123=makeQuery(id+"F3.opExtrude","SWEPT_BODY",BODY,{"disambiguationData":[OSD([sQuery(id+"F1.wireOp",EDGE,"E206.16.6.0")])]});
            var Q124;
            Q124=makeQuery(id+"F3.opExtrude","SWEPT_BODY",BODY,{"disambiguationData":[OSD([sQuery(id+"F1.wireOp",EDGE,"E206.16.5.0")])]});
            var Q125;
            Q125=makeQuery(id+"F3.opExtrude","SWEPT_BODY",BODY,{"disambiguationData":[OSD([sQuery(id+"F1.wireOp",EDGE,"E206.8.4.0")])]});
            var Q126;
            Q126=makeQuery(id+"F3.opExtrude","SWEPT_BODY",BODY,{"disambiguationData":[OSD([sQuery(id+"F1.wireOp",EDGE,"E206.9.4.0")])]});
            var Q127;
            Q127=makeQuery(id+"F3.opExtrude","SWEPT_BODY",BODY,{"disambiguationData":[OSD([sQuery(id+"F1.wireOp",EDGE,"E206.10.4.0")])]});
            var Q128;
            Q128=makeQuery(id+"F3.opExtrude","SWEPT_BODY",BODY,{"disambiguationData":[OSD([sQuery(id+"F1.wireOp",EDGE,"E206.11.4.0")])]});
            var Q129;
            Q129=makeQuery(id+"F3.opExtrude","SWEPT_BODY",BODY,{"disambiguationData":[OSD([sQuery(id+"F1.wireOp",EDGE,"E206.12.4.0")])]});
            var Q130;
            Q130=makeQuery(id+"F3.opExtrude","SWEPT_BODY",BODY,{"disambiguationData":[OSD([sQuery(id+"F1.wireOp",EDGE,"E206.13.4.0")])]});
            var Q131;
            Q131=makeQuery(id+"F3.opExtrude","SWEPT_BODY",BODY,{"disambiguationData":[OSD([sQuery(id+"F1.wireOp",EDGE,"E206.14.4.0")])]});
            var Q132;
            Q132=makeQuery(id+"F3.opExtrude","SWEPT_BODY",BODY,{"disambiguationData":[OSD([sQuery(id+"F1.wireOp",EDGE,"E206.15.4.0")])]});
            var Q133;
            Q133=makeQuery(id+"F3.opExtrude","SWEPT_BODY",BODY,{"disambiguationData":[OSD([sQuery(id+"F1.wireOp",EDGE,"E206.16.4.0")])]});
            var Q134;
            Q134=makeQuery(id+"F3.opExtrude","SWEPT_BODY",BODY,{"disambiguationData":[OSD([sQuery(id+"F1.wireOp",EDGE,"E206.16.3.0")])]});
            var Q135;
            Q135=makeQuery(id+"F3.opExtrude","SWEPT_BODY",BODY,{"disambiguationData":[OSD([sQuery(id+"F1.wireOp",EDGE,"E206.15.3.0")])]});
            var Q136;
            Q136=makeQuery(id+"F3.opExtrude","SWEPT_BODY",BODY,{"disambiguationData":[OSD([sQuery(id+"F1.wireOp",EDGE,"E206.14.3.0")])]});
            var Q137;
            Q137=makeQuery(id+"F3.opExtrude","SWEPT_BODY",BODY,{"disambiguationData":[OSD([sQuery(id+"F1.wireOp",EDGE,"E206.13.3.0")])]});
            var Q138;
            Q138=makeQuery(id+"F3.opExtrude","SWEPT_BODY",BODY,{"disambiguationData":[OSD([sQuery(id+"F1.wireOp",EDGE,"E206.12.3.0")])]});
            var Q139;
            Q139=makeQuery(id+"F3.opExtrude","SWEPT_BODY",BODY,{"disambiguationData":[OSD([sQuery(id+"F1.wireOp",EDGE,"E206.11.3.0")])]});
            var Q140;
            Q140=makeQuery(id+"F3.opExtrude","SWEPT_BODY",BODY,{"disambiguationData":[OSD([sQuery(id+"F1.wireOp",EDGE,"E206.10.3.0")])]});
            var Q141;
            Q141=makeQuery(id+"F3.opExtrude","SWEPT_BODY",BODY,{"disambiguationData":[OSD([sQuery(id+"F1.wireOp",EDGE,"E206.9.3.0")])]});
            var Q142;
            Q142=makeQuery(id+"F3.opExtrude","SWEPT_BODY",BODY,{"disambiguationData":[OSD([sQuery(id+"F1.wireOp",EDGE,"E206.8.3.0")])]});
            var Q143;
            Q143=makeQuery(id+"F3.opExtrude","SWEPT_BODY",BODY,{"disambiguationData":[OSD([sQuery(id+"F1.wireOp",EDGE,"E206.8.2.0")])]});
            var Q144;
            Q144=makeQuery(id+"F3.opExtrude","SWEPT_BODY",BODY,{"disambiguationData":[OSD([sQuery(id+"F1.wireOp",EDGE,"E206.9.2.0")])]});
            var Q145;
            Q145=makeQuery(id+"F3.opExtrude","SWEPT_BODY",BODY,{"disambiguationData":[OSD([sQuery(id+"F1.wireOp",EDGE,"E206.10.2.0")])]});
            var Q146;
            Q146=makeQuery(id+"F3.opExtrude","SWEPT_BODY",BODY,{"disambiguationData":[OSD([sQuery(id+"F1.wireOp",EDGE,"E206.11.2.0")])]});
            var Q147;
            Q147=makeQuery(id+"F3.opExtrude","SWEPT_BODY",BODY,{"disambiguationData":[OSD([sQuery(id+"F1.wireOp",EDGE,"E206.12.2.0")])]});
            var Q148;
            Q148=makeQuery(id+"F3.opExtrude","SWEPT_BODY",BODY,{"disambiguationData":[OSD([sQuery(id+"F1.wireOp",EDGE,"E206.13.2.0")])]});
            var Q149;
            Q149=makeQuery(id+"F3.opExtrude","SWEPT_BODY",BODY,{"disambiguationData":[OSD([sQuery(id+"F1.wireOp",EDGE,"E206.14.2.0")])]});
            var Q150;
            Q150=makeQuery(id+"F3.opExtrude","SWEPT_BODY",BODY,{"disambiguationData":[OSD([sQuery(id+"F1.wireOp",EDGE,"E206.15.2.0")])]});
            var Q151;
            Q151=makeQuery(id+"F3.opExtrude","SWEPT_BODY",BODY,{"disambiguationData":[OSD([sQuery(id+"F1.wireOp",EDGE,"E206.16.2.0")])]});
            var Q152;
            Q152=makeQuery(id+"F3.opExtrude","SWEPT_BODY",BODY,{"disambiguationData":[OSD([sQuery(id+"F1.wireOp",EDGE,"E206.16.1.0")])]});
            var Q153;
            Q153=makeQuery(id+"F3.opExtrude","SWEPT_BODY",BODY,{"disambiguationData":[OSD([sQuery(id+"F1.wireOp",EDGE,"E206.15.1.0")])]});
            var Q154;
            Q154=makeQuery(id+"F3.opExtrude","SWEPT_BODY",BODY,{"disambiguationData":[OSD([sQuery(id+"F1.wireOp",EDGE,"E206.14.1.0")])]});
            var Q155;
            Q155=makeQuery(id+"F3.opExtrude","SWEPT_BODY",BODY,{"disambiguationData":[OSD([sQuery(id+"F1.wireOp",EDGE,"E206.13.1.0")])]});
            var Q156;
            Q156=makeQuery(id+"F3.opExtrude","SWEPT_BODY",BODY,{"disambiguationData":[OSD([sQuery(id+"F1.wireOp",EDGE,"E206.12.1.0")])]});
            var Q157;
            Q157=makeQuery(id+"F3.opExtrude","SWEPT_BODY",BODY,{"disambiguationData":[OSD([sQuery(id+"F1.wireOp",EDGE,"E206.11.1.0")])]});
            var Q158;
            Q158=makeQuery(id+"F3.opExtrude","SWEPT_BODY",BODY,{"disambiguationData":[OSD([sQuery(id+"F1.wireOp",EDGE,"E206.10.1.0")])]});
            var Q159;
            Q159=makeQuery(id+"F3.opExtrude","SWEPT_BODY",BODY,{"disambiguationData":[OSD([sQuery(id+"F1.wireOp",EDGE,"E206.9.1.0")])]});
            var Q160;
            Q160=makeQuery(id+"F3.opExtrude","SWEPT_BODY",BODY,{"disambiguationData":[OSD([sQuery(id+"F1.wireOp",EDGE,"E206.8.1.0")])]});
            var Q161;
            Q161=makeQuery(id+"F3.opExtrude","SWEPT_BODY",BODY,{"disambiguationData":[OSD([sQuery(id+"F1.wireOp",EDGE,"E206.8.0.0")])]});
            var Q162;
            Q162=makeQuery(id+"F3.opExtrude","SWEPT_BODY",BODY,{"disambiguationData":[OSD([sQuery(id+"F1.wireOp",EDGE,"E206.9.0.0")])]});
            var Q163;
            Q163=makeQuery(id+"F3.opExtrude","SWEPT_BODY",BODY,{"disambiguationData":[OSD([sQuery(id+"F1.wireOp",EDGE,"E206.10.0.0")])]});
            var Q164;
            Q164=makeQuery(id+"F3.opExtrude","SWEPT_BODY",BODY,{"disambiguationData":[OSD([sQuery(id+"F1.wireOp",EDGE,"E206.11.0.0")])]});
            var Q165;
            Q165=makeQuery(id+"F3.opExtrude","SWEPT_BODY",BODY,{"disambiguationData":[OSD([sQuery(id+"F1.wireOp",EDGE,"E206.12.0.0")])]});
            var Q166;
            Q166=makeQuery(id+"F3.opExtrude","SWEPT_BODY",BODY,{"disambiguationData":[OSD([sQuery(id+"F1.wireOp",EDGE,"E206.13.0.0")])]});
            var Q167;
            Q167=makeQuery(id+"F3.opExtrude","SWEPT_BODY",BODY,{"disambiguationData":[OSD([sQuery(id+"F1.wireOp",EDGE,"E206.14.0.0")])]});
            var Q168;
            Q168=makeQuery(id+"F3.opExtrude","SWEPT_BODY",BODY,{"disambiguationData":[OSD([sQuery(id+"F1.wireOp",EDGE,"E206.15.0.0")])]});
            var Q169;
            Q169=makeQuery(id+"F3.opExtrude","SWEPT_BODY",BODY,{"disambiguationData":[OSD([sQuery(id+"F1.wireOp",EDGE,"E206.16.0.0")])]});
            booleanBodies(context, id + "F10", {"operationType" : BooleanOperationType.SUBTRACTION, "tools" : qUnion([Q0, Q1, Q2, Q3, Q4, Q5, Q6, Q7, Q8, Q9, Q10, Q11, Q12, Q13, Q14, Q15, Q16, Q17, Q18, Q19, Q20, Q21, Q22, Q23, Q24, Q25, Q26, Q27, Q28, Q29, Q30, Q31, Q32, Q33, Q34, Q35, Q36, Q37, Q38, Q39, Q40, Q41, Q42, Q43, Q44, Q45, Q46, Q47, Q48, Q49, Q50, Q51, Q52, Q53, Q54, Q55, Q56, Q57, Q58, Q59, Q60, Q61, Q62, Q63, Q64, Q65, Q66, Q67, Q68, Q69, Q70, Q71, Q72, Q73, Q74, Q75, Q76, Q77, Q78, Q79, Q80, Q81, Q82, Q83, Q84, Q85, Q86, Q87, Q88, Q89]), "targets" : qUnion([Q90, Q91, Q92, Q93, Q94, Q95, Q96, Q97, Q98, Q99, Q100, Q101, Q102, Q103, Q104, Q105, Q106, Q107, Q108, Q109, Q110, Q111, Q112, Q113, Q114, Q115, Q116, Q117, Q118, Q119, Q120, Q121, Q122, Q123, Q124, Q125, Q126, Q127, Q128, Q129, Q130, Q131, Q132, Q133, Q134, Q135, Q136, Q137, Q138, Q139, Q140, Q141, Q142, Q143, Q144, Q145, Q146, Q147, Q148, Q149, Q150, Q151, Q152, Q153, Q154, Q155, Q156, Q157, Q158, Q159, Q160, Q161, Q162, Q163, Q164, Q165, Q166, Q167, Q168, Q169])});
        }
        {
            var Q0;
            Q0=makeQuery(id+"F0.imprint","IMPRINT",FACE,{"disambiguationData":[TD([[makeQuery(id+"F0.imprint","IMPRINT",EDGE,{"derivedFrom":sQuery(id+"F0.wireOp",EDGE,"E178")}),1.0]])]});
            var Q1;
            Q1=sQuery(id+"F0.wireOp",EDGE,"E178");
            extrude(context, id + "F11", {"entities" : qUnion([Q0]), "surfaceEntities" : qUnion([Q1]), "endBound" : BoundingType.SYMMETRIC, "depth" : 25 * mm, "offsetDistance" : 25 * mm, "hasDraft" : true, "draftAngle" : 1 * degree});
        }
        {
            var Q0;
            Q0=makeQuery(id+"F11.*.split.splitOp","SPLIT",BODY,{"derivedFrom":makeQuery(id+"F11.opExtrude","SWEPT_BODY",BODY,{"disambiguationData":[OSD([sQuery(id+"F0.wireOp",EDGE,"E178")])]})});
            var Q1;
            Q1=makeQuery(id+"F3.opExtrude","SWEPT_BODY",BODY,{"disambiguationData":[OSD([sQuery(id+"F1.wireOp",EDGE,"E206.8.8.0")])]});
            var Q2;
            Q2=makeQuery(id+"F3.opExtrude","SWEPT_BODY",BODY,{"disambiguationData":[OSD([sQuery(id+"F1.wireOp",EDGE,"E206.9.8.0")])]});
            booleanBodies(context, id + "F12", {"operationType" : BooleanOperationType.SUBTRACTION, "tools" : qUnion([Q0]), "targets" : qUnion([Q1, Q2])});
        }
        {
            var Q0;
            Q0=makeQuery(id+"F0.imprint","IMPRINT",FACE,{"disambiguationData":[TD([[makeQuery(id+"F0.imprint","IMPRINT",EDGE,{"derivedFrom":sQuery(id+"F0.wireOp",EDGE,"E169")}),1.0]])]});
            extrude(context, id + "F13", {"entities" : qUnion([Q0]), "endBound" : BoundingType.SYMMETRIC, "depth" : 25 * mm, "offsetDistance" : 25 * mm, "hasDraft" : true, "draftAngle" : 1 * degree});
        }
        {
            var Q0;
            Q0=makeQuery(id+"F13.*.split.splitOp","SPLIT",BODY,{"derivedFrom":makeQuery(id+"F13.opExtrude","SWEPT_BODY",BODY,{"disambiguationData":[OSD([sQuery(id+"F0.wireOp",EDGE,"E169")])]})});
            var Q1;
            Q1=makeQuery(id+"F3.opExtrude","SWEPT_BODY",BODY,{"disambiguationData":[OSD([sQuery(id+"F1.wireOp",EDGE,"E206.8.7.0")])]});
            var Q2;
            Q2=makeQuery(id+"F3.opExtrude","SWEPT_BODY",BODY,{"disambiguationData":[OSD([sQuery(id+"F1.wireOp",EDGE,"E206.9.7.0")])]});
            booleanBodies(context, id + "F14", {"operationType" : BooleanOperationType.SUBTRACTION, "tools" : qUnion([Q0]), "targets" : qUnion([Q1, Q2])});
        }
        {
            var Q0;
            Q0=makeQuery(id+"F0.imprint","IMPRINT",FACE,{"disambiguationData":[TD([[makeQuery(id+"F0.imprint","IMPRINT",EDGE,{"derivedFrom":sQuery(id+"F0.wireOp",EDGE,"E169")}),1.0]])]});
            var Q1;
            Q1=makeQuery(id+"F0.imprint","IMPRINT",FACE,{"disambiguationData":[TD([[makeQuery(id+"F0.imprint","IMPRINT",EDGE,{"derivedFrom":sQuery(id+"F0.wireOp",EDGE,"E139")}),1.0]])]});
            var Q2;
            Q2=makeQuery(id+"F0.imprint","IMPRINT",FACE,{"disambiguationData":[TD([[makeQuery(id+"F0.imprint","IMPRINT",EDGE,{"derivedFrom":sQuery(id+"F0.wireOp",EDGE,"E138")}),1.0]])]});
            var Q3;
            Q3=makeQuery(id+"F0.imprint","IMPRINT",FACE,{"disambiguationData":[TD([[makeQuery(id+"F0.imprint","IMPRINT",EDGE,{"derivedFrom":sQuery(id+"F0.wireOp",EDGE,"E119")}),1.0]])]});
            var Q4;
            Q4=makeQuery(id+"F0.imprint","IMPRINT",FACE,{"disambiguationData":[TD([[makeQuery(id+"F0.imprint","IMPRINT",EDGE,{"derivedFrom":sQuery(id+"F0.wireOp",EDGE,"E106")}),1.0]])]});
            var Q5;
            Q5=makeQuery(id+"F0.imprint","IMPRINT",FACE,{"disambiguationData":[TD([[makeQuery(id+"F0.imprint","IMPRINT",EDGE,{"derivedFrom":sQuery(id+"F0.wireOp",EDGE,"E105")}),1.0]])]});
            var Q6;
            Q6=makeQuery(id+"F0.imprint","IMPRINT",FACE,{"disambiguationData":[TD([[makeQuery(id+"F0.imprint","IMPRINT",EDGE,{"derivedFrom":sQuery(id+"F0.wireOp",EDGE,"E87")}),1.0]])]});
            var Q7;
            Q7=makeQuery(id+"F0.imprint","IMPRINT",FACE,{"disambiguationData":[TD([[makeQuery(id+"F0.imprint","IMPRINT",EDGE,{"derivedFrom":sQuery(id+"F0.wireOp",EDGE,"E84")}),1.0]])]});
            var Q8;
            Q8=makeQuery(id+"F0.imprint","IMPRINT",FACE,{"disambiguationData":[TD([[makeQuery(id+"F0.imprint","IMPRINT",EDGE,{"derivedFrom":sQuery(id+"F0.wireOp",EDGE,"E47")}),1.0]])]});
            var Q9;
            Q9=makeQuery(id+"F0.imprint","IMPRINT",FACE,{"disambiguationData":[TD([[makeQuery(id+"F0.imprint","IMPRINT",EDGE,{"derivedFrom":sQuery(id+"F0.wireOp",EDGE,"E43")}),1.0]])]});
            var Q10;
            Q10=makeQuery(id+"F0.imprint","IMPRINT",FACE,{"disambiguationData":[TD([[makeQuery(id+"F0.imprint","IMPRINT",EDGE,{"derivedFrom":sQuery(id+"F0.wireOp",EDGE,"E46")}),1.0]])]});
            var Q11;
            Q11=makeQuery(id+"F0.imprint","IMPRINT",FACE,{"disambiguationData":[TD([[makeQuery(id+"F0.imprint","IMPRINT",EDGE,{"derivedFrom":sQuery(id+"F0.wireOp",EDGE,"E44")}),1.0]])]});
            var Q12;
            Q12=makeQuery(id+"F0.imprint","IMPRINT",FACE,{"disambiguationData":[TD([[makeQuery(id+"F0.imprint","IMPRINT",EDGE,{"derivedFrom":sQuery(id+"F0.wireOp",EDGE,"E42")}),1.0]])]});
            var Q13;
            Q13=makeQuery(id+"F0.imprint","IMPRINT",FACE,{"disambiguationData":[TD([[makeQuery(id+"F0.imprint","IMPRINT",EDGE,{"derivedFrom":sQuery(id+"F0.wireOp",EDGE,"E45")}),1.0]])]});
            var Q14;
            Q14=makeQuery(id+"F0.imprint","IMPRINT",FACE,{"disambiguationData":[TD([[makeQuery(id+"F0.imprint","IMPRINT",EDGE,{"derivedFrom":sQuery(id+"F0.wireOp",EDGE,"E85")}),1.0]])]});
            var Q15;
            Q15=makeQuery(id+"F0.imprint","IMPRINT",FACE,{"disambiguationData":[TD([[makeQuery(id+"F0.imprint","IMPRINT",EDGE,{"derivedFrom":sQuery(id+"F0.wireOp",EDGE,"E86")}),1.0]])]});
            var Q16;
            Q16=makeQuery(id+"F0.imprint","IMPRINT",FACE,{"disambiguationData":[TD([[makeQuery(id+"F0.imprint","IMPRINT",EDGE,{"derivedFrom":sQuery(id+"F0.wireOp",EDGE,"E104")}),1.0]])]});
            var Q17;
            Q17=makeQuery(id+"F0.imprint","IMPRINT",FACE,{"disambiguationData":[TD([[makeQuery(id+"F0.imprint","IMPRINT",EDGE,{"derivedFrom":sQuery(id+"F0.wireOp",EDGE,"E110")}),1.0]])]});
            var Q18;
            Q18=makeQuery(id+"F0.imprint","IMPRINT",FACE,{"disambiguationData":[TD([[makeQuery(id+"F0.imprint","IMPRINT",EDGE,{"derivedFrom":sQuery(id+"F0.wireOp",EDGE,"E118")}),1.0]])]});
            var Q19;
            Q19=makeQuery(id+"F0.imprint","IMPRINT",FACE,{"disambiguationData":[TD([[makeQuery(id+"F0.imprint","IMPRINT",EDGE,{"derivedFrom":sQuery(id+"F0.wireOp",EDGE,"E137")}),1.0]])]});
            var Q20;
            Q20=makeQuery(id+"F0.imprint","IMPRINT",FACE,{"disambiguationData":[TD([[makeQuery(id+"F0.imprint","IMPRINT",EDGE,{"derivedFrom":sQuery(id+"F0.wireOp",EDGE,"E140")}),1.0]])]});
            var Q21;
            Q21=makeQuery(id+"F0.imprint","IMPRINT",FACE,{"disambiguationData":[TD([[makeQuery(id+"F0.imprint","IMPRINT",EDGE,{"derivedFrom":sQuery(id+"F0.wireOp",EDGE,"E141")}),1.0]])]});
            var Q22;
            Q22=makeQuery(id+"F0.imprint","IMPRINT",FACE,{"disambiguationData":[TD([[makeQuery(id+"F0.imprint","IMPRINT",EDGE,{"derivedFrom":sQuery(id+"F0.wireOp",EDGE,"E136")}),1.0]])]});
            var Q23;
            Q23=makeQuery(id+"F0.imprint","IMPRINT",FACE,{"disambiguationData":[TD([[makeQuery(id+"F0.imprint","IMPRINT",EDGE,{"derivedFrom":sQuery(id+"F0.wireOp",EDGE,"E117")}),1.0]])]});
            var Q24;
            Q24=makeQuery(id+"F0.imprint","IMPRINT",FACE,{"disambiguationData":[TD([[makeQuery(id+"F0.imprint","IMPRINT",EDGE,{"derivedFrom":sQuery(id+"F0.wireOp",EDGE,"E109")}),1.0]])]});
            var Q25;
            Q25=makeQuery(id+"F0.imprint","IMPRINT",FACE,{"disambiguationData":[TD([[makeQuery(id+"F0.imprint","IMPRINT",EDGE,{"derivedFrom":sQuery(id+"F0.wireOp",EDGE,"E34")}),1.0]])]});
            var Q26;
            Q26=makeQuery(id+"F0.imprint","IMPRINT",FACE,{"disambiguationData":[TD([[makeQuery(id+"F0.imprint","IMPRINT",EDGE,{"derivedFrom":sQuery(id+"F0.wireOp",EDGE,"E25")}),1.0]])]});
            var Q27;
            Q27=makeQuery(id+"F0.imprint","IMPRINT",FACE,{"disambiguationData":[TD([[makeQuery(id+"F0.imprint","IMPRINT",EDGE,{"derivedFrom":sQuery(id+"F0.wireOp",EDGE,"E24")}),1.0]])]});
            var Q28;
            Q28=makeQuery(id+"F0.imprint","IMPRINT",FACE,{"disambiguationData":[TD([[makeQuery(id+"F0.imprint","IMPRINT",EDGE,{"derivedFrom":sQuery(id+"F0.wireOp",EDGE,"E23")}),1.0]])]});
            var Q29;
            Q29=makeQuery(id+"F0.imprint","IMPRINT",FACE,{"disambiguationData":[TD([[makeQuery(id+"F0.imprint","IMPRINT",EDGE,{"derivedFrom":sQuery(id+"F0.wireOp",EDGE,"E12")}),1.0]])]});
            var Q30;
            Q30=makeQuery(id+"F0.imprint","IMPRINT",FACE,{"disambiguationData":[TD([[makeQuery(id+"F0.imprint","IMPRINT",EDGE,{"derivedFrom":sQuery(id+"F0.wireOp",EDGE,"E13")}),1.0]])]});
            var Q31;
            Q31=makeQuery(id+"F0.imprint","IMPRINT",FACE,{"disambiguationData":[TD([[makeQuery(id+"F0.imprint","IMPRINT",EDGE,{"derivedFrom":sQuery(id+"F0.wireOp",EDGE,"E22")}),1.0]])]});
            var Q32;
            Q32=makeQuery(id+"F0.imprint","IMPRINT",FACE,{"disambiguationData":[TD([[makeQuery(id+"F0.imprint","IMPRINT",EDGE,{"derivedFrom":sQuery(id+"F0.wireOp",EDGE,"E33")}),1.0]])]});
            var Q33;
            Q33=makeQuery(id+"F0.imprint","IMPRINT",FACE,{"disambiguationData":[TD([[makeQuery(id+"F0.imprint","IMPRINT",EDGE,{"derivedFrom":sQuery(id+"F0.wireOp",EDGE,"E36")}),1.0]])]});
            var Q34;
            Q34=makeQuery(id+"F0.imprint","IMPRINT",FACE,{"disambiguationData":[TD([[makeQuery(id+"F0.imprint","IMPRINT",EDGE,{"derivedFrom":sQuery(id+"F0.wireOp",EDGE,"E102")}),1.0]])]});
            var Q35;
            Q35=makeQuery(id+"F0.imprint","IMPRINT",FACE,{"disambiguationData":[TD([[makeQuery(id+"F0.imprint","IMPRINT",EDGE,{"derivedFrom":sQuery(id+"F0.wireOp",EDGE,"E108")}),1.0]])]});
            var Q36;
            Q36=makeQuery(id+"F0.imprint","IMPRINT",FACE,{"disambiguationData":[TD([[makeQuery(id+"F0.imprint","IMPRINT",EDGE,{"derivedFrom":sQuery(id+"F0.wireOp",EDGE,"E116")}),1.0]])]});
            var Q37;
            Q37=makeQuery(id+"F0.imprint","IMPRINT",FACE,{"disambiguationData":[TD([[makeQuery(id+"F0.imprint","IMPRINT",EDGE,{"derivedFrom":sQuery(id+"F0.wireOp",EDGE,"E134")}),1.0]])]});
            var Q38;
            Q38=makeQuery(id+"F0.imprint","IMPRINT",FACE,{"disambiguationData":[TD([[makeQuery(id+"F0.imprint","IMPRINT",EDGE,{"derivedFrom":sQuery(id+"F0.wireOp",EDGE,"E135")}),1.0]])]});
            var Q39;
            Q39=makeQuery(id+"F0.imprint","IMPRINT",FACE,{"disambiguationData":[TD([[makeQuery(id+"F0.imprint","IMPRINT",EDGE,{"derivedFrom":sQuery(id+"F0.wireOp",EDGE,"E132")}),1.0]])]});
            var Q40;
            Q40=makeQuery(id+"F0.imprint","IMPRINT",FACE,{"disambiguationData":[TD([[makeQuery(id+"F0.imprint","IMPRINT",EDGE,{"derivedFrom":sQuery(id+"F0.wireOp",EDGE,"E133")}),1.0]])]});
            var Q41;
            Q41=makeQuery(id+"F0.imprint","IMPRINT",FACE,{"disambiguationData":[TD([[makeQuery(id+"F0.imprint","IMPRINT",EDGE,{"derivedFrom":sQuery(id+"F0.wireOp",EDGE,"E115")}),1.0]])]});
            var Q42;
            Q42=makeQuery(id+"F0.imprint","IMPRINT",FACE,{"disambiguationData":[TD([[makeQuery(id+"F0.imprint","IMPRINT",EDGE,{"derivedFrom":sQuery(id+"F0.wireOp",EDGE,"E107")}),1.0]])]});
            var Q43;
            Q43=makeQuery(id+"F0.imprint","IMPRINT",FACE,{"disambiguationData":[TD([[makeQuery(id+"F0.imprint","IMPRINT",EDGE,{"derivedFrom":sQuery(id+"F0.wireOp",EDGE,"E101")}),1.0]])]});
            var Q44;
            Q44=makeQuery(id+"F0.imprint","IMPRINT",FACE,{"disambiguationData":[TD([[makeQuery(id+"F0.imprint","IMPRINT",EDGE,{"derivedFrom":sQuery(id+"F0.wireOp",EDGE,"E37")}),1.0]])]});
            var Q45;
            Q45=makeQuery(id+"F0.imprint","IMPRINT",FACE,{"disambiguationData":[TD([[makeQuery(id+"F0.imprint","IMPRINT",EDGE,{"derivedFrom":sQuery(id+"F0.wireOp",EDGE,"E32")}),1.0]])]});
            var Q46;
            Q46=makeQuery(id+"F0.imprint","IMPRINT",FACE,{"disambiguationData":[TD([[makeQuery(id+"F0.imprint","IMPRINT",EDGE,{"derivedFrom":sQuery(id+"F0.wireOp",EDGE,"E21")}),1.0]])]});
            var Q47;
            Q47=makeQuery(id+"F0.imprint","IMPRINT",FACE,{"disambiguationData":[TD([[makeQuery(id+"F0.imprint","IMPRINT",EDGE,{"derivedFrom":sQuery(id+"F0.wireOp",EDGE,"E14")}),1.0]])]});
            var Q48;
            Q48=makeQuery(id+"F0.imprint","IMPRINT",FACE,{"disambiguationData":[TD([[makeQuery(id+"F0.imprint","IMPRINT",EDGE,{"derivedFrom":sQuery(id+"F0.wireOp",EDGE,"E11")}),1.0]])]});
            var Q49;
            Q49=makeQuery(id+"F0.imprint","IMPRINT",FACE,{"disambiguationData":[TD([[makeQuery(id+"F0.imprint","IMPRINT",EDGE,{"derivedFrom":sQuery(id+"F0.wireOp",EDGE,"E10")}),1.0]])]});
            var Q50;
            Q50=makeQuery(id+"F0.imprint","IMPRINT",FACE,{"disambiguationData":[TD([[makeQuery(id+"F0.imprint","IMPRINT",EDGE,{"derivedFrom":sQuery(id+"F0.wireOp",EDGE,"E15")}),1.0]])]});
            var Q51;
            Q51=makeQuery(id+"F0.imprint","IMPRINT",FACE,{"disambiguationData":[TD([[makeQuery(id+"F0.imprint","IMPRINT",EDGE,{"derivedFrom":sQuery(id+"F0.wireOp",EDGE,"E20")}),1.0]])]});
            var Q52;
            Q52=makeQuery(id+"F0.imprint","IMPRINT",FACE,{"disambiguationData":[TD([[makeQuery(id+"F0.imprint","IMPRINT",EDGE,{"derivedFrom":sQuery(id+"F0.wireOp",EDGE,"E38")}),1.0]])]});
            var Q53;
            Q53=makeQuery(id+"F0.imprint","IMPRINT",FACE,{"disambiguationData":[TD([[makeQuery(id+"F0.imprint","IMPRINT",EDGE,{"derivedFrom":sQuery(id+"F0.wireOp",EDGE,"E100")}),1.0]])]});
            var Q54;
            Q54=makeQuery(id+"F0.imprint","IMPRINT",FACE,{"disambiguationData":[TD([[makeQuery(id+"F0.imprint","IMPRINT",EDGE,{"derivedFrom":sQuery(id+"F0.wireOp",EDGE,"E112")}),1.0]])]});
            var Q55;
            Q55=makeQuery(id+"F0.imprint","IMPRINT",FACE,{"disambiguationData":[TD([[makeQuery(id+"F0.imprint","IMPRINT",EDGE,{"derivedFrom":sQuery(id+"F0.wireOp",EDGE,"E114")}),1.0]])]});
            var Q56;
            Q56=makeQuery(id+"F0.imprint","IMPRINT",FACE,{"disambiguationData":[TD([[makeQuery(id+"F0.imprint","IMPRINT",EDGE,{"derivedFrom":sQuery(id+"F0.wireOp",EDGE,"E130")}),1.0]])]});
            var Q57;
            Q57=makeQuery(id+"F0.imprint","IMPRINT",FACE,{"disambiguationData":[TD([[makeQuery(id+"F0.imprint","IMPRINT",EDGE,{"derivedFrom":sQuery(id+"F0.wireOp",EDGE,"E131")}),1.0]])]});
            var Q58;
            Q58=makeQuery(id+"F0.imprint","IMPRINT",FACE,{"disambiguationData":[TD([[makeQuery(id+"F0.imprint","IMPRINT",EDGE,{"derivedFrom":sQuery(id+"F0.wireOp",EDGE,"E128")}),1.0]])]});
            var Q59;
            Q59=makeQuery(id+"F0.imprint","IMPRINT",FACE,{"disambiguationData":[TD([[makeQuery(id+"F0.imprint","IMPRINT",EDGE,{"derivedFrom":sQuery(id+"F0.wireOp",EDGE,"E129")}),1.0]])]});
            var Q60;
            Q60=makeQuery(id+"F0.imprint","IMPRINT",FACE,{"disambiguationData":[TD([[makeQuery(id+"F0.imprint","IMPRINT",EDGE,{"derivedFrom":sQuery(id+"F0.wireOp",EDGE,"E113")}),1.0]])]});
            var Q61;
            Q61=makeQuery(id+"F0.imprint","IMPRINT",FACE,{"disambiguationData":[TD([[makeQuery(id+"F0.imprint","IMPRINT",EDGE,{"derivedFrom":sQuery(id+"F0.wireOp",EDGE,"E99")}),1.0]])]});
            var Q62;
            Q62=makeQuery(id+"F0.imprint","IMPRINT",FACE,{"disambiguationData":[TD([[makeQuery(id+"F0.imprint","IMPRINT",EDGE,{"derivedFrom":sQuery(id+"F0.wireOp",EDGE,"E39")}),1.0]])]});
            var Q63;
            Q63=makeQuery(id+"F0.imprint","IMPRINT",FACE,{"disambiguationData":[TD([[makeQuery(id+"F0.imprint","IMPRINT",EDGE,{"derivedFrom":sQuery(id+"F0.wireOp",EDGE,"E30")}),1.0]])]});
            var Q64;
            Q64=makeQuery(id+"F0.imprint","IMPRINT",FACE,{"disambiguationData":[TD([[makeQuery(id+"F0.imprint","IMPRINT",EDGE,{"derivedFrom":sQuery(id+"F0.wireOp",EDGE,"E19")}),1.0]])]});
            var Q65;
            Q65=makeQuery(id+"F0.imprint","IMPRINT",FACE,{"disambiguationData":[TD([[makeQuery(id+"F0.imprint","IMPRINT",EDGE,{"derivedFrom":sQuery(id+"F0.wireOp",EDGE,"E16")}),1.0]])]});
            var Q66;
            Q66=makeQuery(id+"F0.imprint","IMPRINT",FACE,{"disambiguationData":[TD([[makeQuery(id+"F0.imprint","IMPRINT",EDGE,{"derivedFrom":sQuery(id+"F0.wireOp",EDGE,"E9")}),1.0]])]});
            var Q67;
            Q67=makeQuery(id+"F0.imprint","IMPRINT",FACE,{"disambiguationData":[TD([[makeQuery(id+"F0.imprint","IMPRINT",EDGE,{"derivedFrom":sQuery(id+"F0.wireOp",EDGE,"E8")}),1.0]])]});
            var Q68;
            Q68=makeQuery(id+"F0.imprint","IMPRINT",FACE,{"disambiguationData":[TD([[makeQuery(id+"F0.imprint","IMPRINT",EDGE,{"derivedFrom":sQuery(id+"F0.wireOp",EDGE,"E17")}),1.0]])]});
            var Q69;
            Q69=makeQuery(id+"F0.imprint","IMPRINT",FACE,{"disambiguationData":[TD([[makeQuery(id+"F0.imprint","IMPRINT",EDGE,{"derivedFrom":sQuery(id+"F0.wireOp",EDGE,"E29")}),1.0]])]});
            var Q70;
            Q70=makeQuery(id+"F0.imprint","IMPRINT",FACE,{"disambiguationData":[TD([[makeQuery(id+"F0.imprint","IMPRINT",EDGE,{"derivedFrom":sQuery(id+"F0.wireOp",EDGE,"E40")}),1.0]])]});
            var Q71;
            Q71=makeQuery(id+"F0.imprint","IMPRINT",FACE,{"disambiguationData":[TD([[makeQuery(id+"F0.imprint","IMPRINT",EDGE,{"derivedFrom":sQuery(id+"F0.wireOp",EDGE,"E98")}),1.0]])]});
            var Q72;
            Q72=makeQuery(id+"F0.imprint","IMPRINT",FACE,{"disambiguationData":[TD([[makeQuery(id+"F0.imprint","IMPRINT",EDGE,{"derivedFrom":sQuery(id+"F0.wireOp",EDGE,"E121")}),1.0]])]});
            var Q73;
            Q73=makeQuery(id+"F0.imprint","IMPRINT",FACE,{"disambiguationData":[TD([[makeQuery(id+"F0.imprint","IMPRINT",EDGE,{"derivedFrom":sQuery(id+"F0.wireOp",EDGE,"E125")}),1.0]])]});
            var Q74;
            Q74=makeQuery(id+"F0.imprint","IMPRINT",FACE,{"disambiguationData":[TD([[makeQuery(id+"F0.imprint","IMPRINT",EDGE,{"derivedFrom":sQuery(id+"F0.wireOp",EDGE,"E127")}),1.0]])]});
            var Q75;
            Q75=makeQuery(id+"F0.imprint","IMPRINT",FACE,{"disambiguationData":[TD([[makeQuery(id+"F0.imprint","IMPRINT",EDGE,{"derivedFrom":sQuery(id+"F0.wireOp",EDGE,"E124")}),1.0]])]});
            var Q76;
            Q76=makeQuery(id+"F0.imprint","IMPRINT",FACE,{"disambiguationData":[TD([[makeQuery(id+"F0.imprint","IMPRINT",EDGE,{"derivedFrom":sQuery(id+"F0.wireOp",EDGE,"E122")}),1.0]])]});
            var Q77;
            Q77=makeQuery(id+"F0.imprint","IMPRINT",FACE,{"disambiguationData":[TD([[makeQuery(id+"F0.imprint","IMPRINT",EDGE,{"derivedFrom":sQuery(id+"F0.wireOp",EDGE,"E120")}),1.0]])]});
            var Q78;
            Q78=makeQuery(id+"F0.imprint","IMPRINT",FACE,{"disambiguationData":[TD([[makeQuery(id+"F0.imprint","IMPRINT",EDGE,{"derivedFrom":sQuery(id+"F0.wireOp",EDGE,"E97")}),1.0]])]});
            var Q79;
            Q79=makeQuery(id+"F0.imprint","IMPRINT",FACE,{"disambiguationData":[TD([[makeQuery(id+"F0.imprint","IMPRINT",EDGE,{"derivedFrom":sQuery(id+"F0.wireOp",EDGE,"E41")}),1.0]])]});
            var Q80;
            Q80=makeQuery(id+"F0.imprint","IMPRINT",FACE,{"disambiguationData":[TD([[makeQuery(id+"F0.imprint","IMPRINT",EDGE,{"derivedFrom":sQuery(id+"F0.wireOp",EDGE,"E28")}),1.0]])]});
            var Q81;
            Q81=makeQuery(id+"F0.imprint","IMPRINT",FACE,{"disambiguationData":[TD([[makeQuery(id+"F0.imprint","IMPRINT",EDGE,{"derivedFrom":sQuery(id+"F0.wireOp",EDGE,"E27")}),1.0]])]});
            var Q82;
            Q82=makeQuery(id+"F0.imprint","IMPRINT",FACE,{"disambiguationData":[TD([[makeQuery(id+"F0.imprint","IMPRINT",EDGE,{"derivedFrom":sQuery(id+"F0.wireOp",EDGE,"E26")}),1.0]])]});
            var Q83;
            Q83=makeQuery(id+"F0.imprint","IMPRINT",FACE,{"disambiguationData":[TD([[makeQuery(id+"F0.imprint","IMPRINT",EDGE,{"derivedFrom":sQuery(id+"F0.wireOp",EDGE,"E7")}),1.0]])]});
            var Q84;
            Q84=makeQuery(id+"F0.imprint","IMPRINT",FACE,{"disambiguationData":[TD([[makeQuery(id+"F0.imprint","IMPRINT",EDGE,{"derivedFrom":sQuery(id+"F0.wireOp",EDGE,"E103")}),1.0]])]});
            var Q85;
            Q85=makeQuery(id+"F0.imprint","IMPRINT",FACE,{"disambiguationData":[TD([[makeQuery(id+"F0.imprint","IMPRINT",EDGE,{"derivedFrom":sQuery(id+"F0.wireOp",EDGE,"E35")}),1.0]])]});
            var Q86;
            Q86=makeQuery(id+"F0.imprint","IMPRINT",FACE,{"disambiguationData":[TD([[makeQuery(id+"F0.imprint","IMPRINT",EDGE,{"derivedFrom":sQuery(id+"F0.wireOp",EDGE,"E31")}),1.0]])]});
            var Q87;
            Q87=makeQuery(id+"F0.imprint","IMPRINT",FACE,{"disambiguationData":[TD([[makeQuery(id+"F0.imprint","IMPRINT",EDGE,{"derivedFrom":sQuery(id+"F0.wireOp",EDGE,"E111")}),1.0]])]});
            var Q88;
            Q88=makeQuery(id+"F0.imprint","IMPRINT",FACE,{"disambiguationData":[TD([[makeQuery(id+"F0.imprint","IMPRINT",EDGE,{"derivedFrom":sQuery(id+"F0.wireOp",EDGE,"E18")}),1.0]])]});
            var Q89;
            Q89=makeQuery(id+"F0.imprint","IMPRINT",FACE,{"disambiguationData":[TD([[makeQuery(id+"F0.imprint","IMPRINT",EDGE,{"derivedFrom":sQuery(id+"F0.wireOp",EDGE,"E123")}),1.0]])]});
            var Q90;
            Q90=makeQuery(id+"F0.imprint","IMPRINT",FACE,{"disambiguationData":[TD([[makeQuery(id+"F0.imprint","IMPRINT",EDGE,{"derivedFrom":sQuery(id+"F0.wireOp",EDGE,"E130")}),1.0]])]});
            var Q91;
            Q91=makeQuery(id+"F0.imprint","IMPRINT",FACE,{"disambiguationData":[TD([[makeQuery(id+"F0.imprint","IMPRINT",EDGE,{"derivedFrom":sQuery(id+"F0.wireOp",EDGE,"E126")}),1.0]])]});
            extrude(context, id + "F15", {"entities" : qUnion([Q0, Q1, Q2, Q3, Q4, Q5, Q6, Q7, Q8, Q9, Q10, Q11, Q12, Q13, Q14, Q15, Q16, Q17, Q18, Q19, Q20, Q21, Q22, Q23, Q24, Q25, Q26, Q27, Q28, Q29, Q30, Q31, Q32, Q33, Q34, Q35, Q36, Q37, Q38, Q39, Q40, Q41, Q42, Q43, Q44, Q45, Q46, Q47, Q48, Q49, Q50, Q51, Q52, Q53, Q54, Q55, Q56, Q57, Q58, Q59, Q60, Q61, Q62, Q63, Q64, Q65, Q66, Q67, Q68, Q69, Q70, Q71, Q72, Q73, Q74, Q75, Q76, Q77, Q78, Q79, Q80, Q81, Q82, Q83, Q84, Q85, Q86, Q87, Q88, Q89, Q90, Q91]), "endBound" : BoundingType.SYMMETRIC, "depth" : 25 * mm, "offsetDistance" : 25 * mm, "hasDraft" : true, "draftAngle" : 1 * degree});
        }
        {
            var Q0;
            Q0=makeQuery(id+"F15.*.split.splitOp","SPLIT",BODY,{"derivedFrom":makeQuery(id+"F15.opExtrude","SWEPT_BODY",BODY,{"disambiguationData":[OSD([sQuery(id+"F0.wireOp",EDGE,"E169")])]})});
            var Q1;
            Q1=makeQuery(id+"F15.*.split.splitOp","SPLIT",BODY,{"derivedFrom":makeQuery(id+"F15.opExtrude","SWEPT_BODY",BODY,{"disambiguationData":[OSD([sQuery(id+"F0.wireOp",EDGE,"E139")])]})});
            var Q2;
            Q2=makeQuery(id+"F15.*.split.splitOp","SPLIT",BODY,{"derivedFrom":makeQuery(id+"F15.opExtrude","SWEPT_BODY",BODY,{"disambiguationData":[OSD([sQuery(id+"F0.wireOp",EDGE,"E140")])]})});
            var Q3;
            Q3=makeQuery(id+"F15.*.split.splitOp","SPLIT",BODY,{"derivedFrom":makeQuery(id+"F15.opExtrude","SWEPT_BODY",BODY,{"disambiguationData":[OSD([sQuery(id+"F0.wireOp",EDGE,"E141")])]})});
            var Q4;
            Q4=makeQuery(id+"F15.*.split.splitOp","SPLIT",BODY,{"derivedFrom":makeQuery(id+"F15.opExtrude","SWEPT_BODY",BODY,{"disambiguationData":[OSD([sQuery(id+"F0.wireOp",EDGE,"E135")])]})});
            var Q5;
            Q5=makeQuery(id+"F15.*.split.splitOp","SPLIT",BODY,{"derivedFrom":makeQuery(id+"F15.opExtrude","SWEPT_BODY",BODY,{"disambiguationData":[OSD([sQuery(id+"F0.wireOp",EDGE,"E132")])]})});
            var Q6;
            Q6=makeQuery(id+"F15.*.split.splitOp","SPLIT",BODY,{"derivedFrom":makeQuery(id+"F15.opExtrude","SWEPT_BODY",BODY,{"disambiguationData":[OSD([sQuery(id+"F0.wireOp",EDGE,"E131")])]})});
            var Q7;
            Q7=makeQuery(id+"F15.*.split.splitOp","SPLIT",BODY,{"derivedFrom":makeQuery(id+"F15.opExtrude","SWEPT_BODY",BODY,{"disambiguationData":[OSD([sQuery(id+"F0.wireOp",EDGE,"E128")])]})});
            var Q8;
            Q8=makeQuery(id+"F15.*.split.splitOp","SPLIT",BODY,{"derivedFrom":makeQuery(id+"F15.opExtrude","SWEPT_BODY",BODY,{"disambiguationData":[OSD([sQuery(id+"F0.wireOp",EDGE,"E127")])]})});
            var Q9;
            Q9=makeQuery(id+"F15.*.split.splitOp","SPLIT",BODY,{"derivedFrom":makeQuery(id+"F15.opExtrude","SWEPT_BODY",BODY,{"disambiguationData":[OSD([sQuery(id+"F0.wireOp",EDGE,"E126")])]})});
            var Q10;
            Q10=makeQuery(id+"F15.*.split.splitOp","SPLIT",BODY,{"derivedFrom":makeQuery(id+"F15.opExtrude","SWEPT_BODY",BODY,{"disambiguationData":[OSD([sQuery(id+"F0.wireOp",EDGE,"E124")])]})});
            var Q11;
            Q11=makeQuery(id+"F15.*.split.splitOp","SPLIT",BODY,{"derivedFrom":makeQuery(id+"F15.opExtrude","SWEPT_BODY",BODY,{"disambiguationData":[OSD([sQuery(id+"F0.wireOp",EDGE,"E125")])]})});
            var Q12;
            Q12=makeQuery(id+"F15.*.split.splitOp","SPLIT",BODY,{"derivedFrom":makeQuery(id+"F15.opExtrude","SWEPT_BODY",BODY,{"disambiguationData":[OSD([sQuery(id+"F0.wireOp",EDGE,"E129")])]})});
            var Q13;
            Q13=makeQuery(id+"F15.*.split.splitOp","SPLIT",BODY,{"derivedFrom":makeQuery(id+"F15.opExtrude","SWEPT_BODY",BODY,{"disambiguationData":[OSD([sQuery(id+"F0.wireOp",EDGE,"E130")])]})});
            var Q14;
            Q14=makeQuery(id+"F15.*.split.splitOp","SPLIT",BODY,{"derivedFrom":makeQuery(id+"F15.opExtrude","SWEPT_BODY",BODY,{"disambiguationData":[OSD([sQuery(id+"F0.wireOp",EDGE,"E133")])]})});
            var Q15;
            Q15=makeQuery(id+"F15.*.split.splitOp","SPLIT",BODY,{"derivedFrom":makeQuery(id+"F15.opExtrude","SWEPT_BODY",BODY,{"disambiguationData":[OSD([sQuery(id+"F0.wireOp",EDGE,"E134")])]})});
            var Q16;
            Q16=makeQuery(id+"F15.*.split.splitOp","SPLIT",BODY,{"derivedFrom":makeQuery(id+"F15.opExtrude","SWEPT_BODY",BODY,{"disambiguationData":[OSD([sQuery(id+"F0.wireOp",EDGE,"E136")])]})});
            var Q17;
            Q17=makeQuery(id+"F15.*.split.splitOp","SPLIT",BODY,{"derivedFrom":makeQuery(id+"F15.opExtrude","SWEPT_BODY",BODY,{"disambiguationData":[OSD([sQuery(id+"F0.wireOp",EDGE,"E137")])]})});
            var Q18;
            Q18=makeQuery(id+"F15.*.split.splitOp","SPLIT",BODY,{"derivedFrom":makeQuery(id+"F15.opExtrude","SWEPT_BODY",BODY,{"disambiguationData":[OSD([sQuery(id+"F0.wireOp",EDGE,"E138")])]})});
            var Q19;
            Q19=makeQuery(id+"F15.*.split.splitOp","SPLIT",BODY,{"derivedFrom":makeQuery(id+"F15.opExtrude","SWEPT_BODY",BODY,{"disambiguationData":[OSD([sQuery(id+"F0.wireOp",EDGE,"E119")])]})});
            var Q20;
            Q20=makeQuery(id+"F15.*.split.splitOp","SPLIT",BODY,{"derivedFrom":makeQuery(id+"F15.opExtrude","SWEPT_BODY",BODY,{"disambiguationData":[OSD([sQuery(id+"F0.wireOp",EDGE,"E118")])]})});
            var Q21;
            Q21=makeQuery(id+"F15.*.split.splitOp","SPLIT",BODY,{"derivedFrom":makeQuery(id+"F15.opExtrude","SWEPT_BODY",BODY,{"disambiguationData":[OSD([sQuery(id+"F0.wireOp",EDGE,"E117")])]})});
            var Q22;
            Q22=makeQuery(id+"F15.*.split.splitOp","SPLIT",BODY,{"derivedFrom":makeQuery(id+"F15.opExtrude","SWEPT_BODY",BODY,{"disambiguationData":[OSD([sQuery(id+"F0.wireOp",EDGE,"E116")])]})});
            var Q23;
            Q23=makeQuery(id+"F15.*.split.splitOp","SPLIT",BODY,{"derivedFrom":makeQuery(id+"F15.opExtrude","SWEPT_BODY",BODY,{"disambiguationData":[OSD([sQuery(id+"F0.wireOp",EDGE,"E115")])]})});
            var Q24;
            Q24=makeQuery(id+"F15.*.split.splitOp","SPLIT",BODY,{"derivedFrom":makeQuery(id+"F15.opExtrude","SWEPT_BODY",BODY,{"disambiguationData":[OSD([sQuery(id+"F0.wireOp",EDGE,"E114")])]})});
            var Q25;
            Q25=makeQuery(id+"F15.*.split.splitOp","SPLIT",BODY,{"derivedFrom":makeQuery(id+"F15.opExtrude","SWEPT_BODY",BODY,{"disambiguationData":[OSD([sQuery(id+"F0.wireOp",EDGE,"E113")])]})});
            var Q26;
            Q26=makeQuery(id+"F15.*.split.splitOp","SPLIT",BODY,{"derivedFrom":makeQuery(id+"F15.opExtrude","SWEPT_BODY",BODY,{"disambiguationData":[OSD([sQuery(id+"F0.wireOp",EDGE,"E123")])]})});
            var Q27;
            Q27=makeQuery(id+"F15.*.split.splitOp","SPLIT",BODY,{"derivedFrom":makeQuery(id+"F15.opExtrude","SWEPT_BODY",BODY,{"disambiguationData":[OSD([sQuery(id+"F0.wireOp",EDGE,"E122")])]})});
            var Q28;
            Q28=makeQuery(id+"F15.*.split.splitOp","SPLIT",BODY,{"derivedFrom":makeQuery(id+"F15.opExtrude","SWEPT_BODY",BODY,{"disambiguationData":[OSD([sQuery(id+"F0.wireOp",EDGE,"E120")])]})});
            var Q29;
            Q29=makeQuery(id+"F15.*.split.splitOp","SPLIT",BODY,{"derivedFrom":makeQuery(id+"F15.opExtrude","SWEPT_BODY",BODY,{"disambiguationData":[OSD([sQuery(id+"F0.wireOp",EDGE,"E121")])]})});
            var Q30;
            Q30=makeQuery(id+"F15.*.split.splitOp","SPLIT",BODY,{"derivedFrom":makeQuery(id+"F15.opExtrude","SWEPT_BODY",BODY,{"disambiguationData":[OSD([sQuery(id+"F0.wireOp",EDGE,"E111")])]})});
            var Q31;
            Q31=makeQuery(id+"F15.*.split.splitOp","SPLIT",BODY,{"derivedFrom":makeQuery(id+"F15.opExtrude","SWEPT_BODY",BODY,{"disambiguationData":[OSD([sQuery(id+"F0.wireOp",EDGE,"E112")])]})});
            var Q32;
            Q32=makeQuery(id+"F15.*.split.splitOp","SPLIT",BODY,{"derivedFrom":makeQuery(id+"F15.opExtrude","SWEPT_BODY",BODY,{"disambiguationData":[OSD([sQuery(id+"F0.wireOp",EDGE,"E107")])]})});
            var Q33;
            Q33=makeQuery(id+"F15.*.split.splitOp","SPLIT",BODY,{"derivedFrom":makeQuery(id+"F15.opExtrude","SWEPT_BODY",BODY,{"disambiguationData":[OSD([sQuery(id+"F0.wireOp",EDGE,"E108")])]})});
            var Q34;
            Q34=makeQuery(id+"F15.*.split.splitOp","SPLIT",BODY,{"derivedFrom":makeQuery(id+"F15.opExtrude","SWEPT_BODY",BODY,{"disambiguationData":[OSD([sQuery(id+"F0.wireOp",EDGE,"E109")])]})});
            var Q35;
            Q35=makeQuery(id+"F15.*.split.splitOp","SPLIT",BODY,{"derivedFrom":makeQuery(id+"F15.opExtrude","SWEPT_BODY",BODY,{"disambiguationData":[OSD([sQuery(id+"F0.wireOp",EDGE,"E110")])]})});
            var Q36;
            Q36=makeQuery(id+"F15.*.split.splitOp","SPLIT",BODY,{"derivedFrom":makeQuery(id+"F15.opExtrude","SWEPT_BODY",BODY,{"disambiguationData":[OSD([sQuery(id+"F0.wireOp",EDGE,"E106")])]})});
            var Q37;
            Q37=makeQuery(id+"F15.*.split.splitOp","SPLIT",BODY,{"derivedFrom":makeQuery(id+"F15.opExtrude","SWEPT_BODY",BODY,{"disambiguationData":[OSD([sQuery(id+"F0.wireOp",EDGE,"E105")])]})});
            var Q38;
            Q38=makeQuery(id+"F15.*.split.splitOp","SPLIT",BODY,{"derivedFrom":makeQuery(id+"F15.opExtrude","SWEPT_BODY",BODY,{"disambiguationData":[OSD([sQuery(id+"F0.wireOp",EDGE,"E104")])]})});
            var Q39;
            Q39=makeQuery(id+"F15.*.split.splitOp","SPLIT",BODY,{"derivedFrom":makeQuery(id+"F15.opExtrude","SWEPT_BODY",BODY,{"disambiguationData":[OSD([sQuery(id+"F0.wireOp",EDGE,"E103")])]})});
            var Q40;
            Q40=makeQuery(id+"F15.*.split.splitOp","SPLIT",BODY,{"derivedFrom":makeQuery(id+"F15.opExtrude","SWEPT_BODY",BODY,{"disambiguationData":[OSD([sQuery(id+"F0.wireOp",EDGE,"E102")])]})});
            var Q41;
            Q41=makeQuery(id+"F15.*.split.splitOp","SPLIT",BODY,{"derivedFrom":makeQuery(id+"F15.opExtrude","SWEPT_BODY",BODY,{"disambiguationData":[OSD([sQuery(id+"F0.wireOp",EDGE,"E101")])]})});
            var Q42;
            Q42=makeQuery(id+"F15.*.split.splitOp","SPLIT",BODY,{"derivedFrom":makeQuery(id+"F15.opExtrude","SWEPT_BODY",BODY,{"disambiguationData":[OSD([sQuery(id+"F0.wireOp",EDGE,"E100")])]})});
            var Q43;
            Q43=makeQuery(id+"F15.*.split.splitOp","SPLIT",BODY,{"derivedFrom":makeQuery(id+"F15.opExtrude","SWEPT_BODY",BODY,{"disambiguationData":[OSD([sQuery(id+"F0.wireOp",EDGE,"E99")])]})});
            var Q44;
            Q44=makeQuery(id+"F15.*.split.splitOp","SPLIT",BODY,{"derivedFrom":makeQuery(id+"F15.opExtrude","SWEPT_BODY",BODY,{"disambiguationData":[OSD([sQuery(id+"F0.wireOp",EDGE,"E98")])]})});
            var Q45;
            Q45=makeQuery(id+"F15.*.split.splitOp","SPLIT",BODY,{"derivedFrom":makeQuery(id+"F15.opExtrude","SWEPT_BODY",BODY,{"disambiguationData":[OSD([sQuery(id+"F0.wireOp",EDGE,"E97")])]})});
            var Q46;
            Q46=makeQuery(id+"F15.*.split.splitOp","SPLIT",BODY,{"derivedFrom":makeQuery(id+"F15.opExtrude","SWEPT_BODY",BODY,{"disambiguationData":[OSD([sQuery(id+"F0.wireOp",EDGE,"E41")])]})});
            var Q47;
            Q47=makeQuery(id+"F15.*.split.splitOp","SPLIT",BODY,{"derivedFrom":makeQuery(id+"F15.opExtrude","SWEPT_BODY",BODY,{"disambiguationData":[OSD([sQuery(id+"F0.wireOp",EDGE,"E40")])]})});
            var Q48;
            Q48=makeQuery(id+"F15.*.split.splitOp","SPLIT",BODY,{"derivedFrom":makeQuery(id+"F15.opExtrude","SWEPT_BODY",BODY,{"disambiguationData":[OSD([sQuery(id+"F0.wireOp",EDGE,"E39")])]})});
            var Q49;
            Q49=makeQuery(id+"F15.*.split.splitOp","SPLIT",BODY,{"derivedFrom":makeQuery(id+"F15.opExtrude","SWEPT_BODY",BODY,{"disambiguationData":[OSD([sQuery(id+"F0.wireOp",EDGE,"E38")])]})});
            var Q50;
            Q50=makeQuery(id+"F15.*.split.splitOp","SPLIT",BODY,{"derivedFrom":makeQuery(id+"F15.opExtrude","SWEPT_BODY",BODY,{"disambiguationData":[OSD([sQuery(id+"F0.wireOp",EDGE,"E37")])]})});
            var Q51;
            Q51=makeQuery(id+"F15.*.split.splitOp","SPLIT",BODY,{"derivedFrom":makeQuery(id+"F15.opExtrude","SWEPT_BODY",BODY,{"disambiguationData":[OSD([sQuery(id+"F0.wireOp",EDGE,"E36")])]})});
            var Q52;
            Q52=makeQuery(id+"F15.*.split.splitOp","SPLIT",BODY,{"derivedFrom":makeQuery(id+"F15.opExtrude","SWEPT_BODY",BODY,{"disambiguationData":[OSD([sQuery(id+"F0.wireOp",EDGE,"E35")])]})});
            var Q53;
            Q53=makeQuery(id+"F15.*.split.splitOp","SPLIT",BODY,{"derivedFrom":makeQuery(id+"F15.opExtrude","SWEPT_BODY",BODY,{"disambiguationData":[OSD([sQuery(id+"F0.wireOp",EDGE,"E86")])]})});
            var Q54;
            Q54=makeQuery(id+"F15.*.split.splitOp","SPLIT",BODY,{"derivedFrom":makeQuery(id+"F15.opExtrude","SWEPT_BODY",BODY,{"disambiguationData":[OSD([sQuery(id+"F0.wireOp",EDGE,"E84")])]})});
            var Q55;
            Q55=makeQuery(id+"F15.*.split.splitOp","SPLIT",BODY,{"derivedFrom":makeQuery(id+"F15.opExtrude","SWEPT_BODY",BODY,{"disambiguationData":[OSD([sQuery(id+"F0.wireOp",EDGE,"E85")])]})});
            var Q56;
            Q56=makeQuery(id+"F15.*.split.splitOp","SPLIT",BODY,{"derivedFrom":makeQuery(id+"F15.opExtrude","SWEPT_BODY",BODY,{"disambiguationData":[OSD([sQuery(id+"F0.wireOp",EDGE,"E34")])]})});
            var Q57;
            Q57=makeQuery(id+"F15.*.split.splitOp","SPLIT",BODY,{"derivedFrom":makeQuery(id+"F15.opExtrude","SWEPT_BODY",BODY,{"disambiguationData":[OSD([sQuery(id+"F0.wireOp",EDGE,"E33")])]})});
            var Q58;
            Q58=makeQuery(id+"F15.*.split.splitOp","SPLIT",BODY,{"derivedFrom":makeQuery(id+"F15.opExtrude","SWEPT_BODY",BODY,{"disambiguationData":[OSD([sQuery(id+"F0.wireOp",EDGE,"E32")])]})});
            var Q59;
            Q59=makeQuery(id+"F15.*.split.splitOp","SPLIT",BODY,{"derivedFrom":makeQuery(id+"F15.opExtrude","SWEPT_BODY",BODY,{"disambiguationData":[OSD([sQuery(id+"F0.wireOp",EDGE,"E31")])]})});
            var Q60;
            Q60=makeQuery(id+"F15.*.split.splitOp","SPLIT",BODY,{"derivedFrom":makeQuery(id+"F15.opExtrude","SWEPT_BODY",BODY,{"disambiguationData":[OSD([sQuery(id+"F0.wireOp",EDGE,"E30")])]})});
            var Q61;
            Q61=makeQuery(id+"F15.*.split.splitOp","SPLIT",BODY,{"derivedFrom":makeQuery(id+"F15.opExtrude","SWEPT_BODY",BODY,{"disambiguationData":[OSD([sQuery(id+"F0.wireOp",EDGE,"E29")])]})});
            var Q62;
            Q62=makeQuery(id+"F15.*.split.splitOp","SPLIT",BODY,{"derivedFrom":makeQuery(id+"F15.opExtrude","SWEPT_BODY",BODY,{"disambiguationData":[OSD([sQuery(id+"F0.wireOp",EDGE,"E28")])]})});
            var Q63;
            Q63=makeQuery(id+"F15.*.split.splitOp","SPLIT",BODY,{"derivedFrom":makeQuery(id+"F15.opExtrude","SWEPT_BODY",BODY,{"disambiguationData":[OSD([sQuery(id+"F0.wireOp",EDGE,"E27")])]})});
            var Q64;
            Q64=makeQuery(id+"F15.*.split.splitOp","SPLIT",BODY,{"derivedFrom":makeQuery(id+"F15.opExtrude","SWEPT_BODY",BODY,{"disambiguationData":[OSD([sQuery(id+"F0.wireOp",EDGE,"E18")])]})});
            var Q65;
            Q65=makeQuery(id+"F15.*.split.splitOp","SPLIT",BODY,{"derivedFrom":makeQuery(id+"F15.opExtrude","SWEPT_BODY",BODY,{"disambiguationData":[OSD([sQuery(id+"F0.wireOp",EDGE,"E19")])]})});
            var Q66;
            Q66=makeQuery(id+"F15.*.split.splitOp","SPLIT",BODY,{"derivedFrom":makeQuery(id+"F15.opExtrude","SWEPT_BODY",BODY,{"disambiguationData":[OSD([sQuery(id+"F0.wireOp",EDGE,"E20")])]})});
            var Q67;
            Q67=makeQuery(id+"F15.*.split.splitOp","SPLIT",BODY,{"derivedFrom":makeQuery(id+"F15.opExtrude","SWEPT_BODY",BODY,{"disambiguationData":[OSD([sQuery(id+"F0.wireOp",EDGE,"E21")])]})});
            var Q68;
            Q68=makeQuery(id+"F15.*.split.splitOp","SPLIT",BODY,{"derivedFrom":makeQuery(id+"F15.opExtrude","SWEPT_BODY",BODY,{"disambiguationData":[OSD([sQuery(id+"F0.wireOp",EDGE,"E22")])]})});
            var Q69;
            Q69=makeQuery(id+"F15.*.split.splitOp","SPLIT",BODY,{"derivedFrom":makeQuery(id+"F15.opExtrude","SWEPT_BODY",BODY,{"disambiguationData":[OSD([sQuery(id+"F0.wireOp",EDGE,"E25")])]})});
            var Q70;
            Q70=makeQuery(id+"F15.*.split.splitOp","SPLIT",BODY,{"derivedFrom":makeQuery(id+"F15.opExtrude","SWEPT_BODY",BODY,{"disambiguationData":[OSD([sQuery(id+"F0.wireOp",EDGE,"E45")])]})});
            var Q71;
            Q71=makeQuery(id+"F15.*.split.splitOp","SPLIT",BODY,{"derivedFrom":makeQuery(id+"F15.opExtrude","SWEPT_BODY",BODY,{"disambiguationData":[OSD([sQuery(id+"F0.wireOp",EDGE,"E47")])]})});
            var Q72;
            Q72=makeQuery(id+"F15.*.split.splitOp","SPLIT",BODY,{"derivedFrom":makeQuery(id+"F15.opExtrude","SWEPT_BODY",BODY,{"disambiguationData":[OSD([sQuery(id+"F0.wireOp",EDGE,"E46")])]})});
            var Q73;
            Q73=makeQuery(id+"F15.*.split.splitOp","SPLIT",BODY,{"derivedFrom":makeQuery(id+"F15.opExtrude","SWEPT_BODY",BODY,{"disambiguationData":[OSD([sQuery(id+"F0.wireOp",EDGE,"E44")])]})});
            var Q74;
            Q74=makeQuery(id+"F15.*.split.splitOp","SPLIT",BODY,{"derivedFrom":makeQuery(id+"F15.opExtrude","SWEPT_BODY",BODY,{"disambiguationData":[OSD([sQuery(id+"F0.wireOp",EDGE,"E24")])]})});
            var Q75;
            Q75=makeQuery(id+"F15.*.split.splitOp","SPLIT",BODY,{"derivedFrom":makeQuery(id+"F15.opExtrude","SWEPT_BODY",BODY,{"disambiguationData":[OSD([sQuery(id+"F0.wireOp",EDGE,"E13")])]})});
            var Q76;
            Q76=makeQuery(id+"F15.*.split.splitOp","SPLIT",BODY,{"derivedFrom":makeQuery(id+"F15.opExtrude","SWEPT_BODY",BODY,{"disambiguationData":[OSD([sQuery(id+"F0.wireOp",EDGE,"E14")])]})});
            var Q77;
            Q77=makeQuery(id+"F15.*.split.splitOp","SPLIT",BODY,{"derivedFrom":makeQuery(id+"F15.opExtrude","SWEPT_BODY",BODY,{"disambiguationData":[OSD([sQuery(id+"F0.wireOp",EDGE,"E15")])]})});
            var Q78;
            Q78=makeQuery(id+"F15.*.split.splitOp","SPLIT",BODY,{"derivedFrom":makeQuery(id+"F15.opExtrude","SWEPT_BODY",BODY,{"disambiguationData":[OSD([sQuery(id+"F0.wireOp",EDGE,"E16")])]})});
            var Q79;
            Q79=makeQuery(id+"F15.*.split.splitOp","SPLIT",BODY,{"derivedFrom":makeQuery(id+"F15.opExtrude","SWEPT_BODY",BODY,{"disambiguationData":[OSD([sQuery(id+"F0.wireOp",EDGE,"E17")])]})});
            var Q80;
            Q80=makeQuery(id+"F15.*.split.splitOp","SPLIT",BODY,{"derivedFrom":makeQuery(id+"F15.opExtrude","SWEPT_BODY",BODY,{"disambiguationData":[OSD([sQuery(id+"F0.wireOp",EDGE,"E26")])]})});
            var Q81;
            Q81=makeQuery(id+"F15.*.split.splitOp","SPLIT",BODY,{"derivedFrom":makeQuery(id+"F15.opExtrude","SWEPT_BODY",BODY,{"disambiguationData":[OSD([sQuery(id+"F0.wireOp",EDGE,"E8")])]})});
            var Q82;
            Q82=makeQuery(id+"F15.*.split.splitOp","SPLIT",BODY,{"derivedFrom":makeQuery(id+"F15.opExtrude","SWEPT_BODY",BODY,{"disambiguationData":[OSD([sQuery(id+"F0.wireOp",EDGE,"E9")])]})});
            var Q83;
            Q83=makeQuery(id+"F15.*.split.splitOp","SPLIT",BODY,{"derivedFrom":makeQuery(id+"F15.opExtrude","SWEPT_BODY",BODY,{"disambiguationData":[OSD([sQuery(id+"F0.wireOp",EDGE,"E10")])]})});
            var Q84;
            Q84=makeQuery(id+"F15.*.split.splitOp","SPLIT",BODY,{"derivedFrom":makeQuery(id+"F15.opExtrude","SWEPT_BODY",BODY,{"disambiguationData":[OSD([sQuery(id+"F0.wireOp",EDGE,"E11")])]})});
            var Q85;
            Q85=makeQuery(id+"F15.*.split.splitOp","SPLIT",BODY,{"derivedFrom":makeQuery(id+"F15.opExtrude","SWEPT_BODY",BODY,{"disambiguationData":[OSD([sQuery(id+"F0.wireOp",EDGE,"E23")])]})});
            var Q86;
            Q86=makeQuery(id+"F15.*.split.splitOp","SPLIT",BODY,{"derivedFrom":makeQuery(id+"F15.opExtrude","SWEPT_BODY",BODY,{"disambiguationData":[OSD([sQuery(id+"F0.wireOp",EDGE,"E42")])]})});
            var Q87;
            Q87=makeQuery(id+"F15.*.split.splitOp","SPLIT",BODY,{"derivedFrom":makeQuery(id+"F15.opExtrude","SWEPT_BODY",BODY,{"disambiguationData":[OSD([sQuery(id+"F0.wireOp",EDGE,"E43")])]})});
            var Q88;
            Q88=makeQuery(id+"F15.*.split.splitOp","SPLIT",BODY,{"derivedFrom":makeQuery(id+"F15.opExtrude","SWEPT_BODY",BODY,{"disambiguationData":[OSD([sQuery(id+"F0.wireOp",EDGE,"E7")])]})});
            var Q89;
            Q89=makeQuery(id+"F15.*.split.splitOp","SPLIT",BODY,{"derivedFrom":makeQuery(id+"F15.opExtrude","SWEPT_BODY",BODY,{"disambiguationData":[OSD([sQuery(id+"F0.wireOp",EDGE,"E12")])]})});
            var Q90;
            Q90=makeQuery(id+"F3.opExtrude","SWEPT_BODY",BODY,{"disambiguationData":[OSD([sQuery(id+"F1.wireOp",EDGE,"E206.0.8.0")])]});
            var Q91;
            Q91=makeQuery(id+"F3.opExtrude","SWEPT_BODY",BODY,{"disambiguationData":[OSD([sQuery(id+"F1.wireOp",EDGE,"E206.1.8.0")])]});
            var Q92;
            Q92=makeQuery(id+"F3.opExtrude","SWEPT_BODY",BODY,{"disambiguationData":[OSD([sQuery(id+"F1.wireOp",EDGE,"E206.2.8.0")])]});
            var Q93;
            Q93=makeQuery(id+"F3.opExtrude","SWEPT_BODY",BODY,{"disambiguationData":[OSD([sQuery(id+"F1.wireOp",EDGE,"E206.3.8.0")])]});
            var Q94;
            Q94=makeQuery(id+"F3.opExtrude","SWEPT_BODY",BODY,{"disambiguationData":[OSD([sQuery(id+"F1.wireOp",EDGE,"E206.4.8.0")])]});
            var Q95;
            Q95=makeQuery(id+"F3.opExtrude","SWEPT_BODY",BODY,{"disambiguationData":[OSD([sQuery(id+"F1.wireOp",EDGE,"E206.5.8.0")])]});
            var Q96;
            Q96=makeQuery(id+"F3.opExtrude","SWEPT_BODY",BODY,{"disambiguationData":[OSD([sQuery(id+"F1.wireOp",EDGE,"E206.6.8.0")])]});
            var Q97;
            Q97=makeQuery(id+"F3.opExtrude","SWEPT_BODY",BODY,{"disambiguationData":[OSD([sQuery(id+"F1.wireOp",EDGE,"E206.7.8.0")])]});
            var Q98;
            Q98=makeQuery(id+"F3.opExtrude","SWEPT_BODY",BODY,{"disambiguationData":[OSD([sQuery(id+"F1.wireOp",EDGE,"E206.8.8.0")])]});
            var Q99;
            Q99=makeQuery(id+"F3.opExtrude","SWEPT_BODY",BODY,{"disambiguationData":[OSD([sQuery(id+"F1.wireOp",EDGE,"E206.8.7.0")])]});
            var Q100;
            Q100=makeQuery(id+"F3.opExtrude","SWEPT_BODY",BODY,{"disambiguationData":[OSD([sQuery(id+"F1.wireOp",EDGE,"E206.7.7.0")])]});
            var Q101;
            Q101=makeQuery(id+"F3.opExtrude","SWEPT_BODY",BODY,{"disambiguationData":[OSD([sQuery(id+"F1.wireOp",EDGE,"E206.6.7.0")])]});
            var Q102;
            Q102=makeQuery(id+"F3.opExtrude","SWEPT_BODY",BODY,{"disambiguationData":[OSD([sQuery(id+"F1.wireOp",EDGE,"E206.5.7.0")])]});
            var Q103;
            Q103=makeQuery(id+"F3.opExtrude","SWEPT_BODY",BODY,{"disambiguationData":[OSD([sQuery(id+"F1.wireOp",EDGE,"E206.4.7.0")])]});
            var Q104;
            Q104=makeQuery(id+"F3.opExtrude","SWEPT_BODY",BODY,{"disambiguationData":[OSD([sQuery(id+"F1.wireOp",EDGE,"E206.3.7.0")])]});
            var Q105;
            Q105=makeQuery(id+"F3.opExtrude","SWEPT_BODY",BODY,{"disambiguationData":[OSD([sQuery(id+"F1.wireOp",EDGE,"E206.2.7.0")])]});
            var Q106;
            Q106=makeQuery(id+"F3.opExtrude","SWEPT_BODY",BODY,{"disambiguationData":[OSD([sQuery(id+"F1.wireOp",EDGE,"E206.1.7.0")])]});
            var Q107;
            Q107=makeQuery(id+"F3.opExtrude","SWEPT_BODY",BODY,{"disambiguationData":[OSD([sQuery(id+"F1.wireOp",EDGE,"E206.0.7.0")])]});
            var Q108;
            Q108=makeQuery(id+"F3.opExtrude","SWEPT_BODY",BODY,{"disambiguationData":[OSD([sQuery(id+"F1.wireOp",EDGE,"E206.0.6.0")])]});
            var Q109;
            Q109=makeQuery(id+"F3.opExtrude","SWEPT_BODY",BODY,{"disambiguationData":[OSD([sQuery(id+"F1.wireOp",EDGE,"E206.1.6.0")])]});
            var Q110;
            Q110=makeQuery(id+"F3.opExtrude","SWEPT_BODY",BODY,{"disambiguationData":[OSD([sQuery(id+"F1.wireOp",EDGE,"E206.2.6.0")])]});
            var Q111;
            Q111=makeQuery(id+"F3.opExtrude","SWEPT_BODY",BODY,{"disambiguationData":[OSD([sQuery(id+"F1.wireOp",EDGE,"E206.3.6.0")])]});
            var Q112;
            Q112=makeQuery(id+"F3.opExtrude","SWEPT_BODY",BODY,{"disambiguationData":[OSD([sQuery(id+"F1.wireOp",EDGE,"E206.4.6.0")])]});
            var Q113;
            Q113=makeQuery(id+"F3.opExtrude","SWEPT_BODY",BODY,{"disambiguationData":[OSD([sQuery(id+"F1.wireOp",EDGE,"E206.5.6.0")])]});
            var Q114;
            Q114=makeQuery(id+"F3.opExtrude","SWEPT_BODY",BODY,{"disambiguationData":[OSD([sQuery(id+"F1.wireOp",EDGE,"E206.6.6.0")])]});
            var Q115;
            Q115=makeQuery(id+"F3.opExtrude","SWEPT_BODY",BODY,{"disambiguationData":[OSD([sQuery(id+"F1.wireOp",EDGE,"E206.7.6.0")])]});
            var Q116;
            Q116=makeQuery(id+"F3.opExtrude","SWEPT_BODY",BODY,{"disambiguationData":[OSD([sQuery(id+"F1.wireOp",EDGE,"E206.8.6.0")])]});
            var Q117;
            Q117=makeQuery(id+"F3.opExtrude","SWEPT_BODY",BODY,{"disambiguationData":[OSD([sQuery(id+"F1.wireOp",EDGE,"E206.8.5.0")])]});
            var Q118;
            Q118=makeQuery(id+"F3.opExtrude","SWEPT_BODY",BODY,{"disambiguationData":[OSD([sQuery(id+"F1.wireOp",EDGE,"E206.7.5.0")])]});
            var Q119;
            Q119=makeQuery(id+"F3.opExtrude","SWEPT_BODY",BODY,{"disambiguationData":[OSD([sQuery(id+"F1.wireOp",EDGE,"E206.6.5.0")])]});
            var Q120;
            Q120=makeQuery(id+"F3.opExtrude","SWEPT_BODY",BODY,{"disambiguationData":[OSD([sQuery(id+"F1.wireOp",EDGE,"E206.5.5.0")])]});
            var Q121;
            Q121=makeQuery(id+"F3.opExtrude","SWEPT_BODY",BODY,{"disambiguationData":[OSD([sQuery(id+"F1.wireOp",EDGE,"E206.4.5.0")])]});
            var Q122;
            Q122=makeQuery(id+"F3.opExtrude","SWEPT_BODY",BODY,{"disambiguationData":[OSD([sQuery(id+"F1.wireOp",EDGE,"E206.3.5.0")])]});
            var Q123;
            Q123=makeQuery(id+"F3.opExtrude","SWEPT_BODY",BODY,{"disambiguationData":[OSD([sQuery(id+"F1.wireOp",EDGE,"E206.2.5.0")])]});
            var Q124;
            Q124=makeQuery(id+"F3.opExtrude","SWEPT_BODY",BODY,{"disambiguationData":[OSD([sQuery(id+"F1.wireOp",EDGE,"E206.1.5.0")])]});
            var Q125;
            Q125=makeQuery(id+"F3.opExtrude","SWEPT_BODY",BODY,{"disambiguationData":[OSD([sQuery(id+"F1.wireOp",EDGE,"E206.0.5.0")])]});
            var Q126;
            Q126=makeQuery(id+"F3.opExtrude","SWEPT_BODY",BODY,{"disambiguationData":[OSD([sQuery(id+"F1.wireOp",EDGE,"E206.0.4.0")])]});
            var Q127;
            Q127=makeQuery(id+"F3.opExtrude","SWEPT_BODY",BODY,{"disambiguationData":[OSD([sQuery(id+"F1.wireOp",EDGE,"E206.1.4.0")])]});
            var Q128;
            Q128=makeQuery(id+"F3.opExtrude","SWEPT_BODY",BODY,{"disambiguationData":[OSD([sQuery(id+"F1.wireOp",EDGE,"E206.2.4.0")])]});
            var Q129;
            Q129=makeQuery(id+"F3.opExtrude","SWEPT_BODY",BODY,{"disambiguationData":[OSD([sQuery(id+"F1.wireOp",EDGE,"E206.3.4.0")])]});
            var Q130;
            Q130=makeQuery(id+"F3.opExtrude","SWEPT_BODY",BODY,{"disambiguationData":[OSD([sQuery(id+"F1.wireOp",EDGE,"E206.4.4.0")])]});
            var Q131;
            Q131=makeQuery(id+"F3.opExtrude","SWEPT_BODY",BODY,{"disambiguationData":[OSD([sQuery(id+"F1.wireOp",EDGE,"E206.5.4.0")])]});
            var Q132;
            Q132=makeQuery(id+"F3.opExtrude","SWEPT_BODY",BODY,{"disambiguationData":[OSD([sQuery(id+"F1.wireOp",EDGE,"E206.6.4.0")])]});
            var Q133;
            Q133=makeQuery(id+"F3.opExtrude","SWEPT_BODY",BODY,{"disambiguationData":[OSD([sQuery(id+"F1.wireOp",EDGE,"E206.7.4.0")])]});
            var Q134;
            Q134=makeQuery(id+"F3.opExtrude","SWEPT_BODY",BODY,{"disambiguationData":[OSD([sQuery(id+"F1.wireOp",EDGE,"E206.8.4.0")])]});
            var Q135;
            Q135=makeQuery(id+"F3.opExtrude","SWEPT_BODY",BODY,{"disambiguationData":[OSD([sQuery(id+"F1.wireOp",EDGE,"E206.8.3.0")])]});
            var Q136;
            Q136=makeQuery(id+"F3.opExtrude","SWEPT_BODY",BODY,{"disambiguationData":[OSD([sQuery(id+"F1.wireOp",EDGE,"E206.7.3.0")])]});
            var Q137;
            Q137=makeQuery(id+"F3.opExtrude","SWEPT_BODY",BODY,{"disambiguationData":[OSD([sQuery(id+"F1.wireOp",EDGE,"E206.6.3.0")])]});
            var Q138;
            Q138=makeQuery(id+"F3.opExtrude","SWEPT_BODY",BODY,{"disambiguationData":[OSD([sQuery(id+"F1.wireOp",EDGE,"E206.5.3.0")])]});
            var Q139;
            Q139=makeQuery(id+"F3.opExtrude","SWEPT_BODY",BODY,{"disambiguationData":[OSD([sQuery(id+"F1.wireOp",EDGE,"E206.4.3.0")])]});
            var Q140;
            Q140=makeQuery(id+"F3.opExtrude","SWEPT_BODY",BODY,{"disambiguationData":[OSD([sQuery(id+"F1.wireOp",EDGE,"E206.3.3.0")])]});
            var Q141;
            Q141=makeQuery(id+"F3.opExtrude","SWEPT_BODY",BODY,{"disambiguationData":[OSD([sQuery(id+"F1.wireOp",EDGE,"E206.2.3.0")])]});
            var Q142;
            Q142=makeQuery(id+"F3.opExtrude","SWEPT_BODY",BODY,{"disambiguationData":[OSD([sQuery(id+"F1.wireOp",EDGE,"E206.1.3.0")])]});
            var Q143;
            Q143=makeQuery(id+"F3.opExtrude","SWEPT_BODY",BODY,{"disambiguationData":[OSD([sQuery(id+"F1.wireOp",EDGE,"E206.0.3.0")])]});
            var Q144;
            Q144=makeQuery(id+"F3.opExtrude","SWEPT_BODY",BODY,{"disambiguationData":[OSD([sQuery(id+"F1.wireOp",EDGE,"E206.0.2.0")])]});
            var Q145;
            Q145=makeQuery(id+"F3.opExtrude","SWEPT_BODY",BODY,{"disambiguationData":[OSD([sQuery(id+"F1.wireOp",EDGE,"E206.1.2.0")])]});
            var Q146;
            Q146=makeQuery(id+"F3.opExtrude","SWEPT_BODY",BODY,{"disambiguationData":[OSD([sQuery(id+"F1.wireOp",EDGE,"E206.2.2.0")])]});
            var Q147;
            Q147=makeQuery(id+"F3.opExtrude","SWEPT_BODY",BODY,{"disambiguationData":[OSD([sQuery(id+"F1.wireOp",EDGE,"E206.3.2.0")])]});
            var Q148;
            Q148=makeQuery(id+"F3.opExtrude","SWEPT_BODY",BODY,{"disambiguationData":[OSD([sQuery(id+"F1.wireOp",EDGE,"E206.4.2.0")])]});
            var Q149;
            Q149=makeQuery(id+"F3.opExtrude","SWEPT_BODY",BODY,{"disambiguationData":[OSD([sQuery(id+"F1.wireOp",EDGE,"E206.5.2.0")])]});
            var Q150;
            Q150=makeQuery(id+"F3.opExtrude","SWEPT_BODY",BODY,{"disambiguationData":[OSD([sQuery(id+"F1.wireOp",EDGE,"E206.6.2.0")])]});
            var Q151;
            Q151=makeQuery(id+"F3.opExtrude","SWEPT_BODY",BODY,{"disambiguationData":[OSD([sQuery(id+"F1.wireOp",EDGE,"E206.7.2.0")])]});
            var Q152;
            Q152=makeQuery(id+"F3.opExtrude","SWEPT_BODY",BODY,{"disambiguationData":[OSD([sQuery(id+"F1.wireOp",EDGE,"E206.8.2.0")])]});
            var Q153;
            Q153=makeQuery(id+"F3.opExtrude","SWEPT_BODY",BODY,{"disambiguationData":[OSD([sQuery(id+"F1.wireOp",EDGE,"E206.8.1.0")])]});
            var Q154;
            Q154=makeQuery(id+"F3.opExtrude","SWEPT_BODY",BODY,{"disambiguationData":[OSD([sQuery(id+"F1.wireOp",EDGE,"E206.7.1.0")])]});
            var Q155;
            Q155=makeQuery(id+"F3.opExtrude","SWEPT_BODY",BODY,{"disambiguationData":[OSD([sQuery(id+"F1.wireOp",EDGE,"E206.6.1.0")])]});
            var Q156;
            Q156=makeQuery(id+"F3.opExtrude","SWEPT_BODY",BODY,{"disambiguationData":[OSD([sQuery(id+"F1.wireOp",EDGE,"E206.5.1.0")])]});
            var Q157;
            Q157=makeQuery(id+"F3.opExtrude","SWEPT_BODY",BODY,{"disambiguationData":[OSD([sQuery(id+"F1.wireOp",EDGE,"E206.4.1.0")])]});
            var Q158;
            Q158=makeQuery(id+"F3.opExtrude","SWEPT_BODY",BODY,{"disambiguationData":[OSD([sQuery(id+"F1.wireOp",EDGE,"E206.3.1.0")])]});
            var Q159;
            Q159=makeQuery(id+"F3.opExtrude","SWEPT_BODY",BODY,{"disambiguationData":[OSD([sQuery(id+"F1.wireOp",EDGE,"E206.2.1.0")])]});
            var Q160;
            Q160=makeQuery(id+"F3.opExtrude","SWEPT_BODY",BODY,{"disambiguationData":[OSD([sQuery(id+"F1.wireOp",EDGE,"E206.1.1.0")])]});
            var Q161;
            Q161=makeQuery(id+"F3.opExtrude","SWEPT_BODY",BODY,{"disambiguationData":[OSD([sQuery(id+"F1.wireOp",EDGE,"E206.0.1.0")])]});
            var Q162;
            Q162=makeQuery(id+"F3.opExtrude","SWEPT_BODY",BODY,{"disambiguationData":[OSD([sQuery(id+"F1.wireOp",EDGE,"E206.8.0.0")])]});
            var Q163;
            Q163=makeQuery(id+"F3.opExtrude","SWEPT_BODY",BODY,{"disambiguationData":[OSD([sQuery(id+"F1.wireOp",EDGE,"E206.7.0.0")])]});
            var Q164;
            Q164=makeQuery(id+"F3.opExtrude","SWEPT_BODY",BODY,{"disambiguationData":[OSD([sQuery(id+"F1.wireOp",EDGE,"E206.6.0.0")])]});
            var Q165;
            Q165=makeQuery(id+"F3.opExtrude","SWEPT_BODY",BODY,{"disambiguationData":[OSD([sQuery(id+"F1.wireOp",EDGE,"E206.5.0.0")])]});
            var Q166;
            Q166=makeQuery(id+"F3.opExtrude","SWEPT_BODY",BODY,{"disambiguationData":[OSD([sQuery(id+"F1.wireOp",EDGE,"E206.4.0.0")])]});
            var Q167;
            Q167=makeQuery(id+"F3.opExtrude","SWEPT_BODY",BODY,{"disambiguationData":[OSD([sQuery(id+"F1.wireOp",EDGE,"E206.3.0.0")])]});
            var Q168;
            Q168=makeQuery(id+"F3.opExtrude","SWEPT_BODY",BODY,{"disambiguationData":[OSD([sQuery(id+"F1.wireOp",EDGE,"E206.2.0.0")])]});
            var Q169;
            Q169=makeQuery(id+"F3.opExtrude","SWEPT_BODY",BODY,{"disambiguationData":[OSD([sQuery(id+"F1.wireOp",EDGE,"E206.1.0.0")])]});
            var Q170;
            Q170=makeQuery(id+"F3.opExtrude","SWEPT_BODY",BODY,{"disambiguationData":[OSD([sQuery(id+"F1.wireOp",EDGE,"E199")])]});
            booleanBodies(context, id + "F16", {"operationType" : BooleanOperationType.SUBTRACTION, "tools" : qUnion([Q0, Q1, Q2, Q3, Q4, Q5, Q6, Q7, Q8, Q9, Q10, Q11, Q12, Q13, Q14, Q15, Q16, Q17, Q18, Q19, Q20, Q21, Q22, Q23, Q24, Q25, Q26, Q27, Q28, Q29, Q30, Q31, Q32, Q33, Q34, Q35, Q36, Q37, Q38, Q39, Q40, Q41, Q42, Q43, Q44, Q45, Q46, Q47, Q48, Q49, Q50, Q51, Q52, Q53, Q54, Q55, Q56, Q57, Q58, Q59, Q60, Q61, Q62, Q63, Q64, Q65, Q66, Q67, Q68, Q69, Q70, Q71, Q72, Q73, Q74, Q75, Q76, Q77, Q78, Q79, Q80, Q81, Q82, Q83, Q84, Q85, Q86, Q87, Q88, Q89]), "targets" : qUnion([Q90, Q91, Q92, Q93, Q94, Q95, Q96, Q97, Q98, Q99, Q100, Q101, Q102, Q103, Q104, Q105, Q106, Q107, Q108, Q109, Q110, Q111, Q112, Q113, Q114, Q115, Q116, Q117, Q118, Q119, Q120, Q121, Q122, Q123, Q124, Q125, Q126, Q127, Q128, Q129, Q130, Q131, Q132, Q133, Q134, Q135, Q136, Q137, Q138, Q139, Q140, Q141, Q142, Q143, Q144, Q145, Q146, Q147, Q148, Q149, Q150, Q151, Q152, Q153, Q154, Q155, Q156, Q157, Q158, Q159, Q160, Q161, Q162, Q163, Q164, Q165, Q166, Q167, Q168, Q169, Q170])});
        }
        {
            var Q0;
            Q0=makeQuery(id+"F15.*.split.splitOp","SPLIT",BODY,{"derivedFrom":makeQuery(id+"F15.opExtrude","SWEPT_BODY",BODY,{"disambiguationData":[OSD([sQuery(id+"F0.wireOp",EDGE,"E87")])]})});
            var Q1;
            Q1=makeQuery(id+"F3.opExtrude","SWEPT_BODY",BODY,{"disambiguationData":[OSD([sQuery(id+"F1.wireOp",EDGE,"E206.7.4.0")])]});
            var Q2;
            Q2=makeQuery(id+"F3.opExtrude","SWEPT_BODY",BODY,{"disambiguationData":[OSD([sQuery(id+"F1.wireOp",EDGE,"E206.8.4.0")])]});
            var Q3;
            Q3=makeQuery(id+"F3.opExtrude","SWEPT_BODY",BODY,{"disambiguationData":[OSD([sQuery(id+"F1.wireOp",EDGE,"E206.8.3.0")])]});
            var Q4;
            Q4=makeQuery(id+"F3.opExtrude","SWEPT_BODY",BODY,{"disambiguationData":[OSD([sQuery(id+"F1.wireOp",EDGE,"E206.7.3.0")])]});
            booleanBodies(context, id + "F17", {"operationType" : BooleanOperationType.SUBTRACTION, "tools" : qUnion([Q0]), "targets" : qUnion([Q1, Q2, Q3, Q4])});
        }
        {
            var Q0;
            Q0=makeQuery(id+"F2.opExtrude","CAP_FACE",FACE,{"disambiguationData":[OSD([sQuery(id+"F0.wireOp",EDGE,"E0.bottom"),sQuery(id+"F0.wireOp",EDGE,"E0.top"),sQuery(id+"F0.wireOp",EDGE,"E0.left"),sQuery(id+"F0.wireOp",EDGE,"E0.right"),sQuery(id+"F0.wireOp",EDGE,"E3.filletArc"),sQuery(id+"F0.wireOp",EDGE,"E4.filletArc"),sQuery(id+"F0.wireOp",EDGE,"E5.filletArc"),sQuery(id+"F0.wireOp",EDGE,"E6.filletArc"),sQuery(id+"F0.wireOp",EDGE,"E7"),sQuery(id+"F0.wireOp",EDGE,"E8"),sQuery(id+"F0.wireOp",EDGE,"E9"),sQuery(id+"F0.wireOp",EDGE,"E10"),sQuery(id+"F0.wireOp",EDGE,"E11"),sQuery(id+"F0.wireOp",EDGE,"E12"),sQuery(id+"F0.wireOp",EDGE,"E13"),sQuery(id+"F0.wireOp",EDGE,"E14"),sQuery(id+"F0.wireOp",EDGE,"E15"),sQuery(id+"F0.wireOp",EDGE,"E16"),sQuery(id+"F0.wireOp",EDGE,"E17"),sQuery(id+"F0.wireOp",EDGE,"E18"),sQuery(id+"F0.wireOp",EDGE,"E19"),sQuery(id+"F0.wireOp",EDGE,"E20"),sQuery(id+"F0.wireOp",EDGE,"E21"),sQuery(id+"F0.wireOp",EDGE,"E22"),sQuery(id+"F0.wireOp",EDGE,"E23"),sQuery(id+"F0.wireOp",EDGE,"E24"),sQuery(id+"F0.wireOp",EDGE,"E25"),sQuery(id+"F0.wireOp",EDGE,"E26"),sQuery(id+"F0.wireOp",EDGE,"E27"),sQuery(id+"F0.wireOp",EDGE,"E28"),sQuery(id+"F0.wireOp",EDGE,"E29"),sQuery(id+"F0.wireOp",EDGE,"E30"),sQuery(id+"F0.wireOp",EDGE,"E31"),sQuery(id+"F0.wireOp",EDGE,"E32"),sQuery(id+"F0.wireOp",EDGE,"E33"),sQuery(id+"F0.wireOp",EDGE,"E34"),sQuery(id+"F0.wireOp",EDGE,"E35"),sQuery(id+"F0.wireOp",EDGE,"E36"),sQuery(id+"F0.wireOp",EDGE,"E37"),sQuery(id+"F0.wireOp",EDGE,"E38"),sQuery(id+"F0.wireOp",EDGE,"E39"),sQuery(id+"F0.wireOp",EDGE,"E40"),sQuery(id+"F0.wireOp",EDGE,"E41"),sQuery(id+"F0.wireOp",EDGE,"E42"),sQuery(id+"F0.wireOp",EDGE,"E43"),sQuery(id+"F0.wireOp",EDGE,"E44"),sQuery(id+"F0.wireOp",EDGE,"E45"),sQuery(id+"F0.wireOp",EDGE,"E46"),sQuery(id+"F0.wireOp",EDGE,"E47"),sQuery(id+"F0.wireOp",EDGE,"E48"),sQuery(id+"F0.wireOp",EDGE,"E49"),sQuery(id+"F0.wireOp",EDGE,"E50"),sQuery(id+"F0.wireOp",EDGE,"E51"),sQuery(id+"F0.wireOp",EDGE,"E52"),sQuery(id+"F0.wireOp",EDGE,"E53"),sQuery(id+"F0.wireOp",EDGE,"E54"),sQuery(id+"F0.wireOp",EDGE,"E55"),sQuery(id+"F0.wireOp",EDGE,"E56"),sQuery(id+"F0.wireOp",EDGE,"E57"),sQuery(id+"F0.wireOp",EDGE,"E58"),sQuery(id+"F0.wireOp",EDGE,"E59"),sQuery(id+"F0.wireOp",EDGE,"E60"),sQuery(id+"F0.wireOp",EDGE,"E61"),sQuery(id+"F0.wireOp",EDGE,"E62"),sQuery(id+"F0.wireOp",EDGE,"E63"),sQuery(id+"F0.wireOp",EDGE,"E64"),sQuery(id+"F0.wireOp",EDGE,"E65"),sQuery(id+"F0.wireOp",EDGE,"E66"),sQuery(id+"F0.wireOp",EDGE,"E67"),sQuery(id+"F0.wireOp",EDGE,"E68"),sQuery(id+"F0.wireOp",EDGE,"E69"),sQuery(id+"F0.wireOp",EDGE,"E70"),sQuery(id+"F0.wireOp",EDGE,"E71"),sQuery(id+"F0.wireOp",EDGE,"E72"),sQuery(id+"F0.wireOp",EDGE,"E73"),sQuery(id+"F0.wireOp",EDGE,"E74"),sQuery(id+"F0.wireOp",EDGE,"E75"),sQuery(id+"F0.wireOp",EDGE,"E76"),sQuery(id+"F0.wireOp",EDGE,"E77"),sQuery(id+"F0.wireOp",EDGE,"E78"),sQuery(id+"F0.wireOp",EDGE,"E79"),sQuery(id+"F0.wireOp",EDGE,"E80"),sQuery(id+"F0.wireOp",EDGE,"E81"),sQuery(id+"F0.wireOp",EDGE,"E82"),sQuery(id+"F0.wireOp",EDGE,"E83"),sQuery(id+"F0.wireOp",EDGE,"E84"),sQuery(id+"F0.wireOp",EDGE,"E85"),sQuery(id+"F0.wireOp",EDGE,"E86"),sQuery(id+"F0.wireOp",EDGE,"E87"),sQuery(id+"F0.wireOp",EDGE,"E88"),sQuery(id+"F0.wireOp",EDGE,"E89"),sQuery(id+"F0.wireOp",EDGE,"E90"),sQuery(id+"F0.wireOp",EDGE,"E91"),sQuery(id+"F0.wireOp",EDGE,"E92"),sQuery(id+"F0.wireOp",EDGE,"E93"),sQuery(id+"F0.wireOp",EDGE,"E94"),sQuery(id+"F0.wireOp",EDGE,"E95"),sQuery(id+"F0.wireOp",EDGE,"E96"),sQuery(id+"F0.wireOp",EDGE,"E97"),sQuery(id+"F0.wireOp",EDGE,"E98"),sQuery(id+"F0.wireOp",EDGE,"E99"),sQuery(id+"F0.wireOp",EDGE,"E100"),sQuery(id+"F0.wireOp",EDGE,"E101"),sQuery(id+"F0.wireOp",EDGE,"E102"),sQuery(id+"F0.wireOp",EDGE,"E103"),sQuery(id+"F0.wireOp",EDGE,"E104"),sQuery(id+"F0.wireOp",EDGE,"E105"),sQuery(id+"F0.wireOp",EDGE,"E106"),sQuery(id+"F0.wireOp",EDGE,"E107"),sQuery(id+"F0.wireOp",EDGE,"E108"),sQuery(id+"F0.wireOp",EDGE,"E109"),sQuery(id+"F0.wireOp",EDGE,"E110"),sQuery(id+"F0.wireOp",EDGE,"E111"),sQuery(id+"F0.wireOp",EDGE,"E112"),sQuery(id+"F0.wireOp",EDGE,"E113"),sQuery(id+"F0.wireOp",EDGE,"E114"),sQuery(id+"F0.wireOp",EDGE,"E115"),sQuery(id+"F0.wireOp",EDGE,"E116"),sQuery(id+"F0.wireOp",EDGE,"E117"),sQuery(id+"F0.wireOp",EDGE,"E118"),sQuery(id+"F0.wireOp",EDGE,"E119"),sQuery(id+"F0.wireOp",EDGE,"E120"),sQuery(id+"F0.wireOp",EDGE,"E121"),sQuery(id+"F0.wireOp",EDGE,"E122"),sQuery(id+"F0.wireOp",EDGE,"E123"),sQuery(id+"F0.wireOp",EDGE,"E124"),sQuery(id+"F0.wireOp",EDGE,"E125"),sQuery(id+"F0.wireOp",EDGE,"E126"),sQuery(id+"F0.wireOp",EDGE,"E127"),sQuery(id+"F0.wireOp",EDGE,"E128"),sQuery(id+"F0.wireOp",EDGE,"E129"),sQuery(id+"F0.wireOp",EDGE,"E130"),sQuery(id+"F0.wireOp",EDGE,"E131"),sQuery(id+"F0.wireOp",EDGE,"E132"),sQuery(id+"F0.wireOp",EDGE,"E133"),sQuery(id+"F0.wireOp",EDGE,"E134"),sQuery(id+"F0.wireOp",EDGE,"E135"),sQuery(id+"F0.wireOp",EDGE,"E136"),sQuery(id+"F0.wireOp",EDGE,"E137"),sQuery(id+"F0.wireOp",EDGE,"E138"),sQuery(id+"F0.wireOp",EDGE,"E139"),sQuery(id+"F0.wireOp",EDGE,"E140"),sQuery(id+"F0.wireOp",EDGE,"E141"),sQuery(id+"F0.wireOp",EDGE,"E142"),sQuery(id+"F0.wireOp",EDGE,"E143"),sQuery(id+"F0.wireOp",EDGE,"E144"),sQuery(id+"F0.wireOp",EDGE,"E145"),sQuery(id+"F0.wireOp",EDGE,"E146"),sQuery(id+"F0.wireOp",EDGE,"E147"),sQuery(id+"F0.wireOp",EDGE,"E148"),sQuery(id+"F0.wireOp",EDGE,"E149"),sQuery(id+"F0.wireOp",EDGE,"E150"),sQuery(id+"F0.wireOp",EDGE,"E151"),sQuery(id+"F0.wireOp",EDGE,"E152"),sQuery(id+"F0.wireOp",EDGE,"E153"),sQuery(id+"F0.wireOp",EDGE,"E154"),sQuery(id+"F0.wireOp",EDGE,"E155"),sQuery(id+"F0.wireOp",EDGE,"E156"),sQuery(id+"F0.wireOp",EDGE,"E157"),sQuery(id+"F0.wireOp",EDGE,"E158"),sQuery(id+"F0.wireOp",EDGE,"E159"),sQuery(id+"F0.wireOp",EDGE,"E160"),sQuery(id+"F0.wireOp",EDGE,"E161"),sQuery(id+"F0.wireOp",EDGE,"E162"),sQuery(id+"F0.wireOp",EDGE,"E163"),sQuery(id+"F0.wireOp",EDGE,"E164"),sQuery(id+"F0.wireOp",EDGE,"E165"),sQuery(id+"F0.wireOp",EDGE,"E166"),sQuery(id+"F0.wireOp",EDGE,"E167"),sQuery(id+"F0.wireOp",EDGE,"E168"),sQuery(id+"F0.wireOp",EDGE,"E169"),sQuery(id+"F0.wireOp",EDGE,"E170"),sQuery(id+"F0.wireOp",EDGE,"E171"),sQuery(id+"F0.wireOp",EDGE,"E172"),sQuery(id+"F0.wireOp",EDGE,"E173"),sQuery(id+"F0.wireOp",EDGE,"E174"),sQuery(id+"F0.wireOp",EDGE,"E175"),sQuery(id+"F0.wireOp",EDGE,"E176"),sQuery(id+"F0.wireOp",EDGE,"E177"),sQuery(id+"F0.wireOp",EDGE,"E178"),sQuery(id+"F0.wireOp",EDGE,"E179"),sQuery(id+"F0.wireOp",EDGE,"E180"),sQuery(id+"F0.wireOp",EDGE,"E181"),sQuery(id+"F0.wireOp",EDGE,"E182"),sQuery(id+"F0.wireOp",EDGE,"E183"),sQuery(id+"F0.wireOp",EDGE,"E184"),sQuery(id+"F0.wireOp",EDGE,"E185"),sQuery(id+"F0.wireOp",EDGE,"E186")])],"isStart":false});
            chamfer(context, id + "F18", {"entities" : qUnion([Q0]), "width" : 0.5 * mm, "tangentPropagation" : true});
        }
        {
            var Q0;
            Q0=makeQuery(id+"F2.opExtrude","CAP_FACE",FACE,{"disambiguationData":[OSD([sQuery(id+"F0.wireOp",EDGE,"E0.bottom"),sQuery(id+"F0.wireOp",EDGE,"E0.top"),sQuery(id+"F0.wireOp",EDGE,"E0.left"),sQuery(id+"F0.wireOp",EDGE,"E0.right"),sQuery(id+"F0.wireOp",EDGE,"E3.filletArc"),sQuery(id+"F0.wireOp",EDGE,"E4.filletArc"),sQuery(id+"F0.wireOp",EDGE,"E5.filletArc"),sQuery(id+"F0.wireOp",EDGE,"E6.filletArc"),sQuery(id+"F0.wireOp",EDGE,"E7"),sQuery(id+"F0.wireOp",EDGE,"E8"),sQuery(id+"F0.wireOp",EDGE,"E9"),sQuery(id+"F0.wireOp",EDGE,"E10"),sQuery(id+"F0.wireOp",EDGE,"E11"),sQuery(id+"F0.wireOp",EDGE,"E12"),sQuery(id+"F0.wireOp",EDGE,"E13"),sQuery(id+"F0.wireOp",EDGE,"E14"),sQuery(id+"F0.wireOp",EDGE,"E15"),sQuery(id+"F0.wireOp",EDGE,"E16"),sQuery(id+"F0.wireOp",EDGE,"E17"),sQuery(id+"F0.wireOp",EDGE,"E18"),sQuery(id+"F0.wireOp",EDGE,"E19"),sQuery(id+"F0.wireOp",EDGE,"E20"),sQuery(id+"F0.wireOp",EDGE,"E21"),sQuery(id+"F0.wireOp",EDGE,"E22"),sQuery(id+"F0.wireOp",EDGE,"E23"),sQuery(id+"F0.wireOp",EDGE,"E24"),sQuery(id+"F0.wireOp",EDGE,"E25"),sQuery(id+"F0.wireOp",EDGE,"E26"),sQuery(id+"F0.wireOp",EDGE,"E27"),sQuery(id+"F0.wireOp",EDGE,"E28"),sQuery(id+"F0.wireOp",EDGE,"E29"),sQuery(id+"F0.wireOp",EDGE,"E30"),sQuery(id+"F0.wireOp",EDGE,"E31"),sQuery(id+"F0.wireOp",EDGE,"E32"),sQuery(id+"F0.wireOp",EDGE,"E33"),sQuery(id+"F0.wireOp",EDGE,"E34"),sQuery(id+"F0.wireOp",EDGE,"E35"),sQuery(id+"F0.wireOp",EDGE,"E36"),sQuery(id+"F0.wireOp",EDGE,"E37"),sQuery(id+"F0.wireOp",EDGE,"E38"),sQuery(id+"F0.wireOp",EDGE,"E39"),sQuery(id+"F0.wireOp",EDGE,"E40"),sQuery(id+"F0.wireOp",EDGE,"E41"),sQuery(id+"F0.wireOp",EDGE,"E42"),sQuery(id+"F0.wireOp",EDGE,"E43"),sQuery(id+"F0.wireOp",EDGE,"E44"),sQuery(id+"F0.wireOp",EDGE,"E45"),sQuery(id+"F0.wireOp",EDGE,"E46"),sQuery(id+"F0.wireOp",EDGE,"E47"),sQuery(id+"F0.wireOp",EDGE,"E48"),sQuery(id+"F0.wireOp",EDGE,"E49"),sQuery(id+"F0.wireOp",EDGE,"E50"),sQuery(id+"F0.wireOp",EDGE,"E51"),sQuery(id+"F0.wireOp",EDGE,"E52"),sQuery(id+"F0.wireOp",EDGE,"E53"),sQuery(id+"F0.wireOp",EDGE,"E54"),sQuery(id+"F0.wireOp",EDGE,"E55"),sQuery(id+"F0.wireOp",EDGE,"E56"),sQuery(id+"F0.wireOp",EDGE,"E57"),sQuery(id+"F0.wireOp",EDGE,"E58"),sQuery(id+"F0.wireOp",EDGE,"E59"),sQuery(id+"F0.wireOp",EDGE,"E60"),sQuery(id+"F0.wireOp",EDGE,"E61"),sQuery(id+"F0.wireOp",EDGE,"E62"),sQuery(id+"F0.wireOp",EDGE,"E63"),sQuery(id+"F0.wireOp",EDGE,"E64"),sQuery(id+"F0.wireOp",EDGE,"E65"),sQuery(id+"F0.wireOp",EDGE,"E66"),sQuery(id+"F0.wireOp",EDGE,"E67"),sQuery(id+"F0.wireOp",EDGE,"E68"),sQuery(id+"F0.wireOp",EDGE,"E69"),sQuery(id+"F0.wireOp",EDGE,"E70"),sQuery(id+"F0.wireOp",EDGE,"E71"),sQuery(id+"F0.wireOp",EDGE,"E72"),sQuery(id+"F0.wireOp",EDGE,"E73"),sQuery(id+"F0.wireOp",EDGE,"E74"),sQuery(id+"F0.wireOp",EDGE,"E75"),sQuery(id+"F0.wireOp",EDGE,"E76"),sQuery(id+"F0.wireOp",EDGE,"E77"),sQuery(id+"F0.wireOp",EDGE,"E78"),sQuery(id+"F0.wireOp",EDGE,"E79"),sQuery(id+"F0.wireOp",EDGE,"E80"),sQuery(id+"F0.wireOp",EDGE,"E81"),sQuery(id+"F0.wireOp",EDGE,"E82"),sQuery(id+"F0.wireOp",EDGE,"E83"),sQuery(id+"F0.wireOp",EDGE,"E84"),sQuery(id+"F0.wireOp",EDGE,"E85"),sQuery(id+"F0.wireOp",EDGE,"E86"),sQuery(id+"F0.wireOp",EDGE,"E87"),sQuery(id+"F0.wireOp",EDGE,"E88"),sQuery(id+"F0.wireOp",EDGE,"E89"),sQuery(id+"F0.wireOp",EDGE,"E90"),sQuery(id+"F0.wireOp",EDGE,"E91"),sQuery(id+"F0.wireOp",EDGE,"E92"),sQuery(id+"F0.wireOp",EDGE,"E93"),sQuery(id+"F0.wireOp",EDGE,"E94"),sQuery(id+"F0.wireOp",EDGE,"E95"),sQuery(id+"F0.wireOp",EDGE,"E96"),sQuery(id+"F0.wireOp",EDGE,"E97"),sQuery(id+"F0.wireOp",EDGE,"E98"),sQuery(id+"F0.wireOp",EDGE,"E99"),sQuery(id+"F0.wireOp",EDGE,"E100"),sQuery(id+"F0.wireOp",EDGE,"E101"),sQuery(id+"F0.wireOp",EDGE,"E102"),sQuery(id+"F0.wireOp",EDGE,"E103"),sQuery(id+"F0.wireOp",EDGE,"E104"),sQuery(id+"F0.wireOp",EDGE,"E105"),sQuery(id+"F0.wireOp",EDGE,"E106"),sQuery(id+"F0.wireOp",EDGE,"E107"),sQuery(id+"F0.wireOp",EDGE,"E108"),sQuery(id+"F0.wireOp",EDGE,"E109"),sQuery(id+"F0.wireOp",EDGE,"E110"),sQuery(id+"F0.wireOp",EDGE,"E111"),sQuery(id+"F0.wireOp",EDGE,"E112"),sQuery(id+"F0.wireOp",EDGE,"E113"),sQuery(id+"F0.wireOp",EDGE,"E114"),sQuery(id+"F0.wireOp",EDGE,"E115"),sQuery(id+"F0.wireOp",EDGE,"E116"),sQuery(id+"F0.wireOp",EDGE,"E117"),sQuery(id+"F0.wireOp",EDGE,"E118"),sQuery(id+"F0.wireOp",EDGE,"E119"),sQuery(id+"F0.wireOp",EDGE,"E120"),sQuery(id+"F0.wireOp",EDGE,"E121"),sQuery(id+"F0.wireOp",EDGE,"E122"),sQuery(id+"F0.wireOp",EDGE,"E123"),sQuery(id+"F0.wireOp",EDGE,"E124"),sQuery(id+"F0.wireOp",EDGE,"E125"),sQuery(id+"F0.wireOp",EDGE,"E126"),sQuery(id+"F0.wireOp",EDGE,"E127"),sQuery(id+"F0.wireOp",EDGE,"E128"),sQuery(id+"F0.wireOp",EDGE,"E129"),sQuery(id+"F0.wireOp",EDGE,"E130"),sQuery(id+"F0.wireOp",EDGE,"E131"),sQuery(id+"F0.wireOp",EDGE,"E132"),sQuery(id+"F0.wireOp",EDGE,"E133"),sQuery(id+"F0.wireOp",EDGE,"E134"),sQuery(id+"F0.wireOp",EDGE,"E135"),sQuery(id+"F0.wireOp",EDGE,"E136"),sQuery(id+"F0.wireOp",EDGE,"E137"),sQuery(id+"F0.wireOp",EDGE,"E138"),sQuery(id+"F0.wireOp",EDGE,"E139"),sQuery(id+"F0.wireOp",EDGE,"E140"),sQuery(id+"F0.wireOp",EDGE,"E141"),sQuery(id+"F0.wireOp",EDGE,"E142"),sQuery(id+"F0.wireOp",EDGE,"E143"),sQuery(id+"F0.wireOp",EDGE,"E144"),sQuery(id+"F0.wireOp",EDGE,"E145"),sQuery(id+"F0.wireOp",EDGE,"E146"),sQuery(id+"F0.wireOp",EDGE,"E147"),sQuery(id+"F0.wireOp",EDGE,"E148"),sQuery(id+"F0.wireOp",EDGE,"E149"),sQuery(id+"F0.wireOp",EDGE,"E150"),sQuery(id+"F0.wireOp",EDGE,"E151"),sQuery(id+"F0.wireOp",EDGE,"E152"),sQuery(id+"F0.wireOp",EDGE,"E153"),sQuery(id+"F0.wireOp",EDGE,"E154"),sQuery(id+"F0.wireOp",EDGE,"E155"),sQuery(id+"F0.wireOp",EDGE,"E156"),sQuery(id+"F0.wireOp",EDGE,"E157"),sQuery(id+"F0.wireOp",EDGE,"E158"),sQuery(id+"F0.wireOp",EDGE,"E159"),sQuery(id+"F0.wireOp",EDGE,"E160"),sQuery(id+"F0.wireOp",EDGE,"E161"),sQuery(id+"F0.wireOp",EDGE,"E162"),sQuery(id+"F0.wireOp",EDGE,"E163"),sQuery(id+"F0.wireOp",EDGE,"E164"),sQuery(id+"F0.wireOp",EDGE,"E165"),sQuery(id+"F0.wireOp",EDGE,"E166"),sQuery(id+"F0.wireOp",EDGE,"E167"),sQuery(id+"F0.wireOp",EDGE,"E168"),sQuery(id+"F0.wireOp",EDGE,"E169"),sQuery(id+"F0.wireOp",EDGE,"E170"),sQuery(id+"F0.wireOp",EDGE,"E171"),sQuery(id+"F0.wireOp",EDGE,"E172"),sQuery(id+"F0.wireOp",EDGE,"E173"),sQuery(id+"F0.wireOp",EDGE,"E174"),sQuery(id+"F0.wireOp",EDGE,"E175"),sQuery(id+"F0.wireOp",EDGE,"E176"),sQuery(id+"F0.wireOp",EDGE,"E177"),sQuery(id+"F0.wireOp",EDGE,"E178"),sQuery(id+"F0.wireOp",EDGE,"E179"),sQuery(id+"F0.wireOp",EDGE,"E180"),sQuery(id+"F0.wireOp",EDGE,"E181"),sQuery(id+"F0.wireOp",EDGE,"E182"),sQuery(id+"F0.wireOp",EDGE,"E183"),sQuery(id+"F0.wireOp",EDGE,"E184"),sQuery(id+"F0.wireOp",EDGE,"E185"),sQuery(id+"F0.wireOp",EDGE,"E186")])],"isStart":true});
            chamfer(context, id + "F19", {"entities" : qUnion([Q0]), "width" : 0.3 * mm, "tangentPropagation" : true});
        }
        {
            var Q0;
            Q0=makeQuery(id+"F18.opChamfer","SPLIT",FACE,{"disambiguationData":[OD(153.0)],"derivedFrom":makeQuery(id+"F2.opExtrude","CAP_FACE",FACE,{"disambiguationData":[OSD([sQuery(id+"F0.wireOp",EDGE,"E0.bottom"),sQuery(id+"F0.wireOp",EDGE,"E0.top"),sQuery(id+"F0.wireOp",EDGE,"E0.left"),sQuery(id+"F0.wireOp",EDGE,"E0.right"),sQuery(id+"F0.wireOp",EDGE,"E3.filletArc"),sQuery(id+"F0.wireOp",EDGE,"E4.filletArc"),sQuery(id+"F0.wireOp",EDGE,"E5.filletArc"),sQuery(id+"F0.wireOp",EDGE,"E6.filletArc"),sQuery(id+"F0.wireOp",EDGE,"E7"),sQuery(id+"F0.wireOp",EDGE,"E8"),sQuery(id+"F0.wireOp",EDGE,"E9"),sQuery(id+"F0.wireOp",EDGE,"E10"),sQuery(id+"F0.wireOp",EDGE,"E11"),sQuery(id+"F0.wireOp",EDGE,"E12"),sQuery(id+"F0.wireOp",EDGE,"E13"),sQuery(id+"F0.wireOp",EDGE,"E14"),sQuery(id+"F0.wireOp",EDGE,"E15"),sQuery(id+"F0.wireOp",EDGE,"E16"),sQuery(id+"F0.wireOp",EDGE,"E17"),sQuery(id+"F0.wireOp",EDGE,"E18"),sQuery(id+"F0.wireOp",EDGE,"E19"),sQuery(id+"F0.wireOp",EDGE,"E20"),sQuery(id+"F0.wireOp",EDGE,"E21"),sQuery(id+"F0.wireOp",EDGE,"E22"),sQuery(id+"F0.wireOp",EDGE,"E23"),sQuery(id+"F0.wireOp",EDGE,"E24"),sQuery(id+"F0.wireOp",EDGE,"E25"),sQuery(id+"F0.wireOp",EDGE,"E26"),sQuery(id+"F0.wireOp",EDGE,"E27"),sQuery(id+"F0.wireOp",EDGE,"E28"),sQuery(id+"F0.wireOp",EDGE,"E29"),sQuery(id+"F0.wireOp",EDGE,"E30"),sQuery(id+"F0.wireOp",EDGE,"E31"),sQuery(id+"F0.wireOp",EDGE,"E32"),sQuery(id+"F0.wireOp",EDGE,"E33"),sQuery(id+"F0.wireOp",EDGE,"E34"),sQuery(id+"F0.wireOp",EDGE,"E35"),sQuery(id+"F0.wireOp",EDGE,"E36"),sQuery(id+"F0.wireOp",EDGE,"E37"),sQuery(id+"F0.wireOp",EDGE,"E38"),sQuery(id+"F0.wireOp",EDGE,"E39"),sQuery(id+"F0.wireOp",EDGE,"E40"),sQuery(id+"F0.wireOp",EDGE,"E41"),sQuery(id+"F0.wireOp",EDGE,"E42"),sQuery(id+"F0.wireOp",EDGE,"E43"),sQuery(id+"F0.wireOp",EDGE,"E44"),sQuery(id+"F0.wireOp",EDGE,"E45"),sQuery(id+"F0.wireOp",EDGE,"E46"),sQuery(id+"F0.wireOp",EDGE,"E47"),sQuery(id+"F0.wireOp",EDGE,"E48"),sQuery(id+"F0.wireOp",EDGE,"E49"),sQuery(id+"F0.wireOp",EDGE,"E50"),sQuery(id+"F0.wireOp",EDGE,"E51"),sQuery(id+"F0.wireOp",EDGE,"E52"),sQuery(id+"F0.wireOp",EDGE,"E53"),sQuery(id+"F0.wireOp",EDGE,"E54"),sQuery(id+"F0.wireOp",EDGE,"E55"),sQuery(id+"F0.wireOp",EDGE,"E56"),sQuery(id+"F0.wireOp",EDGE,"E57"),sQuery(id+"F0.wireOp",EDGE,"E58"),sQuery(id+"F0.wireOp",EDGE,"E59"),sQuery(id+"F0.wireOp",EDGE,"E60"),sQuery(id+"F0.wireOp",EDGE,"E61"),sQuery(id+"F0.wireOp",EDGE,"E62"),sQuery(id+"F0.wireOp",EDGE,"E63"),sQuery(id+"F0.wireOp",EDGE,"E64"),sQuery(id+"F0.wireOp",EDGE,"E65"),sQuery(id+"F0.wireOp",EDGE,"E66"),sQuery(id+"F0.wireOp",EDGE,"E67"),sQuery(id+"F0.wireOp",EDGE,"E68"),sQuery(id+"F0.wireOp",EDGE,"E69"),sQuery(id+"F0.wireOp",EDGE,"E70"),sQuery(id+"F0.wireOp",EDGE,"E71"),sQuery(id+"F0.wireOp",EDGE,"E72"),sQuery(id+"F0.wireOp",EDGE,"E73"),sQuery(id+"F0.wireOp",EDGE,"E74"),sQuery(id+"F0.wireOp",EDGE,"E75"),sQuery(id+"F0.wireOp",EDGE,"E76"),sQuery(id+"F0.wireOp",EDGE,"E77"),sQuery(id+"F0.wireOp",EDGE,"E78"),sQuery(id+"F0.wireOp",EDGE,"E79"),sQuery(id+"F0.wireOp",EDGE,"E80"),sQuery(id+"F0.wireOp",EDGE,"E81"),sQuery(id+"F0.wireOp",EDGE,"E82"),sQuery(id+"F0.wireOp",EDGE,"E83"),sQuery(id+"F0.wireOp",EDGE,"E84"),sQuery(id+"F0.wireOp",EDGE,"E85"),sQuery(id+"F0.wireOp",EDGE,"E86"),sQuery(id+"F0.wireOp",EDGE,"E87"),sQuery(id+"F0.wireOp",EDGE,"E88"),sQuery(id+"F0.wireOp",EDGE,"E89"),sQuery(id+"F0.wireOp",EDGE,"E90"),sQuery(id+"F0.wireOp",EDGE,"E91"),sQuery(id+"F0.wireOp",EDGE,"E92"),sQuery(id+"F0.wireOp",EDGE,"E93"),sQuery(id+"F0.wireOp",EDGE,"E94"),sQuery(id+"F0.wireOp",EDGE,"E95"),sQuery(id+"F0.wireOp",EDGE,"E96"),sQuery(id+"F0.wireOp",EDGE,"E97"),sQuery(id+"F0.wireOp",EDGE,"E98"),sQuery(id+"F0.wireOp",EDGE,"E99"),sQuery(id+"F0.wireOp",EDGE,"E100"),sQuery(id+"F0.wireOp",EDGE,"E101"),sQuery(id+"F0.wireOp",EDGE,"E102"),sQuery(id+"F0.wireOp",EDGE,"E103"),sQuery(id+"F0.wireOp",EDGE,"E104"),sQuery(id+"F0.wireOp",EDGE,"E105"),sQuery(id+"F0.wireOp",EDGE,"E106"),sQuery(id+"F0.wireOp",EDGE,"E107"),sQuery(id+"F0.wireOp",EDGE,"E108"),sQuery(id+"F0.wireOp",EDGE,"E109"),sQuery(id+"F0.wireOp",EDGE,"E110"),sQuery(id+"F0.wireOp",EDGE,"E111"),sQuery(id+"F0.wireOp",EDGE,"E112"),sQuery(id+"F0.wireOp",EDGE,"E113"),sQuery(id+"F0.wireOp",EDGE,"E114"),sQuery(id+"F0.wireOp",EDGE,"E115"),sQuery(id+"F0.wireOp",EDGE,"E116"),sQuery(id+"F0.wireOp",EDGE,"E117"),sQuery(id+"F0.wireOp",EDGE,"E118"),sQuery(id+"F0.wireOp",EDGE,"E119"),sQuery(id+"F0.wireOp",EDGE,"E120"),sQuery(id+"F0.wireOp",EDGE,"E121"),sQuery(id+"F0.wireOp",EDGE,"E122"),sQuery(id+"F0.wireOp",EDGE,"E123"),sQuery(id+"F0.wireOp",EDGE,"E124"),sQuery(id+"F0.wireOp",EDGE,"E125"),sQuery(id+"F0.wireOp",EDGE,"E126"),sQuery(id+"F0.wireOp",EDGE,"E127"),sQuery(id+"F0.wireOp",EDGE,"E128"),sQuery(id+"F0.wireOp",EDGE,"E129"),sQuery(id+"F0.wireOp",EDGE,"E130"),sQuery(id+"F0.wireOp",EDGE,"E131"),sQuery(id+"F0.wireOp",EDGE,"E132"),sQuery(id+"F0.wireOp",EDGE,"E133"),sQuery(id+"F0.wireOp",EDGE,"E134"),sQuery(id+"F0.wireOp",EDGE,"E135"),sQuery(id+"F0.wireOp",EDGE,"E136"),sQuery(id+"F0.wireOp",EDGE,"E137"),sQuery(id+"F0.wireOp",EDGE,"E138"),sQuery(id+"F0.wireOp",EDGE,"E139"),sQuery(id+"F0.wireOp",EDGE,"E140"),sQuery(id+"F0.wireOp",EDGE,"E141"),sQuery(id+"F0.wireOp",EDGE,"E142"),sQuery(id+"F0.wireOp",EDGE,"E143"),sQuery(id+"F0.wireOp",EDGE,"E144"),sQuery(id+"F0.wireOp",EDGE,"E145"),sQuery(id+"F0.wireOp",EDGE,"E146"),sQuery(id+"F0.wireOp",EDGE,"E147"),sQuery(id+"F0.wireOp",EDGE,"E148"),sQuery(id+"F0.wireOp",EDGE,"E149"),sQuery(id+"F0.wireOp",EDGE,"E150"),sQuery(id+"F0.wireOp",EDGE,"E151"),sQuery(id+"F0.wireOp",EDGE,"E152"),sQuery(id+"F0.wireOp",EDGE,"E153"),sQuery(id+"F0.wireOp",EDGE,"E154"),sQuery(id+"F0.wireOp",EDGE,"E155"),sQuery(id+"F0.wireOp",EDGE,"E156"),sQuery(id+"F0.wireOp",EDGE,"E157"),sQuery(id+"F0.wireOp",EDGE,"E158"),sQuery(id+"F0.wireOp",EDGE,"E159"),sQuery(id+"F0.wireOp",EDGE,"E160"),sQuery(id+"F0.wireOp",EDGE,"E161"),sQuery(id+"F0.wireOp",EDGE,"E162"),sQuery(id+"F0.wireOp",EDGE,"E163"),sQuery(id+"F0.wireOp",EDGE,"E164"),sQuery(id+"F0.wireOp",EDGE,"E165"),sQuery(id+"F0.wireOp",EDGE,"E166"),sQuery(id+"F0.wireOp",EDGE,"E167"),sQuery(id+"F0.wireOp",EDGE,"E168"),sQuery(id+"F0.wireOp",EDGE,"E169"),sQuery(id+"F0.wireOp",EDGE,"E170"),sQuery(id+"F0.wireOp",EDGE,"E171"),sQuery(id+"F0.wireOp",EDGE,"E172"),sQuery(id+"F0.wireOp",EDGE,"E173"),sQuery(id+"F0.wireOp",EDGE,"E174"),sQuery(id+"F0.wireOp",EDGE,"E175"),sQuery(id+"F0.wireOp",EDGE,"E176"),sQuery(id+"F0.wireOp",EDGE,"E177"),sQuery(id+"F0.wireOp",EDGE,"E178"),sQuery(id+"F0.wireOp",EDGE,"E179"),sQuery(id+"F0.wireOp",EDGE,"E180"),sQuery(id+"F0.wireOp",EDGE,"E181"),sQuery(id+"F0.wireOp",EDGE,"E182"),sQuery(id+"F0.wireOp",EDGE,"E183"),sQuery(id+"F0.wireOp",EDGE,"E184"),sQuery(id+"F0.wireOp",EDGE,"E185"),sQuery(id+"F0.wireOp",EDGE,"E186")])],"isStart":false})});
            var sketch = newSketch(context, id + "F20", { "sketchPlane" : qUnion([Q0])});
            skLineSegment(sketch, "E207", {"start": v(32, 29) * mm, "end": v(47, 29) * mm});
            skLineSegment(sketch, "E208", {"start": v(49, 27) * mm, "end": v(49, 12) * mm});
            skPoint(sketch, "E209.visualSharp", {"position": v(49, 29) * mm});
            skArc(sketch, "E209.filletArc", {"start": v(49, 27) * mm, "mid": v(48.42, 28.4) * mm, "end": v(47, 29) * mm});
            skLineSegment(sketch, "E210", {"start": v(32, 29) * mm, "end": v(32, 30) * mm});
            skLineSegment(sketch, "E211", {"start": v(32, 30) * mm, "end": v(47, 30) * mm});
            skLineSegment(sketch, "E212", {"start": v(50, 27) * mm, "end": v(50, 12) * mm});
            skLineSegment(sketch, "E213", {"start": v(50, 12) * mm, "end": v(49, 12) * mm});
            skPoint(sketch, "E214.visualSharp", {"position": v(50, 30) * mm});
            skArc(sketch, "E214.filletArc", {"start": v(50, 27) * mm, "mid": v(49.13, 29.11) * mm, "end": v(47, 30) * mm});
            skLineSegment(sketch, "E215", {"start": v(49, -12) * mm, "end": v(49, -27) * mm});
            skLineSegment(sketch, "E216", {"start": v(47, -29) * mm, "end": v(32, -29) * mm});
            skArc(sketch, "E217.filletArc", {"start": v(47, -29) * mm, "mid": v(48.42, -28.42) * mm, "end": v(49, -27) * mm});
            skLineSegment(sketch, "E218", {"start": v(49, -12) * mm, "end": v(50, -12) * mm});
            skLineSegment(sketch, "E219", {"start": v(50, -12) * mm, "end": v(50, -27) * mm});
            skLineSegment(sketch, "E220", {"start": v(47, -30) * mm, "end": v(32, -30) * mm});
            skLineSegment(sketch, "E221", {"start": v(32, -30) * mm, "end": v(32, -29) * mm});
            skArc(sketch, "E222.filletArc", {"start": v(47, -30) * mm, "mid": v(49.13, -29.13) * mm, "end": v(50, -27) * mm});
            skLineSegment(sketch, "E223", {"start": v(-32, -29) * mm, "end": v(-47, -29) * mm});
            skLineSegment(sketch, "E224", {"start": v(-49, -27) * mm, "end": v(-49, -12) * mm});
            skArc(sketch, "E225.filletArc", {"start": v(-49, -27) * mm, "mid": v(-48.41, -28.42) * mm, "end": v(-47, -29) * mm});
            skLineSegment(sketch, "E226", {"start": v(-32, -29) * mm, "end": v(-32, -30) * mm});
            skLineSegment(sketch, "E227", {"start": v(-32, -30) * mm, "end": v(-47, -30) * mm});
            skLineSegment(sketch, "E228", {"start": v(-50, -27) * mm, "end": v(-50, -12) * mm});
            skLineSegment(sketch, "E229", {"start": v(-50, -12) * mm, "end": v(-49, -12) * mm});
            skArc(sketch, "E230.filletArc", {"start": v(-50, -27) * mm, "mid": v(-49.12, -29.13) * mm, "end": v(-47, -30) * mm});
            skLineSegment(sketch, "E231", {"start": v(-49, 12) * mm, "end": v(-49, 27) * mm});
            skLineSegment(sketch, "E232", {"start": v(-47, 29) * mm, "end": v(-32, 29) * mm});
            skArc(sketch, "E233.filletArc", {"start": v(-47, 29) * mm, "mid": v(-48.41, 28.4) * mm, "end": v(-49, 27) * mm});
            skLineSegment(sketch, "E234", {"start": v(-49, 12) * mm, "end": v(-50, 12) * mm});
            skLineSegment(sketch, "E235", {"start": v(-50, 12) * mm, "end": v(-50, 27) * mm});
            skLineSegment(sketch, "E236", {"start": v(-47, 30) * mm, "end": v(-32, 30) * mm});
            skLineSegment(sketch, "E237", {"start": v(-32, 30) * mm, "end": v(-32, 29) * mm});
            skArc(sketch, "E238.filletArc", {"start": v(-47, 30) * mm, "mid": v(-49.12, 29.11) * mm, "end": v(-50, 27) * mm});
            skSolve(sketch);
        }
        {
            var Q0;
            {var subQ9=sQuery(id+"F20.wireOp",EDGE,"E227");Q0=makeQuery(id+"F20.imprint","IMPRINT",FACE,{"disambiguationData":[TD([[makeQuery(id+"F20.imprint","IMPRINT",EDGE,{"derivedFrom":subQ9}),-1.0]])]});}
            var Q1;
            {var subQ9=sQuery(id+"F20.wireOp",EDGE,"E223");Q1=makeQuery(id+"F20.imprint","IMPRINT",FACE,{"disambiguationData":[TD([[makeQuery(id+"F20.imprint","IMPRINT",EDGE,{"derivedFrom":subQ9}),1.0]])]});}
            var Q2;
            Q2=sQuery(id+"F20.wireOp",EDGE,"E229");
            var Q3;
            Q3=sQuery(id+"F20.wireOp",EDGE,"E228");
            var Q4;
            Q4=sQuery(id+"F20.wireOp",EDGE,"E224");
            var Q5;
            Q5=sQuery(id+"F20.wireOp",EDGE,"E230.filletArc");
            var Q6;
            Q6=sQuery(id+"F20.wireOp",EDGE,"E225.filletArc");
            var Q7;
            Q7=sQuery(id+"F20.wireOp",EDGE,"E223");
            var Q8;
            Q8=sQuery(id+"F20.wireOp",EDGE,"E226");
            var Q9;
            Q9=sQuery(id+"F20.wireOp",EDGE,"E227");
            extrude(context, id + "F21", {"entities" : qUnion([Q0, Q1]), "surfaceEntities" : qUnion([Q2, Q3, Q4, Q5, Q6, Q7, Q8, Q9]), "depth" : 20 * mm, "offsetDistance" : 25 * mm, "hasDraft" : true, "draftAngle" : 2 * degree});
        }
        {
            var Q0;
            {var subQ17=sQuery(id+"F20.wireOp",EDGE,"E216");Q0=makeQuery(id+"F20.imprint","IMPRINT",FACE,{"disambiguationData":[TD([[makeQuery(id+"F20.imprint","IMPRINT",EDGE,{"derivedFrom":subQ17}),1.0]])]});}
            var Q1;
            {var subQ8=sQuery(id+"F20.wireOp",EDGE,"E219");Q1=makeQuery(id+"F20.imprint","IMPRINT",FACE,{"disambiguationData":[TD([[makeQuery(id+"F20.imprint","IMPRINT",EDGE,{"derivedFrom":subQ8}),-1.0]])]});}
            extrude(context, id + "F22", {"entities" : qUnion([Q0, Q1]), "depth" : 20 * mm, "offsetDistance" : 25 * mm, "hasDraft" : true, "draftAngle" : 2 * degree});
        }
        {
            var Q0;
            {var subQ8=sQuery(id+"F20.wireOp",EDGE,"E211");Q0=makeQuery(id+"F20.imprint","IMPRINT",FACE,{"disambiguationData":[TD([[makeQuery(id+"F20.imprint","IMPRINT",EDGE,{"derivedFrom":subQ8}),-1.0]])]});}
            var Q1;
            {var subQ14=sQuery(id+"F20.wireOp",EDGE,"E209.filletArc");Q1=makeQuery(id+"F20.imprint","IMPRINT",FACE,{"disambiguationData":[TD([[makeQuery(id+"F20.imprint","IMPRINT",EDGE,{"derivedFrom":subQ14}),-1.0]])]});}
            extrude(context, id + "F23", {"entities" : qUnion([Q0, Q1]), "depth" : 20 * mm, "offsetDistance" : 25 * mm, "hasDraft" : true, "draftAngle" : 2 * degree});
        }
        {
            var Q0;
            {var subQ8=sQuery(id+"F20.wireOp",EDGE,"E235");Q0=makeQuery(id+"F20.imprint","IMPRINT",FACE,{"disambiguationData":[TD([[makeQuery(id+"F20.imprint","IMPRINT",EDGE,{"derivedFrom":subQ8}),-1.0]])]});}
            var Q1;
            {var subQ14=sQuery(id+"F20.wireOp",EDGE,"E233.filletArc");Q1=makeQuery(id+"F20.imprint","IMPRINT",FACE,{"disambiguationData":[TD([[makeQuery(id+"F20.imprint","IMPRINT",EDGE,{"derivedFrom":subQ14}),-1.0]])]});}
            extrude(context, id + "F24", {"entities" : qUnion([Q0, Q1]), "depth" : 20 * mm, "offsetDistance" : 25 * mm, "hasDraft" : true, "draftAngle" : 2 * degree});
        }
        {
            var Q0;
            Q0=makeQuery(id+"F24.opExtrude","CAP_FACE",FACE,{"disambiguationData":[OSD([sQuery(id+"F20.wireOp",EDGE,"E231"),sQuery(id+"F20.wireOp",EDGE,"E232"),sQuery(id+"F20.wireOp",EDGE,"E233.filletArc"),sQuery(id+"F20.wireOp",EDGE,"E234"),sQuery(id+"F20.wireOp",EDGE,"E235"),sQuery(id+"F20.wireOp",EDGE,"E236"),sQuery(id+"F20.wireOp",EDGE,"E237"),sQuery(id+"F20.wireOp",EDGE,"E238.filletArc")])],"isStart":false});
            var sketch = newSketch(context, id + "F25", { "sketchPlane" : qUnion([Q0])});
            skLineSegment(sketch, "E239", {"start": v(-49.62, 29.6) * mm, "end": v(-47, 27) * mm, "construction": true});
            skLineSegment(sketch, "E240.bottom", {"start": v(-50.8, 27) * mm, "end": v(-48.1, 27) * mm});
            skLineSegment(sketch, "E240.top", {"start": v(-50.8, 25) * mm, "end": v(-48.1, 25) * mm});
            skLineSegment(sketch, "E240.left", {"start": v(-50.8, 27) * mm, "end": v(-50.8, 25) * mm});
            skLineSegment(sketch, "E240.right", {"start": v(-48.1, 27) * mm, "end": v(-48.1, 25) * mm});
            skLineSegment(sketch, "E241.1.0.0", {"start": v(-50.84, 23) * mm, "end": v(-50.84, 21) * mm});
            skLineSegment(sketch, "E241.1.0.1", {"start": v(-48.14, 23) * mm, "end": v(-48.14, 21) * mm});
            skLineSegment(sketch, "E241.1.0.2", {"start": v(-50.84, 23) * mm, "end": v(-48.14, 23) * mm});
            skLineSegment(sketch, "E241.1.0.3", {"start": v(-50.84, 21) * mm, "end": v(-48.14, 21) * mm});
            skLineSegment(sketch, "E241.2.0.0", {"start": v(-50.88, 19) * mm, "end": v(-50.88, 17) * mm});
            skLineSegment(sketch, "E241.2.0.1", {"start": v(-48.18, 19) * mm, "end": v(-48.18, 17) * mm});
            skLineSegment(sketch, "E241.2.0.2", {"start": v(-50.88, 19) * mm, "end": v(-48.18, 19) * mm});
            skLineSegment(sketch, "E241.2.0.3", {"start": v(-50.88, 17) * mm, "end": v(-48.18, 17) * mm});
            skLineSegment(sketch, "E241.3.0.0", {"start": v(-50.82, 15) * mm, "end": v(-50.82, 13) * mm});
            skLineSegment(sketch, "E241.3.0.1", {"start": v(-48.12, 15) * mm, "end": v(-48.12, 13) * mm});
            skLineSegment(sketch, "E241.3.0.2", {"start": v(-50.82, 15) * mm, "end": v(-48.12, 15) * mm});
            skLineSegment(sketch, "E241.3.0.3", {"start": v(-50.82, 13) * mm, "end": v(-48.12, 13) * mm});
            skLineSegment(sketch, "E242", {"start": v(50.78, -27) * mm, "end": v(48.2, -27) * mm});
            skLineSegment(sketch, "E243", {"start": v(48.2, -27) * mm, "end": v(48.2, -25) * mm});
            skLineSegment(sketch, "E244", {"start": v(48.2, -25) * mm, "end": v(50.78, -25) * mm});
            skLineSegment(sketch, "E245", {"start": v(50.78, -25) * mm, "end": v(50.78, -27) * mm});
            skLineSegment(sketch, "E246.1.0.0", {"start": v(50.78, -23) * mm, "end": v(48.2, -23) * mm});
            skLineSegment(sketch, "E246.1.0.1", {"start": v(48.2, -23) * mm, "end": v(48.2, -21) * mm});
            skLineSegment(sketch, "E246.1.0.2", {"start": v(50.78, -21) * mm, "end": v(50.78, -23) * mm});
            skLineSegment(sketch, "E246.1.0.3", {"start": v(48.2, -21) * mm, "end": v(50.78, -21) * mm});
            skLineSegment(sketch, "E246.2.0.0", {"start": v(50.8, -19) * mm, "end": v(48.2, -19) * mm});
            skLineSegment(sketch, "E246.2.0.1", {"start": v(48.2, -19) * mm, "end": v(48.2, -17) * mm});
            skLineSegment(sketch, "E246.2.0.2", {"start": v(50.8, -17) * mm, "end": v(50.8, -19) * mm});
            skLineSegment(sketch, "E246.2.0.3", {"start": v(48.2, -17) * mm, "end": v(50.8, -17) * mm});
            skLineSegment(sketch, "E246.3.0.0", {"start": v(50.8, -15) * mm, "end": v(48.22, -15) * mm});
            skLineSegment(sketch, "E246.3.0.1", {"start": v(48.22, -15) * mm, "end": v(48.22, -13) * mm});
            skLineSegment(sketch, "E246.3.0.2", {"start": v(50.8, -13) * mm, "end": v(50.8, -15) * mm});
            skLineSegment(sketch, "E246.3.0.3", {"start": v(48.22, -13) * mm, "end": v(50.8, -13) * mm});
            skLineSegment(sketch, "E246.direction1", {"start": v(48.2, -27) * mm, "end": v(48.2, -23) * mm, "construction": true});
            skLineSegment(sketch, "E247", {"start": v(47, -28.23) * mm, "end": v(47, -30.91) * mm});
            skLineSegment(sketch, "E248", {"start": v(47, -30.91) * mm, "end": v(45, -30.91) * mm});
            skLineSegment(sketch, "E249", {"start": v(45, -30.91) * mm, "end": v(45, -28.21) * mm});
            skLineSegment(sketch, "E250", {"start": v(45, -28.21) * mm, "end": v(47, -28.23) * mm});
            skLineSegment(sketch, "E251.1.0.0", {"start": v(43, -28.21) * mm, "end": v(43, -30.9) * mm});
            skLineSegment(sketch, "E251.1.0.1", {"start": v(41, -30.9) * mm, "end": v(41, -28.2) * mm});
            skLineSegment(sketch, "E251.1.0.2", {"start": v(41, -28.2) * mm, "end": v(43, -28.21) * mm});
            skLineSegment(sketch, "E251.1.0.3", {"start": v(43, -30.9) * mm, "end": v(41, -30.9) * mm});
            skLineSegment(sketch, "E251.2.0.0", {"start": v(39, -28.2) * mm, "end": v(39, -30.89) * mm});
            skLineSegment(sketch, "E251.2.0.1", {"start": v(37, -30.89) * mm, "end": v(37, -28.19) * mm});
            skLineSegment(sketch, "E251.2.0.2", {"start": v(37, -28.19) * mm, "end": v(39, -28.2) * mm});
            skLineSegment(sketch, "E251.2.0.3", {"start": v(39, -30.89) * mm, "end": v(37, -30.89) * mm});
            skLineSegment(sketch, "E251.3.0.0", {"start": v(35, -28.19) * mm, "end": v(35, -30.88) * mm});
            skLineSegment(sketch, "E251.3.0.1", {"start": v(33, -30.88) * mm, "end": v(33, -28.17) * mm});
            skLineSegment(sketch, "E251.3.0.2", {"start": v(33, -28.17) * mm, "end": v(35, -28.19) * mm});
            skLineSegment(sketch, "E251.3.0.3", {"start": v(35, -30.88) * mm, "end": v(33, -30.88) * mm});
            skLineSegment(sketch, "E251.direction1", {"start": v(45, -30.91) * mm, "end": v(41, -30.9) * mm, "construction": true});
            skLineSegment(sketch, "E252.bottom", {"start": v(-47, -28.18) * mm, "end": v(-45, -28.18) * mm});
            skLineSegment(sketch, "E252.top", {"start": v(-47, -30.87) * mm, "end": v(-45, -30.87) * mm});
            skLineSegment(sketch, "E252.left", {"start": v(-47, -28.18) * mm, "end": v(-47, -30.87) * mm});
            skLineSegment(sketch, "E252.right", {"start": v(-45, -28.18) * mm, "end": v(-45, -30.87) * mm});
            skLineSegment(sketch, "E253.1.0.0", {"start": v(-43, -30.88) * mm, "end": v(-41, -30.88) * mm});
            skLineSegment(sketch, "E253.1.0.1", {"start": v(-43, -28.19) * mm, "end": v(-43, -30.88) * mm});
            skLineSegment(sketch, "E253.1.0.2", {"start": v(-41, -28.19) * mm, "end": v(-41, -30.88) * mm});
            skLineSegment(sketch, "E253.1.0.3", {"start": v(-43, -28.19) * mm, "end": v(-41, -28.19) * mm});
            skLineSegment(sketch, "E253.2.0.0", {"start": v(-39, -30.89) * mm, "end": v(-37, -30.89) * mm});
            skLineSegment(sketch, "E253.2.0.1", {"start": v(-39, -28.2) * mm, "end": v(-39, -30.89) * mm});
            skLineSegment(sketch, "E253.2.0.2", {"start": v(-37, -28.2) * mm, "end": v(-37, -30.89) * mm});
            skLineSegment(sketch, "E253.2.0.3", {"start": v(-39, -28.2) * mm, "end": v(-37, -28.2) * mm});
            skLineSegment(sketch, "E253.3.0.0", {"start": v(-35, -30.9) * mm, "end": v(-33, -30.9) * mm});
            skLineSegment(sketch, "E253.3.0.1", {"start": v(-35, -28.2) * mm, "end": v(-35, -30.9) * mm});
            skLineSegment(sketch, "E253.3.0.2", {"start": v(-33, -28.2) * mm, "end": v(-33, -30.9) * mm});
            skLineSegment(sketch, "E253.3.0.3", {"start": v(-35, -28.2) * mm, "end": v(-33, -28.2) * mm});
            skLineSegment(sketch, "E253.direction1", {"start": v(-47, -30.87) * mm, "end": v(-43, -30.88) * mm, "construction": true});
            skLineSegment(sketch, "E254.bottom", {"start": v(-50.8, -27) * mm, "end": v(-48.15, -27) * mm});
            skLineSegment(sketch, "E254.top", {"start": v(-50.8, -25) * mm, "end": v(-48.15, -25) * mm});
            skLineSegment(sketch, "E254.left", {"start": v(-50.8, -27) * mm, "end": v(-50.8, -25) * mm});
            skLineSegment(sketch, "E254.right", {"start": v(-48.15, -27) * mm, "end": v(-48.15, -25) * mm});
            skLineSegment(sketch, "E255.1.0.0", {"start": v(-48.15, -23) * mm, "end": v(-48.15, -21) * mm});
            skLineSegment(sketch, "E255.1.0.1", {"start": v(-50.8, -23) * mm, "end": v(-48.15, -23) * mm});
            skLineSegment(sketch, "E255.1.0.2", {"start": v(-50.8, -23) * mm, "end": v(-50.8, -21) * mm});
            skLineSegment(sketch, "E255.1.0.3", {"start": v(-50.8, -21) * mm, "end": v(-48.15, -21) * mm});
            skLineSegment(sketch, "E255.2.0.0", {"start": v(-48.15, -19) * mm, "end": v(-48.15, -17) * mm});
            skLineSegment(sketch, "E255.2.0.1", {"start": v(-50.8, -19) * mm, "end": v(-48.15, -19) * mm});
            skLineSegment(sketch, "E255.2.0.2", {"start": v(-50.8, -19) * mm, "end": v(-50.8, -17) * mm});
            skLineSegment(sketch, "E255.2.0.3", {"start": v(-50.8, -17) * mm, "end": v(-48.15, -17) * mm});
            skLineSegment(sketch, "E255.3.0.0", {"start": v(-48.15, -15) * mm, "end": v(-48.15, -13) * mm});
            skLineSegment(sketch, "E255.3.0.1", {"start": v(-50.8, -15) * mm, "end": v(-48.15, -15) * mm});
            skLineSegment(sketch, "E255.3.0.2", {"start": v(-50.8, -15) * mm, "end": v(-50.8, -13) * mm});
            skLineSegment(sketch, "E255.3.0.3", {"start": v(-50.8, -13) * mm, "end": v(-48.15, -13) * mm});
            skLineSegment(sketch, "E255.direction1", {"start": v(-50.8, -27) * mm, "end": v(-50.8, -23) * mm, "construction": true});
            skLineSegment(sketch, "E256.bottom", {"start": v(-47, 30.77) * mm, "end": v(-45, 30.77) * mm});
            skLineSegment(sketch, "E256.top", {"start": v(-47, 28.2) * mm, "end": v(-45, 28.2) * mm});
            skLineSegment(sketch, "E256.left", {"start": v(-47, 30.77) * mm, "end": v(-47, 28.2) * mm});
            skLineSegment(sketch, "E256.right", {"start": v(-45, 30.77) * mm, "end": v(-45, 28.2) * mm});
            skLineSegment(sketch, "E257.bottom", {"start": v(-43, 30.77) * mm, "end": v(-41, 30.77) * mm});
            skLineSegment(sketch, "E257.top", {"start": v(-43, 28.2) * mm, "end": v(-41, 28.2) * mm});
            skLineSegment(sketch, "E257.left", {"start": v(-43, 30.77) * mm, "end": v(-43, 28.2) * mm});
            skLineSegment(sketch, "E257.right", {"start": v(-41, 30.77) * mm, "end": v(-41, 28.2) * mm});
            skLineSegment(sketch, "E258.bottom", {"start": v(-39, 30.77) * mm, "end": v(-37, 30.77) * mm});
            skLineSegment(sketch, "E258.top", {"start": v(-39, 28.2) * mm, "end": v(-37, 28.2) * mm});
            skLineSegment(sketch, "E258.left", {"start": v(-39, 30.77) * mm, "end": v(-39, 28.2) * mm});
            skLineSegment(sketch, "E258.right", {"start": v(-37, 30.77) * mm, "end": v(-37, 28.2) * mm});
            skLineSegment(sketch, "E259.bottom", {"start": v(-35, 30.77) * mm, "end": v(-33, 30.77) * mm});
            skLineSegment(sketch, "E259.top", {"start": v(-35, 28.2) * mm, "end": v(-33, 28.2) * mm});
            skLineSegment(sketch, "E259.left", {"start": v(-35, 30.77) * mm, "end": v(-35, 28.2) * mm});
            skLineSegment(sketch, "E259.right", {"start": v(-33, 30.77) * mm, "end": v(-33, 28.2) * mm});
            skLineSegment(sketch, "E260.bottom", {"start": v(47, 30.77) * mm, "end": v(45, 30.77) * mm});
            skLineSegment(sketch, "E260.top", {"start": v(47, 28.2) * mm, "end": v(45, 28.2) * mm});
            skLineSegment(sketch, "E260.left", {"start": v(47, 30.77) * mm, "end": v(47, 28.2) * mm});
            skLineSegment(sketch, "E260.right", {"start": v(45, 30.77) * mm, "end": v(45, 28.2) * mm});
            skLineSegment(sketch, "E261.bottom", {"start": v(43, 30.77) * mm, "end": v(41, 30.77) * mm});
            skLineSegment(sketch, "E261.top", {"start": v(43, 28.2) * mm, "end": v(41, 28.2) * mm});
            skLineSegment(sketch, "E261.left", {"start": v(43, 30.77) * mm, "end": v(43, 28.2) * mm});
            skLineSegment(sketch, "E261.right", {"start": v(41, 30.77) * mm, "end": v(41, 28.2) * mm});
            skLineSegment(sketch, "E262.bottom", {"start": v(39, 30.77) * mm, "end": v(37, 30.77) * mm});
            skLineSegment(sketch, "E262.top", {"start": v(39, 28.2) * mm, "end": v(37, 28.2) * mm});
            skLineSegment(sketch, "E262.left", {"start": v(39, 30.77) * mm, "end": v(39, 28.2) * mm});
            skLineSegment(sketch, "E262.right", {"start": v(37, 30.77) * mm, "end": v(37, 28.2) * mm});
            skLineSegment(sketch, "E263.bottom", {"start": v(35, 30.77) * mm, "end": v(33, 30.77) * mm});
            skLineSegment(sketch, "E263.top", {"start": v(35, 28.2) * mm, "end": v(33, 28.2) * mm});
            skLineSegment(sketch, "E263.left", {"start": v(35, 30.77) * mm, "end": v(35, 28.2) * mm});
            skLineSegment(sketch, "E263.right", {"start": v(33, 30.77) * mm, "end": v(33, 28.2) * mm});
            skLineSegment(sketch, "E264.bottom", {"start": v(50.82, 27) * mm, "end": v(48.17, 27) * mm});
            skLineSegment(sketch, "E264.top", {"start": v(50.82, 25) * mm, "end": v(48.17, 25) * mm});
            skLineSegment(sketch, "E264.left", {"start": v(50.82, 27) * mm, "end": v(50.82, 25) * mm});
            skLineSegment(sketch, "E264.right", {"start": v(48.17, 27) * mm, "end": v(48.17, 25) * mm});
            skLineSegment(sketch, "E265.bottom", {"start": v(50.87, 23) * mm, "end": v(48.22, 23) * mm});
            skLineSegment(sketch, "E265.top", {"start": v(50.87, 21) * mm, "end": v(48.22, 21) * mm});
            skLineSegment(sketch, "E265.left", {"start": v(50.87, 23) * mm, "end": v(50.87, 21) * mm});
            skLineSegment(sketch, "E265.right", {"start": v(48.22, 23) * mm, "end": v(48.22, 21) * mm});
            skLineSegment(sketch, "E266.bottom", {"start": v(50.87, 19) * mm, "end": v(48.22, 19) * mm});
            skLineSegment(sketch, "E266.top", {"start": v(50.87, 17) * mm, "end": v(48.22, 17) * mm});
            skLineSegment(sketch, "E266.left", {"start": v(50.87, 19) * mm, "end": v(50.87, 17) * mm});
            skLineSegment(sketch, "E266.right", {"start": v(48.22, 19) * mm, "end": v(48.22, 17) * mm});
            skLineSegment(sketch, "E267.bottom", {"start": v(50.82, 15) * mm, "end": v(48.17, 15) * mm});
            skLineSegment(sketch, "E267.top", {"start": v(50.82, 13) * mm, "end": v(48.17, 13) * mm});
            skLineSegment(sketch, "E267.left", {"start": v(50.82, 15) * mm, "end": v(50.82, 13) * mm});
            skLineSegment(sketch, "E267.right", {"start": v(48.17, 15) * mm, "end": v(48.17, 13) * mm});
            skSolve(sketch);
        }
        {
            var Q0;
            {var subQ0=sQuery(id+"F25.wireOp",EDGE,"E256.top");Q0=makeQuery(id+"F25.imprint","IMPRINT",FACE,{"disambiguationData":[TD([[makeQuery(id+"F25.imprint","IMPRINT",EDGE,{"derivedFrom":subQ0}),1.0]])]});}
            var Q1;
            {var subQ3=makeQuery(id+"F24.opExtrude","CAP_EDGE",EDGE,{"disambiguationData":[OSD([sQuery(id+"F20.wireOp",EDGE,"E236")])],"isStart":false});var subQ5=sQuery(id+"F25.wireOp",EDGE,"E256.right");var subQ6=makeQuery(id+"F25.imprint","INTERSECT",VERTEX,{"derivedFrom":[subQ3,subQ5]});Q1=makeQuery(id+"F25.imprint","IMPRINT",FACE,{"disambiguationData":[TD([[makeQuery(id+"F25.imprint","IMPRINT",EDGE,{"disambiguationData":[TD([[subQ6,-1.0]])],"derivedFrom":subQ5}),-1.0]])]});}
            var Q2;
            {var subQ0=sQuery(id+"F25.wireOp",EDGE,"E256.bottom");Q2=makeQuery(id+"F25.imprint","IMPRINT",FACE,{"disambiguationData":[TD([[makeQuery(id+"F25.imprint","IMPRINT",EDGE,{"derivedFrom":subQ0}),-1.0]])]});}
            var Q3;
            {var subQ0=sQuery(id+"F25.wireOp",EDGE,"E257.left");var subQ1=makeQuery(id+"F24.opExtrude","CAP_EDGE",EDGE,{"disambiguationData":[OSD([sQuery(id+"F20.wireOp",EDGE,"E236")])],"isStart":false});var subQ2=makeQuery(id+"F25.imprint","INTERSECT",VERTEX,{"derivedFrom":[subQ1,subQ0]});Q3=makeQuery(id+"F25.imprint","IMPRINT",FACE,{"disambiguationData":[TD([[makeQuery(id+"F25.imprint","IMPRINT",EDGE,{"disambiguationData":[TD([[subQ2,-1.0]])],"derivedFrom":subQ0}),1.0]])]});}
            var Q4;
            {var subQ0=sQuery(id+"F25.wireOp",EDGE,"E257.top");Q4=makeQuery(id+"F25.imprint","IMPRINT",FACE,{"disambiguationData":[TD([[makeQuery(id+"F25.imprint","IMPRINT",EDGE,{"derivedFrom":subQ0}),1.0]])]});}
            var Q5;
            {var subQ0=sQuery(id+"F25.wireOp",EDGE,"E257.bottom");Q5=makeQuery(id+"F25.imprint","IMPRINT",FACE,{"disambiguationData":[TD([[makeQuery(id+"F25.imprint","IMPRINT",EDGE,{"derivedFrom":subQ0}),-1.0]])]});}
            var Q6;
            {var subQ0=sQuery(id+"F25.wireOp",EDGE,"E258.top");Q6=makeQuery(id+"F25.imprint","IMPRINT",FACE,{"disambiguationData":[TD([[makeQuery(id+"F25.imprint","IMPRINT",EDGE,{"derivedFrom":subQ0}),1.0]])]});}
            var Q7;
            {var subQ0=sQuery(id+"F25.wireOp",EDGE,"E258.bottom");Q7=makeQuery(id+"F25.imprint","IMPRINT",FACE,{"disambiguationData":[TD([[makeQuery(id+"F25.imprint","IMPRINT",EDGE,{"derivedFrom":subQ0}),-1.0]])]});}
            var Q8;
            {var subQ0=sQuery(id+"F25.wireOp",EDGE,"E258.left");var subQ1=makeQuery(id+"F24.opExtrude","CAP_EDGE",EDGE,{"disambiguationData":[OSD([sQuery(id+"F20.wireOp",EDGE,"E236")])],"isStart":false});var subQ2=makeQuery(id+"F25.imprint","INTERSECT",VERTEX,{"derivedFrom":[subQ1,subQ0]});Q8=makeQuery(id+"F25.imprint","IMPRINT",FACE,{"disambiguationData":[TD([[makeQuery(id+"F25.imprint","IMPRINT",EDGE,{"disambiguationData":[TD([[subQ2,-1.0]])],"derivedFrom":subQ0}),1.0]])]});}
            var Q9;
            {var subQ0=sQuery(id+"F25.wireOp",EDGE,"E259.bottom");Q9=makeQuery(id+"F25.imprint","IMPRINT",FACE,{"disambiguationData":[TD([[makeQuery(id+"F25.imprint","IMPRINT",EDGE,{"derivedFrom":subQ0}),-1.0]])]});}
            var Q10;
            {var subQ0=sQuery(id+"F25.wireOp",EDGE,"E259.left");var subQ1=makeQuery(id+"F24.opExtrude","CAP_EDGE",EDGE,{"disambiguationData":[OSD([sQuery(id+"F20.wireOp",EDGE,"E236")])],"isStart":false});var subQ2=makeQuery(id+"F25.imprint","INTERSECT",VERTEX,{"derivedFrom":[subQ1,subQ0]});Q10=makeQuery(id+"F25.imprint","IMPRINT",FACE,{"disambiguationData":[TD([[makeQuery(id+"F25.imprint","IMPRINT",EDGE,{"disambiguationData":[TD([[subQ2,-1.0]])],"derivedFrom":subQ0}),1.0]])]});}
            var Q11;
            {var subQ0=sQuery(id+"F25.wireOp",EDGE,"E259.top");Q11=makeQuery(id+"F25.imprint","IMPRINT",FACE,{"disambiguationData":[TD([[makeQuery(id+"F25.imprint","IMPRINT",EDGE,{"derivedFrom":subQ0}),1.0]])]});}
            var Q12;
            {var subQ0=sQuery(id+"F25.wireOp",EDGE,"E240.right");Q12=makeQuery(id+"F25.imprint","IMPRINT",FACE,{"disambiguationData":[TD([[makeQuery(id+"F25.imprint","IMPRINT",EDGE,{"derivedFrom":subQ0}),-1.0]])]});}
            var Q13;
            {var subQ0=sQuery(id+"F25.wireOp",EDGE,"E240.left");Q13=makeQuery(id+"F25.imprint","IMPRINT",FACE,{"disambiguationData":[TD([[makeQuery(id+"F25.imprint","IMPRINT",EDGE,{"derivedFrom":subQ0}),1.0]])]});}
            var Q14;
            {var subQ0=sQuery(id+"F25.wireOp",EDGE,"E240.bottom");var subQ1=makeQuery(id+"F24.opExtrude","CAP_EDGE",EDGE,{"disambiguationData":[OSD([sQuery(id+"F20.wireOp",EDGE,"E235")])],"isStart":false});var subQ2=makeQuery(id+"F25.imprint","INTERSECT",VERTEX,{"derivedFrom":[subQ1,subQ0]});Q14=makeQuery(id+"F25.imprint","IMPRINT",FACE,{"disambiguationData":[TD([[makeQuery(id+"F25.imprint","IMPRINT",EDGE,{"disambiguationData":[TD([[subQ2,-1.0]])],"derivedFrom":subQ0}),-1.0]])]});}
            var Q15;
            {var subQ0=sQuery(id+"F25.wireOp",EDGE,"E241.1.0.1");Q15=makeQuery(id+"F25.imprint","IMPRINT",FACE,{"disambiguationData":[TD([[makeQuery(id+"F25.imprint","IMPRINT",EDGE,{"derivedFrom":subQ0}),-1.0]])]});}
            var Q16;
            {var subQ0=sQuery(id+"F25.wireOp",EDGE,"E241.1.0.0");Q16=makeQuery(id+"F25.imprint","IMPRINT",FACE,{"disambiguationData":[TD([[makeQuery(id+"F25.imprint","IMPRINT",EDGE,{"derivedFrom":subQ0}),1.0]])]});}
            var Q17;
            {var subQ0=sQuery(id+"F25.wireOp",EDGE,"E241.1.0.2");var subQ1=makeQuery(id+"F24.opExtrude","CAP_EDGE",EDGE,{"disambiguationData":[OSD([sQuery(id+"F20.wireOp",EDGE,"E235")])],"isStart":false});var subQ2=makeQuery(id+"F25.imprint","INTERSECT",VERTEX,{"derivedFrom":[subQ1,subQ0]});Q17=makeQuery(id+"F25.imprint","IMPRINT",FACE,{"disambiguationData":[TD([[makeQuery(id+"F25.imprint","IMPRINT",EDGE,{"disambiguationData":[TD([[subQ2,-1.0]])],"derivedFrom":subQ0}),-1.0]])]});}
            var Q18;
            {var subQ0=sQuery(id+"F25.wireOp",EDGE,"E241.2.0.0");Q18=makeQuery(id+"F25.imprint","IMPRINT",FACE,{"disambiguationData":[TD([[makeQuery(id+"F25.imprint","IMPRINT",EDGE,{"derivedFrom":subQ0}),1.0]])]});}
            var Q19;
            {var subQ0=sQuery(id+"F25.wireOp",EDGE,"E241.2.0.2");var subQ1=makeQuery(id+"F24.opExtrude","CAP_EDGE",EDGE,{"disambiguationData":[OSD([sQuery(id+"F20.wireOp",EDGE,"E235")])],"isStart":false});var subQ2=makeQuery(id+"F25.imprint","INTERSECT",VERTEX,{"derivedFrom":[subQ1,subQ0]});Q19=makeQuery(id+"F25.imprint","IMPRINT",FACE,{"disambiguationData":[TD([[makeQuery(id+"F25.imprint","IMPRINT",EDGE,{"disambiguationData":[TD([[subQ2,-1.0]])],"derivedFrom":subQ0}),-1.0]])]});}
            var Q20;
            {var subQ0=sQuery(id+"F25.wireOp",EDGE,"E241.2.0.1");Q20=makeQuery(id+"F25.imprint","IMPRINT",FACE,{"disambiguationData":[TD([[makeQuery(id+"F25.imprint","IMPRINT",EDGE,{"derivedFrom":subQ0}),-1.0]])]});}
            var Q21;
            {var subQ0=sQuery(id+"F25.wireOp",EDGE,"E241.3.0.2");var subQ1=makeQuery(id+"F24.opExtrude","CAP_EDGE",EDGE,{"disambiguationData":[OSD([sQuery(id+"F20.wireOp",EDGE,"E235")])],"isStart":false});var subQ2=makeQuery(id+"F25.imprint","INTERSECT",VERTEX,{"derivedFrom":[subQ1,subQ0]});Q21=makeQuery(id+"F25.imprint","IMPRINT",FACE,{"disambiguationData":[TD([[makeQuery(id+"F25.imprint","IMPRINT",EDGE,{"disambiguationData":[TD([[subQ2,-1.0]])],"derivedFrom":subQ0}),-1.0]])]});}
            var Q22;
            {var subQ0=sQuery(id+"F25.wireOp",EDGE,"E241.3.0.0");Q22=makeQuery(id+"F25.imprint","IMPRINT",FACE,{"disambiguationData":[TD([[makeQuery(id+"F25.imprint","IMPRINT",EDGE,{"derivedFrom":subQ0}),1.0]])]});}
            var Q23;
            {var subQ0=sQuery(id+"F25.wireOp",EDGE,"E241.3.0.1");Q23=makeQuery(id+"F25.imprint","IMPRINT",FACE,{"disambiguationData":[TD([[makeQuery(id+"F25.imprint","IMPRINT",EDGE,{"derivedFrom":subQ0}),-1.0]])]});}
            extrude(context, id + "F26", {"entities" : qUnion([Q0, Q1, Q2, Q3, Q4, Q5, Q6, Q7, Q8, Q9, Q10, Q11, Q12, Q13, Q14, Q15, Q16, Q17, Q18, Q19, Q20, Q21, Q22, Q23]), "operationType" : NewBodyOperationType.REMOVE, "depth" : -5 * mm, "offsetDistance" : 25 * mm});
        }
        {
            var Q0;
            Q0=makeQuery(id+"F25.imprint","IMPRINT",FACE,{"disambiguationData":[TD([[makeQuery(id+"F25.imprint","IMPRINT",EDGE,{"derivedFrom":sQuery(id+"F25.wireOp",EDGE,"E255.3.0.0")}),1.0]])]});
            var Q1;
            Q1=makeQuery(id+"F25.imprint","IMPRINT",FACE,{"disambiguationData":[TD([[makeQuery(id+"F25.imprint","IMPRINT",EDGE,{"derivedFrom":sQuery(id+"F25.wireOp",EDGE,"E255.2.0.0")}),1.0]])]});
            var Q2;
            Q2=makeQuery(id+"F25.imprint","IMPRINT",FACE,{"disambiguationData":[TD([[makeQuery(id+"F25.imprint","IMPRINT",EDGE,{"derivedFrom":sQuery(id+"F25.wireOp",EDGE,"E255.1.0.0")}),1.0]])]});
            var Q3;
            Q3=makeQuery(id+"F25.imprint","IMPRINT",FACE,{"disambiguationData":[TD([[makeQuery(id+"F25.imprint","IMPRINT",EDGE,{"derivedFrom":sQuery(id+"F25.wireOp",EDGE,"E254.bottom")}),1.0]])]});
            var Q4;
            Q4=makeQuery(id+"F25.imprint","IMPRINT",FACE,{"disambiguationData":[TD([[makeQuery(id+"F25.imprint","IMPRINT",EDGE,{"derivedFrom":sQuery(id+"F25.wireOp",EDGE,"E252.bottom")}),-1.0]])]});
            var Q5;
            Q5=makeQuery(id+"F25.imprint","IMPRINT",FACE,{"disambiguationData":[TD([[makeQuery(id+"F25.imprint","IMPRINT",EDGE,{"derivedFrom":sQuery(id+"F25.wireOp",EDGE,"E253.1.0.0")}),1.0]])]});
            var Q6;
            Q6=makeQuery(id+"F25.imprint","IMPRINT",FACE,{"disambiguationData":[TD([[makeQuery(id+"F25.imprint","IMPRINT",EDGE,{"derivedFrom":sQuery(id+"F25.wireOp",EDGE,"E253.2.0.0")}),1.0]])]});
            var Q7;
            Q7=makeQuery(id+"F25.imprint","IMPRINT",FACE,{"disambiguationData":[TD([[makeQuery(id+"F25.imprint","IMPRINT",EDGE,{"derivedFrom":sQuery(id+"F25.wireOp",EDGE,"E253.3.0.0")}),1.0]])]});
            extrude(context, id + "F27", {"entities" : qUnion([Q0, Q1, Q2, Q3, Q4, Q5, Q6, Q7]), "operationType" : NewBodyOperationType.REMOVE, "oppositeDirection" : true, "depth" : -5 * mm, "offsetDistance" : 25 * mm});
        }
        {
            var Q0;
            Q0=makeQuery(id+"F25.imprint","IMPRINT",FACE,{"disambiguationData":[TD([[makeQuery(id+"F25.imprint","IMPRINT",EDGE,{"derivedFrom":sQuery(id+"F25.wireOp",EDGE,"E253.3.0.0")}),1.0]])]});
            var Q1;
            Q1=makeQuery(id+"F25.imprint","IMPRINT",FACE,{"disambiguationData":[TD([[makeQuery(id+"F25.imprint","IMPRINT",EDGE,{"derivedFrom":sQuery(id+"F25.wireOp",EDGE,"E253.2.0.0")}),1.0]])]});
            var Q2;
            Q2=makeQuery(id+"F25.imprint","IMPRINT",FACE,{"disambiguationData":[TD([[makeQuery(id+"F25.imprint","IMPRINT",EDGE,{"derivedFrom":sQuery(id+"F25.wireOp",EDGE,"E253.1.0.0")}),1.0]])]});
            var Q3;
            Q3=makeQuery(id+"F25.imprint","IMPRINT",FACE,{"disambiguationData":[TD([[makeQuery(id+"F25.imprint","IMPRINT",EDGE,{"derivedFrom":sQuery(id+"F25.wireOp",EDGE,"E252.bottom")}),-1.0]])]});
            var Q4;
            Q4=makeQuery(id+"F25.imprint","IMPRINT",FACE,{"disambiguationData":[TD([[makeQuery(id+"F25.imprint","IMPRINT",EDGE,{"derivedFrom":sQuery(id+"F25.wireOp",EDGE,"E254.bottom")}),1.0]])]});
            var Q5;
            Q5=makeQuery(id+"F25.imprint","IMPRINT",FACE,{"disambiguationData":[TD([[makeQuery(id+"F25.imprint","IMPRINT",EDGE,{"derivedFrom":sQuery(id+"F25.wireOp",EDGE,"E255.1.0.0")}),1.0]])]});
            var Q6;
            Q6=makeQuery(id+"F25.imprint","IMPRINT",FACE,{"disambiguationData":[TD([[makeQuery(id+"F25.imprint","IMPRINT",EDGE,{"derivedFrom":sQuery(id+"F25.wireOp",EDGE,"E255.2.0.0")}),1.0]])]});
            var Q7;
            Q7=makeQuery(id+"F25.imprint","IMPRINT",FACE,{"disambiguationData":[TD([[makeQuery(id+"F25.imprint","IMPRINT",EDGE,{"derivedFrom":sQuery(id+"F25.wireOp",EDGE,"E255.3.0.0")}),1.0]])]});
            extrude(context, id + "F28", {"entities" : qUnion([Q0, Q1, Q2, Q3, Q4, Q5, Q6, Q7]), "operationType" : NewBodyOperationType.REMOVE, "oppositeDirection" : true, "depth" : 5 * mm, "offsetDistance" : 25 * mm});
        }
        {
            var Q0;
            Q0=makeQuery(id+"F25.imprint","IMPRINT",FACE,{"disambiguationData":[TD([[makeQuery(id+"F25.imprint","IMPRINT",EDGE,{"derivedFrom":sQuery(id+"F25.wireOp",EDGE,"E251.3.0.0")}),-1.0]])]});
            var Q1;
            Q1=makeQuery(id+"F25.imprint","IMPRINT",FACE,{"disambiguationData":[TD([[makeQuery(id+"F25.imprint","IMPRINT",EDGE,{"derivedFrom":sQuery(id+"F25.wireOp",EDGE,"E251.2.0.0")}),-1.0]])]});
            var Q2;
            Q2=makeQuery(id+"F25.imprint","IMPRINT",FACE,{"disambiguationData":[TD([[makeQuery(id+"F25.imprint","IMPRINT",EDGE,{"derivedFrom":sQuery(id+"F25.wireOp",EDGE,"E251.1.0.0")}),-1.0]])]});
            var Q3;
            Q3=makeQuery(id+"F25.imprint","IMPRINT",FACE,{"disambiguationData":[TD([[makeQuery(id+"F25.imprint","IMPRINT",EDGE,{"derivedFrom":sQuery(id+"F25.wireOp",EDGE,"E247")}),-1.0]])]});
            var Q4;
            Q4=makeQuery(id+"F25.imprint","IMPRINT",FACE,{"disambiguationData":[TD([[makeQuery(id+"F25.imprint","IMPRINT",EDGE,{"derivedFrom":sQuery(id+"F25.wireOp",EDGE,"E242")}),-1.0]])]});
            var Q5;
            Q5=makeQuery(id+"F25.imprint","IMPRINT",FACE,{"disambiguationData":[TD([[makeQuery(id+"F25.imprint","IMPRINT",EDGE,{"derivedFrom":sQuery(id+"F25.wireOp",EDGE,"E246.1.0.0")}),-1.0]])]});
            var Q6;
            Q6=makeQuery(id+"F25.imprint","IMPRINT",FACE,{"disambiguationData":[TD([[makeQuery(id+"F25.imprint","IMPRINT",EDGE,{"derivedFrom":sQuery(id+"F25.wireOp",EDGE,"E246.2.0.0")}),-1.0]])]});
            var Q7;
            Q7=makeQuery(id+"F25.imprint","IMPRINT",FACE,{"disambiguationData":[TD([[makeQuery(id+"F25.imprint","IMPRINT",EDGE,{"derivedFrom":sQuery(id+"F25.wireOp",EDGE,"E246.3.0.0")}),-1.0]])]});
            extrude(context, id + "F29", {"entities" : qUnion([Q0, Q1, Q2, Q3, Q4, Q5, Q6, Q7]), "operationType" : NewBodyOperationType.REMOVE, "oppositeDirection" : true, "depth" : 5 * mm, "offsetDistance" : 25 * mm});
        }
        {
            var Q0;
            Q0=makeQuery(id+"F25.imprint","IMPRINT",FACE,{"disambiguationData":[TD([[makeQuery(id+"F25.imprint","IMPRINT",EDGE,{"derivedFrom":sQuery(id+"F25.wireOp",EDGE,"E267.bottom")}),1.0]])]});
            var Q1;
            Q1=makeQuery(id+"F25.imprint","IMPRINT",FACE,{"disambiguationData":[TD([[makeQuery(id+"F25.imprint","IMPRINT",EDGE,{"derivedFrom":sQuery(id+"F25.wireOp",EDGE,"E266.bottom")}),1.0]])]});
            var Q2;
            Q2=makeQuery(id+"F25.imprint","IMPRINT",FACE,{"disambiguationData":[TD([[makeQuery(id+"F25.imprint","IMPRINT",EDGE,{"derivedFrom":sQuery(id+"F25.wireOp",EDGE,"E265.bottom")}),1.0]])]});
            var Q3;
            Q3=makeQuery(id+"F25.imprint","IMPRINT",FACE,{"disambiguationData":[TD([[makeQuery(id+"F25.imprint","IMPRINT",EDGE,{"derivedFrom":sQuery(id+"F25.wireOp",EDGE,"E264.bottom")}),1.0]])]});
            var Q4;
            Q4=makeQuery(id+"F25.imprint","IMPRINT",FACE,{"disambiguationData":[TD([[makeQuery(id+"F25.imprint","IMPRINT",EDGE,{"derivedFrom":sQuery(id+"F25.wireOp",EDGE,"E260.bottom")}),1.0]])]});
            var Q5;
            Q5=makeQuery(id+"F25.imprint","IMPRINT",FACE,{"disambiguationData":[TD([[makeQuery(id+"F25.imprint","IMPRINT",EDGE,{"derivedFrom":sQuery(id+"F25.wireOp",EDGE,"E261.bottom")}),1.0]])]});
            var Q6;
            Q6=makeQuery(id+"F25.imprint","IMPRINT",FACE,{"disambiguationData":[TD([[makeQuery(id+"F25.imprint","IMPRINT",EDGE,{"derivedFrom":sQuery(id+"F25.wireOp",EDGE,"E262.bottom")}),1.0]])]});
            var Q7;
            Q7=makeQuery(id+"F25.imprint","IMPRINT",FACE,{"disambiguationData":[TD([[makeQuery(id+"F25.imprint","IMPRINT",EDGE,{"derivedFrom":sQuery(id+"F25.wireOp",EDGE,"E263.bottom")}),1.0]])]});
            extrude(context, id + "F30", {"entities" : qUnion([Q0, Q1, Q2, Q3, Q4, Q5, Q6, Q7]), "operationType" : NewBodyOperationType.REMOVE, "oppositeDirection" : true, "depth" : 5 * mm, "offsetDistance" : 25 * mm});
        }
        {
            var Q0;
            {var subQ0=sQuery(id+"F20.wireOp",EDGE,"E207");var subQ1=sQuery(id+"F20.wireOp",EDGE,"E210");var subQ2=sQuery(id+"F20.wireOp",EDGE,"E211");Q0=makeQuery(id+"F30.boolean.opBoolean","SPLIT",FACE,{"disambiguationData":[TD([makeQuery(id+"F23.opExtrude","SWEPT_FACE",FACE,{"disambiguationData":[OSD([subQ1])]})])],"derivedFrom":makeQuery(id+"F23.opExtrude","CAP_FACE",FACE,{"disambiguationData":[OSD([subQ0,sQuery(id+"F20.wireOp",EDGE,"E208"),sQuery(id+"F20.wireOp",EDGE,"E209.filletArc"),subQ1,subQ2,sQuery(id+"F20.wireOp",EDGE,"E212"),sQuery(id+"F20.wireOp",EDGE,"E213"),sQuery(id+"F20.wireOp",EDGE,"E214.filletArc")])],"isStart":false})});}
            var Q1;
            {var subQ0=sQuery(id+"F20.wireOp",EDGE,"E207");var subQ1=sQuery(id+"F20.wireOp",EDGE,"E211");Q1=makeQuery(id+"F30.boolean.opBoolean","SPLIT",FACE,{"disambiguationData":[TD([makeQuery(id+"F30.opExtrude","SWEPT_FACE",FACE,{"disambiguationData":[OSD([sQuery(id+"F25.wireOp",EDGE,"E262.right")])]})])],"derivedFrom":makeQuery(id+"F23.opExtrude","CAP_FACE",FACE,{"disambiguationData":[OSD([subQ0,sQuery(id+"F20.wireOp",EDGE,"E208"),sQuery(id+"F20.wireOp",EDGE,"E209.filletArc"),sQuery(id+"F20.wireOp",EDGE,"E210"),subQ1,sQuery(id+"F20.wireOp",EDGE,"E212"),sQuery(id+"F20.wireOp",EDGE,"E213"),sQuery(id+"F20.wireOp",EDGE,"E214.filletArc")])],"isStart":false})});}
            var Q2;
            {var subQ0=sQuery(id+"F20.wireOp",EDGE,"E207");var subQ1=sQuery(id+"F20.wireOp",EDGE,"E211");Q2=makeQuery(id+"F30.boolean.opBoolean","SPLIT",FACE,{"disambiguationData":[TD([makeQuery(id+"F30.opExtrude","SWEPT_FACE",FACE,{"disambiguationData":[OSD([sQuery(id+"F25.wireOp",EDGE,"E261.right")])]})])],"derivedFrom":makeQuery(id+"F23.opExtrude","CAP_FACE",FACE,{"disambiguationData":[OSD([subQ0,sQuery(id+"F20.wireOp",EDGE,"E208"),sQuery(id+"F20.wireOp",EDGE,"E209.filletArc"),sQuery(id+"F20.wireOp",EDGE,"E210"),subQ1,sQuery(id+"F20.wireOp",EDGE,"E212"),sQuery(id+"F20.wireOp",EDGE,"E213"),sQuery(id+"F20.wireOp",EDGE,"E214.filletArc")])],"isStart":false})});}
            var Q3;
            {var subQ0=sQuery(id+"F20.wireOp",EDGE,"E207");var subQ1=sQuery(id+"F20.wireOp",EDGE,"E211");Q3=makeQuery(id+"F30.boolean.opBoolean","SPLIT",FACE,{"disambiguationData":[TD([makeQuery(id+"F30.opExtrude","SWEPT_FACE",FACE,{"disambiguationData":[OSD([sQuery(id+"F25.wireOp",EDGE,"E260.right")])]})])],"derivedFrom":makeQuery(id+"F23.opExtrude","CAP_FACE",FACE,{"disambiguationData":[OSD([subQ0,sQuery(id+"F20.wireOp",EDGE,"E208"),sQuery(id+"F20.wireOp",EDGE,"E209.filletArc"),sQuery(id+"F20.wireOp",EDGE,"E210"),subQ1,sQuery(id+"F20.wireOp",EDGE,"E212"),sQuery(id+"F20.wireOp",EDGE,"E213"),sQuery(id+"F20.wireOp",EDGE,"E214.filletArc")])],"isStart":false})});}
            var Q4;
            Q4=makeQuery(id+"F30.boolean.opBoolean","COPY",EDGE,{"derivedFrom":makeQuery(id+"F30.opExtrude","CAP_EDGE",EDGE,{"disambiguationData":[OSD([sQuery(id+"F25.wireOp",EDGE,"E260.left")])],"isStart":true})});
            var Q5;
            Q5=makeQuery(id+"F30.boolean.opBoolean","COPY",EDGE,{"derivedFrom":makeQuery(id+"F30.opExtrude","CAP_EDGE",EDGE,{"disambiguationData":[OSD([sQuery(id+"F25.wireOp",EDGE,"E264.bottom")])],"isStart":true})});
            var Q6;
            {var subQ0=sQuery(id+"F20.wireOp",EDGE,"E208");var subQ1=sQuery(id+"F20.wireOp",EDGE,"E212");Q6=makeQuery(id+"F30.boolean.opBoolean","SPLIT",FACE,{"disambiguationData":[TD([makeQuery(id+"F30.opExtrude","SWEPT_FACE",FACE,{"disambiguationData":[OSD([sQuery(id+"F25.wireOp",EDGE,"E264.top")])]})])],"derivedFrom":makeQuery(id+"F23.opExtrude","CAP_FACE",FACE,{"disambiguationData":[OSD([sQuery(id+"F20.wireOp",EDGE,"E207"),subQ0,sQuery(id+"F20.wireOp",EDGE,"E209.filletArc"),sQuery(id+"F20.wireOp",EDGE,"E210"),sQuery(id+"F20.wireOp",EDGE,"E211"),subQ1,sQuery(id+"F20.wireOp",EDGE,"E213"),sQuery(id+"F20.wireOp",EDGE,"E214.filletArc")])],"isStart":false})});}
            var Q7;
            {var subQ0=sQuery(id+"F20.wireOp",EDGE,"E208");var subQ1=sQuery(id+"F20.wireOp",EDGE,"E212");Q7=makeQuery(id+"F30.boolean.opBoolean","SPLIT",FACE,{"disambiguationData":[TD([makeQuery(id+"F30.opExtrude","SWEPT_FACE",FACE,{"disambiguationData":[OSD([sQuery(id+"F25.wireOp",EDGE,"E265.top")])]})])],"derivedFrom":makeQuery(id+"F23.opExtrude","CAP_FACE",FACE,{"disambiguationData":[OSD([sQuery(id+"F20.wireOp",EDGE,"E207"),subQ0,sQuery(id+"F20.wireOp",EDGE,"E209.filletArc"),sQuery(id+"F20.wireOp",EDGE,"E210"),sQuery(id+"F20.wireOp",EDGE,"E211"),subQ1,sQuery(id+"F20.wireOp",EDGE,"E213"),sQuery(id+"F20.wireOp",EDGE,"E214.filletArc")])],"isStart":false})});}
            var Q8;
            {var subQ0=sQuery(id+"F20.wireOp",EDGE,"E208");var subQ1=sQuery(id+"F20.wireOp",EDGE,"E212");Q8=makeQuery(id+"F30.boolean.opBoolean","SPLIT",FACE,{"disambiguationData":[TD([makeQuery(id+"F30.opExtrude","SWEPT_FACE",FACE,{"disambiguationData":[OSD([sQuery(id+"F25.wireOp",EDGE,"E266.top")])]})])],"derivedFrom":makeQuery(id+"F23.opExtrude","CAP_FACE",FACE,{"disambiguationData":[OSD([sQuery(id+"F20.wireOp",EDGE,"E207"),subQ0,sQuery(id+"F20.wireOp",EDGE,"E209.filletArc"),sQuery(id+"F20.wireOp",EDGE,"E210"),sQuery(id+"F20.wireOp",EDGE,"E211"),subQ1,sQuery(id+"F20.wireOp",EDGE,"E213"),sQuery(id+"F20.wireOp",EDGE,"E214.filletArc")])],"isStart":false})});}
            var Q9;
            {var subQ0=sQuery(id+"F20.wireOp",EDGE,"E208");var subQ1=sQuery(id+"F20.wireOp",EDGE,"E213");var subQ2=sQuery(id+"F20.wireOp",EDGE,"E212");Q9=makeQuery(id+"F30.boolean.opBoolean","SPLIT",FACE,{"disambiguationData":[TD([makeQuery(id+"F23.opExtrude","SWEPT_FACE",FACE,{"disambiguationData":[OSD([subQ1])]})])],"derivedFrom":makeQuery(id+"F23.opExtrude","CAP_FACE",FACE,{"disambiguationData":[OSD([sQuery(id+"F20.wireOp",EDGE,"E207"),subQ0,sQuery(id+"F20.wireOp",EDGE,"E209.filletArc"),sQuery(id+"F20.wireOp",EDGE,"E210"),sQuery(id+"F20.wireOp",EDGE,"E211"),subQ2,subQ1,sQuery(id+"F20.wireOp",EDGE,"E214.filletArc")])],"isStart":false})});}
            chamfer(context, id + "F31", {"entities" : qUnion([Q0, Q1, Q2, Q3, Q4, Q5, Q6, Q7, Q8, Q9]), "width" : 0.5 * mm, "tangentPropagation" : true});
        }
        {
            var Q0;
            {var subQ0=sQuery(id+"F20.wireOp",EDGE,"E215");var subQ1=sQuery(id+"F20.wireOp",EDGE,"E218");var subQ2=sQuery(id+"F20.wireOp",EDGE,"E219");Q0=makeQuery(id+"F29.boolean.opBoolean","SPLIT",FACE,{"disambiguationData":[TD([makeQuery(id+"F22.opExtrude","SWEPT_FACE",FACE,{"disambiguationData":[OSD([subQ1])]})])],"derivedFrom":makeQuery(id+"F22.opExtrude","CAP_FACE",FACE,{"disambiguationData":[OSD([subQ0,sQuery(id+"F20.wireOp",EDGE,"E216"),sQuery(id+"F20.wireOp",EDGE,"E217.filletArc"),subQ1,subQ2,sQuery(id+"F20.wireOp",EDGE,"E220"),sQuery(id+"F20.wireOp",EDGE,"E221"),sQuery(id+"F20.wireOp",EDGE,"E222.filletArc")])],"isStart":false})});}
            var Q1;
            {var subQ0=sQuery(id+"F20.wireOp",EDGE,"E215");var subQ1=sQuery(id+"F20.wireOp",EDGE,"E219");Q1=makeQuery(id+"F29.boolean.opBoolean","SPLIT",FACE,{"disambiguationData":[TD([makeQuery(id+"F29.opExtrude","SWEPT_FACE",FACE,{"disambiguationData":[OSD([sQuery(id+"F25.wireOp",EDGE,"E246.2.0.3")])]})])],"derivedFrom":makeQuery(id+"F22.opExtrude","CAP_FACE",FACE,{"disambiguationData":[OSD([subQ0,sQuery(id+"F20.wireOp",EDGE,"E216"),sQuery(id+"F20.wireOp",EDGE,"E217.filletArc"),sQuery(id+"F20.wireOp",EDGE,"E218"),subQ1,sQuery(id+"F20.wireOp",EDGE,"E220"),sQuery(id+"F20.wireOp",EDGE,"E221"),sQuery(id+"F20.wireOp",EDGE,"E222.filletArc")])],"isStart":false})});}
            var Q2;
            {var subQ0=sQuery(id+"F20.wireOp",EDGE,"E215");var subQ1=sQuery(id+"F20.wireOp",EDGE,"E219");Q2=makeQuery(id+"F29.boolean.opBoolean","SPLIT",FACE,{"disambiguationData":[TD([makeQuery(id+"F29.opExtrude","SWEPT_FACE",FACE,{"disambiguationData":[OSD([sQuery(id+"F25.wireOp",EDGE,"E246.1.0.3")])]})])],"derivedFrom":makeQuery(id+"F22.opExtrude","CAP_FACE",FACE,{"disambiguationData":[OSD([subQ0,sQuery(id+"F20.wireOp",EDGE,"E216"),sQuery(id+"F20.wireOp",EDGE,"E217.filletArc"),sQuery(id+"F20.wireOp",EDGE,"E218"),subQ1,sQuery(id+"F20.wireOp",EDGE,"E220"),sQuery(id+"F20.wireOp",EDGE,"E221"),sQuery(id+"F20.wireOp",EDGE,"E222.filletArc")])],"isStart":false})});}
            var Q3;
            {var subQ0=sQuery(id+"F20.wireOp",EDGE,"E215");var subQ1=sQuery(id+"F20.wireOp",EDGE,"E219");Q3=makeQuery(id+"F29.boolean.opBoolean","SPLIT",FACE,{"disambiguationData":[TD([makeQuery(id+"F29.opExtrude","SWEPT_FACE",FACE,{"disambiguationData":[OSD([sQuery(id+"F25.wireOp",EDGE,"E244")])]})])],"derivedFrom":makeQuery(id+"F22.opExtrude","CAP_FACE",FACE,{"disambiguationData":[OSD([subQ0,sQuery(id+"F20.wireOp",EDGE,"E216"),sQuery(id+"F20.wireOp",EDGE,"E217.filletArc"),sQuery(id+"F20.wireOp",EDGE,"E218"),subQ1,sQuery(id+"F20.wireOp",EDGE,"E220"),sQuery(id+"F20.wireOp",EDGE,"E221"),sQuery(id+"F20.wireOp",EDGE,"E222.filletArc")])],"isStart":false})});}
            var Q4;
            Q4=makeQuery(id+"F29.boolean.opBoolean","COPY",EDGE,{"derivedFrom":makeQuery(id+"F29.opExtrude","CAP_EDGE",EDGE,{"disambiguationData":[OSD([sQuery(id+"F25.wireOp",EDGE,"E242")])],"isStart":true})});
            var Q5;
            Q5=makeQuery(id+"F29.boolean.opBoolean","COPY",EDGE,{"derivedFrom":makeQuery(id+"F29.opExtrude","CAP_EDGE",EDGE,{"disambiguationData":[OSD([sQuery(id+"F25.wireOp",EDGE,"E247")])],"isStart":true})});
            var Q6;
            {var subQ0=sQuery(id+"F20.wireOp",EDGE,"E216");var subQ1=sQuery(id+"F20.wireOp",EDGE,"E220");Q6=makeQuery(id+"F29.boolean.opBoolean","SPLIT",FACE,{"disambiguationData":[TD([makeQuery(id+"F29.opExtrude","SWEPT_FACE",FACE,{"disambiguationData":[OSD([sQuery(id+"F25.wireOp",EDGE,"E249")])]})])],"derivedFrom":makeQuery(id+"F22.opExtrude","CAP_FACE",FACE,{"disambiguationData":[OSD([sQuery(id+"F20.wireOp",EDGE,"E215"),subQ0,sQuery(id+"F20.wireOp",EDGE,"E217.filletArc"),sQuery(id+"F20.wireOp",EDGE,"E218"),sQuery(id+"F20.wireOp",EDGE,"E219"),subQ1,sQuery(id+"F20.wireOp",EDGE,"E221"),sQuery(id+"F20.wireOp",EDGE,"E222.filletArc")])],"isStart":false})});}
            var Q7;
            {var subQ0=sQuery(id+"F20.wireOp",EDGE,"E216");var subQ1=sQuery(id+"F20.wireOp",EDGE,"E220");Q7=makeQuery(id+"F29.boolean.opBoolean","SPLIT",FACE,{"disambiguationData":[TD([makeQuery(id+"F29.opExtrude","SWEPT_FACE",FACE,{"disambiguationData":[OSD([sQuery(id+"F25.wireOp",EDGE,"E251.1.0.1")])]})])],"derivedFrom":makeQuery(id+"F22.opExtrude","CAP_FACE",FACE,{"disambiguationData":[OSD([sQuery(id+"F20.wireOp",EDGE,"E215"),subQ0,sQuery(id+"F20.wireOp",EDGE,"E217.filletArc"),sQuery(id+"F20.wireOp",EDGE,"E218"),sQuery(id+"F20.wireOp",EDGE,"E219"),subQ1,sQuery(id+"F20.wireOp",EDGE,"E221"),sQuery(id+"F20.wireOp",EDGE,"E222.filletArc")])],"isStart":false})});}
            var Q8;
            {var subQ0=sQuery(id+"F20.wireOp",EDGE,"E216");var subQ1=sQuery(id+"F20.wireOp",EDGE,"E220");Q8=makeQuery(id+"F29.boolean.opBoolean","SPLIT",FACE,{"disambiguationData":[TD([makeQuery(id+"F29.opExtrude","SWEPT_FACE",FACE,{"disambiguationData":[OSD([sQuery(id+"F25.wireOp",EDGE,"E251.2.0.1")])]})])],"derivedFrom":makeQuery(id+"F22.opExtrude","CAP_FACE",FACE,{"disambiguationData":[OSD([sQuery(id+"F20.wireOp",EDGE,"E215"),subQ0,sQuery(id+"F20.wireOp",EDGE,"E217.filletArc"),sQuery(id+"F20.wireOp",EDGE,"E218"),sQuery(id+"F20.wireOp",EDGE,"E219"),subQ1,sQuery(id+"F20.wireOp",EDGE,"E221"),sQuery(id+"F20.wireOp",EDGE,"E222.filletArc")])],"isStart":false})});}
            var Q9;
            {var subQ0=sQuery(id+"F20.wireOp",EDGE,"E216");var subQ1=sQuery(id+"F20.wireOp",EDGE,"E221");var subQ2=sQuery(id+"F20.wireOp",EDGE,"E220");Q9=makeQuery(id+"F29.boolean.opBoolean","SPLIT",FACE,{"disambiguationData":[TD([makeQuery(id+"F22.opExtrude","SWEPT_FACE",FACE,{"disambiguationData":[OSD([subQ1])]})])],"derivedFrom":makeQuery(id+"F22.opExtrude","CAP_FACE",FACE,{"disambiguationData":[OSD([sQuery(id+"F20.wireOp",EDGE,"E215"),subQ0,sQuery(id+"F20.wireOp",EDGE,"E217.filletArc"),sQuery(id+"F20.wireOp",EDGE,"E218"),sQuery(id+"F20.wireOp",EDGE,"E219"),subQ2,subQ1,sQuery(id+"F20.wireOp",EDGE,"E222.filletArc")])],"isStart":false})});}
            chamfer(context, id + "F32", {"entities" : qUnion([Q0, Q1, Q2, Q3, Q4, Q5, Q6, Q7, Q8, Q9]), "width" : 0.5 * mm, "tangentPropagation" : true});
        }
        {
            var Q0;
            {var subQ0=sQuery(id+"F20.wireOp",EDGE,"E223");var subQ1=sQuery(id+"F20.wireOp",EDGE,"E226");var subQ2=sQuery(id+"F20.wireOp",EDGE,"E227");Q0=makeQuery(id+"F28.boolean.opBoolean","SPLIT",FACE,{"disambiguationData":[TD([makeQuery(id+"F21.opExtrude","SWEPT_FACE",FACE,{"disambiguationData":[OSD([subQ1])]})])],"derivedFrom":makeQuery(id+"F21.opExtrude","CAP_FACE",FACE,{"disambiguationData":[OSD([subQ0,sQuery(id+"F20.wireOp",EDGE,"E224"),sQuery(id+"F20.wireOp",EDGE,"E225.filletArc"),subQ1,subQ2,sQuery(id+"F20.wireOp",EDGE,"E228"),sQuery(id+"F20.wireOp",EDGE,"E229"),sQuery(id+"F20.wireOp",EDGE,"E230.filletArc")])],"isStart":false})});}
            var Q1;
            {var subQ0=sQuery(id+"F20.wireOp",EDGE,"E223");var subQ1=sQuery(id+"F20.wireOp",EDGE,"E227");Q1=makeQuery(id+"F28.boolean.opBoolean","SPLIT",FACE,{"disambiguationData":[TD([makeQuery(id+"F28.opExtrude","SWEPT_FACE",FACE,{"disambiguationData":[OSD([sQuery(id+"F25.wireOp",EDGE,"E253.2.0.2")])]})])],"derivedFrom":makeQuery(id+"F21.opExtrude","CAP_FACE",FACE,{"disambiguationData":[OSD([subQ0,sQuery(id+"F20.wireOp",EDGE,"E224"),sQuery(id+"F20.wireOp",EDGE,"E225.filletArc"),sQuery(id+"F20.wireOp",EDGE,"E226"),subQ1,sQuery(id+"F20.wireOp",EDGE,"E228"),sQuery(id+"F20.wireOp",EDGE,"E229"),sQuery(id+"F20.wireOp",EDGE,"E230.filletArc")])],"isStart":false})});}
            var Q2;
            {var subQ0=sQuery(id+"F20.wireOp",EDGE,"E223");var subQ1=sQuery(id+"F20.wireOp",EDGE,"E227");Q2=makeQuery(id+"F28.boolean.opBoolean","SPLIT",FACE,{"disambiguationData":[TD([makeQuery(id+"F28.opExtrude","SWEPT_FACE",FACE,{"disambiguationData":[OSD([sQuery(id+"F25.wireOp",EDGE,"E253.1.0.2")])]})])],"derivedFrom":makeQuery(id+"F21.opExtrude","CAP_FACE",FACE,{"disambiguationData":[OSD([subQ0,sQuery(id+"F20.wireOp",EDGE,"E224"),sQuery(id+"F20.wireOp",EDGE,"E225.filletArc"),sQuery(id+"F20.wireOp",EDGE,"E226"),subQ1,sQuery(id+"F20.wireOp",EDGE,"E228"),sQuery(id+"F20.wireOp",EDGE,"E229"),sQuery(id+"F20.wireOp",EDGE,"E230.filletArc")])],"isStart":false})});}
            var Q3;
            {var subQ0=sQuery(id+"F20.wireOp",EDGE,"E223");var subQ1=sQuery(id+"F20.wireOp",EDGE,"E227");Q3=makeQuery(id+"F28.boolean.opBoolean","SPLIT",FACE,{"disambiguationData":[TD([makeQuery(id+"F28.opExtrude","SWEPT_FACE",FACE,{"disambiguationData":[OSD([sQuery(id+"F25.wireOp",EDGE,"E252.right")])]})])],"derivedFrom":makeQuery(id+"F21.opExtrude","CAP_FACE",FACE,{"disambiguationData":[OSD([subQ0,sQuery(id+"F20.wireOp",EDGE,"E224"),sQuery(id+"F20.wireOp",EDGE,"E225.filletArc"),sQuery(id+"F20.wireOp",EDGE,"E226"),subQ1,sQuery(id+"F20.wireOp",EDGE,"E228"),sQuery(id+"F20.wireOp",EDGE,"E229"),sQuery(id+"F20.wireOp",EDGE,"E230.filletArc")])],"isStart":false})});}
            var Q4;
            {var subQ0=sQuery(id+"F20.wireOp",EDGE,"E224");var subQ1=sQuery(id+"F20.wireOp",EDGE,"E228");Q4=makeQuery(id+"F28.boolean.opBoolean","SPLIT",FACE,{"disambiguationData":[TD([makeQuery(id+"F28.opExtrude","SWEPT_FACE",FACE,{"disambiguationData":[OSD([sQuery(id+"F25.wireOp",EDGE,"E254.top")])]})])],"derivedFrom":makeQuery(id+"F21.opExtrude","CAP_FACE",FACE,{"disambiguationData":[OSD([sQuery(id+"F20.wireOp",EDGE,"E223"),subQ0,sQuery(id+"F20.wireOp",EDGE,"E225.filletArc"),sQuery(id+"F20.wireOp",EDGE,"E226"),sQuery(id+"F20.wireOp",EDGE,"E227"),subQ1,sQuery(id+"F20.wireOp",EDGE,"E229"),sQuery(id+"F20.wireOp",EDGE,"E230.filletArc")])],"isStart":false})});}
            var Q5;
            {var subQ0=sQuery(id+"F20.wireOp",EDGE,"E224");var subQ1=sQuery(id+"F20.wireOp",EDGE,"E228");Q5=makeQuery(id+"F28.boolean.opBoolean","SPLIT",FACE,{"disambiguationData":[TD([makeQuery(id+"F28.opExtrude","SWEPT_FACE",FACE,{"disambiguationData":[OSD([sQuery(id+"F25.wireOp",EDGE,"E255.1.0.3")])]})])],"derivedFrom":makeQuery(id+"F21.opExtrude","CAP_FACE",FACE,{"disambiguationData":[OSD([sQuery(id+"F20.wireOp",EDGE,"E223"),subQ0,sQuery(id+"F20.wireOp",EDGE,"E225.filletArc"),sQuery(id+"F20.wireOp",EDGE,"E226"),sQuery(id+"F20.wireOp",EDGE,"E227"),subQ1,sQuery(id+"F20.wireOp",EDGE,"E229"),sQuery(id+"F20.wireOp",EDGE,"E230.filletArc")])],"isStart":false})});}
            var Q6;
            {var subQ0=sQuery(id+"F20.wireOp",EDGE,"E224");var subQ1=sQuery(id+"F20.wireOp",EDGE,"E228");Q6=makeQuery(id+"F28.boolean.opBoolean","SPLIT",FACE,{"disambiguationData":[TD([makeQuery(id+"F28.opExtrude","SWEPT_FACE",FACE,{"disambiguationData":[OSD([sQuery(id+"F25.wireOp",EDGE,"E255.2.0.3")])]})])],"derivedFrom":makeQuery(id+"F21.opExtrude","CAP_FACE",FACE,{"disambiguationData":[OSD([sQuery(id+"F20.wireOp",EDGE,"E223"),subQ0,sQuery(id+"F20.wireOp",EDGE,"E225.filletArc"),sQuery(id+"F20.wireOp",EDGE,"E226"),sQuery(id+"F20.wireOp",EDGE,"E227"),subQ1,sQuery(id+"F20.wireOp",EDGE,"E229"),sQuery(id+"F20.wireOp",EDGE,"E230.filletArc")])],"isStart":false})});}
            var Q7;
            {var subQ0=sQuery(id+"F20.wireOp",EDGE,"E224");var subQ1=sQuery(id+"F20.wireOp",EDGE,"E229");var subQ2=sQuery(id+"F20.wireOp",EDGE,"E228");Q7=makeQuery(id+"F28.boolean.opBoolean","SPLIT",FACE,{"disambiguationData":[TD([makeQuery(id+"F21.opExtrude","SWEPT_FACE",FACE,{"disambiguationData":[OSD([subQ1])]})])],"derivedFrom":makeQuery(id+"F21.opExtrude","CAP_FACE",FACE,{"disambiguationData":[OSD([sQuery(id+"F20.wireOp",EDGE,"E223"),subQ0,sQuery(id+"F20.wireOp",EDGE,"E225.filletArc"),sQuery(id+"F20.wireOp",EDGE,"E226"),sQuery(id+"F20.wireOp",EDGE,"E227"),subQ2,subQ1,sQuery(id+"F20.wireOp",EDGE,"E230.filletArc")])],"isStart":false})});}
            var Q8;
            Q8=makeQuery(id+"F28.boolean.opBoolean","COPY",EDGE,{"derivedFrom":makeQuery(id+"F28.opExtrude","CAP_EDGE",EDGE,{"disambiguationData":[OSD([sQuery(id+"F25.wireOp",EDGE,"E252.left")])],"isStart":true})});
            var Q9;
            Q9=makeQuery(id+"F28.boolean.opBoolean","COPY",EDGE,{"derivedFrom":makeQuery(id+"F28.opExtrude","CAP_EDGE",EDGE,{"disambiguationData":[OSD([sQuery(id+"F25.wireOp",EDGE,"E254.bottom")])],"isStart":true})});
            chamfer(context, id + "F33", {"entities" : qUnion([Q0, Q1, Q2, Q3, Q4, Q5, Q6, Q7, Q8, Q9]), "width" : 0.5 * mm, "tangentPropagation" : true});
        }
        {
            var Q0;
            {var subQ0=sQuery(id+"F20.wireOp",EDGE,"E232");var subQ1=sQuery(id+"F20.wireOp",EDGE,"E237");var subQ2=sQuery(id+"F20.wireOp",EDGE,"E236");Q0=makeQuery(id+"F26.boolean.opBoolean","SPLIT",FACE,{"disambiguationData":[TD([makeQuery(id+"F24.opExtrude","SWEPT_FACE",FACE,{"disambiguationData":[OSD([subQ1])]})])],"derivedFrom":makeQuery(id+"F24.opExtrude","CAP_FACE",FACE,{"disambiguationData":[OSD([sQuery(id+"F20.wireOp",EDGE,"E231"),subQ0,sQuery(id+"F20.wireOp",EDGE,"E233.filletArc"),sQuery(id+"F20.wireOp",EDGE,"E234"),sQuery(id+"F20.wireOp",EDGE,"E235"),subQ2,subQ1,sQuery(id+"F20.wireOp",EDGE,"E238.filletArc")])],"isStart":false})});}
            var Q1;
            {var subQ0=sQuery(id+"F20.wireOp",EDGE,"E232");var subQ1=sQuery(id+"F20.wireOp",EDGE,"E236");Q1=makeQuery(id+"F26.boolean.opBoolean","SPLIT",FACE,{"disambiguationData":[TD([makeQuery(id+"F26.opExtrude","SWEPT_FACE",FACE,{"disambiguationData":[OSD([sQuery(id+"F25.wireOp",EDGE,"E258.right")])]})])],"derivedFrom":makeQuery(id+"F24.opExtrude","CAP_FACE",FACE,{"disambiguationData":[OSD([sQuery(id+"F20.wireOp",EDGE,"E231"),subQ0,sQuery(id+"F20.wireOp",EDGE,"E233.filletArc"),sQuery(id+"F20.wireOp",EDGE,"E234"),sQuery(id+"F20.wireOp",EDGE,"E235"),subQ1,sQuery(id+"F20.wireOp",EDGE,"E237"),sQuery(id+"F20.wireOp",EDGE,"E238.filletArc")])],"isStart":false})});}
            var Q2;
            {var subQ0=sQuery(id+"F20.wireOp",EDGE,"E232");var subQ1=sQuery(id+"F20.wireOp",EDGE,"E236");Q2=makeQuery(id+"F26.boolean.opBoolean","SPLIT",FACE,{"disambiguationData":[TD([makeQuery(id+"F26.opExtrude","SWEPT_FACE",FACE,{"disambiguationData":[OSD([sQuery(id+"F25.wireOp",EDGE,"E257.right")])]})])],"derivedFrom":makeQuery(id+"F24.opExtrude","CAP_FACE",FACE,{"disambiguationData":[OSD([sQuery(id+"F20.wireOp",EDGE,"E231"),subQ0,sQuery(id+"F20.wireOp",EDGE,"E233.filletArc"),sQuery(id+"F20.wireOp",EDGE,"E234"),sQuery(id+"F20.wireOp",EDGE,"E235"),subQ1,sQuery(id+"F20.wireOp",EDGE,"E237"),sQuery(id+"F20.wireOp",EDGE,"E238.filletArc")])],"isStart":false})});}
            var Q3;
            {var subQ0=sQuery(id+"F20.wireOp",EDGE,"E232");var subQ1=sQuery(id+"F20.wireOp",EDGE,"E236");Q3=makeQuery(id+"F26.boolean.opBoolean","SPLIT",FACE,{"disambiguationData":[TD([makeQuery(id+"F26.opExtrude","SWEPT_FACE",FACE,{"disambiguationData":[OSD([sQuery(id+"F25.wireOp",EDGE,"E256.right")])]})])],"derivedFrom":makeQuery(id+"F24.opExtrude","CAP_FACE",FACE,{"disambiguationData":[OSD([sQuery(id+"F20.wireOp",EDGE,"E231"),subQ0,sQuery(id+"F20.wireOp",EDGE,"E233.filletArc"),sQuery(id+"F20.wireOp",EDGE,"E234"),sQuery(id+"F20.wireOp",EDGE,"E235"),subQ1,sQuery(id+"F20.wireOp",EDGE,"E237"),sQuery(id+"F20.wireOp",EDGE,"E238.filletArc")])],"isStart":false})});}
            var Q4;
            Q4=makeQuery(id+"F26.boolean.opBoolean","COPY",EDGE,{"derivedFrom":makeQuery(id+"F26.opExtrude","CAP_EDGE",EDGE,{"disambiguationData":[OSD([sQuery(id+"F25.wireOp",EDGE,"E256.left")])],"isStart":true})});
            var Q5;
            Q5=makeQuery(id+"F26.boolean.opBoolean","COPY",EDGE,{"derivedFrom":makeQuery(id+"F26.opExtrude","CAP_EDGE",EDGE,{"disambiguationData":[OSD([sQuery(id+"F25.wireOp",EDGE,"E240.bottom")])],"isStart":true})});
            var Q6;
            {var subQ0=sQuery(id+"F20.wireOp",EDGE,"E231");var subQ1=sQuery(id+"F20.wireOp",EDGE,"E235");Q6=makeQuery(id+"F26.boolean.opBoolean","SPLIT",FACE,{"disambiguationData":[TD([makeQuery(id+"F26.opExtrude","SWEPT_FACE",FACE,{"disambiguationData":[OSD([sQuery(id+"F25.wireOp",EDGE,"E240.top")])]})])],"derivedFrom":makeQuery(id+"F24.opExtrude","CAP_FACE",FACE,{"disambiguationData":[OSD([subQ0,sQuery(id+"F20.wireOp",EDGE,"E232"),sQuery(id+"F20.wireOp",EDGE,"E233.filletArc"),sQuery(id+"F20.wireOp",EDGE,"E234"),subQ1,sQuery(id+"F20.wireOp",EDGE,"E236"),sQuery(id+"F20.wireOp",EDGE,"E237"),sQuery(id+"F20.wireOp",EDGE,"E238.filletArc")])],"isStart":false})});}
            var Q7;
            {var subQ0=sQuery(id+"F20.wireOp",EDGE,"E231");var subQ1=sQuery(id+"F20.wireOp",EDGE,"E235");Q7=makeQuery(id+"F26.boolean.opBoolean","SPLIT",FACE,{"disambiguationData":[TD([makeQuery(id+"F26.opExtrude","SWEPT_FACE",FACE,{"disambiguationData":[OSD([sQuery(id+"F25.wireOp",EDGE,"E241.1.0.3")])]})])],"derivedFrom":makeQuery(id+"F24.opExtrude","CAP_FACE",FACE,{"disambiguationData":[OSD([subQ0,sQuery(id+"F20.wireOp",EDGE,"E232"),sQuery(id+"F20.wireOp",EDGE,"E233.filletArc"),sQuery(id+"F20.wireOp",EDGE,"E234"),subQ1,sQuery(id+"F20.wireOp",EDGE,"E236"),sQuery(id+"F20.wireOp",EDGE,"E237"),sQuery(id+"F20.wireOp",EDGE,"E238.filletArc")])],"isStart":false})});}
            var Q8;
            {var subQ0=sQuery(id+"F20.wireOp",EDGE,"E231");var subQ1=sQuery(id+"F20.wireOp",EDGE,"E235");Q8=makeQuery(id+"F26.boolean.opBoolean","SPLIT",FACE,{"disambiguationData":[TD([makeQuery(id+"F26.opExtrude","SWEPT_FACE",FACE,{"disambiguationData":[OSD([sQuery(id+"F25.wireOp",EDGE,"E241.2.0.3")])]})])],"derivedFrom":makeQuery(id+"F24.opExtrude","CAP_FACE",FACE,{"disambiguationData":[OSD([subQ0,sQuery(id+"F20.wireOp",EDGE,"E232"),sQuery(id+"F20.wireOp",EDGE,"E233.filletArc"),sQuery(id+"F20.wireOp",EDGE,"E234"),subQ1,sQuery(id+"F20.wireOp",EDGE,"E236"),sQuery(id+"F20.wireOp",EDGE,"E237"),sQuery(id+"F20.wireOp",EDGE,"E238.filletArc")])],"isStart":false})});}
            var Q9;
            {var subQ0=sQuery(id+"F20.wireOp",EDGE,"E231");var subQ1=sQuery(id+"F20.wireOp",EDGE,"E234");var subQ2=sQuery(id+"F20.wireOp",EDGE,"E235");Q9=makeQuery(id+"F26.boolean.opBoolean","SPLIT",FACE,{"disambiguationData":[TD([makeQuery(id+"F24.opExtrude","SWEPT_FACE",FACE,{"disambiguationData":[OSD([subQ1])]})])],"derivedFrom":makeQuery(id+"F24.opExtrude","CAP_FACE",FACE,{"disambiguationData":[OSD([subQ0,sQuery(id+"F20.wireOp",EDGE,"E232"),sQuery(id+"F20.wireOp",EDGE,"E233.filletArc"),subQ1,subQ2,sQuery(id+"F20.wireOp",EDGE,"E236"),sQuery(id+"F20.wireOp",EDGE,"E237"),sQuery(id+"F20.wireOp",EDGE,"E238.filletArc")])],"isStart":false})});}
            chamfer(context, id + "F34", {"entities" : qUnion([Q0, Q1, Q2, Q3, Q4, Q5, Q6, Q7, Q8, Q9]), "width" : 0.5 * mm, "tangentPropagation" : true});
        }
    });
